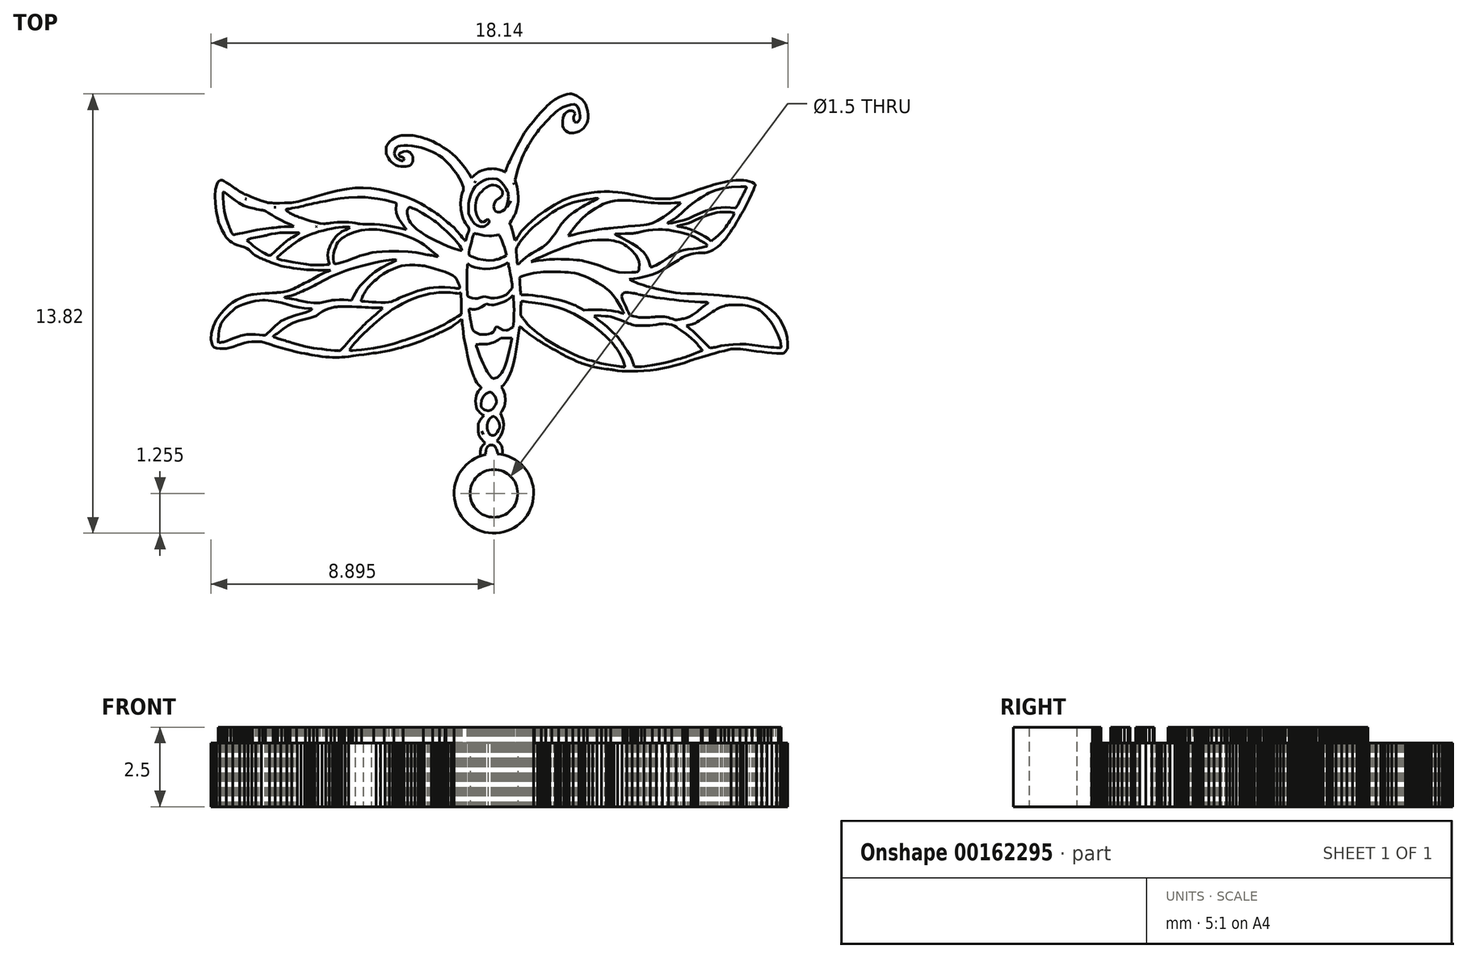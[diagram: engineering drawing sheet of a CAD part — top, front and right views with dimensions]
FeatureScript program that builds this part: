
annotation { "Feature Type Name" : "Feature", "Feature Type Description" : "" }
export const myFeature = defineFeature(function(context is Context, id is Id, definition is map)
    precondition{}
    {
        {
            var Q0;
            Q0=qCreatedBy(makeId("Top.planeOp"),FACE);
            var sketch = newSketch(context, id + "F0", { "sketchPlane" : qUnion([Q0])});
            skLineSegment(sketch, "E0", {"start": v(-0.39, -5.84) * mm, "end": v(-0.43, -5.8) * mm});
            skLineSegment(sketch, "E1", {"start": v(-0.43, -5.8) * mm, "end": v(-0.48, -5.76) * mm});
            skLineSegment(sketch, "E2", {"start": v(-0.48, -5.76) * mm, "end": v(-0.52, -5.71) * mm});
            skLineSegment(sketch, "E3", {"start": v(-0.52, -5.71) * mm, "end": v(-0.56, -5.66) * mm});
            skLineSegment(sketch, "E4", {"start": v(-0.56, -5.66) * mm, "end": v(-0.6, -5.53) * mm});
            skLineSegment(sketch, "E5", {"start": v(-0.6, -5.53) * mm, "end": v(-0.6, -5.4) * mm});
            skLineSegment(sketch, "E6", {"start": v(-0.6, -5.4) * mm, "end": v(-0.57, -5.28) * mm});
            skLineSegment(sketch, "E7", {"start": v(-0.57, -5.28) * mm, "end": v(-0.5, -5.18) * mm});
            skLineSegment(sketch, "E8", {"start": v(-0.5, -5.18) * mm, "end": v(-0.45, -5.13) * mm});
            skLineSegment(sketch, "E9", {"start": v(-0.45, -5.13) * mm, "end": v(-0.5, -5.07) * mm});
            skLineSegment(sketch, "E10", {"start": v(-0.5, -5.07) * mm, "end": v(-0.56, -5.02) * mm});
            skLineSegment(sketch, "E11", {"start": v(-0.56, -5.02) * mm, "end": v(-0.6, -4.96) * mm});
            skLineSegment(sketch, "E12", {"start": v(-0.6, -4.96) * mm, "end": v(-0.63, -4.9) * mm});
            skLineSegment(sketch, "E13", {"start": v(-0.63, -4.9) * mm, "end": v(-0.65, -4.86) * mm});
            skLineSegment(sketch, "E14", {"start": v(-0.65, -4.86) * mm, "end": v(-0.66, -4.83) * mm});
            skLineSegment(sketch, "E15", {"start": v(-0.66, -4.83) * mm, "end": v(-0.66, -4.79) * mm});
            skLineSegment(sketch, "E16", {"start": v(-0.66, -4.79) * mm, "end": v(-0.66, -4.73) * mm});
            skLineSegment(sketch, "E17", {"start": v(-0.66, -4.73) * mm, "end": v(-0.67, -4.66) * mm});
            skLineSegment(sketch, "E18", {"start": v(-0.67, -4.66) * mm, "end": v(-0.66, -4.61) * mm});
            skLineSegment(sketch, "E19", {"start": v(-0.66, -4.61) * mm, "end": v(-0.66, -4.57) * mm});
            skLineSegment(sketch, "E20", {"start": v(-0.66, -4.57) * mm, "end": v(-0.66, -4.54) * mm});
            skLineSegment(sketch, "E21", {"start": v(-0.66, -4.54) * mm, "end": v(-0.66, -4.52) * mm});
            skLineSegment(sketch, "E22", {"start": v(-0.66, -4.52) * mm, "end": v(-0.66, -4.5) * mm});
            skLineSegment(sketch, "E23", {"start": v(-0.66, -4.5) * mm, "end": v(-0.65, -4.48) * mm});
            skLineSegment(sketch, "E24", {"start": v(-0.65, -4.48) * mm, "end": v(-0.64, -4.47) * mm});
            skLineSegment(sketch, "E25", {"start": v(-0.64, -4.47) * mm, "end": v(-0.63, -4.45) * mm});
            skLineSegment(sketch, "E26", {"start": v(-0.63, -4.45) * mm, "end": v(-0.62, -4.42) * mm});
            skLineSegment(sketch, "E27", {"start": v(-0.62, -4.42) * mm, "end": v(-0.6, -4.39) * mm});
            skLineSegment(sketch, "E28", {"start": v(-0.6, -4.39) * mm, "end": v(-0.57, -4.36) * mm});
            skLineSegment(sketch, "E29", {"start": v(-0.57, -4.36) * mm, "end": v(-0.55, -4.33) * mm});
            skLineSegment(sketch, "E30", {"start": v(-0.55, -4.33) * mm, "end": v(-0.53, -4.3) * mm});
            skLineSegment(sketch, "E31", {"start": v(-0.53, -4.3) * mm, "end": v(-0.5, -4.3) * mm});
            skLineSegment(sketch, "E32", {"start": v(-0.5, -4.3) * mm, "end": v(-0.5, -4.28) * mm});
            skLineSegment(sketch, "E33", {"start": v(-0.5, -4.28) * mm, "end": v(-0.5, -4.27) * mm});
            skLineSegment(sketch, "E34", {"start": v(-0.5, -4.27) * mm, "end": v(-0.5, -4.26) * mm});
            skLineSegment(sketch, "E35", {"start": v(-0.5, -4.26) * mm, "end": v(-0.53, -4.24) * mm});
            skLineSegment(sketch, "E36", {"start": v(-0.53, -4.24) * mm, "end": v(-0.55, -4.22) * mm});
            skLineSegment(sketch, "E37", {"start": v(-0.55, -4.22) * mm, "end": v(-0.58, -4.2) * mm});
            skLineSegment(sketch, "E38", {"start": v(-0.58, -4.2) * mm, "end": v(-0.61, -4.17) * mm});
            skLineSegment(sketch, "E39", {"start": v(-0.61, -4.17) * mm, "end": v(-0.64, -4.15) * mm});
            skLineSegment(sketch, "E40", {"start": v(-0.64, -4.15) * mm, "end": v(-0.68, -4.1) * mm});
            skLineSegment(sketch, "E41", {"start": v(-0.68, -4.1) * mm, "end": v(-0.7, -4.08) * mm});
            skLineSegment(sketch, "E42", {"start": v(-0.7, -4.08) * mm, "end": v(-0.72, -4.04) * mm});
            skLineSegment(sketch, "E43", {"start": v(-0.72, -4.04) * mm, "end": v(-0.74, -4) * mm});
            skLineSegment(sketch, "E44", {"start": v(-0.74, -4) * mm, "end": v(-0.76, -3.81) * mm});
            skLineSegment(sketch, "E45", {"start": v(-0.76, -3.81) * mm, "end": v(-0.73, -3.65) * mm});
            skLineSegment(sketch, "E46", {"start": v(-0.73, -3.65) * mm, "end": v(-0.7, -3.58) * mm});
            skLineSegment(sketch, "E47", {"start": v(-0.7, -3.58) * mm, "end": v(-0.67, -3.51) * mm});
            skLineSegment(sketch, "E48", {"start": v(-0.67, -3.51) * mm, "end": v(-0.63, -3.46) * mm});
            skLineSegment(sketch, "E49", {"start": v(-0.63, -3.46) * mm, "end": v(-0.6, -3.43) * mm});
            skLineSegment(sketch, "E50", {"start": v(-0.6, -3.43) * mm, "end": v(-0.58, -3.4) * mm});
            skLineSegment(sketch, "E51", {"start": v(-0.58, -3.4) * mm, "end": v(-0.57, -3.4) * mm});
            skLineSegment(sketch, "E52", {"start": v(-0.57, -3.4) * mm, "end": v(-0.59, -3.37) * mm});
            skLineSegment(sketch, "E53", {"start": v(-0.59, -3.37) * mm, "end": v(-0.62, -3.34) * mm});
            skLineSegment(sketch, "E54", {"start": v(-0.62, -3.34) * mm, "end": v(-0.67, -3.3) * mm});
            skLineSegment(sketch, "E55", {"start": v(-0.67, -3.3) * mm, "end": v(-0.71, -3.23) * mm});
            skLineSegment(sketch, "E56", {"start": v(-0.71, -3.23) * mm, "end": v(-0.75, -3.16) * mm});
            skLineSegment(sketch, "E57", {"start": v(-0.75, -3.16) * mm, "end": v(-0.79, -3.1) * mm});
            skLineSegment(sketch, "E58", {"start": v(-0.79, -3.1) * mm, "end": v(-0.8, -3.05) * mm});
            skLineSegment(sketch, "E59", {"start": v(-0.8, -3.05) * mm, "end": v(-0.82, -3) * mm});
            skLineSegment(sketch, "E60", {"start": v(-0.82, -3) * mm, "end": v(-0.84, -2.95) * mm});
            skLineSegment(sketch, "E61", {"start": v(-0.84, -2.95) * mm, "end": v(-0.86, -2.9) * mm});
            skLineSegment(sketch, "E62", {"start": v(-0.86, -2.9) * mm, "end": v(-0.9, -2.8) * mm});
            skLineSegment(sketch, "E63", {"start": v(-0.9, -2.8) * mm, "end": v(-0.93, -2.68) * mm});
            skLineSegment(sketch, "E64", {"start": v(-0.93, -2.68) * mm, "end": v(-0.96, -2.54) * mm});
            skLineSegment(sketch, "E65", {"start": v(-0.96, -2.54) * mm, "end": v(-1, -2.36) * mm});
            skLineSegment(sketch, "E66", {"start": v(-1, -2.36) * mm, "end": v(-1.03, -2.21) * mm});
            skLineSegment(sketch, "E67", {"start": v(-1.03, -2.21) * mm, "end": v(-1.06, -2.08) * mm});
            skLineSegment(sketch, "E68", {"start": v(-1.06, -2.08) * mm, "end": v(-1.12, -1.8) * mm});
            skLineSegment(sketch, "E69", {"start": v(-1.12, -1.8) * mm, "end": v(-1.15, -1.51) * mm});
            skLineSegment(sketch, "E70", {"start": v(-1.15, -1.51) * mm, "end": v(-1.16, -1.44) * mm});
            skLineSegment(sketch, "E71", {"start": v(-1.16, -1.44) * mm, "end": v(-1.17, -1.37) * mm});
            skLineSegment(sketch, "E72", {"start": v(-1.17, -1.37) * mm, "end": v(-1.17, -1.31) * mm});
            skLineSegment(sketch, "E73", {"start": v(-1.17, -1.31) * mm, "end": v(-1.18, -1.28) * mm});
            skLineSegment(sketch, "E74", {"start": v(-1.18, -1.28) * mm, "end": v(-1.18, -1.23) * mm});
            skLineSegment(sketch, "E75", {"start": v(-1.18, -1.23) * mm, "end": v(-1.22, -1.26) * mm});
            skLineSegment(sketch, "E76", {"start": v(-1.22, -1.26) * mm, "end": v(-1.3, -1.32) * mm});
            skLineSegment(sketch, "E77", {"start": v(-1.3, -1.32) * mm, "end": v(-1.4, -1.4) * mm});
            skLineSegment(sketch, "E78", {"start": v(-1.4, -1.4) * mm, "end": v(-1.52, -1.48) * mm});
            skLineSegment(sketch, "E79", {"start": v(-1.52, -1.48) * mm, "end": v(-1.62, -1.54) * mm});
            skLineSegment(sketch, "E80", {"start": v(-1.62, -1.54) * mm, "end": v(-1.67, -1.57) * mm});
            skLineSegment(sketch, "E81", {"start": v(-1.67, -1.57) * mm, "end": v(-1.72, -1.6) * mm});
            skLineSegment(sketch, "E82", {"start": v(-1.72, -1.6) * mm, "end": v(-1.77, -1.62) * mm});
            skLineSegment(sketch, "E83", {"start": v(-1.77, -1.62) * mm, "end": v(-1.82, -1.64) * mm});
            skLineSegment(sketch, "E84", {"start": v(-1.82, -1.64) * mm, "end": v(-1.87, -1.66) * mm});
            skLineSegment(sketch, "E85", {"start": v(-1.87, -1.66) * mm, "end": v(-1.91, -1.68) * mm});
            skLineSegment(sketch, "E86", {"start": v(-1.91, -1.68) * mm, "end": v(-1.96, -1.7) * mm});
            skLineSegment(sketch, "E87", {"start": v(-1.96, -1.7) * mm, "end": v(-2, -1.72) * mm});
            skLineSegment(sketch, "E88", {"start": v(-2, -1.72) * mm, "end": v(-2.04, -1.74) * mm});
            skLineSegment(sketch, "E89", {"start": v(-2.04, -1.74) * mm, "end": v(-2.09, -1.76) * mm});
            skLineSegment(sketch, "E90", {"start": v(-2.09, -1.76) * mm, "end": v(-2.14, -1.79) * mm});
            skLineSegment(sketch, "E91", {"start": v(-2.14, -1.79) * mm, "end": v(-2.2, -1.8) * mm});
            skLineSegment(sketch, "E92", {"start": v(-2.2, -1.8) * mm, "end": v(-2.26, -1.83) * mm});
            skLineSegment(sketch, "E93", {"start": v(-2.26, -1.83) * mm, "end": v(-2.32, -1.86) * mm});
            skLineSegment(sketch, "E94", {"start": v(-2.32, -1.86) * mm, "end": v(-2.37, -1.88) * mm});
            skLineSegment(sketch, "E95", {"start": v(-2.37, -1.88) * mm, "end": v(-2.42, -1.9) * mm});
            skLineSegment(sketch, "E96", {"start": v(-2.42, -1.9) * mm, "end": v(-2.48, -1.93) * mm});
            skLineSegment(sketch, "E97", {"start": v(-2.48, -1.93) * mm, "end": v(-2.56, -1.96) * mm});
            skLineSegment(sketch, "E98", {"start": v(-2.56, -1.96) * mm, "end": v(-2.67, -2) * mm});
            skLineSegment(sketch, "E99", {"start": v(-2.67, -2) * mm, "end": v(-2.78, -2.03) * mm});
            skLineSegment(sketch, "E100", {"start": v(-2.78, -2.03) * mm, "end": v(-2.89, -2.07) * mm});
            skLineSegment(sketch, "E101", {"start": v(-2.89, -2.07) * mm, "end": v(-3, -2.1) * mm});
            skLineSegment(sketch, "E102", {"start": v(-3, -2.1) * mm, "end": v(-3.1, -2.13) * mm});
            skLineSegment(sketch, "E103", {"start": v(-3.1, -2.13) * mm, "end": v(-3.18, -2.15) * mm});
            skLineSegment(sketch, "E104", {"start": v(-3.18, -2.15) * mm, "end": v(-3.22, -2.16) * mm});
            skLineSegment(sketch, "E105", {"start": v(-3.22, -2.16) * mm, "end": v(-3.27, -2.17) * mm});
            skLineSegment(sketch, "E106", {"start": v(-3.27, -2.17) * mm, "end": v(-3.31, -2.18) * mm});
            skLineSegment(sketch, "E107", {"start": v(-3.31, -2.18) * mm, "end": v(-3.35, -2.2) * mm});
            skLineSegment(sketch, "E108", {"start": v(-3.35, -2.2) * mm, "end": v(-3.46, -2.22) * mm});
            skLineSegment(sketch, "E109", {"start": v(-3.46, -2.22) * mm, "end": v(-3.6, -2.25) * mm});
            skLineSegment(sketch, "E110", {"start": v(-3.6, -2.25) * mm, "end": v(-3.74, -2.27) * mm});
            skLineSegment(sketch, "E111", {"start": v(-3.74, -2.27) * mm, "end": v(-3.88, -2.3) * mm});
            skLineSegment(sketch, "E112", {"start": v(-3.88, -2.3) * mm, "end": v(-3.97, -2.3) * mm});
            skLineSegment(sketch, "E113", {"start": v(-3.97, -2.3) * mm, "end": v(-4.1, -2.32) * mm});
            skLineSegment(sketch, "E114", {"start": v(-4.1, -2.32) * mm, "end": v(-4.26, -2.34) * mm});
            skLineSegment(sketch, "E115", {"start": v(-4.26, -2.34) * mm, "end": v(-4.43, -2.37) * mm});
            skLineSegment(sketch, "E116", {"start": v(-4.43, -2.37) * mm, "end": v(-4.6, -2.4) * mm});
            skLineSegment(sketch, "E117", {"start": v(-4.6, -2.4) * mm, "end": v(-4.74, -2.4) * mm});
            skLineSegment(sketch, "E118", {"start": v(-4.74, -2.4) * mm, "end": v(-4.86, -2.42) * mm});
            skLineSegment(sketch, "E119", {"start": v(-4.86, -2.42) * mm, "end": v(-4.95, -2.43) * mm});
            skLineSegment(sketch, "E120", {"start": v(-4.95, -2.43) * mm, "end": v(-5.03, -2.44) * mm});
            skLineSegment(sketch, "E121", {"start": v(-5.03, -2.44) * mm, "end": v(-5.1, -2.44) * mm});
            skLineSegment(sketch, "E122", {"start": v(-5.1, -2.44) * mm, "end": v(-5.18, -2.44) * mm});
            skLineSegment(sketch, "E123", {"start": v(-5.18, -2.44) * mm, "end": v(-5.25, -2.44) * mm});
            skLineSegment(sketch, "E124", {"start": v(-5.25, -2.44) * mm, "end": v(-5.35, -2.43) * mm});
            skLineSegment(sketch, "E125", {"start": v(-5.35, -2.43) * mm, "end": v(-5.46, -2.42) * mm});
            skLineSegment(sketch, "E126", {"start": v(-5.46, -2.42) * mm, "end": v(-5.58, -2.4) * mm});
            skLineSegment(sketch, "E127", {"start": v(-5.58, -2.4) * mm, "end": v(-5.7, -2.4) * mm});
            skLineSegment(sketch, "E128", {"start": v(-5.7, -2.4) * mm, "end": v(-5.8, -2.38) * mm});
            skLineSegment(sketch, "E129", {"start": v(-5.8, -2.38) * mm, "end": v(-5.9, -2.36) * mm});
            skLineSegment(sketch, "E130", {"start": v(-5.9, -2.36) * mm, "end": v(-5.97, -2.35) * mm});
            skLineSegment(sketch, "E131", {"start": v(-5.97, -2.35) * mm, "end": v(-6, -2.34) * mm});
            skLineSegment(sketch, "E132", {"start": v(-6, -2.34) * mm, "end": v(-6.02, -2.34) * mm});
            skLineSegment(sketch, "E133", {"start": v(-6.02, -2.34) * mm, "end": v(-6.04, -2.33) * mm});
            skLineSegment(sketch, "E134", {"start": v(-6.04, -2.33) * mm, "end": v(-6.08, -2.32) * mm});
            skLineSegment(sketch, "E135", {"start": v(-6.08, -2.32) * mm, "end": v(-6.13, -2.32) * mm});
            skLineSegment(sketch, "E136", {"start": v(-6.13, -2.32) * mm, "end": v(-6.24, -2.3) * mm});
            skLineSegment(sketch, "E137", {"start": v(-6.24, -2.3) * mm, "end": v(-6.35, -2.27) * mm});
            skLineSegment(sketch, "E138", {"start": v(-6.35, -2.27) * mm, "end": v(-6.4, -2.26) * mm});
            skLineSegment(sketch, "E139", {"start": v(-6.4, -2.26) * mm, "end": v(-6.45, -2.25) * mm});
            skLineSegment(sketch, "E140", {"start": v(-6.45, -2.25) * mm, "end": v(-6.5, -2.23) * mm});
            skLineSegment(sketch, "E141", {"start": v(-6.5, -2.23) * mm, "end": v(-6.53, -2.23) * mm});
            skLineSegment(sketch, "E142", {"start": v(-6.53, -2.23) * mm, "end": v(-6.7, -2.19) * mm});
            skLineSegment(sketch, "E143", {"start": v(-6.7, -2.19) * mm, "end": v(-6.87, -2.14) * mm});
            skLineSegment(sketch, "E144", {"start": v(-6.87, -2.14) * mm, "end": v(-7.06, -2.08) * mm});
            skLineSegment(sketch, "E145", {"start": v(-7.06, -2.08) * mm, "end": v(-7.24, -2.02) * mm});
            skLineSegment(sketch, "E146", {"start": v(-7.24, -2.02) * mm, "end": v(-7.49, -1.94) * mm});
            skLineSegment(sketch, "E147", {"start": v(-7.49, -1.94) * mm, "end": v(-7.66, -1.94) * mm});
            skLineSegment(sketch, "E148", {"start": v(-7.66, -1.94) * mm, "end": v(-7.8, -1.94) * mm});
            skLineSegment(sketch, "E149", {"start": v(-7.8, -1.94) * mm, "end": v(-7.9, -1.96) * mm});
            skLineSegment(sketch, "E150", {"start": v(-7.9, -1.96) * mm, "end": v(-8.02, -1.98) * mm});
            skLineSegment(sketch, "E151", {"start": v(-8.02, -1.98) * mm, "end": v(-8.17, -2.03) * mm});
            skLineSegment(sketch, "E152", {"start": v(-8.17, -2.03) * mm, "end": v(-8.23, -2.05) * mm});
            skLineSegment(sketch, "E153", {"start": v(-8.23, -2.05) * mm, "end": v(-8.29, -2.07) * mm});
            skLineSegment(sketch, "E154", {"start": v(-8.29, -2.07) * mm, "end": v(-8.35, -2.1) * mm});
            skLineSegment(sketch, "E155", {"start": v(-8.35, -2.1) * mm, "end": v(-8.39, -2.1) * mm});
            skLineSegment(sketch, "E156", {"start": v(-8.39, -2.1) * mm, "end": v(-8.6, -2.16) * mm});
            skLineSegment(sketch, "E157", {"start": v(-8.6, -2.16) * mm, "end": v(-8.8, -2.16) * mm});
            skLineSegment(sketch, "E158", {"start": v(-8.8, -2.16) * mm, "end": v(-8.9, -2.15) * mm});
            skLineSegment(sketch, "E159", {"start": v(-8.9, -2.15) * mm, "end": v(-8.97, -2.12) * mm});
            skLineSegment(sketch, "E160", {"start": v(-8.97, -2.12) * mm, "end": v(-9, -2.09) * mm});
            skLineSegment(sketch, "E161", {"start": v(-9, -2.09) * mm, "end": v(-9.04, -2.04) * mm});
            skLineSegment(sketch, "E162", {"start": v(-9.04, -2.04) * mm, "end": v(-9.07, -1.87) * mm});
            skLineSegment(sketch, "E163", {"start": v(-9.07, -1.87) * mm, "end": v(-9.05, -1.67) * mm});
            skLineSegment(sketch, "E164", {"start": v(-9.05, -1.67) * mm, "end": v(-9, -1.46) * mm});
            skLineSegment(sketch, "E165", {"start": v(-9, -1.46) * mm, "end": v(-8.9, -1.26) * mm});
            skLineSegment(sketch, "E166", {"start": v(-8.9, -1.26) * mm, "end": v(-8.86, -1.2) * mm});
            skLineSegment(sketch, "E167", {"start": v(-8.86, -1.2) * mm, "end": v(-8.8, -1.12) * mm});
            skLineSegment(sketch, "E168", {"start": v(-8.8, -1.12) * mm, "end": v(-8.74, -1.04) * mm});
            skLineSegment(sketch, "E169", {"start": v(-8.74, -1.04) * mm, "end": v(-8.67, -0.96) * mm});
            skLineSegment(sketch, "E170", {"start": v(-8.67, -0.96) * mm, "end": v(-8.6, -0.88) * mm});
            skLineSegment(sketch, "E171", {"start": v(-8.6, -0.88) * mm, "end": v(-8.52, -0.8) * mm});
            skLineSegment(sketch, "E172", {"start": v(-8.52, -0.8) * mm, "end": v(-8.45, -0.75) * mm});
            skLineSegment(sketch, "E173", {"start": v(-8.45, -0.75) * mm, "end": v(-8.4, -0.7) * mm});
            skLineSegment(sketch, "E174", {"start": v(-8.4, -0.7) * mm, "end": v(-8.27, -0.64) * mm});
            skLineSegment(sketch, "E175", {"start": v(-8.27, -0.64) * mm, "end": v(-8.1, -0.56) * mm});
            skLineSegment(sketch, "E176", {"start": v(-8.1, -0.56) * mm, "end": v(-7.94, -0.5) * mm});
            skLineSegment(sketch, "E177", {"start": v(-7.94, -0.5) * mm, "end": v(-7.78, -0.46) * mm});
            skLineSegment(sketch, "E178", {"start": v(-7.78, -0.46) * mm, "end": v(-7.72, -0.45) * mm});
            skLineSegment(sketch, "E179", {"start": v(-7.72, -0.45) * mm, "end": v(-7.63, -0.44) * mm});
            skLineSegment(sketch, "E180", {"start": v(-7.63, -0.44) * mm, "end": v(-7.51, -0.43) * mm});
            skLineSegment(sketch, "E181", {"start": v(-7.51, -0.43) * mm, "end": v(-7.38, -0.43) * mm});
            skLineSegment(sketch, "E182", {"start": v(-7.38, -0.43) * mm, "end": v(-7.25, -0.42) * mm});
            skLineSegment(sketch, "E183", {"start": v(-7.25, -0.42) * mm, "end": v(-7.14, -0.41) * mm});
            skLineSegment(sketch, "E184", {"start": v(-7.14, -0.41) * mm, "end": v(-7.07, -0.4) * mm});
            skLineSegment(sketch, "E185", {"start": v(-7.07, -0.4) * mm, "end": v(-7.04, -0.4) * mm});
            skLineSegment(sketch, "E186", {"start": v(-7.04, -0.4) * mm, "end": v(-7.02, -0.4) * mm});
            skLineSegment(sketch, "E187", {"start": v(-7.02, -0.4) * mm, "end": v(-6.98, -0.4) * mm});
            skLineSegment(sketch, "E188", {"start": v(-6.98, -0.4) * mm, "end": v(-6.94, -0.4) * mm});
            skLineSegment(sketch, "E189", {"start": v(-6.94, -0.4) * mm, "end": v(-6.88, -0.39) * mm});
            skLineSegment(sketch, "E190", {"start": v(-6.88, -0.39) * mm, "end": v(-6.8, -0.38) * mm});
            skLineSegment(sketch, "E191", {"start": v(-6.8, -0.38) * mm, "end": v(-6.74, -0.37) * mm});
            skLineSegment(sketch, "E192", {"start": v(-6.74, -0.37) * mm, "end": v(-6.68, -0.36) * mm});
            skLineSegment(sketch, "E193", {"start": v(-6.68, -0.36) * mm, "end": v(-6.6, -0.33) * mm});
            skLineSegment(sketch, "E194", {"start": v(-6.6, -0.33) * mm, "end": v(-6.55, -0.3) * mm});
            skLineSegment(sketch, "E195", {"start": v(-6.55, -0.3) * mm, "end": v(-6.47, -0.28) * mm});
            skLineSegment(sketch, "E196", {"start": v(-6.47, -0.28) * mm, "end": v(-6.4, -0.25) * mm});
            skLineSegment(sketch, "E197", {"start": v(-6.4, -0.25) * mm, "end": v(-6.34, -0.21) * mm});
            skLineSegment(sketch, "E198", {"start": v(-6.34, -0.21) * mm, "end": v(-6.27, -0.18) * mm});
            skLineSegment(sketch, "E199", {"start": v(-6.27, -0.18) * mm, "end": v(-6.2, -0.14) * mm});
            skLineSegment(sketch, "E200", {"start": v(-6.2, -0.14) * mm, "end": v(-6.13, -0.1) * mm});
            skLineSegment(sketch, "E201", {"start": v(-6.13, -0.1) * mm, "end": v(-6.08, -0.08) * mm});
            skLineSegment(sketch, "E202", {"start": v(-6.08, -0.08) * mm, "end": v(-6.02, -0.05) * mm});
            skLineSegment(sketch, "E203", {"start": v(-6.02, -0.05) * mm, "end": v(-5.95, 0) * mm});
            skLineSegment(sketch, "E204", {"start": v(-5.95, 0) * mm, "end": v(-5.88, 0.03) * mm});
            skLineSegment(sketch, "E205", {"start": v(-5.88, 0.03) * mm, "end": v(-5.8, 0.07) * mm});
            skLineSegment(sketch, "E206", {"start": v(-5.8, 0.07) * mm, "end": v(-5.69, 0.13) * mm});
            skLineSegment(sketch, "E207", {"start": v(-5.69, 0.13) * mm, "end": v(-5.58, 0.19) * mm});
            skLineSegment(sketch, "E208", {"start": v(-5.58, 0.19) * mm, "end": v(-5.48, 0.23) * mm});
            skLineSegment(sketch, "E209", {"start": v(-5.48, 0.23) * mm, "end": v(-5.4, 0.27) * mm});
            skLineSegment(sketch, "E210", {"start": v(-5.4, 0.27) * mm, "end": v(-5.36, 0.28) * mm});
            skLineSegment(sketch, "E211", {"start": v(-5.36, 0.28) * mm, "end": v(-5.34, 0.29) * mm});
            skLineSegment(sketch, "E212", {"start": v(-5.34, 0.29) * mm, "end": v(-5.32, 0.3) * mm});
            skLineSegment(sketch, "E213", {"start": v(-5.32, 0.3) * mm, "end": v(-5.32, 0.3) * mm});
            skLineSegment(sketch, "E214", {"start": v(-5.32, 0.3) * mm, "end": v(-5.34, 0.3) * mm});
            skLineSegment(sketch, "E215", {"start": v(-5.34, 0.3) * mm, "end": v(-5.4, 0.3) * mm});
            skLineSegment(sketch, "E216", {"start": v(-5.4, 0.3) * mm, "end": v(-5.48, 0.3) * mm});
            skLineSegment(sketch, "E217", {"start": v(-5.48, 0.3) * mm, "end": v(-5.6, 0.3) * mm});
            skLineSegment(sketch, "E218", {"start": v(-5.6, 0.3) * mm, "end": v(-5.71, 0.3) * mm});
            skLineSegment(sketch, "E219", {"start": v(-5.71, 0.3) * mm, "end": v(-5.84, 0.31) * mm});
            skLineSegment(sketch, "E220", {"start": v(-5.84, 0.31) * mm, "end": v(-5.96, 0.32) * mm});
            skLineSegment(sketch, "E221", {"start": v(-5.96, 0.32) * mm, "end": v(-6.06, 0.32) * mm});
            skLineSegment(sketch, "E222", {"start": v(-6.06, 0.32) * mm, "end": v(-6.15, 0.33) * mm});
            skLineSegment(sketch, "E223", {"start": v(-6.15, 0.33) * mm, "end": v(-6.26, 0.34) * mm});
            skLineSegment(sketch, "E224", {"start": v(-6.26, 0.34) * mm, "end": v(-6.37, 0.35) * mm});
            skLineSegment(sketch, "E225", {"start": v(-6.37, 0.35) * mm, "end": v(-6.48, 0.37) * mm});
            skLineSegment(sketch, "E226", {"start": v(-6.48, 0.37) * mm, "end": v(-6.6, 0.39) * mm});
            skLineSegment(sketch, "E227", {"start": v(-6.6, 0.39) * mm, "end": v(-6.7, 0.4) * mm});
            skLineSegment(sketch, "E228", {"start": v(-6.7, 0.4) * mm, "end": v(-6.78, 0.42) * mm});
            skLineSegment(sketch, "E229", {"start": v(-6.78, 0.42) * mm, "end": v(-6.84, 0.43) * mm});
            skLineSegment(sketch, "E230", {"start": v(-6.84, 0.43) * mm, "end": v(-6.89, 0.45) * mm});
            skLineSegment(sketch, "E231", {"start": v(-6.89, 0.45) * mm, "end": v(-6.95, 0.47) * mm});
            skLineSegment(sketch, "E232", {"start": v(-6.95, 0.47) * mm, "end": v(-7.03, 0.5) * mm});
            skLineSegment(sketch, "E233", {"start": v(-7.03, 0.5) * mm, "end": v(-7.1, 0.52) * mm});
            skLineSegment(sketch, "E234", {"start": v(-7.1, 0.52) * mm, "end": v(-7.18, 0.55) * mm});
            skLineSegment(sketch, "E235", {"start": v(-7.18, 0.55) * mm, "end": v(-7.25, 0.58) * mm});
            skLineSegment(sketch, "E236", {"start": v(-7.25, 0.58) * mm, "end": v(-7.31, 0.6) * mm});
            skLineSegment(sketch, "E237", {"start": v(-7.31, 0.6) * mm, "end": v(-7.35, 0.62) * mm});
            skLineSegment(sketch, "E238", {"start": v(-7.35, 0.62) * mm, "end": v(-7.39, 0.63) * mm});
            skLineSegment(sketch, "E239", {"start": v(-7.39, 0.63) * mm, "end": v(-7.43, 0.65) * mm});
            skLineSegment(sketch, "E240", {"start": v(-7.43, 0.65) * mm, "end": v(-7.48, 0.67) * mm});
            skLineSegment(sketch, "E241", {"start": v(-7.48, 0.67) * mm, "end": v(-7.52, 0.69) * mm});
            skLineSegment(sketch, "E242", {"start": v(-7.52, 0.69) * mm, "end": v(-7.61, 0.73) * mm});
            skLineSegment(sketch, "E243", {"start": v(-7.61, 0.73) * mm, "end": v(-7.68, 0.77) * mm});
            skLineSegment(sketch, "E244", {"start": v(-7.68, 0.77) * mm, "end": v(-7.75, 0.82) * mm});
            skLineSegment(sketch, "E245", {"start": v(-7.75, 0.82) * mm, "end": v(-7.81, 0.88) * mm});
            skLineSegment(sketch, "E246", {"start": v(-7.81, 0.88) * mm, "end": v(-7.88, 0.95) * mm});
            skLineSegment(sketch, "E247", {"start": v(-7.88, 0.95) * mm, "end": v(-7.94, 0.99) * mm});
            skLineSegment(sketch, "E248", {"start": v(-7.94, 0.99) * mm, "end": v(-8.02, 1.02) * mm});
            skLineSegment(sketch, "E249", {"start": v(-8.02, 1.02) * mm, "end": v(-8.14, 1.06) * mm});
            skLineSegment(sketch, "E250", {"start": v(-8.14, 1.06) * mm, "end": v(-8.24, 1.1) * mm});
            skLineSegment(sketch, "E251", {"start": v(-8.24, 1.1) * mm, "end": v(-8.33, 1.13) * mm});
            skLineSegment(sketch, "E252", {"start": v(-8.33, 1.13) * mm, "end": v(-8.41, 1.18) * mm});
            skLineSegment(sketch, "E253", {"start": v(-8.41, 1.18) * mm, "end": v(-8.48, 1.22) * mm});
            skLineSegment(sketch, "E254", {"start": v(-8.48, 1.22) * mm, "end": v(-8.54, 1.28) * mm});
            skLineSegment(sketch, "E255", {"start": v(-8.54, 1.28) * mm, "end": v(-8.6, 1.35) * mm});
            skLineSegment(sketch, "E256", {"start": v(-8.6, 1.35) * mm, "end": v(-8.66, 1.45) * mm});
            skLineSegment(sketch, "E257", {"start": v(-8.66, 1.45) * mm, "end": v(-8.73, 1.57) * mm});
            skLineSegment(sketch, "E258", {"start": v(-8.73, 1.57) * mm, "end": v(-8.76, 1.64) * mm});
            skLineSegment(sketch, "E259", {"start": v(-8.76, 1.64) * mm, "end": v(-8.79, 1.7) * mm});
            skLineSegment(sketch, "E260", {"start": v(-8.79, 1.7) * mm, "end": v(-8.8, 1.75) * mm});
            skLineSegment(sketch, "E261", {"start": v(-8.8, 1.75) * mm, "end": v(-8.83, 1.8) * mm});
            skLineSegment(sketch, "E262", {"start": v(-8.83, 1.8) * mm, "end": v(-8.84, 1.87) * mm});
            skLineSegment(sketch, "E263", {"start": v(-8.84, 1.87) * mm, "end": v(-8.86, 1.95) * mm});
            skLineSegment(sketch, "E264", {"start": v(-8.86, 1.95) * mm, "end": v(-8.88, 2.05) * mm});
            skLineSegment(sketch, "E265", {"start": v(-8.88, 2.05) * mm, "end": v(-8.9, 2.17) * mm});
            skLineSegment(sketch, "E266", {"start": v(-8.9, 2.17) * mm, "end": v(-8.94, 2.41) * mm});
            skLineSegment(sketch, "E267", {"start": v(-8.94, 2.41) * mm, "end": v(-8.95, 2.64) * mm});
            skLineSegment(sketch, "E268", {"start": v(-8.95, 2.64) * mm, "end": v(-8.93, 2.84) * mm});
            skLineSegment(sketch, "E269", {"start": v(-8.93, 2.84) * mm, "end": v(-8.89, 3) * mm});
            skLineSegment(sketch, "E270", {"start": v(-8.89, 3) * mm, "end": v(-8.85, 3.07) * mm});
            skLineSegment(sketch, "E271", {"start": v(-8.85, 3.07) * mm, "end": v(-8.82, 3.11) * mm});
            skLineSegment(sketch, "E272", {"start": v(-8.82, 3.11) * mm, "end": v(-8.78, 3.13) * mm});
            skLineSegment(sketch, "E273", {"start": v(-8.78, 3.13) * mm, "end": v(-8.72, 3.13) * mm});
            skLineSegment(sketch, "E274", {"start": v(-8.72, 3.13) * mm, "end": v(-8.67, 3.1) * mm});
            skLineSegment(sketch, "E275", {"start": v(-8.67, 3.1) * mm, "end": v(-8.59, 3.06) * mm});
            skLineSegment(sketch, "E276", {"start": v(-8.59, 3.06) * mm, "end": v(-8.48, 3) * mm});
            skLineSegment(sketch, "E277", {"start": v(-8.48, 3) * mm, "end": v(-8.37, 2.92) * mm});
            skLineSegment(sketch, "E278", {"start": v(-8.37, 2.92) * mm, "end": v(-8.33, 2.89) * mm});
            skLineSegment(sketch, "E279", {"start": v(-8.33, 2.89) * mm, "end": v(-8.28, 2.85) * mm});
            skLineSegment(sketch, "E280", {"start": v(-8.28, 2.85) * mm, "end": v(-8.22, 2.82) * mm});
            skLineSegment(sketch, "E281", {"start": v(-8.22, 2.82) * mm, "end": v(-8.17, 2.78) * mm});
            skLineSegment(sketch, "E282", {"start": v(-8.17, 2.78) * mm, "end": v(-8.12, 2.75) * mm});
            skLineSegment(sketch, "E283", {"start": v(-8.12, 2.75) * mm, "end": v(-8.07, 2.72) * mm});
            skLineSegment(sketch, "E284", {"start": v(-8.07, 2.72) * mm, "end": v(-8.04, 2.7) * mm});
            skLineSegment(sketch, "E285", {"start": v(-8.04, 2.7) * mm, "end": v(-8.02, 2.7) * mm});
            skLineSegment(sketch, "E286", {"start": v(-8.02, 2.7) * mm, "end": v(-8, 2.7) * mm});
            skLineSegment(sketch, "E287", {"start": v(-8, 2.7) * mm, "end": v(-7.96, 2.67) * mm});
            skLineSegment(sketch, "E288", {"start": v(-7.96, 2.67) * mm, "end": v(-7.9, 2.65) * mm});
            skLineSegment(sketch, "E289", {"start": v(-7.9, 2.65) * mm, "end": v(-7.82, 2.61) * mm});
            skLineSegment(sketch, "E290", {"start": v(-7.82, 2.61) * mm, "end": v(-7.7, 2.56) * mm});
            skLineSegment(sketch, "E291", {"start": v(-7.7, 2.56) * mm, "end": v(-7.6, 2.52) * mm});
            skLineSegment(sketch, "E292", {"start": v(-7.6, 2.52) * mm, "end": v(-7.49, 2.49) * mm});
            skLineSegment(sketch, "E293", {"start": v(-7.49, 2.49) * mm, "end": v(-7.35, 2.45) * mm});
            skLineSegment(sketch, "E294", {"start": v(-7.35, 2.45) * mm, "end": v(-7.3, 2.44) * mm});
            skLineSegment(sketch, "E295", {"start": v(-7.3, 2.44) * mm, "end": v(-7.28, 2.43) * mm});
            skLineSegment(sketch, "E296", {"start": v(-7.28, 2.43) * mm, "end": v(-7.24, 2.42) * mm});
            skLineSegment(sketch, "E297", {"start": v(-7.24, 2.42) * mm, "end": v(-7.2, 2.42) * mm});
            skLineSegment(sketch, "E298", {"start": v(-7.2, 2.42) * mm, "end": v(-7.16, 2.42) * mm});
            skLineSegment(sketch, "E299", {"start": v(-7.16, 2.42) * mm, "end": v(-7.1, 2.42) * mm});
            skLineSegment(sketch, "E300", {"start": v(-7.1, 2.42) * mm, "end": v(-7.02, 2.42) * mm});
            skLineSegment(sketch, "E301", {"start": v(-7.02, 2.42) * mm, "end": v(-6.92, 2.42) * mm});
            skLineSegment(sketch, "E302", {"start": v(-6.92, 2.42) * mm, "end": v(-6.76, 2.42) * mm});
            skLineSegment(sketch, "E303", {"start": v(-6.76, 2.42) * mm, "end": v(-6.64, 2.42) * mm});
            skLineSegment(sketch, "E304", {"start": v(-6.64, 2.42) * mm, "end": v(-6.55, 2.43) * mm});
            skLineSegment(sketch, "E305", {"start": v(-6.55, 2.43) * mm, "end": v(-6.48, 2.44) * mm});
            skLineSegment(sketch, "E306", {"start": v(-6.48, 2.44) * mm, "end": v(-6.34, 2.46) * mm});
            skLineSegment(sketch, "E307", {"start": v(-6.34, 2.46) * mm, "end": v(-6.16, 2.5) * mm});
            skLineSegment(sketch, "E308", {"start": v(-6.16, 2.5) * mm, "end": v(-5.96, 2.56) * mm});
            skLineSegment(sketch, "E309", {"start": v(-5.96, 2.56) * mm, "end": v(-5.76, 2.62) * mm});
            skLineSegment(sketch, "E310", {"start": v(-5.76, 2.62) * mm, "end": v(-5.4, 2.73) * mm});
            skLineSegment(sketch, "E311", {"start": v(-5.4, 2.73) * mm, "end": v(-5.1, 2.8) * mm});
            skLineSegment(sketch, "E312", {"start": v(-5.1, 2.8) * mm, "end": v(-4.8, 2.86) * mm});
            skLineSegment(sketch, "E313", {"start": v(-4.8, 2.86) * mm, "end": v(-4.54, 2.9) * mm});
            skLineSegment(sketch, "E314", {"start": v(-4.54, 2.9) * mm, "end": v(-4.29, 2.9) * mm});
            skLineSegment(sketch, "E315", {"start": v(-4.29, 2.9) * mm, "end": v(-4.03, 2.88) * mm});
            skLineSegment(sketch, "E316", {"start": v(-4.03, 2.88) * mm, "end": v(-3.77, 2.84) * mm});
            skLineSegment(sketch, "E317", {"start": v(-3.77, 2.84) * mm, "end": v(-3.5, 2.78) * mm});
            skLineSegment(sketch, "E318", {"start": v(-3.5, 2.78) * mm, "end": v(-3.2, 2.7) * mm});
            skLineSegment(sketch, "E319", {"start": v(-3.2, 2.7) * mm, "end": v(-2.91, 2.6) * mm});
            skLineSegment(sketch, "E320", {"start": v(-2.91, 2.6) * mm, "end": v(-2.67, 2.5) * mm});
            skLineSegment(sketch, "E321", {"start": v(-2.67, 2.5) * mm, "end": v(-2.47, 2.4) * mm});
            skLineSegment(sketch, "E322", {"start": v(-2.47, 2.4) * mm, "end": v(-2.34, 2.32) * mm});
            skLineSegment(sketch, "E323", {"start": v(-2.34, 2.32) * mm, "end": v(-2.22, 2.25) * mm});
            skLineSegment(sketch, "E324", {"start": v(-2.22, 2.25) * mm, "end": v(-2.12, 2.19) * mm});
            skLineSegment(sketch, "E325", {"start": v(-2.12, 2.19) * mm, "end": v(-2.04, 2.14) * mm});
            skLineSegment(sketch, "E326", {"start": v(-2.04, 2.14) * mm, "end": v(-1.97, 2.09) * mm});
            skLineSegment(sketch, "E327", {"start": v(-1.97, 2.09) * mm, "end": v(-1.91, 2.04) * mm});
            skLineSegment(sketch, "E328", {"start": v(-1.91, 2.04) * mm, "end": v(-1.86, 2) * mm});
            skLineSegment(sketch, "E329", {"start": v(-1.86, 2) * mm, "end": v(-1.82, 1.97) * mm});
            skLineSegment(sketch, "E330", {"start": v(-1.82, 1.97) * mm, "end": v(-1.79, 1.94) * mm});
            skLineSegment(sketch, "E331", {"start": v(-1.79, 1.94) * mm, "end": v(-1.74, 1.9) * mm});
            skLineSegment(sketch, "E332", {"start": v(-1.74, 1.9) * mm, "end": v(-1.68, 1.85) * mm});
            skLineSegment(sketch, "E333", {"start": v(-1.68, 1.85) * mm, "end": v(-1.63, 1.8) * mm});
            skLineSegment(sketch, "E334", {"start": v(-1.63, 1.8) * mm, "end": v(-1.57, 1.76) * mm});
            skLineSegment(sketch, "E335", {"start": v(-1.57, 1.76) * mm, "end": v(-1.52, 1.72) * mm});
            skLineSegment(sketch, "E336", {"start": v(-1.52, 1.72) * mm, "end": v(-1.47, 1.68) * mm});
            skLineSegment(sketch, "E337", {"start": v(-1.47, 1.68) * mm, "end": v(-1.44, 1.66) * mm});
            skLineSegment(sketch, "E338", {"start": v(-1.44, 1.66) * mm, "end": v(-1.42, 1.63) * mm});
            skLineSegment(sketch, "E339", {"start": v(-1.42, 1.63) * mm, "end": v(-1.39, 1.6) * mm});
            skLineSegment(sketch, "E340", {"start": v(-1.39, 1.6) * mm, "end": v(-1.35, 1.55) * mm});
            skLineSegment(sketch, "E341", {"start": v(-1.35, 1.55) * mm, "end": v(-1.3, 1.5) * mm});
            skLineSegment(sketch, "E342", {"start": v(-1.3, 1.5) * mm, "end": v(-1.26, 1.44) * mm});
            skLineSegment(sketch, "E343", {"start": v(-1.26, 1.44) * mm, "end": v(-1.21, 1.39) * mm});
            skLineSegment(sketch, "E344", {"start": v(-1.21, 1.39) * mm, "end": v(-1.17, 1.34) * mm});
            skLineSegment(sketch, "E345", {"start": v(-1.17, 1.34) * mm, "end": v(-1.13, 1.3) * mm});
            skLineSegment(sketch, "E346", {"start": v(-1.13, 1.3) * mm, "end": v(-1.11, 1.26) * mm});
            skLineSegment(sketch, "E347", {"start": v(-1.11, 1.26) * mm, "end": v(-1.1, 1.24) * mm});
            skLineSegment(sketch, "E348", {"start": v(-1.1, 1.24) * mm, "end": v(-1.08, 1.23) * mm});
            skLineSegment(sketch, "E349", {"start": v(-1.08, 1.23) * mm, "end": v(-1.07, 1.23) * mm});
            skLineSegment(sketch, "E350", {"start": v(-1.07, 1.23) * mm, "end": v(-1.06, 1.25) * mm});
            skLineSegment(sketch, "E351", {"start": v(-1.06, 1.25) * mm, "end": v(-1.05, 1.28) * mm});
            skLineSegment(sketch, "E352", {"start": v(-1.05, 1.28) * mm, "end": v(-1.03, 1.33) * mm});
            skLineSegment(sketch, "E353", {"start": v(-1.03, 1.33) * mm, "end": v(-1.01, 1.4) * mm});
            skLineSegment(sketch, "E354", {"start": v(-1.01, 1.4) * mm, "end": v(-1, 1.45) * mm});
            skLineSegment(sketch, "E355", {"start": v(-1, 1.45) * mm, "end": v(-0.98, 1.51) * mm});
            skLineSegment(sketch, "E356", {"start": v(-0.98, 1.51) * mm, "end": v(-0.96, 1.56) * mm});
            skLineSegment(sketch, "E357", {"start": v(-0.96, 1.56) * mm, "end": v(-0.95, 1.6) * mm});
            skLineSegment(sketch, "E358", {"start": v(-0.95, 1.6) * mm, "end": v(-0.95, 1.61) * mm});
            skLineSegment(sketch, "E359", {"start": v(-0.95, 1.61) * mm, "end": v(-0.97, 1.64) * mm});
            skLineSegment(sketch, "E360", {"start": v(-0.97, 1.64) * mm, "end": v(-0.99, 1.67) * mm});
            skLineSegment(sketch, "E361", {"start": v(-0.99, 1.67) * mm, "end": v(-1.02, 1.72) * mm});
            skLineSegment(sketch, "E362", {"start": v(-1.02, 1.72) * mm, "end": v(-1.07, 1.79) * mm});
            skLineSegment(sketch, "E363", {"start": v(-1.07, 1.79) * mm, "end": v(-1.11, 1.85) * mm});
            skLineSegment(sketch, "E364", {"start": v(-1.11, 1.85) * mm, "end": v(-1.14, 1.9) * mm});
            skLineSegment(sketch, "E365", {"start": v(-1.14, 1.9) * mm, "end": v(-1.16, 1.98) * mm});
            skLineSegment(sketch, "E366", {"start": v(-1.16, 1.98) * mm, "end": v(-1.21, 2.2) * mm});
            skLineSegment(sketch, "E367", {"start": v(-1.21, 2.2) * mm, "end": v(-1.22, 2.42) * mm});
            skLineSegment(sketch, "E368", {"start": v(-1.22, 2.42) * mm, "end": v(-1.21, 2.51) * mm});
            skLineSegment(sketch, "E369", {"start": v(-1.21, 2.51) * mm, "end": v(-1.2, 2.62) * mm});
            skLineSegment(sketch, "E370", {"start": v(-1.2, 2.62) * mm, "end": v(-1.17, 2.73) * mm});
            skLineSegment(sketch, "E371", {"start": v(-1.17, 2.73) * mm, "end": v(-1.14, 2.82) * mm});
            skLineSegment(sketch, "E372", {"start": v(-1.14, 2.82) * mm, "end": v(-1.13, 2.85) * mm});
            skLineSegment(sketch, "E373", {"start": v(-1.13, 2.85) * mm, "end": v(-1.13, 2.88) * mm});
            skLineSegment(sketch, "E374", {"start": v(-1.13, 2.88) * mm, "end": v(-1.14, 2.92) * mm});
            skLineSegment(sketch, "E375", {"start": v(-1.14, 2.92) * mm, "end": v(-1.16, 2.98) * mm});
            skLineSegment(sketch, "E376", {"start": v(-1.16, 2.98) * mm, "end": v(-1.2, 3.09) * mm});
            skLineSegment(sketch, "E377", {"start": v(-1.2, 3.09) * mm, "end": v(-1.26, 3.2) * mm});
            skLineSegment(sketch, "E378", {"start": v(-1.26, 3.2) * mm, "end": v(-1.33, 3.31) * mm});
            skLineSegment(sketch, "E379", {"start": v(-1.33, 3.31) * mm, "end": v(-1.43, 3.44) * mm});
            skLineSegment(sketch, "E380", {"start": v(-1.43, 3.44) * mm, "end": v(-1.55, 3.6) * mm});
            skLineSegment(sketch, "E381", {"start": v(-1.55, 3.6) * mm, "end": v(-1.68, 3.74) * mm});
            skLineSegment(sketch, "E382", {"start": v(-1.68, 3.74) * mm, "end": v(-1.8, 3.84) * mm});
            skLineSegment(sketch, "E383", {"start": v(-1.8, 3.84) * mm, "end": v(-1.9, 3.91) * mm});
            skLineSegment(sketch, "E384", {"start": v(-1.9, 3.91) * mm, "end": v(-1.93, 3.93) * mm});
            skLineSegment(sketch, "E385", {"start": v(-1.93, 3.93) * mm, "end": v(-1.96, 3.95) * mm});
            skLineSegment(sketch, "E386", {"start": v(-1.96, 3.95) * mm, "end": v(-2, 3.97) * mm});
            skLineSegment(sketch, "E387", {"start": v(-2, 3.97) * mm, "end": v(-2.02, 3.99) * mm});
            skLineSegment(sketch, "E388", {"start": v(-2.02, 3.99) * mm, "end": v(-2.1, 4.03) * mm});
            skLineSegment(sketch, "E389", {"start": v(-2.1, 4.03) * mm, "end": v(-2.22, 4.08) * mm});
            skLineSegment(sketch, "E390", {"start": v(-2.22, 4.08) * mm, "end": v(-2.35, 4.13) * mm});
            skLineSegment(sketch, "E391", {"start": v(-2.35, 4.13) * mm, "end": v(-2.46, 4.16) * mm});
            skLineSegment(sketch, "E392", {"start": v(-2.46, 4.16) * mm, "end": v(-2.6, 4.2) * mm});
            skLineSegment(sketch, "E393", {"start": v(-2.6, 4.2) * mm, "end": v(-2.75, 4.22) * mm});
            skLineSegment(sketch, "E394", {"start": v(-2.75, 4.22) * mm, "end": v(-2.89, 4.23) * mm});
            skLineSegment(sketch, "E395", {"start": v(-2.89, 4.23) * mm, "end": v(-3, 4.23) * mm});
            skLineSegment(sketch, "E396", {"start": v(-3, 4.23) * mm, "end": v(-3.12, 4.22) * mm});
            skLineSegment(sketch, "E397", {"start": v(-3.12, 4.22) * mm, "end": v(-3.19, 4.2) * mm});
            skLineSegment(sketch, "E398", {"start": v(-3.19, 4.2) * mm, "end": v(-3.24, 4.16) * mm});
            skLineSegment(sketch, "E399", {"start": v(-3.24, 4.16) * mm, "end": v(-3.28, 4.1) * mm});
            skLineSegment(sketch, "E400", {"start": v(-3.28, 4.1) * mm, "end": v(-3.3, 3.97) * mm});
            skLineSegment(sketch, "E401", {"start": v(-3.3, 3.97) * mm, "end": v(-3.27, 3.87) * mm});
            skLineSegment(sketch, "E402", {"start": v(-3.27, 3.87) * mm, "end": v(-3.25, 3.85) * mm});
            skLineSegment(sketch, "E403", {"start": v(-3.25, 3.85) * mm, "end": v(-3.23, 3.83) * mm});
            skLineSegment(sketch, "E404", {"start": v(-3.23, 3.83) * mm, "end": v(-3.2, 3.8) * mm});
            skLineSegment(sketch, "E405", {"start": v(-3.2, 3.8) * mm, "end": v(-3.17, 3.79) * mm});
            skLineSegment(sketch, "E406", {"start": v(-3.17, 3.79) * mm, "end": v(-3.14, 3.77) * mm});
            skLineSegment(sketch, "E407", {"start": v(-3.14, 3.77) * mm, "end": v(-3.1, 3.76) * mm});
            skLineSegment(sketch, "E408", {"start": v(-3.1, 3.76) * mm, "end": v(-3.08, 3.75) * mm});
            skLineSegment(sketch, "E409", {"start": v(-3.08, 3.75) * mm, "end": v(-3.06, 3.74) * mm});
            skLineSegment(sketch, "E410", {"start": v(-3.06, 3.74) * mm, "end": v(-3.03, 3.75) * mm});
            skLineSegment(sketch, "E411", {"start": v(-3.03, 3.75) * mm, "end": v(-3.01, 3.77) * mm});
            skLineSegment(sketch, "E412", {"start": v(-3.01, 3.77) * mm, "end": v(-3, 3.79) * mm});
            skLineSegment(sketch, "E413", {"start": v(-3, 3.79) * mm, "end": v(-3, 3.8) * mm});
            skLineSegment(sketch, "E414", {"start": v(-3, 3.8) * mm, "end": v(-3, 3.82) * mm});
            skLineSegment(sketch, "E415", {"start": v(-3, 3.82) * mm, "end": v(-3.03, 3.84) * mm});
            skLineSegment(sketch, "E416", {"start": v(-3.03, 3.84) * mm, "end": v(-3.06, 3.86) * mm});
            skLineSegment(sketch, "E417", {"start": v(-3.06, 3.86) * mm, "end": v(-3.08, 3.87) * mm});
            skLineSegment(sketch, "E418", {"start": v(-3.08, 3.87) * mm, "end": v(-3.1, 3.87) * mm});
            skLineSegment(sketch, "E419", {"start": v(-3.1, 3.87) * mm, "end": v(-3.13, 3.9) * mm});
            skLineSegment(sketch, "E420", {"start": v(-3.13, 3.9) * mm, "end": v(-3.15, 3.91) * mm});
            skLineSegment(sketch, "E421", {"start": v(-3.15, 3.91) * mm, "end": v(-3.16, 3.94) * mm});
            skLineSegment(sketch, "E422", {"start": v(-3.16, 3.94) * mm, "end": v(-3.15, 3.96) * mm});
            skLineSegment(sketch, "E423", {"start": v(-3.15, 3.96) * mm, "end": v(-3.13, 3.99) * mm});
            skLineSegment(sketch, "E424", {"start": v(-3.13, 3.99) * mm, "end": v(-3.02, 4.04) * mm});
            skLineSegment(sketch, "E425", {"start": v(-3.02, 4.04) * mm, "end": v(-2.9, 4.05) * mm});
            skLineSegment(sketch, "E426", {"start": v(-2.9, 4.05) * mm, "end": v(-2.82, 4) * mm});
            skLineSegment(sketch, "E427", {"start": v(-2.82, 4) * mm, "end": v(-2.75, 3.92) * mm});
            skLineSegment(sketch, "E428", {"start": v(-2.75, 3.92) * mm, "end": v(-2.73, 3.89) * mm});
            skLineSegment(sketch, "E429", {"start": v(-2.73, 3.89) * mm, "end": v(-2.72, 3.86) * mm});
            skLineSegment(sketch, "E430", {"start": v(-2.72, 3.86) * mm, "end": v(-2.72, 3.83) * mm});
            skLineSegment(sketch, "E431", {"start": v(-2.72, 3.83) * mm, "end": v(-2.72, 3.8) * mm});
            skLineSegment(sketch, "E432", {"start": v(-2.72, 3.8) * mm, "end": v(-2.73, 3.74) * mm});
            skLineSegment(sketch, "E433", {"start": v(-2.73, 3.74) * mm, "end": v(-2.74, 3.7) * mm});
            skLineSegment(sketch, "E434", {"start": v(-2.74, 3.7) * mm, "end": v(-2.76, 3.65) * mm});
            skLineSegment(sketch, "E435", {"start": v(-2.76, 3.65) * mm, "end": v(-2.79, 3.62) * mm});
            skLineSegment(sketch, "E436", {"start": v(-2.79, 3.62) * mm, "end": v(-2.83, 3.6) * mm});
            skLineSegment(sketch, "E437", {"start": v(-2.83, 3.6) * mm, "end": v(-2.87, 3.58) * mm});
            skLineSegment(sketch, "E438", {"start": v(-2.87, 3.58) * mm, "end": v(-2.94, 3.57) * mm});
            skLineSegment(sketch, "E439", {"start": v(-2.94, 3.57) * mm, "end": v(-3.02, 3.56) * mm});
            skLineSegment(sketch, "E440", {"start": v(-3.02, 3.56) * mm, "end": v(-3.1, 3.57) * mm});
            skLineSegment(sketch, "E441", {"start": v(-3.1, 3.57) * mm, "end": v(-3.18, 3.58) * mm});
            skLineSegment(sketch, "E442", {"start": v(-3.18, 3.58) * mm, "end": v(-3.25, 3.6) * mm});
            skLineSegment(sketch, "E443", {"start": v(-3.25, 3.6) * mm, "end": v(-3.33, 3.66) * mm});
            skLineSegment(sketch, "E444", {"start": v(-3.33, 3.66) * mm, "end": v(-3.4, 3.7) * mm});
            skLineSegment(sketch, "E445", {"start": v(-3.4, 3.7) * mm, "end": v(-3.44, 3.75) * mm});
            skLineSegment(sketch, "E446", {"start": v(-3.44, 3.75) * mm, "end": v(-3.49, 3.82) * mm});
            skLineSegment(sketch, "E447", {"start": v(-3.49, 3.82) * mm, "end": v(-3.53, 3.9) * mm});
            skLineSegment(sketch, "E448", {"start": v(-3.53, 3.9) * mm, "end": v(-3.55, 3.94) * mm});
            skLineSegment(sketch, "E449", {"start": v(-3.55, 3.94) * mm, "end": v(-3.56, 3.98) * mm});
            skLineSegment(sketch, "E450", {"start": v(-3.56, 3.98) * mm, "end": v(-3.56, 4.02) * mm});
            skLineSegment(sketch, "E451", {"start": v(-3.56, 4.02) * mm, "end": v(-3.57, 4.08) * mm});
            skLineSegment(sketch, "E452", {"start": v(-3.57, 4.08) * mm, "end": v(-3.56, 4.14) * mm});
            skLineSegment(sketch, "E453", {"start": v(-3.56, 4.14) * mm, "end": v(-3.56, 4.18) * mm});
            skLineSegment(sketch, "E454", {"start": v(-3.56, 4.18) * mm, "end": v(-3.55, 4.21) * mm});
            skLineSegment(sketch, "E455", {"start": v(-3.55, 4.21) * mm, "end": v(-3.52, 4.25) * mm});
            skLineSegment(sketch, "E456", {"start": v(-3.52, 4.25) * mm, "end": v(-3.45, 4.34) * mm});
            skLineSegment(sketch, "E457", {"start": v(-3.45, 4.34) * mm, "end": v(-3.37, 4.41) * mm});
            skLineSegment(sketch, "E458", {"start": v(-3.37, 4.41) * mm, "end": v(-3.27, 4.48) * mm});
            skLineSegment(sketch, "E459", {"start": v(-3.27, 4.48) * mm, "end": v(-3.16, 4.53) * mm});
            skLineSegment(sketch, "E460", {"start": v(-3.16, 4.53) * mm, "end": v(-3.12, 4.54) * mm});
            skLineSegment(sketch, "E461", {"start": v(-3.12, 4.54) * mm, "end": v(-3.08, 4.55) * mm});
            skLineSegment(sketch, "E462", {"start": v(-3.08, 4.55) * mm, "end": v(-3.01, 4.55) * mm});
            skLineSegment(sketch, "E463", {"start": v(-3.01, 4.55) * mm, "end": v(-2.9, 4.55) * mm});
            skLineSegment(sketch, "E464", {"start": v(-2.9, 4.55) * mm, "end": v(-2.8, 4.55) * mm});
            skLineSegment(sketch, "E465", {"start": v(-2.8, 4.55) * mm, "end": v(-2.72, 4.54) * mm});
            skLineSegment(sketch, "E466", {"start": v(-2.72, 4.54) * mm, "end": v(-2.65, 4.53) * mm});
            skLineSegment(sketch, "E467", {"start": v(-2.65, 4.53) * mm, "end": v(-2.56, 4.5) * mm});
            skLineSegment(sketch, "E468", {"start": v(-2.56, 4.5) * mm, "end": v(-2.49, 4.49) * mm});
            skLineSegment(sketch, "E469", {"start": v(-2.49, 4.49) * mm, "end": v(-2.4, 4.47) * mm});
            skLineSegment(sketch, "E470", {"start": v(-2.4, 4.47) * mm, "end": v(-2.34, 4.44) * mm});
            skLineSegment(sketch, "E471", {"start": v(-2.34, 4.44) * mm, "end": v(-2.28, 4.43) * mm});
            skLineSegment(sketch, "E472", {"start": v(-2.28, 4.43) * mm, "end": v(-2.19, 4.4) * mm});
            skLineSegment(sketch, "E473", {"start": v(-2.19, 4.4) * mm, "end": v(-2.09, 4.35) * mm});
            skLineSegment(sketch, "E474", {"start": v(-2.09, 4.35) * mm, "end": v(-1.98, 4.3) * mm});
            skLineSegment(sketch, "E475", {"start": v(-1.98, 4.3) * mm, "end": v(-1.87, 4.24) * mm});
            skLineSegment(sketch, "E476", {"start": v(-1.87, 4.24) * mm, "end": v(-1.76, 4.17) * mm});
            skLineSegment(sketch, "E477", {"start": v(-1.76, 4.17) * mm, "end": v(-1.66, 4.1) * mm});
            skLineSegment(sketch, "E478", {"start": v(-1.66, 4.1) * mm, "end": v(-1.56, 4.03) * mm});
            skLineSegment(sketch, "E479", {"start": v(-1.56, 4.03) * mm, "end": v(-1.48, 3.97) * mm});
            skLineSegment(sketch, "E480", {"start": v(-1.48, 3.97) * mm, "end": v(-1.37, 3.87) * mm});
            skLineSegment(sketch, "E481", {"start": v(-1.37, 3.87) * mm, "end": v(-1.26, 3.74) * mm});
            skLineSegment(sketch, "E482", {"start": v(-1.26, 3.74) * mm, "end": v(-1.15, 3.61) * mm});
            skLineSegment(sketch, "E483", {"start": v(-1.15, 3.61) * mm, "end": v(-1.05, 3.48) * mm});
            skLineSegment(sketch, "E484", {"start": v(-1.05, 3.48) * mm, "end": v(-1.03, 3.45) * mm});
            skLineSegment(sketch, "E485", {"start": v(-1.03, 3.45) * mm, "end": v(-1, 3.41) * mm});
            skLineSegment(sketch, "E486", {"start": v(-1, 3.41) * mm, "end": v(-0.98, 3.38) * mm});
            skLineSegment(sketch, "E487", {"start": v(-0.98, 3.38) * mm, "end": v(-0.96, 3.34) * mm});
            skLineSegment(sketch, "E488", {"start": v(-0.96, 3.34) * mm, "end": v(-0.94, 3.3) * mm});
            skLineSegment(sketch, "E489", {"start": v(-0.94, 3.3) * mm, "end": v(-0.92, 3.28) * mm});
            skLineSegment(sketch, "E490", {"start": v(-0.92, 3.28) * mm, "end": v(-0.9, 3.25) * mm});
            skLineSegment(sketch, "E491", {"start": v(-0.9, 3.25) * mm, "end": v(-0.9, 3.24) * mm});
            skLineSegment(sketch, "E492", {"start": v(-0.9, 3.24) * mm, "end": v(-0.9, 3.22) * mm});
            skLineSegment(sketch, "E493", {"start": v(-0.9, 3.22) * mm, "end": v(-0.88, 3.21) * mm});
            skLineSegment(sketch, "E494", {"start": v(-0.88, 3.21) * mm, "end": v(-0.86, 3.22) * mm});
            skLineSegment(sketch, "E495", {"start": v(-0.86, 3.22) * mm, "end": v(-0.84, 3.25) * mm});
            skLineSegment(sketch, "E496", {"start": v(-0.84, 3.25) * mm, "end": v(-0.8, 3.3) * mm});
            skLineSegment(sketch, "E497", {"start": v(-0.8, 3.3) * mm, "end": v(-0.73, 3.34) * mm});
            skLineSegment(sketch, "E498", {"start": v(-0.73, 3.34) * mm, "end": v(-0.67, 3.39) * mm});
            skLineSegment(sketch, "E499", {"start": v(-0.67, 3.39) * mm, "end": v(-0.62, 3.42) * mm});
            skLineSegment(sketch, "E500", {"start": v(-0.62, 3.42) * mm, "end": v(-0.55, 3.44) * mm});
            skLineSegment(sketch, "E501", {"start": v(-0.55, 3.44) * mm, "end": v(-0.46, 3.47) * mm});
            skLineSegment(sketch, "E502", {"start": v(-0.46, 3.47) * mm, "end": v(-0.36, 3.49) * mm});
            skLineSegment(sketch, "E503", {"start": v(-0.36, 3.49) * mm, "end": v(-0.27, 3.5) * mm});
            skLineSegment(sketch, "E504", {"start": v(-0.27, 3.5) * mm, "end": v(-0.2, 3.5) * mm});
            skLineSegment(sketch, "E505", {"start": v(-0.2, 3.5) * mm, "end": v(-0.16, 3.5) * mm});
            skLineSegment(sketch, "E506", {"start": v(-0.16, 3.5) * mm, "end": v(-0.1, 3.5) * mm});
            skLineSegment(sketch, "E507", {"start": v(-0.1, 3.5) * mm, "end": v(-0.05, 3.48) * mm});
            skLineSegment(sketch, "E508", {"start": v(-0.05, 3.48) * mm, "end": v(0, 3.47) * mm});
            skLineSegment(sketch, "E509", {"start": v(0, 3.47) * mm, "end": v(0.04, 3.45) * mm});
            skLineSegment(sketch, "E510", {"start": v(0.04, 3.45) * mm, "end": v(0.08, 3.44) * mm});
            skLineSegment(sketch, "E511", {"start": v(0.08, 3.44) * mm, "end": v(0.11, 3.42) * mm});
            skLineSegment(sketch, "E512", {"start": v(0.11, 3.42) * mm, "end": v(0.14, 3.4) * mm});
            skLineSegment(sketch, "E513", {"start": v(0.14, 3.4) * mm, "end": v(0.16, 3.4) * mm});
            skLineSegment(sketch, "E514", {"start": v(0.16, 3.4) * mm, "end": v(0.17, 3.4) * mm});
            skLineSegment(sketch, "E515", {"start": v(0.17, 3.4) * mm, "end": v(0.18, 3.4) * mm});
            skLineSegment(sketch, "E516", {"start": v(0.18, 3.4) * mm, "end": v(0.18, 3.4) * mm});
            skLineSegment(sketch, "E517", {"start": v(0.18, 3.4) * mm, "end": v(0.2, 3.43) * mm});
            skLineSegment(sketch, "E518", {"start": v(0.2, 3.43) * mm, "end": v(0.21, 3.47) * mm});
            skLineSegment(sketch, "E519", {"start": v(0.21, 3.47) * mm, "end": v(0.23, 3.52) * mm});
            skLineSegment(sketch, "E520", {"start": v(0.23, 3.52) * mm, "end": v(0.25, 3.56) * mm});
            skLineSegment(sketch, "E521", {"start": v(0.25, 3.56) * mm, "end": v(0.27, 3.61) * mm});
            skLineSegment(sketch, "E522", {"start": v(0.27, 3.61) * mm, "end": v(0.3, 3.67) * mm});
            skLineSegment(sketch, "E523", {"start": v(0.3, 3.67) * mm, "end": v(0.32, 3.73) * mm});
            skLineSegment(sketch, "E524", {"start": v(0.32, 3.73) * mm, "end": v(0.36, 3.82) * mm});
            skLineSegment(sketch, "E525", {"start": v(0.36, 3.82) * mm, "end": v(0.41, 3.92) * mm});
            skLineSegment(sketch, "E526", {"start": v(0.41, 3.92) * mm, "end": v(0.48, 4.05) * mm});
            skLineSegment(sketch, "E527", {"start": v(0.48, 4.05) * mm, "end": v(0.55, 4.2) * mm});
            skLineSegment(sketch, "E528", {"start": v(0.55, 4.2) * mm, "end": v(0.62, 4.32) * mm});
            skLineSegment(sketch, "E529", {"start": v(0.62, 4.32) * mm, "end": v(0.68, 4.43) * mm});
            skLineSegment(sketch, "E530", {"start": v(0.68, 4.43) * mm, "end": v(0.73, 4.53) * mm});
            skLineSegment(sketch, "E531", {"start": v(0.73, 4.53) * mm, "end": v(0.79, 4.62) * mm});
            skLineSegment(sketch, "E532", {"start": v(0.79, 4.62) * mm, "end": v(0.85, 4.7) * mm});
            skLineSegment(sketch, "E533", {"start": v(0.85, 4.7) * mm, "end": v(0.91, 4.8) * mm});
            skLineSegment(sketch, "E534", {"start": v(0.91, 4.8) * mm, "end": v(0.99, 4.9) * mm});
            skLineSegment(sketch, "E535", {"start": v(0.99, 4.9) * mm, "end": v(1.07, 5) * mm});
            skLineSegment(sketch, "E536", {"start": v(1.07, 5) * mm, "end": v(1.14, 5.08) * mm});
            skLineSegment(sketch, "E537", {"start": v(1.14, 5.08) * mm, "end": v(1.21, 5.16) * mm});
            skLineSegment(sketch, "E538", {"start": v(1.21, 5.16) * mm, "end": v(1.3, 5.25) * mm});
            skLineSegment(sketch, "E539", {"start": v(1.3, 5.25) * mm, "end": v(1.37, 5.33) * mm});
            skLineSegment(sketch, "E540", {"start": v(1.37, 5.33) * mm, "end": v(1.44, 5.41) * mm});
            skLineSegment(sketch, "E541", {"start": v(1.44, 5.41) * mm, "end": v(1.51, 5.48) * mm});
            skLineSegment(sketch, "E542", {"start": v(1.51, 5.48) * mm, "end": v(1.57, 5.53) * mm});
            skLineSegment(sketch, "E543", {"start": v(1.57, 5.53) * mm, "end": v(1.61, 5.57) * mm});
            skLineSegment(sketch, "E544", {"start": v(1.61, 5.57) * mm, "end": v(1.75, 5.67) * mm});
            skLineSegment(sketch, "E545", {"start": v(1.75, 5.67) * mm, "end": v(1.89, 5.75) * mm});
            skLineSegment(sketch, "E546", {"start": v(1.89, 5.75) * mm, "end": v(2.01, 5.8) * mm});
            skLineSegment(sketch, "E547", {"start": v(2.01, 5.8) * mm, "end": v(2.13, 5.84) * mm});
            skLineSegment(sketch, "E548", {"start": v(2.13, 5.84) * mm, "end": v(2.2, 5.85) * mm});
            skLineSegment(sketch, "E549", {"start": v(2.2, 5.85) * mm, "end": v(2.27, 5.85) * mm});
            skLineSegment(sketch, "E550", {"start": v(2.27, 5.85) * mm, "end": v(2.34, 5.83) * mm});
            skLineSegment(sketch, "E551", {"start": v(2.34, 5.83) * mm, "end": v(2.43, 5.8) * mm});
            skLineSegment(sketch, "E552", {"start": v(2.43, 5.8) * mm, "end": v(2.51, 5.74) * mm});
            skLineSegment(sketch, "E553", {"start": v(2.51, 5.74) * mm, "end": v(2.6, 5.67) * mm});
            skLineSegment(sketch, "E554", {"start": v(2.6, 5.67) * mm, "end": v(2.66, 5.6) * mm});
            skLineSegment(sketch, "E555", {"start": v(2.66, 5.6) * mm, "end": v(2.7, 5.52) * mm});
            skLineSegment(sketch, "E556", {"start": v(2.7, 5.52) * mm, "end": v(2.74, 5.43) * mm});
            skLineSegment(sketch, "E557", {"start": v(2.74, 5.43) * mm, "end": v(2.77, 5.3) * mm});
            skLineSegment(sketch, "E558", {"start": v(2.77, 5.3) * mm, "end": v(2.79, 5.19) * mm});
            skLineSegment(sketch, "E559", {"start": v(2.79, 5.19) * mm, "end": v(2.8, 5.1) * mm});
            skLineSegment(sketch, "E560", {"start": v(2.8, 5.1) * mm, "end": v(2.78, 5) * mm});
            skLineSegment(sketch, "E561", {"start": v(2.78, 5) * mm, "end": v(2.75, 4.92) * mm});
            skLineSegment(sketch, "E562", {"start": v(2.75, 4.92) * mm, "end": v(2.7, 4.85) * mm});
            skLineSegment(sketch, "E563", {"start": v(2.7, 4.85) * mm, "end": v(2.65, 4.78) * mm});
            skLineSegment(sketch, "E564", {"start": v(2.65, 4.78) * mm, "end": v(2.59, 4.72) * mm});
            skLineSegment(sketch, "E565", {"start": v(2.59, 4.72) * mm, "end": v(2.51, 4.68) * mm});
            skLineSegment(sketch, "E566", {"start": v(2.51, 4.68) * mm, "end": v(2.43, 4.64) * mm});
            skLineSegment(sketch, "E567", {"start": v(2.43, 4.64) * mm, "end": v(2.34, 4.62) * mm});
            skLineSegment(sketch, "E568", {"start": v(2.34, 4.62) * mm, "end": v(2.26, 4.62) * mm});
            skLineSegment(sketch, "E569", {"start": v(2.26, 4.62) * mm, "end": v(2.2, 4.62) * mm});
            skLineSegment(sketch, "E570", {"start": v(2.2, 4.62) * mm, "end": v(2.15, 4.64) * mm});
            skLineSegment(sketch, "E571", {"start": v(2.15, 4.64) * mm, "end": v(2.1, 4.68) * mm});
            skLineSegment(sketch, "E572", {"start": v(2.1, 4.68) * mm, "end": v(2.04, 4.73) * mm});
            skLineSegment(sketch, "E573", {"start": v(2.04, 4.73) * mm, "end": v(2, 4.78) * mm});
            skLineSegment(sketch, "E574", {"start": v(2, 4.78) * mm, "end": v(2, 4.84) * mm});
            skLineSegment(sketch, "E575", {"start": v(2, 4.84) * mm, "end": v(1.99, 4.92) * mm});
            skLineSegment(sketch, "E576", {"start": v(1.99, 4.92) * mm, "end": v(1.99, 5.02) * mm});
            skLineSegment(sketch, "E577", {"start": v(1.99, 5.02) * mm, "end": v(2, 5.09) * mm});
            skLineSegment(sketch, "E578", {"start": v(2, 5.09) * mm, "end": v(2.02, 5.15) * mm});
            skLineSegment(sketch, "E579", {"start": v(2.02, 5.15) * mm, "end": v(2.05, 5.21) * mm});
            skLineSegment(sketch, "E580", {"start": v(2.05, 5.21) * mm, "end": v(2.09, 5.26) * mm});
            skLineSegment(sketch, "E581", {"start": v(2.09, 5.26) * mm, "end": v(2.14, 5.3) * mm});
            skLineSegment(sketch, "E582", {"start": v(2.14, 5.3) * mm, "end": v(2.2, 5.31) * mm});
            skLineSegment(sketch, "E583", {"start": v(2.2, 5.31) * mm, "end": v(2.25, 5.32) * mm});
            skLineSegment(sketch, "E584", {"start": v(2.25, 5.32) * mm, "end": v(2.29, 5.32) * mm});
            skLineSegment(sketch, "E585", {"start": v(2.29, 5.32) * mm, "end": v(2.32, 5.31) * mm});
            skLineSegment(sketch, "E586", {"start": v(2.32, 5.31) * mm, "end": v(2.34, 5.3) * mm});
            skLineSegment(sketch, "E587", {"start": v(2.34, 5.3) * mm, "end": v(2.36, 5.27) * mm});
            skLineSegment(sketch, "E588", {"start": v(2.36, 5.27) * mm, "end": v(2.38, 5.24) * mm});
            skLineSegment(sketch, "E589", {"start": v(2.38, 5.24) * mm, "end": v(2.36, 5.18) * mm});
            skLineSegment(sketch, "E590", {"start": v(2.36, 5.18) * mm, "end": v(2.34, 5.15) * mm});
            skLineSegment(sketch, "E591", {"start": v(2.34, 5.15) * mm, "end": v(2.33, 5.13) * mm});
            skLineSegment(sketch, "E592", {"start": v(2.33, 5.13) * mm, "end": v(2.33, 5.1) * mm});
            skLineSegment(sketch, "E593", {"start": v(2.33, 5.1) * mm, "end": v(2.33, 5.06) * mm});
            skLineSegment(sketch, "E594", {"start": v(2.33, 5.06) * mm, "end": v(2.34, 5.01) * mm});
            skLineSegment(sketch, "E595", {"start": v(2.34, 5.01) * mm, "end": v(2.36, 4.98) * mm});
            skLineSegment(sketch, "E596", {"start": v(2.36, 4.98) * mm, "end": v(2.38, 4.96) * mm});
            skLineSegment(sketch, "E597", {"start": v(2.38, 4.96) * mm, "end": v(2.42, 4.96) * mm});
            skLineSegment(sketch, "E598", {"start": v(2.42, 4.96) * mm, "end": v(2.46, 4.96) * mm});
            skLineSegment(sketch, "E599", {"start": v(2.46, 4.96) * mm, "end": v(2.49, 4.99) * mm});
            skLineSegment(sketch, "E600", {"start": v(2.49, 4.99) * mm, "end": v(2.51, 5.02) * mm});
            skLineSegment(sketch, "E601", {"start": v(2.51, 5.02) * mm, "end": v(2.53, 5.07) * mm});
            skLineSegment(sketch, "E602", {"start": v(2.53, 5.07) * mm, "end": v(2.54, 5.15) * mm});
            skLineSegment(sketch, "E603", {"start": v(2.54, 5.15) * mm, "end": v(2.53, 5.26) * mm});
            skLineSegment(sketch, "E604", {"start": v(2.53, 5.26) * mm, "end": v(2.5, 5.36) * mm});
            skLineSegment(sketch, "E605", {"start": v(2.5, 5.36) * mm, "end": v(2.46, 5.45) * mm});
            skLineSegment(sketch, "E606", {"start": v(2.46, 5.45) * mm, "end": v(2.41, 5.5) * mm});
            skLineSegment(sketch, "E607", {"start": v(2.41, 5.5) * mm, "end": v(2.35, 5.53) * mm});
            skLineSegment(sketch, "E608", {"start": v(2.35, 5.53) * mm, "end": v(2.25, 5.52) * mm});
            skLineSegment(sketch, "E609", {"start": v(2.25, 5.52) * mm, "end": v(2.12, 5.48) * mm});
            skLineSegment(sketch, "E610", {"start": v(2.12, 5.48) * mm, "end": v(2, 5.43) * mm});
            skLineSegment(sketch, "E611", {"start": v(2, 5.43) * mm, "end": v(1.91, 5.39) * mm});
            skLineSegment(sketch, "E612", {"start": v(1.91, 5.39) * mm, "end": v(1.84, 5.34) * mm});
            skLineSegment(sketch, "E613", {"start": v(1.84, 5.34) * mm, "end": v(1.75, 5.27) * mm});
            skLineSegment(sketch, "E614", {"start": v(1.75, 5.27) * mm, "end": v(1.7, 5.21) * mm});
            skLineSegment(sketch, "E615", {"start": v(1.7, 5.21) * mm, "end": v(1.62, 5.14) * mm});
            skLineSegment(sketch, "E616", {"start": v(1.62, 5.14) * mm, "end": v(1.54, 5.06) * mm});
            skLineSegment(sketch, "E617", {"start": v(1.54, 5.06) * mm, "end": v(1.46, 4.97) * mm});
            skLineSegment(sketch, "E618", {"start": v(1.46, 4.97) * mm, "end": v(1.38, 4.88) * mm});
            skLineSegment(sketch, "E619", {"start": v(1.38, 4.88) * mm, "end": v(1.3, 4.8) * mm});
            skLineSegment(sketch, "E620", {"start": v(1.3, 4.8) * mm, "end": v(1.24, 4.72) * mm});
            skLineSegment(sketch, "E621", {"start": v(1.24, 4.72) * mm, "end": v(1.2, 4.66) * mm});
            skLineSegment(sketch, "E622", {"start": v(1.2, 4.66) * mm, "end": v(1.17, 4.63) * mm});
            skLineSegment(sketch, "E623", {"start": v(1.17, 4.63) * mm, "end": v(1.15, 4.6) * mm});
            skLineSegment(sketch, "E624", {"start": v(1.15, 4.6) * mm, "end": v(1.12, 4.56) * mm});
            skLineSegment(sketch, "E625", {"start": v(1.12, 4.56) * mm, "end": v(1.1, 4.53) * mm});
            skLineSegment(sketch, "E626", {"start": v(1.1, 4.53) * mm, "end": v(1.08, 4.5) * mm});
            skLineSegment(sketch, "E627", {"start": v(1.08, 4.5) * mm, "end": v(1.05, 4.46) * mm});
            skLineSegment(sketch, "E628", {"start": v(1.05, 4.46) * mm, "end": v(1.02, 4.42) * mm});
            skLineSegment(sketch, "E629", {"start": v(1.02, 4.42) * mm, "end": v(1, 4.38) * mm});
            skLineSegment(sketch, "E630", {"start": v(1, 4.38) * mm, "end": v(0.97, 4.34) * mm});
            skLineSegment(sketch, "E631", {"start": v(0.97, 4.34) * mm, "end": v(0.95, 4.3) * mm});
            skLineSegment(sketch, "E632", {"start": v(0.95, 4.3) * mm, "end": v(0.93, 4.26) * mm});
            skLineSegment(sketch, "E633", {"start": v(0.93, 4.26) * mm, "end": v(0.91, 4.23) * mm});
            skLineSegment(sketch, "E634", {"start": v(0.91, 4.23) * mm, "end": v(0.82, 4.07) * mm});
            skLineSegment(sketch, "E635", {"start": v(0.82, 4.07) * mm, "end": v(0.75, 3.94) * mm});
            skLineSegment(sketch, "E636", {"start": v(0.75, 3.94) * mm, "end": v(0.7, 3.83) * mm});
            skLineSegment(sketch, "E637", {"start": v(0.7, 3.83) * mm, "end": v(0.66, 3.72) * mm});
            skLineSegment(sketch, "E638", {"start": v(0.66, 3.72) * mm, "end": v(0.66, 3.7) * mm});
            skLineSegment(sketch, "E639", {"start": v(0.66, 3.7) * mm, "end": v(0.64, 3.66) * mm});
            skLineSegment(sketch, "E640", {"start": v(0.64, 3.66) * mm, "end": v(0.63, 3.63) * mm});
            skLineSegment(sketch, "E641", {"start": v(0.63, 3.63) * mm, "end": v(0.62, 3.59) * mm});
            skLineSegment(sketch, "E642", {"start": v(0.62, 3.59) * mm, "end": v(0.57, 3.44) * mm});
            skLineSegment(sketch, "E643", {"start": v(0.57, 3.44) * mm, "end": v(0.51, 3.23) * mm});
            skLineSegment(sketch, "E644", {"start": v(0.51, 3.23) * mm, "end": v(0.5, 3.15) * mm});
            skLineSegment(sketch, "E645", {"start": v(0.5, 3.15) * mm, "end": v(0.52, 3.06) * mm});
            skLineSegment(sketch, "E646", {"start": v(0.52, 3.06) * mm, "end": v(0.55, 2.93) * mm});
            skLineSegment(sketch, "E647", {"start": v(0.55, 2.93) * mm, "end": v(0.58, 2.76) * mm});
            skLineSegment(sketch, "E648", {"start": v(0.58, 2.76) * mm, "end": v(0.6, 2.6) * mm});
            skLineSegment(sketch, "E649", {"start": v(0.6, 2.6) * mm, "end": v(0.6, 2.46) * mm});
            skLineSegment(sketch, "E650", {"start": v(0.6, 2.46) * mm, "end": v(0.58, 2.38) * mm});
            skLineSegment(sketch, "E651", {"start": v(0.58, 2.38) * mm, "end": v(0.55, 2.27) * mm});
            skLineSegment(sketch, "E652", {"start": v(0.55, 2.27) * mm, "end": v(0.53, 2.17) * mm});
            skLineSegment(sketch, "E653", {"start": v(0.53, 2.17) * mm, "end": v(0.5, 2.09) * mm});
            skLineSegment(sketch, "E654", {"start": v(0.5, 2.09) * mm, "end": v(0.47, 2.02) * mm});
            skLineSegment(sketch, "E655", {"start": v(0.47, 2.02) * mm, "end": v(0.43, 1.94) * mm});
            skLineSegment(sketch, "E656", {"start": v(0.43, 1.94) * mm, "end": v(0.38, 1.86) * mm});
            skLineSegment(sketch, "E657", {"start": v(0.38, 1.86) * mm, "end": v(0.34, 1.8) * mm});
            skLineSegment(sketch, "E658", {"start": v(0.34, 1.8) * mm, "end": v(0.33, 1.78) * mm});
            skLineSegment(sketch, "E659", {"start": v(0.33, 1.78) * mm, "end": v(0.32, 1.76) * mm});
            skLineSegment(sketch, "E660", {"start": v(0.32, 1.76) * mm, "end": v(0.32, 1.75) * mm});
            skLineSegment(sketch, "E661", {"start": v(0.32, 1.75) * mm, "end": v(0.33, 1.74) * mm});
            skLineSegment(sketch, "E662", {"start": v(0.33, 1.74) * mm, "end": v(0.36, 1.7) * mm});
            skLineSegment(sketch, "E663", {"start": v(0.36, 1.7) * mm, "end": v(0.4, 1.6) * mm});
            skLineSegment(sketch, "E664", {"start": v(0.4, 1.6) * mm, "end": v(0.43, 1.49) * mm});
            skLineSegment(sketch, "E665", {"start": v(0.43, 1.49) * mm, "end": v(0.46, 1.37) * mm});
            skLineSegment(sketch, "E666", {"start": v(0.46, 1.37) * mm, "end": v(0.47, 1.32) * mm});
            skLineSegment(sketch, "E667", {"start": v(0.47, 1.32) * mm, "end": v(0.48, 1.28) * mm});
            skLineSegment(sketch, "E668", {"start": v(0.48, 1.28) * mm, "end": v(0.48, 1.25) * mm});
            skLineSegment(sketch, "E669", {"start": v(0.48, 1.25) * mm, "end": v(0.49, 1.24) * mm});
            skLineSegment(sketch, "E670", {"start": v(0.49, 1.24) * mm, "end": v(0.5, 1.26) * mm});
            skLineSegment(sketch, "E671", {"start": v(0.5, 1.26) * mm, "end": v(0.56, 1.32) * mm});
            skLineSegment(sketch, "E672", {"start": v(0.56, 1.32) * mm, "end": v(0.61, 1.4) * mm});
            skLineSegment(sketch, "E673", {"start": v(0.61, 1.4) * mm, "end": v(0.66, 1.48) * mm});
            skLineSegment(sketch, "E674", {"start": v(0.66, 1.48) * mm, "end": v(0.7, 1.54) * mm});
            skLineSegment(sketch, "E675", {"start": v(0.7, 1.54) * mm, "end": v(0.78, 1.62) * mm});
            skLineSegment(sketch, "E676", {"start": v(0.78, 1.62) * mm, "end": v(0.88, 1.72) * mm});
            skLineSegment(sketch, "E677", {"start": v(0.88, 1.72) * mm, "end": v(1.02, 1.85) * mm});
            skLineSegment(sketch, "E678", {"start": v(1.02, 1.85) * mm, "end": v(1.13, 1.94) * mm});
            skLineSegment(sketch, "E679", {"start": v(1.13, 1.94) * mm, "end": v(1.21, 2.02) * mm});
            skLineSegment(sketch, "E680", {"start": v(1.21, 2.02) * mm, "end": v(1.3, 2.09) * mm});
            skLineSegment(sketch, "E681", {"start": v(1.3, 2.09) * mm, "end": v(1.42, 2.16) * mm});
            skLineSegment(sketch, "E682", {"start": v(1.42, 2.16) * mm, "end": v(1.73, 2.36) * mm});
            skLineSegment(sketch, "E683", {"start": v(1.73, 2.36) * mm, "end": v(2.02, 2.5) * mm});
            skLineSegment(sketch, "E684", {"start": v(2.02, 2.5) * mm, "end": v(2.29, 2.61) * mm});
            skLineSegment(sketch, "E685", {"start": v(2.29, 2.61) * mm, "end": v(2.54, 2.68) * mm});
            skLineSegment(sketch, "E686", {"start": v(2.54, 2.68) * mm, "end": v(2.67, 2.7) * mm});
            skLineSegment(sketch, "E687", {"start": v(2.67, 2.7) * mm, "end": v(2.81, 2.73) * mm});
            skLineSegment(sketch, "E688", {"start": v(2.81, 2.73) * mm, "end": v(2.89, 2.74) * mm});
            skLineSegment(sketch, "E689", {"start": v(2.89, 2.74) * mm, "end": v(2.98, 2.75) * mm});
            skLineSegment(sketch, "E690", {"start": v(2.98, 2.75) * mm, "end": v(3.09, 2.76) * mm});
            skLineSegment(sketch, "E691", {"start": v(3.09, 2.76) * mm, "end": v(3.18, 2.77) * mm});
            skLineSegment(sketch, "E692", {"start": v(3.18, 2.77) * mm, "end": v(3.3, 2.78) * mm});
            skLineSegment(sketch, "E693", {"start": v(3.3, 2.78) * mm, "end": v(3.38, 2.78) * mm});
            skLineSegment(sketch, "E694", {"start": v(3.38, 2.78) * mm, "end": v(3.46, 2.78) * mm});
            skLineSegment(sketch, "E695", {"start": v(3.46, 2.78) * mm, "end": v(3.56, 2.77) * mm});
            skLineSegment(sketch, "E696", {"start": v(3.56, 2.77) * mm, "end": v(3.73, 2.75) * mm});
            skLineSegment(sketch, "E697", {"start": v(3.73, 2.75) * mm, "end": v(3.86, 2.74) * mm});
            skLineSegment(sketch, "E698", {"start": v(3.86, 2.74) * mm, "end": v(3.95, 2.73) * mm});
            skLineSegment(sketch, "E699", {"start": v(3.95, 2.73) * mm, "end": v(4.03, 2.71) * mm});
            skLineSegment(sketch, "E700", {"start": v(4.03, 2.71) * mm, "end": v(4.07, 2.7) * mm});
            skLineSegment(sketch, "E701", {"start": v(4.07, 2.7) * mm, "end": v(4.12, 2.7) * mm});
            skLineSegment(sketch, "E702", {"start": v(4.12, 2.7) * mm, "end": v(4.17, 2.68) * mm});
            skLineSegment(sketch, "E703", {"start": v(4.17, 2.68) * mm, "end": v(4.21, 2.68) * mm});
            skLineSegment(sketch, "E704", {"start": v(4.21, 2.68) * mm, "end": v(4.33, 2.66) * mm});
            skLineSegment(sketch, "E705", {"start": v(4.33, 2.66) * mm, "end": v(4.46, 2.63) * mm});
            skLineSegment(sketch, "E706", {"start": v(4.46, 2.63) * mm, "end": v(4.6, 2.6) * mm});
            skLineSegment(sketch, "E707", {"start": v(4.6, 2.6) * mm, "end": v(4.73, 2.57) * mm});
            skLineSegment(sketch, "E708", {"start": v(4.73, 2.57) * mm, "end": v(4.9, 2.56) * mm});
            skLineSegment(sketch, "E709", {"start": v(4.9, 2.56) * mm, "end": v(5.08, 2.55) * mm});
            skLineSegment(sketch, "E710", {"start": v(5.08, 2.55) * mm, "end": v(5.25, 2.55) * mm});
            skLineSegment(sketch, "E711", {"start": v(5.25, 2.55) * mm, "end": v(5.37, 2.55) * mm});
            skLineSegment(sketch, "E712", {"start": v(5.37, 2.55) * mm, "end": v(5.48, 2.58) * mm});
            skLineSegment(sketch, "E713", {"start": v(5.48, 2.58) * mm, "end": v(5.62, 2.61) * mm});
            skLineSegment(sketch, "E714", {"start": v(5.62, 2.61) * mm, "end": v(5.78, 2.66) * mm});
            skLineSegment(sketch, "E715", {"start": v(5.78, 2.66) * mm, "end": v(5.95, 2.72) * mm});
            skLineSegment(sketch, "E716", {"start": v(5.95, 2.72) * mm, "end": v(6.05, 2.76) * mm});
            skLineSegment(sketch, "E717", {"start": v(6.05, 2.76) * mm, "end": v(6.15, 2.8) * mm});
            skLineSegment(sketch, "E718", {"start": v(6.15, 2.8) * mm, "end": v(6.24, 2.83) * mm});
            skLineSegment(sketch, "E719", {"start": v(6.24, 2.83) * mm, "end": v(6.3, 2.85) * mm});
            skLineSegment(sketch, "E720", {"start": v(6.3, 2.85) * mm, "end": v(6.43, 2.9) * mm});
            skLineSegment(sketch, "E721", {"start": v(6.43, 2.9) * mm, "end": v(6.55, 2.93) * mm});
            skLineSegment(sketch, "E722", {"start": v(6.55, 2.93) * mm, "end": v(6.63, 2.96) * mm});
            skLineSegment(sketch, "E723", {"start": v(6.63, 2.96) * mm, "end": v(6.74, 3) * mm});
            skLineSegment(sketch, "E724", {"start": v(6.74, 3) * mm, "end": v(6.85, 3.02) * mm});
            skLineSegment(sketch, "E725", {"start": v(6.85, 3.02) * mm, "end": v(6.96, 3.05) * mm});
            skLineSegment(sketch, "E726", {"start": v(6.96, 3.05) * mm, "end": v(7.07, 3.08) * mm});
            skLineSegment(sketch, "E727", {"start": v(7.07, 3.08) * mm, "end": v(7.17, 3.1) * mm});
            skLineSegment(sketch, "E728", {"start": v(7.17, 3.1) * mm, "end": v(7.26, 3.11) * mm});
            skLineSegment(sketch, "E729", {"start": v(7.26, 3.11) * mm, "end": v(7.33, 3.12) * mm});
            skLineSegment(sketch, "E730", {"start": v(7.33, 3.12) * mm, "end": v(7.44, 3.13) * mm});
            skLineSegment(sketch, "E731", {"start": v(7.44, 3.13) * mm, "end": v(7.57, 3.13) * mm});
            skLineSegment(sketch, "E732", {"start": v(7.57, 3.13) * mm, "end": v(7.68, 3.13) * mm});
            skLineSegment(sketch, "E733", {"start": v(7.68, 3.13) * mm, "end": v(7.77, 3.12) * mm});
            skLineSegment(sketch, "E734", {"start": v(7.77, 3.12) * mm, "end": v(7.86, 3.1) * mm});
            skLineSegment(sketch, "E735", {"start": v(7.86, 3.1) * mm, "end": v(7.94, 3.07) * mm});
            skLineSegment(sketch, "E736", {"start": v(7.94, 3.07) * mm, "end": v(8, 3.04) * mm});
            skLineSegment(sketch, "E737", {"start": v(8, 3.04) * mm, "end": v(8.04, 3) * mm});
            skLineSegment(sketch, "E738", {"start": v(8.04, 3) * mm, "end": v(8.05, 2.98) * mm});
            skLineSegment(sketch, "E739", {"start": v(8.05, 2.98) * mm, "end": v(8.04, 2.96) * mm});
            skLineSegment(sketch, "E740", {"start": v(8.04, 2.96) * mm, "end": v(8.03, 2.94) * mm});
            skLineSegment(sketch, "E741", {"start": v(8.03, 2.94) * mm, "end": v(8.02, 2.92) * mm});
            skLineSegment(sketch, "E742", {"start": v(8.02, 2.92) * mm, "end": v(8, 2.89) * mm});
            skLineSegment(sketch, "E743", {"start": v(8, 2.89) * mm, "end": v(8, 2.84) * mm});
            skLineSegment(sketch, "E744", {"start": v(8, 2.84) * mm, "end": v(7.94, 2.7) * mm});
            skLineSegment(sketch, "E745", {"start": v(7.94, 2.7) * mm, "end": v(7.86, 2.53) * mm});
            skLineSegment(sketch, "E746", {"start": v(7.86, 2.53) * mm, "end": v(7.77, 2.36) * mm});
            skLineSegment(sketch, "E747", {"start": v(7.77, 2.36) * mm, "end": v(7.67, 2.19) * mm});
            skLineSegment(sketch, "E748", {"start": v(7.67, 2.19) * mm, "end": v(7.6, 2.07) * mm});
            skLineSegment(sketch, "E749", {"start": v(7.6, 2.07) * mm, "end": v(7.55, 1.98) * mm});
            skLineSegment(sketch, "E750", {"start": v(7.55, 1.98) * mm, "end": v(7.5, 1.9) * mm});
            skLineSegment(sketch, "E751", {"start": v(7.5, 1.9) * mm, "end": v(7.47, 1.82) * mm});
            skLineSegment(sketch, "E752", {"start": v(7.47, 1.82) * mm, "end": v(7.44, 1.77) * mm});
            skLineSegment(sketch, "E753", {"start": v(7.44, 1.77) * mm, "end": v(7.4, 1.72) * mm});
            skLineSegment(sketch, "E754", {"start": v(7.4, 1.72) * mm, "end": v(7.38, 1.68) * mm});
            skLineSegment(sketch, "E755", {"start": v(7.38, 1.68) * mm, "end": v(7.36, 1.65) * mm});
            skLineSegment(sketch, "E756", {"start": v(7.36, 1.65) * mm, "end": v(7.31, 1.58) * mm});
            skLineSegment(sketch, "E757", {"start": v(7.31, 1.58) * mm, "end": v(7.26, 1.5) * mm});
            skLineSegment(sketch, "E758", {"start": v(7.26, 1.5) * mm, "end": v(7.2, 1.41) * mm});
            skLineSegment(sketch, "E759", {"start": v(7.2, 1.41) * mm, "end": v(7.16, 1.35) * mm});
            skLineSegment(sketch, "E760", {"start": v(7.16, 1.35) * mm, "end": v(7.13, 1.3) * mm});
            skLineSegment(sketch, "E761", {"start": v(7.13, 1.3) * mm, "end": v(7.07, 1.24) * mm});
            skLineSegment(sketch, "E762", {"start": v(7.07, 1.24) * mm, "end": v(7, 1.18) * mm});
            skLineSegment(sketch, "E763", {"start": v(7, 1.18) * mm, "end": v(6.94, 1.1) * mm});
            skLineSegment(sketch, "E764", {"start": v(6.94, 1.1) * mm, "end": v(6.86, 1.04) * mm});
            skLineSegment(sketch, "E765", {"start": v(6.86, 1.04) * mm, "end": v(6.79, 0.99) * mm});
            skLineSegment(sketch, "E766", {"start": v(6.79, 0.99) * mm, "end": v(6.72, 0.94) * mm});
            skLineSegment(sketch, "E767", {"start": v(6.72, 0.94) * mm, "end": v(6.66, 0.91) * mm});
            skLineSegment(sketch, "E768", {"start": v(6.66, 0.91) * mm, "end": v(6.6, 0.89) * mm});
            skLineSegment(sketch, "E769", {"start": v(6.6, 0.89) * mm, "end": v(6.52, 0.86) * mm});
            skLineSegment(sketch, "E770", {"start": v(6.52, 0.86) * mm, "end": v(6.46, 0.85) * mm});
            skLineSegment(sketch, "E771", {"start": v(6.46, 0.85) * mm, "end": v(6.43, 0.85) * mm});
            skLineSegment(sketch, "E772", {"start": v(6.43, 0.85) * mm, "end": v(6.41, 0.85) * mm});
            skLineSegment(sketch, "E773", {"start": v(6.41, 0.85) * mm, "end": v(6.37, 0.85) * mm});
            skLineSegment(sketch, "E774", {"start": v(6.37, 0.85) * mm, "end": v(6.32, 0.85) * mm});
            skLineSegment(sketch, "E775", {"start": v(6.32, 0.85) * mm, "end": v(6.26, 0.85) * mm});
            skLineSegment(sketch, "E776", {"start": v(6.26, 0.85) * mm, "end": v(6.16, 0.84) * mm});
            skLineSegment(sketch, "E777", {"start": v(6.16, 0.84) * mm, "end": v(6.1, 0.83) * mm});
            skLineSegment(sketch, "E778", {"start": v(6.1, 0.83) * mm, "end": v(6.03, 0.81) * mm});
            skLineSegment(sketch, "E779", {"start": v(6.03, 0.81) * mm, "end": v(5.95, 0.78) * mm});
            skLineSegment(sketch, "E780", {"start": v(5.95, 0.78) * mm, "end": v(5.84, 0.74) * mm});
            skLineSegment(sketch, "E781", {"start": v(5.84, 0.74) * mm, "end": v(5.76, 0.7) * mm});
            skLineSegment(sketch, "E782", {"start": v(5.76, 0.7) * mm, "end": v(5.7, 0.67) * mm});
            skLineSegment(sketch, "E783", {"start": v(5.7, 0.67) * mm, "end": v(5.63, 0.63) * mm});
            skLineSegment(sketch, "E784", {"start": v(5.63, 0.63) * mm, "end": v(5.49, 0.53) * mm});
            skLineSegment(sketch, "E785", {"start": v(5.49, 0.53) * mm, "end": v(5.32, 0.43) * mm});
            skLineSegment(sketch, "E786", {"start": v(5.32, 0.43) * mm, "end": v(5.14, 0.33) * mm});
            skLineSegment(sketch, "E787", {"start": v(5.14, 0.33) * mm, "end": v(4.96, 0.23) * mm});
            skLineSegment(sketch, "E788", {"start": v(4.96, 0.23) * mm, "end": v(4.8, 0.17) * mm});
            skLineSegment(sketch, "E789", {"start": v(4.8, 0.17) * mm, "end": v(4.6, 0.1) * mm});
            skLineSegment(sketch, "E790", {"start": v(4.6, 0.1) * mm, "end": v(4.4, 0.06) * mm});
            skLineSegment(sketch, "E791", {"start": v(4.4, 0.06) * mm, "end": v(4.23, 0.03) * mm});
            skLineSegment(sketch, "E792", {"start": v(4.23, 0.03) * mm, "end": v(4.18, 0.03) * mm});
            skLineSegment(sketch, "E793", {"start": v(4.18, 0.03) * mm, "end": v(4.14, 0.02) * mm});
            skLineSegment(sketch, "E794", {"start": v(4.14, 0.02) * mm, "end": v(4.1, 0.02) * mm});
            skLineSegment(sketch, "E795", {"start": v(4.1, 0.02) * mm, "end": v(4.1, 0.02) * mm});
            skLineSegment(sketch, "E796", {"start": v(4.1, 0.02) * mm, "end": v(4.1, 0.01) * mm});
            skLineSegment(sketch, "E797", {"start": v(4.1, 0.01) * mm, "end": v(4.12, 0) * mm});
            skLineSegment(sketch, "E798", {"start": v(4.12, 0) * mm, "end": v(4.16, -0.03) * mm});
            skLineSegment(sketch, "E799", {"start": v(4.16, -0.03) * mm, "end": v(4.22, -0.05) * mm});
            skLineSegment(sketch, "E800", {"start": v(4.22, -0.05) * mm, "end": v(4.29, -0.08) * mm});
            skLineSegment(sketch, "E801", {"start": v(4.29, -0.08) * mm, "end": v(4.37, -0.1) * mm});
            skLineSegment(sketch, "E802", {"start": v(4.37, -0.1) * mm, "end": v(4.45, -0.14) * mm});
            skLineSegment(sketch, "E803", {"start": v(4.45, -0.14) * mm, "end": v(4.54, -0.17) * mm});
            skLineSegment(sketch, "E804", {"start": v(4.54, -0.17) * mm, "end": v(4.63, -0.2) * mm});
            skLineSegment(sketch, "E805", {"start": v(4.63, -0.2) * mm, "end": v(4.7, -0.22) * mm});
            skLineSegment(sketch, "E806", {"start": v(4.7, -0.22) * mm, "end": v(4.77, -0.24) * mm});
            skLineSegment(sketch, "E807", {"start": v(4.77, -0.24) * mm, "end": v(4.85, -0.26) * mm});
            skLineSegment(sketch, "E808", {"start": v(4.85, -0.26) * mm, "end": v(4.94, -0.28) * mm});
            skLineSegment(sketch, "E809", {"start": v(4.94, -0.28) * mm, "end": v(5.06, -0.3) * mm});
            skLineSegment(sketch, "E810", {"start": v(5.06, -0.3) * mm, "end": v(5.21, -0.34) * mm});
            skLineSegment(sketch, "E811", {"start": v(5.21, -0.34) * mm, "end": v(5.41, -0.38) * mm});
            skLineSegment(sketch, "E812", {"start": v(5.41, -0.38) * mm, "end": v(5.54, -0.4) * mm});
            skLineSegment(sketch, "E813", {"start": v(5.54, -0.4) * mm, "end": v(5.7, -0.42) * mm});
            skLineSegment(sketch, "E814", {"start": v(5.7, -0.42) * mm, "end": v(5.9, -0.43) * mm});
            skLineSegment(sketch, "E815", {"start": v(5.9, -0.43) * mm, "end": v(6.14, -0.44) * mm});
            skLineSegment(sketch, "E816", {"start": v(6.14, -0.44) * mm, "end": v(6.36, -0.45) * mm});
            skLineSegment(sketch, "E817", {"start": v(6.36, -0.45) * mm, "end": v(6.55, -0.46) * mm});
            skLineSegment(sketch, "E818", {"start": v(6.55, -0.46) * mm, "end": v(6.73, -0.47) * mm});
            skLineSegment(sketch, "E819", {"start": v(6.73, -0.47) * mm, "end": v(6.92, -0.49) * mm});
            skLineSegment(sketch, "E820", {"start": v(6.92, -0.49) * mm, "end": v(7.01, -0.5) * mm});
            skLineSegment(sketch, "E821", {"start": v(7.01, -0.5) * mm, "end": v(7.12, -0.5) * mm});
            skLineSegment(sketch, "E822", {"start": v(7.12, -0.5) * mm, "end": v(7.23, -0.52) * mm});
            skLineSegment(sketch, "E823", {"start": v(7.23, -0.52) * mm, "end": v(7.32, -0.52) * mm});
            skLineSegment(sketch, "E824", {"start": v(7.32, -0.52) * mm, "end": v(7.57, -0.54) * mm});
            skLineSegment(sketch, "E825", {"start": v(7.57, -0.54) * mm, "end": v(7.79, -0.57) * mm});
            skLineSegment(sketch, "E826", {"start": v(7.79, -0.57) * mm, "end": v(7.97, -0.62) * mm});
            skLineSegment(sketch, "E827", {"start": v(7.97, -0.62) * mm, "end": v(8.12, -0.67) * mm});
            skLineSegment(sketch, "E828", {"start": v(8.12, -0.67) * mm, "end": v(8.2, -0.71) * mm});
            skLineSegment(sketch, "E829", {"start": v(8.2, -0.71) * mm, "end": v(8.29, -0.76) * mm});
            skLineSegment(sketch, "E830", {"start": v(8.29, -0.76) * mm, "end": v(8.37, -0.8) * mm});
            skLineSegment(sketch, "E831", {"start": v(8.37, -0.8) * mm, "end": v(8.42, -0.84) * mm});
            skLineSegment(sketch, "E832", {"start": v(8.42, -0.84) * mm, "end": v(8.55, -0.95) * mm});
            skLineSegment(sketch, "E833", {"start": v(8.55, -0.95) * mm, "end": v(8.67, -1.06) * mm});
            skLineSegment(sketch, "E834", {"start": v(8.67, -1.06) * mm, "end": v(8.76, -1.16) * mm});
            skLineSegment(sketch, "E835", {"start": v(8.76, -1.16) * mm, "end": v(8.83, -1.25) * mm});
            skLineSegment(sketch, "E836", {"start": v(8.83, -1.25) * mm, "end": v(8.94, -1.46) * mm});
            skLineSegment(sketch, "E837", {"start": v(8.94, -1.46) * mm, "end": v(9.01, -1.65) * mm});
            skLineSegment(sketch, "E838", {"start": v(9.01, -1.65) * mm, "end": v(9.06, -1.82) * mm});
            skLineSegment(sketch, "E839", {"start": v(9.06, -1.82) * mm, "end": v(9.07, -2) * mm});
            skLineSegment(sketch, "E840", {"start": v(9.07, -2) * mm, "end": v(9.07, -2.07) * mm});
            skLineSegment(sketch, "E841", {"start": v(9.07, -2.07) * mm, "end": v(9.06, -2.12) * mm});
            skLineSegment(sketch, "E842", {"start": v(9.06, -2.12) * mm, "end": v(9.06, -2.15) * mm});
            skLineSegment(sketch, "E843", {"start": v(9.06, -2.15) * mm, "end": v(9.05, -2.17) * mm});
            skLineSegment(sketch, "E844", {"start": v(9.05, -2.17) * mm, "end": v(9.02, -2.21) * mm});
            skLineSegment(sketch, "E845", {"start": v(9.02, -2.21) * mm, "end": v(9, -2.25) * mm});
            skLineSegment(sketch, "E846", {"start": v(9, -2.25) * mm, "end": v(8.97, -2.28) * mm});
            skLineSegment(sketch, "E847", {"start": v(8.97, -2.28) * mm, "end": v(8.95, -2.3) * mm});
            skLineSegment(sketch, "E848", {"start": v(8.95, -2.3) * mm, "end": v(8.91, -2.3) * mm});
            skLineSegment(sketch, "E849", {"start": v(8.91, -2.3) * mm, "end": v(8.83, -2.31) * mm});
            skLineSegment(sketch, "E850", {"start": v(8.83, -2.31) * mm, "end": v(8.71, -2.3) * mm});
            skLineSegment(sketch, "E851", {"start": v(8.71, -2.3) * mm, "end": v(8.57, -2.3) * mm});
            skLineSegment(sketch, "E852", {"start": v(8.57, -2.3) * mm, "end": v(8.42, -2.28) * mm});
            skLineSegment(sketch, "E853", {"start": v(8.42, -2.28) * mm, "end": v(8.25, -2.27) * mm});
            skLineSegment(sketch, "E854", {"start": v(8.25, -2.27) * mm, "end": v(8.08, -2.24) * mm});
            skLineSegment(sketch, "E855", {"start": v(8.08, -2.24) * mm, "end": v(7.92, -2.22) * mm});
            skLineSegment(sketch, "E856", {"start": v(7.92, -2.22) * mm, "end": v(7.77, -2.2) * mm});
            skLineSegment(sketch, "E857", {"start": v(7.77, -2.2) * mm, "end": v(7.66, -2.18) * mm});
            skLineSegment(sketch, "E858", {"start": v(7.66, -2.18) * mm, "end": v(7.57, -2.17) * mm});
            skLineSegment(sketch, "E859", {"start": v(7.57, -2.17) * mm, "end": v(7.47, -2.17) * mm});
            skLineSegment(sketch, "E860", {"start": v(7.47, -2.17) * mm, "end": v(7.3, -2.17) * mm});
            skLineSegment(sketch, "E861", {"start": v(7.3, -2.17) * mm, "end": v(7.06, -2.23) * mm});
            skLineSegment(sketch, "E862", {"start": v(7.06, -2.23) * mm, "end": v(7, -2.25) * mm});
            skLineSegment(sketch, "E863", {"start": v(7, -2.25) * mm, "end": v(6.92, -2.27) * mm});
            skLineSegment(sketch, "E864", {"start": v(6.92, -2.27) * mm, "end": v(6.84, -2.29) * mm});
            skLineSegment(sketch, "E865", {"start": v(6.84, -2.29) * mm, "end": v(6.76, -2.31) * mm});
            skLineSegment(sketch, "E866", {"start": v(6.76, -2.31) * mm, "end": v(6.66, -2.34) * mm});
            skLineSegment(sketch, "E867", {"start": v(6.66, -2.34) * mm, "end": v(6.55, -2.37) * mm});
            skLineSegment(sketch, "E868", {"start": v(6.55, -2.37) * mm, "end": v(6.4, -2.41) * mm});
            skLineSegment(sketch, "E869", {"start": v(6.4, -2.41) * mm, "end": v(6.24, -2.46) * mm});
            skLineSegment(sketch, "E870", {"start": v(6.24, -2.46) * mm, "end": v(6.2, -2.48) * mm});
            skLineSegment(sketch, "E871", {"start": v(6.2, -2.48) * mm, "end": v(6.14, -2.5) * mm});
            skLineSegment(sketch, "E872", {"start": v(6.14, -2.5) * mm, "end": v(6.08, -2.52) * mm});
            skLineSegment(sketch, "E873", {"start": v(6.08, -2.52) * mm, "end": v(6.02, -2.53) * mm});
            skLineSegment(sketch, "E874", {"start": v(6.02, -2.53) * mm, "end": v(5.8, -2.61) * mm});
            skLineSegment(sketch, "E875", {"start": v(5.8, -2.61) * mm, "end": v(5.55, -2.69) * mm});
            skLineSegment(sketch, "E876", {"start": v(5.55, -2.69) * mm, "end": v(5.32, -2.75) * mm});
            skLineSegment(sketch, "E877", {"start": v(5.32, -2.75) * mm, "end": v(5.13, -2.79) * mm});
            skLineSegment(sketch, "E878", {"start": v(5.13, -2.79) * mm, "end": v(4.94, -2.82) * mm});
            skLineSegment(sketch, "E879", {"start": v(4.94, -2.82) * mm, "end": v(4.74, -2.84) * mm});
            skLineSegment(sketch, "E880", {"start": v(4.74, -2.84) * mm, "end": v(4.55, -2.86) * mm});
            skLineSegment(sketch, "E881", {"start": v(4.55, -2.86) * mm, "end": v(4.36, -2.87) * mm});
            skLineSegment(sketch, "E882", {"start": v(4.36, -2.87) * mm, "end": v(4.18, -2.88) * mm});
            skLineSegment(sketch, "E883", {"start": v(4.18, -2.88) * mm, "end": v(4, -2.88) * mm});
            skLineSegment(sketch, "E884", {"start": v(4, -2.88) * mm, "end": v(3.85, -2.87) * mm});
            skLineSegment(sketch, "E885", {"start": v(3.85, -2.87) * mm, "end": v(3.72, -2.86) * mm});
            skLineSegment(sketch, "E886", {"start": v(3.72, -2.86) * mm, "end": v(3.65, -2.85) * mm});
            skLineSegment(sketch, "E887", {"start": v(3.65, -2.85) * mm, "end": v(3.6, -2.84) * mm});
            skLineSegment(sketch, "E888", {"start": v(3.6, -2.84) * mm, "end": v(3.56, -2.83) * mm});
            skLineSegment(sketch, "E889", {"start": v(3.56, -2.83) * mm, "end": v(3.54, -2.83) * mm});
            skLineSegment(sketch, "E890", {"start": v(3.54, -2.83) * mm, "end": v(3.52, -2.82) * mm});
            skLineSegment(sketch, "E891", {"start": v(3.52, -2.82) * mm, "end": v(3.48, -2.82) * mm});
            skLineSegment(sketch, "E892", {"start": v(3.48, -2.82) * mm, "end": v(3.43, -2.81) * mm});
            skLineSegment(sketch, "E893", {"start": v(3.43, -2.81) * mm, "end": v(3.36, -2.8) * mm});
            skLineSegment(sketch, "E894", {"start": v(3.36, -2.8) * mm, "end": v(3.2, -2.79) * mm});
            skLineSegment(sketch, "E895", {"start": v(3.2, -2.79) * mm, "end": v(3.06, -2.76) * mm});
            skLineSegment(sketch, "E896", {"start": v(3.06, -2.76) * mm, "end": v(2.93, -2.73) * mm});
            skLineSegment(sketch, "E897", {"start": v(2.93, -2.73) * mm, "end": v(2.82, -2.7) * mm});
            skLineSegment(sketch, "E898", {"start": v(2.82, -2.7) * mm, "end": v(2.78, -2.69) * mm});
            skLineSegment(sketch, "E899", {"start": v(2.78, -2.69) * mm, "end": v(2.73, -2.67) * mm});
            skLineSegment(sketch, "E900", {"start": v(2.73, -2.67) * mm, "end": v(2.68, -2.66) * mm});
            skLineSegment(sketch, "E901", {"start": v(2.68, -2.66) * mm, "end": v(2.64, -2.64) * mm});
            skLineSegment(sketch, "E902", {"start": v(2.64, -2.64) * mm, "end": v(2.6, -2.63) * mm});
            skLineSegment(sketch, "E903", {"start": v(2.6, -2.63) * mm, "end": v(2.55, -2.61) * mm});
            skLineSegment(sketch, "E904", {"start": v(2.55, -2.61) * mm, "end": v(2.5, -2.59) * mm});
            skLineSegment(sketch, "E905", {"start": v(2.5, -2.59) * mm, "end": v(2.44, -2.56) * mm});
            skLineSegment(sketch, "E906", {"start": v(2.44, -2.56) * mm, "end": v(2.31, -2.5) * mm});
            skLineSegment(sketch, "E907", {"start": v(2.31, -2.5) * mm, "end": v(2.2, -2.45) * mm});
            skLineSegment(sketch, "E908", {"start": v(2.2, -2.45) * mm, "end": v(2.14, -2.43) * mm});
            skLineSegment(sketch, "E909", {"start": v(2.14, -2.43) * mm, "end": v(2.08, -2.4) * mm});
            skLineSegment(sketch, "E910", {"start": v(2.08, -2.4) * mm, "end": v(2.02, -2.37) * mm});
            skLineSegment(sketch, "E911", {"start": v(2.02, -2.37) * mm, "end": v(1.98, -2.34) * mm});
            skLineSegment(sketch, "E912", {"start": v(1.98, -2.34) * mm, "end": v(1.93, -2.3) * mm});
            skLineSegment(sketch, "E913", {"start": v(1.93, -2.3) * mm, "end": v(1.85, -2.26) * mm});
            skLineSegment(sketch, "E914", {"start": v(1.85, -2.26) * mm, "end": v(1.76, -2.22) * mm});
            skLineSegment(sketch, "E915", {"start": v(1.76, -2.22) * mm, "end": v(1.67, -2.17) * mm});
            skLineSegment(sketch, "E916", {"start": v(1.67, -2.17) * mm, "end": v(1.58, -2.12) * mm});
            skLineSegment(sketch, "E917", {"start": v(1.58, -2.12) * mm, "end": v(1.5, -2.07) * mm});
            skLineSegment(sketch, "E918", {"start": v(1.5, -2.07) * mm, "end": v(1.43, -2.04) * mm});
            skLineSegment(sketch, "E919", {"start": v(1.43, -2.04) * mm, "end": v(1.4, -2) * mm});
            skLineSegment(sketch, "E920", {"start": v(1.4, -2) * mm, "end": v(1.37, -2) * mm});
            skLineSegment(sketch, "E921", {"start": v(1.37, -2) * mm, "end": v(1.34, -1.97) * mm});
            skLineSegment(sketch, "E922", {"start": v(1.34, -1.97) * mm, "end": v(1.31, -1.95) * mm});
            skLineSegment(sketch, "E923", {"start": v(1.31, -1.95) * mm, "end": v(1.3, -1.94) * mm});
            skLineSegment(sketch, "E924", {"start": v(1.3, -1.94) * mm, "end": v(1.26, -1.92) * mm});
            skLineSegment(sketch, "E925", {"start": v(1.26, -1.92) * mm, "end": v(1.2, -1.89) * mm});
            skLineSegment(sketch, "E926", {"start": v(1.2, -1.89) * mm, "end": v(1.13, -1.84) * mm});
            skLineSegment(sketch, "E927", {"start": v(1.13, -1.84) * mm, "end": v(1.06, -1.8) * mm});
            skLineSegment(sketch, "E928", {"start": v(1.06, -1.8) * mm, "end": v(0.94, -1.71) * mm});
            skLineSegment(sketch, "E929", {"start": v(0.94, -1.71) * mm, "end": v(0.85, -1.65) * mm});
            skLineSegment(sketch, "E930", {"start": v(0.85, -1.65) * mm, "end": v(0.77, -1.58) * mm});
            skLineSegment(sketch, "E931", {"start": v(0.77, -1.58) * mm, "end": v(0.69, -1.5) * mm});
            skLineSegment(sketch, "E932", {"start": v(0.69, -1.5) * mm, "end": v(0.67, -1.49) * mm});
            skLineSegment(sketch, "E933", {"start": v(0.67, -1.49) * mm, "end": v(0.65, -1.48) * mm});
            skLineSegment(sketch, "E934", {"start": v(0.65, -1.48) * mm, "end": v(0.64, -1.47) * mm});
            skLineSegment(sketch, "E935", {"start": v(0.64, -1.47) * mm, "end": v(0.63, -1.47) * mm});
            skLineSegment(sketch, "E936", {"start": v(0.63, -1.47) * mm, "end": v(0.63, -1.49) * mm});
            skLineSegment(sketch, "E937", {"start": v(0.63, -1.49) * mm, "end": v(0.62, -1.53) * mm});
            skLineSegment(sketch, "E938", {"start": v(0.62, -1.53) * mm, "end": v(0.62, -1.6) * mm});
            skLineSegment(sketch, "E939", {"start": v(0.62, -1.6) * mm, "end": v(0.6, -1.67) * mm});
            skLineSegment(sketch, "E940", {"start": v(0.6, -1.67) * mm, "end": v(0.57, -1.94) * mm});
            skLineSegment(sketch, "E941", {"start": v(0.57, -1.94) * mm, "end": v(0.53, -2.18) * mm});
            skLineSegment(sketch, "E942", {"start": v(0.53, -2.18) * mm, "end": v(0.49, -2.42) * mm});
            skLineSegment(sketch, "E943", {"start": v(0.49, -2.42) * mm, "end": v(0.43, -2.64) * mm});
            skLineSegment(sketch, "E944", {"start": v(0.43, -2.64) * mm, "end": v(0.37, -2.86) * mm});
            skLineSegment(sketch, "E945", {"start": v(0.37, -2.86) * mm, "end": v(0.3, -3.04) * mm});
            skLineSegment(sketch, "E946", {"start": v(0.3, -3.04) * mm, "end": v(0.22, -3.18) * mm});
            skLineSegment(sketch, "E947", {"start": v(0.22, -3.18) * mm, "end": v(0.13, -3.3) * mm});
            skLineSegment(sketch, "E948", {"start": v(0.13, -3.3) * mm, "end": v(0.06, -3.37) * mm});
            skLineSegment(sketch, "E949", {"start": v(0.06, -3.37) * mm, "end": v(0.1, -3.44) * mm});
            skLineSegment(sketch, "E950", {"start": v(0.1, -3.44) * mm, "end": v(0.18, -3.6) * mm});
            skLineSegment(sketch, "E951", {"start": v(0.18, -3.6) * mm, "end": v(0.2, -3.8) * mm});
            skLineSegment(sketch, "E952", {"start": v(0.2, -3.8) * mm, "end": v(0.15, -3.98) * mm});
            skLineSegment(sketch, "E953", {"start": v(0.15, -3.98) * mm, "end": v(0.07, -4.14) * mm});
            skLineSegment(sketch, "E954", {"start": v(0.07, -4.14) * mm, "end": v(0.03, -4.19) * mm});
            skLineSegment(sketch, "E955", {"start": v(0.03, -4.19) * mm, "end": v(0.06, -4.25) * mm});
            skLineSegment(sketch, "E956", {"start": v(0.06, -4.25) * mm, "end": v(0.11, -4.4) * mm});
            skLineSegment(sketch, "E957", {"start": v(0.11, -4.4) * mm, "end": v(0.13, -4.54) * mm});
            skLineSegment(sketch, "E958", {"start": v(0.13, -4.54) * mm, "end": v(0.12, -4.67) * mm});
            skLineSegment(sketch, "E959", {"start": v(0.12, -4.67) * mm, "end": v(0.09, -4.8) * mm});
            skLineSegment(sketch, "E960", {"start": v(0.09, -4.8) * mm, "end": v(0.03, -4.92) * mm});
            skLineSegment(sketch, "E961", {"start": v(0.03, -4.92) * mm, "end": v(-0.03, -5) * mm});
            skLineSegment(sketch, "E962", {"start": v(-0.03, -5) * mm, "end": v(-0.05, -5.03) * mm});
            skLineSegment(sketch, "E963", {"start": v(-0.05, -5.03) * mm, "end": v(-0.07, -5.05) * mm});
            skLineSegment(sketch, "E964", {"start": v(-0.07, -5.05) * mm, "end": v(-0.08, -5.07) * mm});
            skLineSegment(sketch, "E965", {"start": v(-0.08, -5.07) * mm, "end": v(-0.08, -5.07) * mm});
            skLineSegment(sketch, "E966", {"start": v(-0.08, -5.07) * mm, "end": v(-0.05, -5.09) * mm});
            skLineSegment(sketch, "E967", {"start": v(-0.05, -5.09) * mm, "end": v(-0.02, -5.1) * mm});
            skLineSegment(sketch, "E968", {"start": v(-0.02, -5.1) * mm, "end": v(0.01, -5.14) * mm});
            skLineSegment(sketch, "E969", {"start": v(0.01, -5.14) * mm, "end": v(0.03, -5.16) * mm});
            skLineSegment(sketch, "E970", {"start": v(0.03, -5.16) * mm, "end": v(0.07, -5.23) * mm});
            skLineSegment(sketch, "E971", {"start": v(0.07, -5.23) * mm, "end": v(0.09, -5.3) * mm});
            skLineSegment(sketch, "E972", {"start": v(0.09, -5.3) * mm, "end": v(0.1, -5.37) * mm});
            skLineSegment(sketch, "E973", {"start": v(0.1, -5.37) * mm, "end": v(0.1, -5.47) * mm});
            skLineSegment(sketch, "E974", {"start": v(0.1, -5.47) * mm, "end": v(0.1, -5.54) * mm});
            skLineSegment(sketch, "E975", {"start": v(0.1, -5.54) * mm, "end": v(0.1, -5.6) * mm});
            skLineSegment(sketch, "E976", {"start": v(0.1, -5.6) * mm, "end": v(0.09, -5.63) * mm});
            skLineSegment(sketch, "E977", {"start": v(0.09, -5.63) * mm, "end": v(0.07, -5.67) * mm});
            skLineSegment(sketch, "E978", {"start": v(0.07, -5.67) * mm, "end": v(0.06, -5.7) * mm});
            skLineSegment(sketch, "E979", {"start": v(0.06, -5.7) * mm, "end": v(0.04, -5.72) * mm});
            skLineSegment(sketch, "E980", {"start": v(0.04, -5.72) * mm, "end": v(0.02, -5.75) * mm});
            skLineSegment(sketch, "E981", {"start": v(0.02, -5.75) * mm, "end": v(0, -5.76) * mm});
            skLineSegment(sketch, "E982", {"start": v(0, -5.76) * mm, "end": v(-0.08, -5.8) * mm});
            skLineSegment(sketch, "E983", {"start": v(-0.08, -5.8) * mm, "end": v(-0.2, -5.84) * mm});
            skLineSegment(sketch, "E984", {"start": v(-0.2, -5.84) * mm, "end": v(-0.3, -5.85) * mm});
            skLineSegment(sketch, "E985", {"start": v(-0.3, -5.85) * mm, "end": v(-0.39, -5.84) * mm});
            skLineSegment(sketch, "E986", {"start": v(-0.19, -5.64) * mm, "end": v(-0.17, -5.63) * mm});
            skLineSegment(sketch, "E987", {"start": v(-0.17, -5.63) * mm, "end": v(-0.15, -5.62) * mm});
            skLineSegment(sketch, "E988", {"start": v(-0.15, -5.62) * mm, "end": v(-0.12, -5.6) * mm});
            skLineSegment(sketch, "E989", {"start": v(-0.12, -5.6) * mm, "end": v(-0.1, -5.56) * mm});
            skLineSegment(sketch, "E990", {"start": v(-0.1, -5.56) * mm, "end": v(-0.07, -5.5) * mm});
            skLineSegment(sketch, "E991", {"start": v(-0.07, -5.5) * mm, "end": v(-0.06, -5.45) * mm});
            skLineSegment(sketch, "E992", {"start": v(-0.06, -5.45) * mm, "end": v(-0.07, -5.4) * mm});
            skLineSegment(sketch, "E993", {"start": v(-0.07, -5.4) * mm, "end": v(-0.1, -5.32) * mm});
            skLineSegment(sketch, "E994", {"start": v(-0.1, -5.32) * mm, "end": v(-0.12, -5.28) * mm});
            skLineSegment(sketch, "E995", {"start": v(-0.12, -5.28) * mm, "end": v(-0.13, -5.25) * mm});
            skLineSegment(sketch, "E996", {"start": v(-0.13, -5.25) * mm, "end": v(-0.15, -5.23) * mm});
            skLineSegment(sketch, "E997", {"start": v(-0.15, -5.23) * mm, "end": v(-0.16, -5.22) * mm});
            skLineSegment(sketch, "E998", {"start": v(-0.16, -5.22) * mm, "end": v(-0.18, -5.2) * mm});
            skLineSegment(sketch, "E999", {"start": v(-0.18, -5.2) * mm, "end": v(-0.2, -5.2) * mm});
            skLineSegment(sketch, "E1000", {"start": v(-0.2, -5.2) * mm, "end": v(-0.22, -5.2) * mm});
            skLineSegment(sketch, "E1001", {"start": v(-0.22, -5.2) * mm, "end": v(-0.25, -5.2) * mm});
            skLineSegment(sketch, "E1002", {"start": v(-0.25, -5.2) * mm, "end": v(-0.3, -5.2) * mm});
            skLineSegment(sketch, "E1003", {"start": v(-0.3, -5.2) * mm, "end": v(-0.33, -5.2) * mm});
            skLineSegment(sketch, "E1004", {"start": v(-0.33, -5.2) * mm, "end": v(-0.34, -5.21) * mm});
            skLineSegment(sketch, "E1005", {"start": v(-0.34, -5.21) * mm, "end": v(-0.36, -5.23) * mm});
            skLineSegment(sketch, "E1006", {"start": v(-0.36, -5.23) * mm, "end": v(-0.4, -5.3) * mm});
            skLineSegment(sketch, "E1007", {"start": v(-0.4, -5.3) * mm, "end": v(-0.43, -5.38) * mm});
            skLineSegment(sketch, "E1008", {"start": v(-0.43, -5.38) * mm, "end": v(-0.44, -5.46) * mm});
            skLineSegment(sketch, "E1009", {"start": v(-0.44, -5.46) * mm, "end": v(-0.42, -5.53) * mm});
            skLineSegment(sketch, "E1010", {"start": v(-0.42, -5.53) * mm, "end": v(-0.4, -5.56) * mm});
            skLineSegment(sketch, "E1011", {"start": v(-0.4, -5.56) * mm, "end": v(-0.37, -5.6) * mm});
            skLineSegment(sketch, "E1012", {"start": v(-0.37, -5.6) * mm, "end": v(-0.31, -5.64) * mm});
            skLineSegment(sketch, "E1013", {"start": v(-0.31, -5.64) * mm, "end": v(-0.26, -5.66) * mm});
            skLineSegment(sketch, "E1014", {"start": v(-0.26, -5.66) * mm, "end": v(-0.22, -5.66) * mm});
            skLineSegment(sketch, "E1015", {"start": v(-0.22, -5.66) * mm, "end": v(-0.19, -5.64) * mm});
            skLineSegment(sketch, "E1016", {"start": v(-0.18, -4.89) * mm, "end": v(-0.15, -4.88) * mm});
            skLineSegment(sketch, "E1017", {"start": v(-0.15, -4.88) * mm, "end": v(-0.1, -4.84) * mm});
            skLineSegment(sketch, "E1018", {"start": v(-0.1, -4.84) * mm, "end": v(-0.07, -4.79) * mm});
            skLineSegment(sketch, "E1019", {"start": v(-0.07, -4.79) * mm, "end": v(-0.03, -4.72) * mm});
            skLineSegment(sketch, "E1020", {"start": v(-0.03, -4.72) * mm, "end": v(0, -4.68) * mm});
            skLineSegment(sketch, "E1021", {"start": v(0, -4.68) * mm, "end": v(0, -4.64) * mm});
            skLineSegment(sketch, "E1022", {"start": v(0, -4.64) * mm, "end": v(0, -4.61) * mm});
            skLineSegment(sketch, "E1023", {"start": v(0, -4.61) * mm, "end": v(0, -4.58) * mm});
            skLineSegment(sketch, "E1024", {"start": v(0, -4.58) * mm, "end": v(-0.02, -4.47) * mm});
            skLineSegment(sketch, "E1025", {"start": v(-0.02, -4.47) * mm, "end": v(-0.1, -4.36) * mm});
            skLineSegment(sketch, "E1026", {"start": v(-0.1, -4.36) * mm, "end": v(-0.14, -4.32) * mm});
            skLineSegment(sketch, "E1027", {"start": v(-0.14, -4.32) * mm, "end": v(-0.17, -4.3) * mm});
            skLineSegment(sketch, "E1028", {"start": v(-0.17, -4.3) * mm, "end": v(-0.2, -4.3) * mm});
            skLineSegment(sketch, "E1029", {"start": v(-0.2, -4.3) * mm, "end": v(-0.24, -4.31) * mm});
            skLineSegment(sketch, "E1030", {"start": v(-0.24, -4.31) * mm, "end": v(-0.3, -4.37) * mm});
            skLineSegment(sketch, "E1031", {"start": v(-0.3, -4.37) * mm, "end": v(-0.36, -4.46) * mm});
            skLineSegment(sketch, "E1032", {"start": v(-0.36, -4.46) * mm, "end": v(-0.39, -4.57) * mm});
            skLineSegment(sketch, "E1033", {"start": v(-0.39, -4.57) * mm, "end": v(-0.38, -4.68) * mm});
            skLineSegment(sketch, "E1034", {"start": v(-0.38, -4.68) * mm, "end": v(-0.37, -4.72) * mm});
            skLineSegment(sketch, "E1035", {"start": v(-0.37, -4.72) * mm, "end": v(-0.36, -4.77) * mm});
            skLineSegment(sketch, "E1036", {"start": v(-0.36, -4.77) * mm, "end": v(-0.34, -4.8) * mm});
            skLineSegment(sketch, "E1037", {"start": v(-0.34, -4.8) * mm, "end": v(-0.32, -4.84) * mm});
            skLineSegment(sketch, "E1038", {"start": v(-0.32, -4.84) * mm, "end": v(-0.3, -4.86) * mm});
            skLineSegment(sketch, "E1039", {"start": v(-0.3, -4.86) * mm, "end": v(-0.28, -4.88) * mm});
            skLineSegment(sketch, "E1040", {"start": v(-0.28, -4.88) * mm, "end": v(-0.25, -4.9) * mm});
            skLineSegment(sketch, "E1041", {"start": v(-0.25, -4.9) * mm, "end": v(-0.23, -4.9) * mm});
            skLineSegment(sketch, "E1042", {"start": v(-0.23, -4.9) * mm, "end": v(-0.2, -4.9) * mm});
            skLineSegment(sketch, "E1043", {"start": v(-0.2, -4.9) * mm, "end": v(-0.18, -4.89) * mm});
            skLineSegment(sketch, "E1044", {"start": v(-0.52, -4.81) * mm, "end": v(-0.53, -4.79) * mm});
            skLineSegment(sketch, "E1045", {"start": v(-0.53, -4.79) * mm, "end": v(-0.54, -4.77) * mm});
            skLineSegment(sketch, "E1046", {"start": v(-0.54, -4.77) * mm, "end": v(-0.55, -4.77) * mm});
            skLineSegment(sketch, "E1047", {"start": v(-0.55, -4.77) * mm, "end": v(-0.55, -4.77) * mm});
            skLineSegment(sketch, "E1048", {"start": v(-0.55, -4.77) * mm, "end": v(-0.54, -4.8) * mm});
            skLineSegment(sketch, "E1049", {"start": v(-0.54, -4.8) * mm, "end": v(-0.53, -4.82) * mm});
            skLineSegment(sketch, "E1050", {"start": v(-0.53, -4.82) * mm, "end": v(-0.52, -4.85) * mm});
            skLineSegment(sketch, "E1051", {"start": v(-0.52, -4.85) * mm, "end": v(-0.51, -4.86) * mm});
            skLineSegment(sketch, "E1052", {"start": v(-0.51, -4.86) * mm, "end": v(-0.51, -4.84) * mm});
            skLineSegment(sketch, "E1053", {"start": v(-0.51, -4.84) * mm, "end": v(-0.52, -4.81) * mm});
            skLineSegment(sketch, "E1054", {"start": v(-0.26, -4.09) * mm, "end": v(-0.22, -4.06) * mm});
            skLineSegment(sketch, "E1055", {"start": v(-0.22, -4.06) * mm, "end": v(-0.19, -4.03) * mm});
            skLineSegment(sketch, "E1056", {"start": v(-0.19, -4.03) * mm, "end": v(-0.15, -3.98) * mm});
            skLineSegment(sketch, "E1057", {"start": v(-0.15, -3.98) * mm, "end": v(-0.12, -3.92) * mm});
            skLineSegment(sketch, "E1058", {"start": v(-0.12, -3.92) * mm, "end": v(-0.1, -3.89) * mm});
            skLineSegment(sketch, "E1059", {"start": v(-0.1, -3.89) * mm, "end": v(-0.1, -3.86) * mm});
            skLineSegment(sketch, "E1060", {"start": v(-0.1, -3.86) * mm, "end": v(-0.1, -3.83) * mm});
            skLineSegment(sketch, "E1061", {"start": v(-0.1, -3.83) * mm, "end": v(-0.1, -3.8) * mm});
            skLineSegment(sketch, "E1062", {"start": v(-0.1, -3.8) * mm, "end": v(-0.13, -3.68) * mm});
            skLineSegment(sketch, "E1063", {"start": v(-0.13, -3.68) * mm, "end": v(-0.22, -3.57) * mm});
            skLineSegment(sketch, "E1064", {"start": v(-0.22, -3.57) * mm, "end": v(-0.24, -3.55) * mm});
            skLineSegment(sketch, "E1065", {"start": v(-0.24, -3.55) * mm, "end": v(-0.26, -3.54) * mm});
            skLineSegment(sketch, "E1066", {"start": v(-0.26, -3.54) * mm, "end": v(-0.29, -3.53) * mm});
            skLineSegment(sketch, "E1067", {"start": v(-0.29, -3.53) * mm, "end": v(-0.32, -3.54) * mm});
            skLineSegment(sketch, "E1068", {"start": v(-0.32, -3.54) * mm, "end": v(-0.42, -3.58) * mm});
            skLineSegment(sketch, "E1069", {"start": v(-0.42, -3.58) * mm, "end": v(-0.5, -3.66) * mm});
            skLineSegment(sketch, "E1070", {"start": v(-0.5, -3.66) * mm, "end": v(-0.56, -3.78) * mm});
            skLineSegment(sketch, "E1071", {"start": v(-0.56, -3.78) * mm, "end": v(-0.58, -3.92) * mm});
            skLineSegment(sketch, "E1072", {"start": v(-0.58, -3.92) * mm, "end": v(-0.58, -3.96) * mm});
            skLineSegment(sketch, "E1073", {"start": v(-0.58, -3.96) * mm, "end": v(-0.58, -3.98) * mm});
            skLineSegment(sketch, "E1074", {"start": v(-0.58, -3.98) * mm, "end": v(-0.57, -4) * mm});
            skLineSegment(sketch, "E1075", {"start": v(-0.57, -4) * mm, "end": v(-0.55, -4.03) * mm});
            skLineSegment(sketch, "E1076", {"start": v(-0.55, -4.03) * mm, "end": v(-0.52, -4.06) * mm});
            skLineSegment(sketch, "E1077", {"start": v(-0.52, -4.06) * mm, "end": v(-0.5, -4.08) * mm});
            skLineSegment(sketch, "E1078", {"start": v(-0.5, -4.08) * mm, "end": v(-0.46, -4.1) * mm});
            skLineSegment(sketch, "E1079", {"start": v(-0.46, -4.1) * mm, "end": v(-0.42, -4.1) * mm});
            skLineSegment(sketch, "E1080", {"start": v(-0.42, -4.1) * mm, "end": v(-0.37, -4.11) * mm});
            skLineSegment(sketch, "E1081", {"start": v(-0.37, -4.11) * mm, "end": v(-0.34, -4.11) * mm});
            skLineSegment(sketch, "E1082", {"start": v(-0.34, -4.11) * mm, "end": v(-0.3, -4.1) * mm});
            skLineSegment(sketch, "E1083", {"start": v(-0.3, -4.1) * mm, "end": v(-0.26, -4.09) * mm});
            skLineSegment(sketch, "E1084", {"start": v(-0.08, -3.08) * mm, "end": v(-0.06, -3.06) * mm});
            skLineSegment(sketch, "E1085", {"start": v(-0.06, -3.06) * mm, "end": v(-0.03, -3.04) * mm});
            skLineSegment(sketch, "E1086", {"start": v(-0.03, -3.04) * mm, "end": v(0, -3.02) * mm});
            skLineSegment(sketch, "E1087", {"start": v(0, -3.02) * mm, "end": v(0.02, -2.99) * mm});
            skLineSegment(sketch, "E1088", {"start": v(0.02, -2.99) * mm, "end": v(0.07, -2.93) * mm});
            skLineSegment(sketch, "E1089", {"start": v(0.07, -2.93) * mm, "end": v(0.11, -2.86) * mm});
            skLineSegment(sketch, "E1090", {"start": v(0.11, -2.86) * mm, "end": v(0.15, -2.78) * mm});
            skLineSegment(sketch, "E1091", {"start": v(0.15, -2.78) * mm, "end": v(0.19, -2.68) * mm});
            skLineSegment(sketch, "E1092", {"start": v(0.19, -2.68) * mm, "end": v(0.23, -2.57) * mm});
            skLineSegment(sketch, "E1093", {"start": v(0.23, -2.57) * mm, "end": v(0.26, -2.43) * mm});
            skLineSegment(sketch, "E1094", {"start": v(0.26, -2.43) * mm, "end": v(0.3, -2.26) * mm});
            skLineSegment(sketch, "E1095", {"start": v(0.3, -2.26) * mm, "end": v(0.35, -2.06) * mm});
            skLineSegment(sketch, "E1096", {"start": v(0.35, -2.06) * mm, "end": v(0.36, -1.99) * mm});
            skLineSegment(sketch, "E1097", {"start": v(0.36, -1.99) * mm, "end": v(0.38, -1.92) * mm});
            skLineSegment(sketch, "E1098", {"start": v(0.38, -1.92) * mm, "end": v(0.39, -1.87) * mm});
            skLineSegment(sketch, "E1099", {"start": v(0.39, -1.87) * mm, "end": v(0.4, -1.85) * mm});
            skLineSegment(sketch, "E1100", {"start": v(0.4, -1.85) * mm, "end": v(0.4, -1.84) * mm});
            skLineSegment(sketch, "E1101", {"start": v(0.4, -1.84) * mm, "end": v(0.4, -1.84) * mm});
            skLineSegment(sketch, "E1102", {"start": v(0.4, -1.84) * mm, "end": v(0.39, -1.83) * mm});
            skLineSegment(sketch, "E1103", {"start": v(0.39, -1.83) * mm, "end": v(0.37, -1.83) * mm});
            skLineSegment(sketch, "E1104", {"start": v(0.37, -1.83) * mm, "end": v(0.35, -1.83) * mm});
            skLineSegment(sketch, "E1105", {"start": v(0.35, -1.83) * mm, "end": v(0.32, -1.83) * mm});
            skLineSegment(sketch, "E1106", {"start": v(0.32, -1.83) * mm, "end": v(0.28, -1.83) * mm});
            skLineSegment(sketch, "E1107", {"start": v(0.28, -1.83) * mm, "end": v(0.22, -1.83) * mm});
            skLineSegment(sketch, "E1108", {"start": v(0.22, -1.83) * mm, "end": v(0.04, -1.83) * mm});
            skLineSegment(sketch, "E1109", {"start": v(0.04, -1.83) * mm, "end": v(-0.04, -1.89) * mm});
            skLineSegment(sketch, "E1110", {"start": v(-0.04, -1.89) * mm, "end": v(-0.09, -1.92) * mm});
            skLineSegment(sketch, "E1111", {"start": v(-0.09, -1.92) * mm, "end": v(-0.14, -1.94) * mm});
            skLineSegment(sketch, "E1112", {"start": v(-0.14, -1.94) * mm, "end": v(-0.19, -1.96) * mm});
            skLineSegment(sketch, "E1113", {"start": v(-0.19, -1.96) * mm, "end": v(-0.25, -1.99) * mm});
            skLineSegment(sketch, "E1114", {"start": v(-0.25, -1.99) * mm, "end": v(-0.33, -2) * mm});
            skLineSegment(sketch, "E1115", {"start": v(-0.33, -2) * mm, "end": v(-0.38, -2.02) * mm});
            skLineSegment(sketch, "E1116", {"start": v(-0.38, -2.02) * mm, "end": v(-0.45, -2.03) * mm});
            skLineSegment(sketch, "E1117", {"start": v(-0.45, -2.03) * mm, "end": v(-0.56, -2.03) * mm});
            skLineSegment(sketch, "E1118", {"start": v(-0.56, -2.03) * mm, "end": v(-0.63, -2.03) * mm});
            skLineSegment(sketch, "E1119", {"start": v(-0.63, -2.03) * mm, "end": v(-0.68, -2.03) * mm});
            skLineSegment(sketch, "E1120", {"start": v(-0.68, -2.03) * mm, "end": v(-0.72, -2.03) * mm});
            skLineSegment(sketch, "E1121", {"start": v(-0.72, -2.03) * mm, "end": v(-0.74, -2.03) * mm});
            skLineSegment(sketch, "E1122", {"start": v(-0.74, -2.03) * mm, "end": v(-0.73, -2.04) * mm});
            skLineSegment(sketch, "E1123", {"start": v(-0.73, -2.04) * mm, "end": v(-0.72, -2.08) * mm});
            skLineSegment(sketch, "E1124", {"start": v(-0.72, -2.08) * mm, "end": v(-0.7, -2.17) * mm});
            skLineSegment(sketch, "E1125", {"start": v(-0.7, -2.17) * mm, "end": v(-0.66, -2.28) * mm});
            skLineSegment(sketch, "E1126", {"start": v(-0.66, -2.28) * mm, "end": v(-0.61, -2.4) * mm});
            skLineSegment(sketch, "E1127", {"start": v(-0.61, -2.4) * mm, "end": v(-0.56, -2.52) * mm});
            skLineSegment(sketch, "E1128", {"start": v(-0.56, -2.52) * mm, "end": v(-0.51, -2.63) * mm});
            skLineSegment(sketch, "E1129", {"start": v(-0.51, -2.63) * mm, "end": v(-0.46, -2.74) * mm});
            skLineSegment(sketch, "E1130", {"start": v(-0.46, -2.74) * mm, "end": v(-0.42, -2.82) * mm});
            skLineSegment(sketch, "E1131", {"start": v(-0.42, -2.82) * mm, "end": v(-0.39, -2.88) * mm});
            skLineSegment(sketch, "E1132", {"start": v(-0.39, -2.88) * mm, "end": v(-0.36, -2.92) * mm});
            skLineSegment(sketch, "E1133", {"start": v(-0.36, -2.92) * mm, "end": v(-0.33, -2.96) * mm});
            skLineSegment(sketch, "E1134", {"start": v(-0.33, -2.96) * mm, "end": v(-0.32, -2.98) * mm});
            skLineSegment(sketch, "E1135", {"start": v(-0.32, -2.98) * mm, "end": v(-0.3, -3) * mm});
            skLineSegment(sketch, "E1136", {"start": v(-0.3, -3) * mm, "end": v(-0.3, -3.02) * mm});
            skLineSegment(sketch, "E1137", {"start": v(-0.3, -3.02) * mm, "end": v(-0.27, -3.05) * mm});
            skLineSegment(sketch, "E1138", {"start": v(-0.27, -3.05) * mm, "end": v(-0.24, -3.08) * mm});
            skLineSegment(sketch, "E1139", {"start": v(-0.24, -3.08) * mm, "end": v(-0.22, -3.1) * mm});
            skLineSegment(sketch, "E1140", {"start": v(-0.22, -3.1) * mm, "end": v(-0.2, -3.1) * mm});
            skLineSegment(sketch, "E1141", {"start": v(-0.2, -3.1) * mm, "end": v(-0.17, -3.1) * mm});
            skLineSegment(sketch, "E1142", {"start": v(-0.17, -3.1) * mm, "end": v(-0.13, -3.1) * mm});
            skLineSegment(sketch, "E1143", {"start": v(-0.13, -3.1) * mm, "end": v(-0.08, -3.08) * mm});
            skLineSegment(sketch, "E1144", {"start": v(3.94, -2.73) * mm, "end": v(3.95, -2.72) * mm});
            skLineSegment(sketch, "E1145", {"start": v(3.95, -2.72) * mm, "end": v(3.95, -2.7) * mm});
            skLineSegment(sketch, "E1146", {"start": v(3.95, -2.7) * mm, "end": v(3.94, -2.68) * mm});
            skLineSegment(sketch, "E1147", {"start": v(3.94, -2.68) * mm, "end": v(3.92, -2.62) * mm});
            skLineSegment(sketch, "E1148", {"start": v(3.92, -2.62) * mm, "end": v(3.88, -2.51) * mm});
            skLineSegment(sketch, "E1149", {"start": v(3.88, -2.51) * mm, "end": v(3.82, -2.4) * mm});
            skLineSegment(sketch, "E1150", {"start": v(3.82, -2.4) * mm, "end": v(3.77, -2.29) * mm});
            skLineSegment(sketch, "E1151", {"start": v(3.77, -2.29) * mm, "end": v(3.72, -2.21) * mm});
            skLineSegment(sketch, "E1152", {"start": v(3.72, -2.21) * mm, "end": v(3.7, -2.19) * mm});
            skLineSegment(sketch, "E1153", {"start": v(3.7, -2.19) * mm, "end": v(3.67, -2.15) * mm});
            skLineSegment(sketch, "E1154", {"start": v(3.67, -2.15) * mm, "end": v(3.65, -2.11) * mm});
            skLineSegment(sketch, "E1155", {"start": v(3.65, -2.11) * mm, "end": v(3.62, -2.08) * mm});
            skLineSegment(sketch, "E1156", {"start": v(3.62, -2.08) * mm, "end": v(3.55, -1.99) * mm});
            skLineSegment(sketch, "E1157", {"start": v(3.55, -1.99) * mm, "end": v(3.47, -1.9) * mm});
            skLineSegment(sketch, "E1158", {"start": v(3.47, -1.9) * mm, "end": v(3.36, -1.79) * mm});
            skLineSegment(sketch, "E1159", {"start": v(3.36, -1.79) * mm, "end": v(3.2, -1.66) * mm});
            skLineSegment(sketch, "E1160", {"start": v(3.2, -1.66) * mm, "end": v(2.94, -1.44) * mm});
            skLineSegment(sketch, "E1161", {"start": v(2.94, -1.44) * mm, "end": v(2.65, -1.25) * mm});
            skLineSegment(sketch, "E1162", {"start": v(2.65, -1.25) * mm, "end": v(2.34, -1.07) * mm});
            skLineSegment(sketch, "E1163", {"start": v(2.34, -1.07) * mm, "end": v(2.03, -0.93) * mm});
            skLineSegment(sketch, "E1164", {"start": v(2.03, -0.93) * mm, "end": v(1.84, -0.86) * mm});
            skLineSegment(sketch, "E1165", {"start": v(1.84, -0.86) * mm, "end": v(1.6, -0.8) * mm});
            skLineSegment(sketch, "E1166", {"start": v(1.6, -0.8) * mm, "end": v(1.32, -0.75) * mm});
            skLineSegment(sketch, "E1167", {"start": v(1.32, -0.75) * mm, "end": v(1.03, -0.7) * mm});
            skLineSegment(sketch, "E1168", {"start": v(1.03, -0.7) * mm, "end": v(0.91, -0.7) * mm});
            skLineSegment(sketch, "E1169", {"start": v(0.91, -0.7) * mm, "end": v(0.83, -0.69) * mm});
            skLineSegment(sketch, "E1170", {"start": v(0.83, -0.69) * mm, "end": v(0.77, -0.68) * mm});
            skLineSegment(sketch, "E1171", {"start": v(0.77, -0.68) * mm, "end": v(0.73, -0.68) * mm});
            skLineSegment(sketch, "E1172", {"start": v(0.73, -0.68) * mm, "end": v(0.7, -0.68) * mm});
            skLineSegment(sketch, "E1173", {"start": v(0.7, -0.68) * mm, "end": v(0.7, -0.68) * mm});
            skLineSegment(sketch, "E1174", {"start": v(0.7, -0.68) * mm, "end": v(0.69, -0.68) * mm});
            skLineSegment(sketch, "E1175", {"start": v(0.69, -0.68) * mm, "end": v(0.69, -0.69) * mm});
            skLineSegment(sketch, "E1176", {"start": v(0.69, -0.69) * mm, "end": v(0.68, -0.71) * mm});
            skLineSegment(sketch, "E1177", {"start": v(0.68, -0.71) * mm, "end": v(0.68, -0.76) * mm});
            skLineSegment(sketch, "E1178", {"start": v(0.68, -0.76) * mm, "end": v(0.67, -0.83) * mm});
            skLineSegment(sketch, "E1179", {"start": v(0.67, -0.83) * mm, "end": v(0.67, -0.91) * mm});
            skLineSegment(sketch, "E1180", {"start": v(0.67, -0.91) * mm, "end": v(0.67, -1.12) * mm});
            skLineSegment(sketch, "E1181", {"start": v(0.67, -1.12) * mm, "end": v(0.72, -1.18) * mm});
            skLineSegment(sketch, "E1182", {"start": v(0.72, -1.18) * mm, "end": v(0.73, -1.2) * mm});
            skLineSegment(sketch, "E1183", {"start": v(0.73, -1.2) * mm, "end": v(0.75, -1.23) * mm});
            skLineSegment(sketch, "E1184", {"start": v(0.75, -1.23) * mm, "end": v(0.77, -1.24) * mm});
            skLineSegment(sketch, "E1185", {"start": v(0.77, -1.24) * mm, "end": v(0.77, -1.25) * mm});
            skLineSegment(sketch, "E1186", {"start": v(0.77, -1.25) * mm, "end": v(0.78, -1.26) * mm});
            skLineSegment(sketch, "E1187", {"start": v(0.78, -1.26) * mm, "end": v(0.8, -1.28) * mm});
            skLineSegment(sketch, "E1188", {"start": v(0.8, -1.28) * mm, "end": v(0.82, -1.3) * mm});
            skLineSegment(sketch, "E1189", {"start": v(0.82, -1.3) * mm, "end": v(0.84, -1.34) * mm});
            skLineSegment(sketch, "E1190", {"start": v(0.84, -1.34) * mm, "end": v(0.86, -1.37) * mm});
            skLineSegment(sketch, "E1191", {"start": v(0.86, -1.37) * mm, "end": v(0.89, -1.4) * mm});
            skLineSegment(sketch, "E1192", {"start": v(0.89, -1.4) * mm, "end": v(0.92, -1.43) * mm});
            skLineSegment(sketch, "E1193", {"start": v(0.92, -1.43) * mm, "end": v(0.96, -1.47) * mm});
            skLineSegment(sketch, "E1194", {"start": v(0.96, -1.47) * mm, "end": v(1.02, -1.52) * mm});
            skLineSegment(sketch, "E1195", {"start": v(1.02, -1.52) * mm, "end": v(1.1, -1.58) * mm});
            skLineSegment(sketch, "E1196", {"start": v(1.1, -1.58) * mm, "end": v(1.2, -1.66) * mm});
            skLineSegment(sketch, "E1197", {"start": v(1.2, -1.66) * mm, "end": v(1.31, -1.76) * mm});
            skLineSegment(sketch, "E1198", {"start": v(1.31, -1.76) * mm, "end": v(1.46, -1.86) * mm});
            skLineSegment(sketch, "E1199", {"start": v(1.46, -1.86) * mm, "end": v(1.65, -1.98) * mm});
            skLineSegment(sketch, "E1200", {"start": v(1.65, -1.98) * mm, "end": v(1.86, -2.1) * mm});
            skLineSegment(sketch, "E1201", {"start": v(1.86, -2.1) * mm, "end": v(2.1, -2.23) * mm});
            skLineSegment(sketch, "E1202", {"start": v(2.1, -2.23) * mm, "end": v(2.31, -2.33) * mm});
            skLineSegment(sketch, "E1203", {"start": v(2.31, -2.33) * mm, "end": v(2.5, -2.4) * mm});
            skLineSegment(sketch, "E1204", {"start": v(2.5, -2.4) * mm, "end": v(2.65, -2.47) * mm});
            skLineSegment(sketch, "E1205", {"start": v(2.65, -2.47) * mm, "end": v(2.77, -2.5) * mm});
            skLineSegment(sketch, "E1206", {"start": v(2.77, -2.5) * mm, "end": v(2.83, -2.53) * mm});
            skLineSegment(sketch, "E1207", {"start": v(2.83, -2.53) * mm, "end": v(2.9, -2.55) * mm});
            skLineSegment(sketch, "E1208", {"start": v(2.9, -2.55) * mm, "end": v(2.99, -2.57) * mm});
            skLineSegment(sketch, "E1209", {"start": v(2.99, -2.57) * mm, "end": v(3.06, -2.59) * mm});
            skLineSegment(sketch, "E1210", {"start": v(3.06, -2.59) * mm, "end": v(3.21, -2.63) * mm});
            skLineSegment(sketch, "E1211", {"start": v(3.21, -2.63) * mm, "end": v(3.35, -2.66) * mm});
            skLineSegment(sketch, "E1212", {"start": v(3.35, -2.66) * mm, "end": v(3.5, -2.68) * mm});
            skLineSegment(sketch, "E1213", {"start": v(3.5, -2.68) * mm, "end": v(3.68, -2.71) * mm});
            skLineSegment(sketch, "E1214", {"start": v(3.68, -2.71) * mm, "end": v(3.77, -2.72) * mm});
            skLineSegment(sketch, "E1215", {"start": v(3.77, -2.72) * mm, "end": v(3.83, -2.73) * mm});
            skLineSegment(sketch, "E1216", {"start": v(3.83, -2.73) * mm, "end": v(3.87, -2.74) * mm});
            skLineSegment(sketch, "E1217", {"start": v(3.87, -2.74) * mm, "end": v(3.9, -2.74) * mm});
            skLineSegment(sketch, "E1218", {"start": v(3.9, -2.74) * mm, "end": v(3.92, -2.74) * mm});
            skLineSegment(sketch, "E1219", {"start": v(3.92, -2.74) * mm, "end": v(3.93, -2.74) * mm});
            skLineSegment(sketch, "E1220", {"start": v(3.93, -2.74) * mm, "end": v(3.93, -2.74) * mm});
            skLineSegment(sketch, "E1221", {"start": v(3.93, -2.74) * mm, "end": v(3.94, -2.73) * mm});
            skLineSegment(sketch, "E1222", {"start": v(4.57, -2.72) * mm, "end": v(4.81, -2.68) * mm});
            skLineSegment(sketch, "E1223", {"start": v(4.81, -2.68) * mm, "end": v(5.02, -2.65) * mm});
            skLineSegment(sketch, "E1224", {"start": v(5.02, -2.65) * mm, "end": v(5.22, -2.6) * mm});
            skLineSegment(sketch, "E1225", {"start": v(5.22, -2.6) * mm, "end": v(5.41, -2.55) * mm});
            skLineSegment(sketch, "E1226", {"start": v(5.41, -2.55) * mm, "end": v(5.53, -2.52) * mm});
            skLineSegment(sketch, "E1227", {"start": v(5.53, -2.52) * mm, "end": v(5.62, -2.5) * mm});
            skLineSegment(sketch, "E1228", {"start": v(5.62, -2.5) * mm, "end": v(5.7, -2.47) * mm});
            skLineSegment(sketch, "E1229", {"start": v(5.7, -2.47) * mm, "end": v(5.76, -2.46) * mm});
            skLineSegment(sketch, "E1230", {"start": v(5.76, -2.46) * mm, "end": v(5.81, -2.44) * mm});
            skLineSegment(sketch, "E1231", {"start": v(5.81, -2.44) * mm, "end": v(5.86, -2.42) * mm});
            skLineSegment(sketch, "E1232", {"start": v(5.86, -2.42) * mm, "end": v(5.9, -2.4) * mm});
            skLineSegment(sketch, "E1233", {"start": v(5.9, -2.4) * mm, "end": v(5.96, -2.39) * mm});
            skLineSegment(sketch, "E1234", {"start": v(5.96, -2.39) * mm, "end": v(6.11, -2.33) * mm});
            skLineSegment(sketch, "E1235", {"start": v(6.11, -2.33) * mm, "end": v(6.25, -2.28) * mm});
            skLineSegment(sketch, "E1236", {"start": v(6.25, -2.28) * mm, "end": v(6.35, -2.24) * mm});
            skLineSegment(sketch, "E1237", {"start": v(6.35, -2.24) * mm, "end": v(6.39, -2.23) * mm});
            skLineSegment(sketch, "E1238", {"start": v(6.39, -2.23) * mm, "end": v(6.39, -2.22) * mm});
            skLineSegment(sketch, "E1239", {"start": v(6.39, -2.22) * mm, "end": v(6.37, -2.2) * mm});
            skLineSegment(sketch, "E1240", {"start": v(6.37, -2.2) * mm, "end": v(6.35, -2.17) * mm});
            skLineSegment(sketch, "E1241", {"start": v(6.35, -2.17) * mm, "end": v(6.32, -2.14) * mm});
            skLineSegment(sketch, "E1242", {"start": v(6.32, -2.14) * mm, "end": v(6.29, -2.1) * mm});
            skLineSegment(sketch, "E1243", {"start": v(6.29, -2.1) * mm, "end": v(6.26, -2.07) * mm});
            skLineSegment(sketch, "E1244", {"start": v(6.26, -2.07) * mm, "end": v(6.23, -2.04) * mm});
            skLineSegment(sketch, "E1245", {"start": v(6.23, -2.04) * mm, "end": v(6.21, -2.01) * mm});
            skLineSegment(sketch, "E1246", {"start": v(6.21, -2.01) * mm, "end": v(6.14, -1.93) * mm});
            skLineSegment(sketch, "E1247", {"start": v(6.14, -1.93) * mm, "end": v(6.02, -1.83) * mm});
            skLineSegment(sketch, "E1248", {"start": v(6.02, -1.83) * mm, "end": v(5.87, -1.7) * mm});
            skLineSegment(sketch, "E1249", {"start": v(5.87, -1.7) * mm, "end": v(5.7, -1.59) * mm});
            skLineSegment(sketch, "E1250", {"start": v(5.7, -1.59) * mm, "end": v(5.67, -1.57) * mm});
            skLineSegment(sketch, "E1251", {"start": v(5.67, -1.57) * mm, "end": v(5.64, -1.54) * mm});
            skLineSegment(sketch, "E1252", {"start": v(5.64, -1.54) * mm, "end": v(5.6, -1.51) * mm});
            skLineSegment(sketch, "E1253", {"start": v(5.6, -1.51) * mm, "end": v(5.57, -1.5) * mm});
            skLineSegment(sketch, "E1254", {"start": v(5.57, -1.5) * mm, "end": v(5.5, -1.45) * mm});
            skLineSegment(sketch, "E1255", {"start": v(5.5, -1.45) * mm, "end": v(5.42, -1.42) * mm});
            skLineSegment(sketch, "E1256", {"start": v(5.42, -1.42) * mm, "end": v(5.33, -1.4) * mm});
            skLineSegment(sketch, "E1257", {"start": v(5.33, -1.4) * mm, "end": v(5.24, -1.38) * mm});
            skLineSegment(sketch, "E1258", {"start": v(5.24, -1.38) * mm, "end": v(5.18, -1.38) * mm});
            skLineSegment(sketch, "E1259", {"start": v(5.18, -1.38) * mm, "end": v(5.12, -1.38) * mm});
            skLineSegment(sketch, "E1260", {"start": v(5.12, -1.38) * mm, "end": v(5.04, -1.4) * mm});
            skLineSegment(sketch, "E1261", {"start": v(5.04, -1.4) * mm, "end": v(4.94, -1.4) * mm});
            skLineSegment(sketch, "E1262", {"start": v(4.94, -1.4) * mm, "end": v(4.83, -1.42) * mm});
            skLineSegment(sketch, "E1263", {"start": v(4.83, -1.42) * mm, "end": v(4.73, -1.43) * mm});
            skLineSegment(sketch, "E1264", {"start": v(4.73, -1.43) * mm, "end": v(4.63, -1.44) * mm});
            skLineSegment(sketch, "E1265", {"start": v(4.63, -1.44) * mm, "end": v(4.5, -1.44) * mm});
            skLineSegment(sketch, "E1266", {"start": v(4.5, -1.44) * mm, "end": v(4.42, -1.44) * mm});
            skLineSegment(sketch, "E1267", {"start": v(4.42, -1.44) * mm, "end": v(4.34, -1.44) * mm});
            skLineSegment(sketch, "E1268", {"start": v(4.34, -1.44) * mm, "end": v(4.28, -1.43) * mm});
            skLineSegment(sketch, "E1269", {"start": v(4.28, -1.43) * mm, "end": v(4.23, -1.42) * mm});
            skLineSegment(sketch, "E1270", {"start": v(4.23, -1.42) * mm, "end": v(4.17, -1.4) * mm});
            skLineSegment(sketch, "E1271", {"start": v(4.17, -1.4) * mm, "end": v(4.12, -1.4) * mm});
            skLineSegment(sketch, "E1272", {"start": v(4.12, -1.4) * mm, "end": v(4.06, -1.37) * mm});
            skLineSegment(sketch, "E1273", {"start": v(4.06, -1.37) * mm, "end": v(3.98, -1.34) * mm});
            skLineSegment(sketch, "E1274", {"start": v(3.98, -1.34) * mm, "end": v(3.92, -1.3) * mm});
            skLineSegment(sketch, "E1275", {"start": v(3.92, -1.3) * mm, "end": v(3.84, -1.28) * mm});
            skLineSegment(sketch, "E1276", {"start": v(3.84, -1.28) * mm, "end": v(3.75, -1.24) * mm});
            skLineSegment(sketch, "E1277", {"start": v(3.75, -1.24) * mm, "end": v(3.67, -1.22) * mm});
            skLineSegment(sketch, "E1278", {"start": v(3.67, -1.22) * mm, "end": v(3.58, -1.18) * mm});
            skLineSegment(sketch, "E1279", {"start": v(3.58, -1.18) * mm, "end": v(3.5, -1.16) * mm});
            skLineSegment(sketch, "E1280", {"start": v(3.5, -1.16) * mm, "end": v(3.43, -1.15) * mm});
            skLineSegment(sketch, "E1281", {"start": v(3.43, -1.15) * mm, "end": v(3.33, -1.14) * mm});
            skLineSegment(sketch, "E1282", {"start": v(3.33, -1.14) * mm, "end": v(3.2, -1.13) * mm});
            skLineSegment(sketch, "E1283", {"start": v(3.2, -1.13) * mm, "end": v(3.09, -1.12) * mm});
            skLineSegment(sketch, "E1284", {"start": v(3.09, -1.12) * mm, "end": v(3, -1.13) * mm});
            skLineSegment(sketch, "E1285", {"start": v(3, -1.13) * mm, "end": v(2.98, -1.14) * mm});
            skLineSegment(sketch, "E1286", {"start": v(2.98, -1.14) * mm, "end": v(2.99, -1.15) * mm});
            skLineSegment(sketch, "E1287", {"start": v(2.99, -1.15) * mm, "end": v(3.02, -1.18) * mm});
            skLineSegment(sketch, "E1288", {"start": v(3.02, -1.18) * mm, "end": v(3.06, -1.21) * mm});
            skLineSegment(sketch, "E1289", {"start": v(3.06, -1.21) * mm, "end": v(3.11, -1.25) * mm});
            skLineSegment(sketch, "E1290", {"start": v(3.11, -1.25) * mm, "end": v(3.24, -1.36) * mm});
            skLineSegment(sketch, "E1291", {"start": v(3.24, -1.36) * mm, "end": v(3.38, -1.48) * mm});
            skLineSegment(sketch, "E1292", {"start": v(3.38, -1.48) * mm, "end": v(3.52, -1.6) * mm});
            skLineSegment(sketch, "E1293", {"start": v(3.52, -1.6) * mm, "end": v(3.66, -1.74) * mm});
            skLineSegment(sketch, "E1294", {"start": v(3.66, -1.74) * mm, "end": v(3.73, -1.81) * mm});
            skLineSegment(sketch, "E1295", {"start": v(3.73, -1.81) * mm, "end": v(3.78, -1.88) * mm});
            skLineSegment(sketch, "E1296", {"start": v(3.78, -1.88) * mm, "end": v(3.84, -1.95) * mm});
            skLineSegment(sketch, "E1297", {"start": v(3.84, -1.95) * mm, "end": v(3.9, -2.04) * mm});
            skLineSegment(sketch, "E1298", {"start": v(3.9, -2.04) * mm, "end": v(4.03, -2.24) * mm});
            skLineSegment(sketch, "E1299", {"start": v(4.03, -2.24) * mm, "end": v(4.12, -2.4) * mm});
            skLineSegment(sketch, "E1300", {"start": v(4.12, -2.4) * mm, "end": v(4.18, -2.53) * mm});
            skLineSegment(sketch, "E1301", {"start": v(4.18, -2.53) * mm, "end": v(4.21, -2.64) * mm});
            skLineSegment(sketch, "E1302", {"start": v(4.21, -2.64) * mm, "end": v(4.22, -2.67) * mm});
            skLineSegment(sketch, "E1303", {"start": v(4.22, -2.67) * mm, "end": v(4.23, -2.7) * mm});
            skLineSegment(sketch, "E1304", {"start": v(4.23, -2.7) * mm, "end": v(4.23, -2.71) * mm});
            skLineSegment(sketch, "E1305", {"start": v(4.23, -2.71) * mm, "end": v(4.24, -2.72) * mm});
            skLineSegment(sketch, "E1306", {"start": v(4.24, -2.72) * mm, "end": v(4.27, -2.73) * mm});
            skLineSegment(sketch, "E1307", {"start": v(4.27, -2.73) * mm, "end": v(4.35, -2.73) * mm});
            skLineSegment(sketch, "E1308", {"start": v(4.35, -2.73) * mm, "end": v(4.46, -2.73) * mm});
            skLineSegment(sketch, "E1309", {"start": v(4.46, -2.73) * mm, "end": v(4.57, -2.72) * mm});
            skLineSegment(sketch, "E1310", {"start": v(-5, -2.2) * mm, "end": v(-4.97, -2.18) * mm});
            skLineSegment(sketch, "E1311", {"start": v(-4.97, -2.18) * mm, "end": v(-4.92, -2.14) * mm});
            skLineSegment(sketch, "E1312", {"start": v(-4.92, -2.14) * mm, "end": v(-4.87, -2.08) * mm});
            skLineSegment(sketch, "E1313", {"start": v(-4.87, -2.08) * mm, "end": v(-4.8, -2.01) * mm});
            skLineSegment(sketch, "E1314", {"start": v(-4.8, -2.01) * mm, "end": v(-4.74, -1.93) * mm});
            skLineSegment(sketch, "E1315", {"start": v(-4.74, -1.93) * mm, "end": v(-4.67, -1.85) * mm});
            skLineSegment(sketch, "E1316", {"start": v(-4.67, -1.85) * mm, "end": v(-4.6, -1.76) * mm});
            skLineSegment(sketch, "E1317", {"start": v(-4.6, -1.76) * mm, "end": v(-4.53, -1.7) * mm});
            skLineSegment(sketch, "E1318", {"start": v(-4.53, -1.7) * mm, "end": v(-4.46, -1.63) * mm});
            skLineSegment(sketch, "E1319", {"start": v(-4.46, -1.63) * mm, "end": v(-4.4, -1.56) * mm});
            skLineSegment(sketch, "E1320", {"start": v(-4.4, -1.56) * mm, "end": v(-4.34, -1.5) * mm});
            skLineSegment(sketch, "E1321", {"start": v(-4.34, -1.5) * mm, "end": v(-4.29, -1.44) * mm});
            skLineSegment(sketch, "E1322", {"start": v(-4.29, -1.44) * mm, "end": v(-4.24, -1.4) * mm});
            skLineSegment(sketch, "E1323", {"start": v(-4.24, -1.4) * mm, "end": v(-4.18, -1.34) * mm});
            skLineSegment(sketch, "E1324", {"start": v(-4.18, -1.34) * mm, "end": v(-4.12, -1.28) * mm});
            skLineSegment(sketch, "E1325", {"start": v(-4.12, -1.28) * mm, "end": v(-4.06, -1.23) * mm});
            skLineSegment(sketch, "E1326", {"start": v(-4.06, -1.23) * mm, "end": v(-4, -1.19) * mm});
            skLineSegment(sketch, "E1327", {"start": v(-4, -1.19) * mm, "end": v(-3.95, -1.14) * mm});
            skLineSegment(sketch, "E1328", {"start": v(-3.95, -1.14) * mm, "end": v(-3.9, -1.1) * mm});
            skLineSegment(sketch, "E1329", {"start": v(-3.9, -1.1) * mm, "end": v(-3.85, -1.06) * mm});
            skLineSegment(sketch, "E1330", {"start": v(-3.85, -1.06) * mm, "end": v(-3.82, -1.02) * mm});
            skLineSegment(sketch, "E1331", {"start": v(-3.82, -1.02) * mm, "end": v(-3.78, -1) * mm});
            skLineSegment(sketch, "E1332", {"start": v(-3.78, -1) * mm, "end": v(-3.75, -0.96) * mm});
            skLineSegment(sketch, "E1333", {"start": v(-3.75, -0.96) * mm, "end": v(-3.72, -0.94) * mm});
            skLineSegment(sketch, "E1334", {"start": v(-3.72, -0.94) * mm, "end": v(-3.7, -0.92) * mm});
            skLineSegment(sketch, "E1335", {"start": v(-3.7, -0.92) * mm, "end": v(-3.69, -0.9) * mm});
            skLineSegment(sketch, "E1336", {"start": v(-3.69, -0.9) * mm, "end": v(-3.67, -0.9) * mm});
            skLineSegment(sketch, "E1337", {"start": v(-3.67, -0.9) * mm, "end": v(-3.67, -0.89) * mm});
            skLineSegment(sketch, "E1338", {"start": v(-3.67, -0.89) * mm, "end": v(-3.68, -0.88) * mm});
            skLineSegment(sketch, "E1339", {"start": v(-3.68, -0.88) * mm, "end": v(-3.72, -0.88) * mm});
            skLineSegment(sketch, "E1340", {"start": v(-3.72, -0.88) * mm, "end": v(-3.77, -0.88) * mm});
            skLineSegment(sketch, "E1341", {"start": v(-3.77, -0.88) * mm, "end": v(-3.83, -0.88) * mm});
            skLineSegment(sketch, "E1342", {"start": v(-3.83, -0.88) * mm, "end": v(-3.92, -0.88) * mm});
            skLineSegment(sketch, "E1343", {"start": v(-3.92, -0.88) * mm, "end": v(-4.02, -0.87) * mm});
            skLineSegment(sketch, "E1344", {"start": v(-4.02, -0.87) * mm, "end": v(-4.12, -0.87) * mm});
            skLineSegment(sketch, "E1345", {"start": v(-4.12, -0.87) * mm, "end": v(-4.23, -0.86) * mm});
            skLineSegment(sketch, "E1346", {"start": v(-4.23, -0.86) * mm, "end": v(-4.34, -0.85) * mm});
            skLineSegment(sketch, "E1347", {"start": v(-4.34, -0.85) * mm, "end": v(-4.48, -0.85) * mm});
            skLineSegment(sketch, "E1348", {"start": v(-4.48, -0.85) * mm, "end": v(-4.64, -0.84) * mm});
            skLineSegment(sketch, "E1349", {"start": v(-4.64, -0.84) * mm, "end": v(-4.78, -0.84) * mm});
            skLineSegment(sketch, "E1350", {"start": v(-4.78, -0.84) * mm, "end": v(-4.88, -0.84) * mm});
            skLineSegment(sketch, "E1351", {"start": v(-4.88, -0.84) * mm, "end": v(-4.96, -0.84) * mm});
            skLineSegment(sketch, "E1352", {"start": v(-4.96, -0.84) * mm, "end": v(-5.03, -0.84) * mm});
            skLineSegment(sketch, "E1353", {"start": v(-5.03, -0.84) * mm, "end": v(-5.08, -0.84) * mm});
            skLineSegment(sketch, "E1354", {"start": v(-5.08, -0.84) * mm, "end": v(-5.12, -0.85) * mm});
            skLineSegment(sketch, "E1355", {"start": v(-5.12, -0.85) * mm, "end": v(-5.15, -0.85) * mm});
            skLineSegment(sketch, "E1356", {"start": v(-5.15, -0.85) * mm, "end": v(-5.18, -0.86) * mm});
            skLineSegment(sketch, "E1357", {"start": v(-5.18, -0.86) * mm, "end": v(-5.22, -0.87) * mm});
            skLineSegment(sketch, "E1358", {"start": v(-5.22, -0.87) * mm, "end": v(-5.36, -0.9) * mm});
            skLineSegment(sketch, "E1359", {"start": v(-5.36, -0.9) * mm, "end": v(-5.47, -0.94) * mm});
            skLineSegment(sketch, "E1360", {"start": v(-5.47, -0.94) * mm, "end": v(-5.57, -1) * mm});
            skLineSegment(sketch, "E1361", {"start": v(-5.57, -1) * mm, "end": v(-5.68, -1.07) * mm});
            skLineSegment(sketch, "E1362", {"start": v(-5.68, -1.07) * mm, "end": v(-5.76, -1.13) * mm});
            skLineSegment(sketch, "E1363", {"start": v(-5.76, -1.13) * mm, "end": v(-5.84, -1.16) * mm});
            skLineSegment(sketch, "E1364", {"start": v(-5.84, -1.16) * mm, "end": v(-5.94, -1.2) * mm});
            skLineSegment(sketch, "E1365", {"start": v(-5.94, -1.2) * mm, "end": v(-6.1, -1.23) * mm});
            skLineSegment(sketch, "E1366", {"start": v(-6.1, -1.23) * mm, "end": v(-6.3, -1.28) * mm});
            skLineSegment(sketch, "E1367", {"start": v(-6.3, -1.28) * mm, "end": v(-6.48, -1.35) * mm});
            skLineSegment(sketch, "E1368", {"start": v(-6.48, -1.35) * mm, "end": v(-6.65, -1.44) * mm});
            skLineSegment(sketch, "E1369", {"start": v(-6.65, -1.44) * mm, "end": v(-6.82, -1.55) * mm});
            skLineSegment(sketch, "E1370", {"start": v(-6.82, -1.55) * mm, "end": v(-6.88, -1.6) * mm});
            skLineSegment(sketch, "E1371", {"start": v(-6.88, -1.6) * mm, "end": v(-6.94, -1.65) * mm});
            skLineSegment(sketch, "E1372", {"start": v(-6.94, -1.65) * mm, "end": v(-7, -1.69) * mm});
            skLineSegment(sketch, "E1373", {"start": v(-7, -1.69) * mm, "end": v(-7.04, -1.72) * mm});
            skLineSegment(sketch, "E1374", {"start": v(-7.04, -1.72) * mm, "end": v(-7.07, -1.75) * mm});
            skLineSegment(sketch, "E1375", {"start": v(-7.07, -1.75) * mm, "end": v(-7.1, -1.77) * mm});
            skLineSegment(sketch, "E1376", {"start": v(-7.1, -1.77) * mm, "end": v(-7.12, -1.78) * mm});
            skLineSegment(sketch, "E1377", {"start": v(-7.12, -1.78) * mm, "end": v(-7.12, -1.8) * mm});
            skLineSegment(sketch, "E1378", {"start": v(-7.12, -1.8) * mm, "end": v(-7.11, -1.8) * mm});
            skLineSegment(sketch, "E1379", {"start": v(-7.11, -1.8) * mm, "end": v(-7.08, -1.8) * mm});
            skLineSegment(sketch, "E1380", {"start": v(-7.08, -1.8) * mm, "end": v(-7.03, -1.82) * mm});
            skLineSegment(sketch, "E1381", {"start": v(-7.03, -1.82) * mm, "end": v(-6.97, -1.84) * mm});
            skLineSegment(sketch, "E1382", {"start": v(-6.97, -1.84) * mm, "end": v(-6.85, -1.88) * mm});
            skLineSegment(sketch, "E1383", {"start": v(-6.85, -1.88) * mm, "end": v(-6.74, -1.91) * mm});
            skLineSegment(sketch, "E1384", {"start": v(-6.74, -1.91) * mm, "end": v(-6.7, -1.93) * mm});
            skLineSegment(sketch, "E1385", {"start": v(-6.7, -1.93) * mm, "end": v(-6.64, -1.94) * mm});
            skLineSegment(sketch, "E1386", {"start": v(-6.64, -1.94) * mm, "end": v(-6.58, -1.96) * mm});
            skLineSegment(sketch, "E1387", {"start": v(-6.58, -1.96) * mm, "end": v(-6.52, -1.98) * mm});
            skLineSegment(sketch, "E1388", {"start": v(-6.52, -1.98) * mm, "end": v(-6.38, -2.01) * mm});
            skLineSegment(sketch, "E1389", {"start": v(-6.38, -2.01) * mm, "end": v(-6.24, -2.05) * mm});
            skLineSegment(sketch, "E1390", {"start": v(-6.24, -2.05) * mm, "end": v(-6.1, -2.1) * mm});
            skLineSegment(sketch, "E1391", {"start": v(-6.1, -2.1) * mm, "end": v(-5.97, -2.12) * mm});
            skLineSegment(sketch, "E1392", {"start": v(-5.97, -2.12) * mm, "end": v(-5.85, -2.14) * mm});
            skLineSegment(sketch, "E1393", {"start": v(-5.85, -2.14) * mm, "end": v(-5.73, -2.16) * mm});
            skLineSegment(sketch, "E1394", {"start": v(-5.73, -2.16) * mm, "end": v(-5.58, -2.18) * mm});
            skLineSegment(sketch, "E1395", {"start": v(-5.58, -2.18) * mm, "end": v(-5.44, -2.2) * mm});
            skLineSegment(sketch, "E1396", {"start": v(-5.44, -2.2) * mm, "end": v(-5.3, -2.21) * mm});
            skLineSegment(sketch, "E1397", {"start": v(-5.3, -2.21) * mm, "end": v(-5.19, -2.22) * mm});
            skLineSegment(sketch, "E1398", {"start": v(-5.19, -2.22) * mm, "end": v(-5.14, -2.22) * mm});
            skLineSegment(sketch, "E1399", {"start": v(-5.14, -2.22) * mm, "end": v(-5.1, -2.23) * mm});
            skLineSegment(sketch, "E1400", {"start": v(-5.1, -2.23) * mm, "end": v(-5.07, -2.23) * mm});
            skLineSegment(sketch, "E1401", {"start": v(-5.07, -2.23) * mm, "end": v(-5.05, -2.23) * mm});
            skLineSegment(sketch, "E1402", {"start": v(-5.05, -2.23) * mm, "end": v(-5.03, -2.22) * mm});
            skLineSegment(sketch, "E1403", {"start": v(-5.03, -2.22) * mm, "end": v(-5, -2.2) * mm});
            skLineSegment(sketch, "E1404", {"start": v(-4.33, -2.2) * mm, "end": v(-3.96, -2.15) * mm});
            skLineSegment(sketch, "E1405", {"start": v(-3.96, -2.15) * mm, "end": v(-3.62, -2.09) * mm});
            skLineSegment(sketch, "E1406", {"start": v(-3.62, -2.09) * mm, "end": v(-3.32, -2) * mm});
            skLineSegment(sketch, "E1407", {"start": v(-3.32, -2) * mm, "end": v(-3.03, -1.91) * mm});
            skLineSegment(sketch, "E1408", {"start": v(-3.03, -1.91) * mm, "end": v(-2.97, -1.89) * mm});
            skLineSegment(sketch, "E1409", {"start": v(-2.97, -1.89) * mm, "end": v(-2.9, -1.86) * mm});
            skLineSegment(sketch, "E1410", {"start": v(-2.9, -1.86) * mm, "end": v(-2.82, -1.84) * mm});
            skLineSegment(sketch, "E1411", {"start": v(-2.82, -1.84) * mm, "end": v(-2.75, -1.81) * mm});
            skLineSegment(sketch, "E1412", {"start": v(-2.75, -1.81) * mm, "end": v(-2.4, -1.69) * mm});
            skLineSegment(sketch, "E1413", {"start": v(-2.4, -1.69) * mm, "end": v(-2.1, -1.58) * mm});
            skLineSegment(sketch, "E1414", {"start": v(-2.1, -1.58) * mm, "end": v(-1.88, -1.48) * mm});
            skLineSegment(sketch, "E1415", {"start": v(-1.88, -1.48) * mm, "end": v(-1.72, -1.4) * mm});
            skLineSegment(sketch, "E1416", {"start": v(-1.72, -1.4) * mm, "end": v(-1.68, -1.37) * mm});
            skLineSegment(sketch, "E1417", {"start": v(-1.68, -1.37) * mm, "end": v(-1.63, -1.34) * mm});
            skLineSegment(sketch, "E1418", {"start": v(-1.63, -1.34) * mm, "end": v(-1.57, -1.3) * mm});
            skLineSegment(sketch, "E1419", {"start": v(-1.57, -1.3) * mm, "end": v(-1.52, -1.27) * mm});
            skLineSegment(sketch, "E1420", {"start": v(-1.52, -1.27) * mm, "end": v(-1.47, -1.24) * mm});
            skLineSegment(sketch, "E1421", {"start": v(-1.47, -1.24) * mm, "end": v(-1.4, -1.2) * mm});
            skLineSegment(sketch, "E1422", {"start": v(-1.4, -1.2) * mm, "end": v(-1.35, -1.17) * mm});
            skLineSegment(sketch, "E1423", {"start": v(-1.35, -1.17) * mm, "end": v(-1.3, -1.14) * mm});
            skLineSegment(sketch, "E1424", {"start": v(-1.3, -1.14) * mm, "end": v(-1.2, -1.08) * mm});
            skLineSegment(sketch, "E1425", {"start": v(-1.2, -1.08) * mm, "end": v(-1.2, -0.75) * mm});
            skLineSegment(sketch, "E1426", {"start": v(-1.2, -0.75) * mm, "end": v(-1.2, -0.62) * mm});
            skLineSegment(sketch, "E1427", {"start": v(-1.2, -0.62) * mm, "end": v(-1.2, -0.51) * mm});
            skLineSegment(sketch, "E1428", {"start": v(-1.2, -0.51) * mm, "end": v(-1.2, -0.44) * mm});
            skLineSegment(sketch, "E1429", {"start": v(-1.2, -0.44) * mm, "end": v(-1.21, -0.41) * mm});
            skLineSegment(sketch, "E1430", {"start": v(-1.21, -0.41) * mm, "end": v(-1.22, -0.41) * mm});
            skLineSegment(sketch, "E1431", {"start": v(-1.22, -0.41) * mm, "end": v(-1.24, -0.42) * mm});
            skLineSegment(sketch, "E1432", {"start": v(-1.24, -0.42) * mm, "end": v(-1.26, -0.43) * mm});
            skLineSegment(sketch, "E1433", {"start": v(-1.26, -0.43) * mm, "end": v(-1.3, -0.43) * mm});
            skLineSegment(sketch, "E1434", {"start": v(-1.3, -0.43) * mm, "end": v(-1.33, -0.42) * mm});
            skLineSegment(sketch, "E1435", {"start": v(-1.33, -0.42) * mm, "end": v(-1.4, -0.41) * mm});
            skLineSegment(sketch, "E1436", {"start": v(-1.4, -0.41) * mm, "end": v(-1.54, -0.4) * mm});
            skLineSegment(sketch, "E1437", {"start": v(-1.54, -0.4) * mm, "end": v(-1.72, -0.4) * mm});
            skLineSegment(sketch, "E1438", {"start": v(-1.72, -0.4) * mm, "end": v(-1.9, -0.4) * mm});
            skLineSegment(sketch, "E1439", {"start": v(-1.9, -0.4) * mm, "end": v(-2.06, -0.41) * mm});
            skLineSegment(sketch, "E1440", {"start": v(-2.06, -0.41) * mm, "end": v(-2.2, -0.44) * mm});
            skLineSegment(sketch, "E1441", {"start": v(-2.2, -0.44) * mm, "end": v(-2.34, -0.47) * mm});
            skLineSegment(sketch, "E1442", {"start": v(-2.34, -0.47) * mm, "end": v(-2.51, -0.53) * mm});
            skLineSegment(sketch, "E1443", {"start": v(-2.51, -0.53) * mm, "end": v(-2.7, -0.6) * mm});
            skLineSegment(sketch, "E1444", {"start": v(-2.7, -0.6) * mm, "end": v(-2.87, -0.67) * mm});
            skLineSegment(sketch, "E1445", {"start": v(-2.87, -0.67) * mm, "end": v(-3.05, -0.75) * mm});
            skLineSegment(sketch, "E1446", {"start": v(-3.05, -0.75) * mm, "end": v(-3.21, -0.84) * mm});
            skLineSegment(sketch, "E1447", {"start": v(-3.21, -0.84) * mm, "end": v(-3.36, -0.93) * mm});
            skLineSegment(sketch, "E1448", {"start": v(-3.36, -0.93) * mm, "end": v(-3.5, -1.02) * mm});
            skLineSegment(sketch, "E1449", {"start": v(-3.5, -1.02) * mm, "end": v(-3.62, -1.12) * mm});
            skLineSegment(sketch, "E1450", {"start": v(-3.62, -1.12) * mm, "end": v(-3.68, -1.18) * mm});
            skLineSegment(sketch, "E1451", {"start": v(-3.68, -1.18) * mm, "end": v(-3.77, -1.25) * mm});
            skLineSegment(sketch, "E1452", {"start": v(-3.77, -1.25) * mm, "end": v(-3.87, -1.33) * mm});
            skLineSegment(sketch, "E1453", {"start": v(-3.87, -1.33) * mm, "end": v(-3.95, -1.4) * mm});
            skLineSegment(sketch, "E1454", {"start": v(-3.95, -1.4) * mm, "end": v(-4, -1.43) * mm});
            skLineSegment(sketch, "E1455", {"start": v(-4, -1.43) * mm, "end": v(-4.07, -1.5) * mm});
            skLineSegment(sketch, "E1456", {"start": v(-4.07, -1.5) * mm, "end": v(-4.16, -1.58) * mm});
            skLineSegment(sketch, "E1457", {"start": v(-4.16, -1.58) * mm, "end": v(-4.26, -1.68) * mm});
            skLineSegment(sketch, "E1458", {"start": v(-4.26, -1.68) * mm, "end": v(-4.39, -1.8) * mm});
            skLineSegment(sketch, "E1459", {"start": v(-4.39, -1.8) * mm, "end": v(-4.48, -1.9) * mm});
            skLineSegment(sketch, "E1460", {"start": v(-4.48, -1.9) * mm, "end": v(-4.56, -1.98) * mm});
            skLineSegment(sketch, "E1461", {"start": v(-4.56, -1.98) * mm, "end": v(-4.62, -2.06) * mm});
            skLineSegment(sketch, "E1462", {"start": v(-4.62, -2.06) * mm, "end": v(-4.65, -2.1) * mm});
            skLineSegment(sketch, "E1463", {"start": v(-4.65, -2.1) * mm, "end": v(-4.69, -2.15) * mm});
            skLineSegment(sketch, "E1464", {"start": v(-4.69, -2.15) * mm, "end": v(-4.7, -2.19) * mm});
            skLineSegment(sketch, "E1465", {"start": v(-4.7, -2.19) * mm, "end": v(-4.72, -2.2) * mm});
            skLineSegment(sketch, "E1466", {"start": v(-4.72, -2.2) * mm, "end": v(-4.7, -2.22) * mm});
            skLineSegment(sketch, "E1467", {"start": v(-4.7, -2.22) * mm, "end": v(-4.62, -2.22) * mm});
            skLineSegment(sketch, "E1468", {"start": v(-4.62, -2.22) * mm, "end": v(-4.5, -2.22) * mm});
            skLineSegment(sketch, "E1469", {"start": v(-4.5, -2.22) * mm, "end": v(-4.33, -2.2) * mm});
            skLineSegment(sketch, "E1470", {"start": v(6.83, -2.1) * mm, "end": v(6.97, -2.08) * mm});
            skLineSegment(sketch, "E1471", {"start": v(6.97, -2.08) * mm, "end": v(7.09, -2.06) * mm});
            skLineSegment(sketch, "E1472", {"start": v(7.09, -2.06) * mm, "end": v(7.2, -2.04) * mm});
            skLineSegment(sketch, "E1473", {"start": v(7.2, -2.04) * mm, "end": v(7.35, -2.03) * mm});
            skLineSegment(sketch, "E1474", {"start": v(7.35, -2.03) * mm, "end": v(7.56, -2.02) * mm});
            skLineSegment(sketch, "E1475", {"start": v(7.56, -2.02) * mm, "end": v(7.76, -2.03) * mm});
            skLineSegment(sketch, "E1476", {"start": v(7.76, -2.03) * mm, "end": v(7.95, -2.04) * mm});
            skLineSegment(sketch, "E1477", {"start": v(7.95, -2.04) * mm, "end": v(8.13, -2.07) * mm});
            skLineSegment(sketch, "E1478", {"start": v(8.13, -2.07) * mm, "end": v(8.22, -2.08) * mm});
            skLineSegment(sketch, "E1479", {"start": v(8.22, -2.08) * mm, "end": v(8.33, -2.1) * mm});
            skLineSegment(sketch, "E1480", {"start": v(8.33, -2.1) * mm, "end": v(8.44, -2.1) * mm});
            skLineSegment(sketch, "E1481", {"start": v(8.44, -2.1) * mm, "end": v(8.55, -2.12) * mm});
            skLineSegment(sketch, "E1482", {"start": v(8.55, -2.12) * mm, "end": v(8.64, -2.12) * mm});
            skLineSegment(sketch, "E1483", {"start": v(8.64, -2.12) * mm, "end": v(8.71, -2.13) * mm});
            skLineSegment(sketch, "E1484", {"start": v(8.71, -2.13) * mm, "end": v(8.78, -2.14) * mm});
            skLineSegment(sketch, "E1485", {"start": v(8.78, -2.14) * mm, "end": v(8.8, -2.14) * mm});
            skLineSegment(sketch, "E1486", {"start": v(8.8, -2.14) * mm, "end": v(8.83, -2.14) * mm});
            skLineSegment(sketch, "E1487", {"start": v(8.83, -2.14) * mm, "end": v(8.84, -2.14) * mm});
            skLineSegment(sketch, "E1488", {"start": v(8.84, -2.14) * mm, "end": v(8.85, -2.13) * mm});
            skLineSegment(sketch, "E1489", {"start": v(8.85, -2.13) * mm, "end": v(8.85, -2.12) * mm});
            skLineSegment(sketch, "E1490", {"start": v(8.85, -2.12) * mm, "end": v(8.86, -2.1) * mm});
            skLineSegment(sketch, "E1491", {"start": v(8.86, -2.1) * mm, "end": v(8.86, -2.08) * mm});
            skLineSegment(sketch, "E1492", {"start": v(8.86, -2.08) * mm, "end": v(8.85, -2.05) * mm});
            skLineSegment(sketch, "E1493", {"start": v(8.85, -2.05) * mm, "end": v(8.85, -2) * mm});
            skLineSegment(sketch, "E1494", {"start": v(8.85, -2) * mm, "end": v(8.83, -1.91) * mm});
            skLineSegment(sketch, "E1495", {"start": v(8.83, -1.91) * mm, "end": v(8.8, -1.83) * mm});
            skLineSegment(sketch, "E1496", {"start": v(8.8, -1.83) * mm, "end": v(8.76, -1.72) * mm});
            skLineSegment(sketch, "E1497", {"start": v(8.76, -1.72) * mm, "end": v(8.68, -1.58) * mm});
            skLineSegment(sketch, "E1498", {"start": v(8.68, -1.58) * mm, "end": v(8.6, -1.42) * mm});
            skLineSegment(sketch, "E1499", {"start": v(8.6, -1.42) * mm, "end": v(8.53, -1.32) * mm});
            skLineSegment(sketch, "E1500", {"start": v(8.53, -1.32) * mm, "end": v(8.47, -1.23) * mm});
            skLineSegment(sketch, "E1501", {"start": v(8.47, -1.23) * mm, "end": v(8.38, -1.13) * mm});
            skLineSegment(sketch, "E1502", {"start": v(8.38, -1.13) * mm, "end": v(8.3, -1.06) * mm});
            skLineSegment(sketch, "E1503", {"start": v(8.3, -1.06) * mm, "end": v(8.24, -1) * mm});
            skLineSegment(sketch, "E1504", {"start": v(8.24, -1) * mm, "end": v(8.18, -0.96) * mm});
            skLineSegment(sketch, "E1505", {"start": v(8.18, -0.96) * mm, "end": v(8.12, -0.92) * mm});
            skLineSegment(sketch, "E1506", {"start": v(8.12, -0.92) * mm, "end": v(8.06, -0.89) * mm});
            skLineSegment(sketch, "E1507", {"start": v(8.06, -0.89) * mm, "end": v(7.98, -0.86) * mm});
            skLineSegment(sketch, "E1508", {"start": v(7.98, -0.86) * mm, "end": v(7.9, -0.84) * mm});
            skLineSegment(sketch, "E1509", {"start": v(7.9, -0.84) * mm, "end": v(7.8, -0.81) * mm});
            skLineSegment(sketch, "E1510", {"start": v(7.8, -0.81) * mm, "end": v(7.72, -0.8) * mm});
            skLineSegment(sketch, "E1511", {"start": v(7.72, -0.8) * mm, "end": v(7.65, -0.79) * mm});
            skLineSegment(sketch, "E1512", {"start": v(7.65, -0.79) * mm, "end": v(7.56, -0.78) * mm});
            skLineSegment(sketch, "E1513", {"start": v(7.56, -0.78) * mm, "end": v(7.43, -0.78) * mm});
            skLineSegment(sketch, "E1514", {"start": v(7.43, -0.78) * mm, "end": v(7.35, -0.78) * mm});
            skLineSegment(sketch, "E1515", {"start": v(7.35, -0.78) * mm, "end": v(7.28, -0.79) * mm});
            skLineSegment(sketch, "E1516", {"start": v(7.28, -0.79) * mm, "end": v(7.22, -0.79) * mm});
            skLineSegment(sketch, "E1517", {"start": v(7.22, -0.79) * mm, "end": v(7.17, -0.8) * mm});
            skLineSegment(sketch, "E1518", {"start": v(7.17, -0.8) * mm, "end": v(7.12, -0.8) * mm});
            skLineSegment(sketch, "E1519", {"start": v(7.12, -0.8) * mm, "end": v(7.07, -0.82) * mm});
            skLineSegment(sketch, "E1520", {"start": v(7.07, -0.82) * mm, "end": v(7.01, -0.84) * mm});
            skLineSegment(sketch, "E1521", {"start": v(7.01, -0.84) * mm, "end": v(6.94, -0.87) * mm});
            skLineSegment(sketch, "E1522", {"start": v(6.94, -0.87) * mm, "end": v(6.84, -0.92) * mm});
            skLineSegment(sketch, "E1523", {"start": v(6.84, -0.92) * mm, "end": v(6.76, -0.97) * mm});
            skLineSegment(sketch, "E1524", {"start": v(6.76, -0.97) * mm, "end": v(6.7, -1) * mm});
            skLineSegment(sketch, "E1525", {"start": v(6.7, -1) * mm, "end": v(6.62, -1.06) * mm});
            skLineSegment(sketch, "E1526", {"start": v(6.62, -1.06) * mm, "end": v(6.54, -1.12) * mm});
            skLineSegment(sketch, "E1527", {"start": v(6.54, -1.12) * mm, "end": v(6.45, -1.18) * mm});
            skLineSegment(sketch, "E1528", {"start": v(6.45, -1.18) * mm, "end": v(6.36, -1.24) * mm});
            skLineSegment(sketch, "E1529", {"start": v(6.36, -1.24) * mm, "end": v(6.28, -1.29) * mm});
            skLineSegment(sketch, "E1530", {"start": v(6.28, -1.29) * mm, "end": v(6.21, -1.33) * mm});
            skLineSegment(sketch, "E1531", {"start": v(6.21, -1.33) * mm, "end": v(6.16, -1.35) * mm});
            skLineSegment(sketch, "E1532", {"start": v(6.16, -1.35) * mm, "end": v(6.05, -1.4) * mm});
            skLineSegment(sketch, "E1533", {"start": v(6.05, -1.4) * mm, "end": v(5.94, -1.43) * mm});
            skLineSegment(sketch, "E1534", {"start": v(5.94, -1.43) * mm, "end": v(5.9, -1.44) * mm});
            skLineSegment(sketch, "E1535", {"start": v(5.9, -1.44) * mm, "end": v(5.88, -1.44) * mm});
            skLineSegment(sketch, "E1536", {"start": v(5.88, -1.44) * mm, "end": v(5.9, -1.46) * mm});
            skLineSegment(sketch, "E1537", {"start": v(5.9, -1.46) * mm, "end": v(5.92, -1.48) * mm});
            skLineSegment(sketch, "E1538", {"start": v(5.92, -1.48) * mm, "end": v(5.96, -1.5) * mm});
            skLineSegment(sketch, "E1539", {"start": v(5.96, -1.5) * mm, "end": v(6, -1.55) * mm});
            skLineSegment(sketch, "E1540", {"start": v(6, -1.55) * mm, "end": v(6.07, -1.6) * mm});
            skLineSegment(sketch, "E1541", {"start": v(6.07, -1.6) * mm, "end": v(6.16, -1.68) * mm});
            skLineSegment(sketch, "E1542", {"start": v(6.16, -1.68) * mm, "end": v(6.26, -1.77) * mm});
            skLineSegment(sketch, "E1543", {"start": v(6.26, -1.77) * mm, "end": v(6.37, -1.9) * mm});
            skLineSegment(sketch, "E1544", {"start": v(6.37, -1.9) * mm, "end": v(6.62, -2.15) * mm});
            skLineSegment(sketch, "E1545", {"start": v(6.62, -2.15) * mm, "end": v(6.67, -2.14) * mm});
            skLineSegment(sketch, "E1546", {"start": v(6.67, -2.14) * mm, "end": v(6.7, -2.14) * mm});
            skLineSegment(sketch, "E1547", {"start": v(6.7, -2.14) * mm, "end": v(6.74, -2.13) * mm});
            skLineSegment(sketch, "E1548", {"start": v(6.74, -2.13) * mm, "end": v(6.78, -2.12) * mm});
            skLineSegment(sketch, "E1549", {"start": v(6.78, -2.12) * mm, "end": v(6.83, -2.1) * mm});
            skLineSegment(sketch, "E1550", {"start": v(-8.73, -1.96) * mm, "end": v(-8.68, -1.95) * mm});
            skLineSegment(sketch, "E1551", {"start": v(-8.68, -1.95) * mm, "end": v(-8.64, -1.94) * mm});
            skLineSegment(sketch, "E1552", {"start": v(-8.64, -1.94) * mm, "end": v(-8.6, -1.93) * mm});
            skLineSegment(sketch, "E1553", {"start": v(-8.6, -1.93) * mm, "end": v(-8.56, -1.92) * mm});
            skLineSegment(sketch, "E1554", {"start": v(-8.56, -1.92) * mm, "end": v(-8.45, -1.87) * mm});
            skLineSegment(sketch, "E1555", {"start": v(-8.45, -1.87) * mm, "end": v(-8.35, -1.83) * mm});
            skLineSegment(sketch, "E1556", {"start": v(-8.35, -1.83) * mm, "end": v(-8.27, -1.8) * mm});
            skLineSegment(sketch, "E1557", {"start": v(-8.27, -1.8) * mm, "end": v(-8.2, -1.77) * mm});
            skLineSegment(sketch, "E1558", {"start": v(-8.2, -1.77) * mm, "end": v(-8.13, -1.76) * mm});
            skLineSegment(sketch, "E1559", {"start": v(-8.13, -1.76) * mm, "end": v(-8.07, -1.74) * mm});
            skLineSegment(sketch, "E1560", {"start": v(-8.07, -1.74) * mm, "end": v(-8, -1.73) * mm});
            skLineSegment(sketch, "E1561", {"start": v(-8, -1.73) * mm, "end": v(-7.94, -1.72) * mm});
            skLineSegment(sketch, "E1562", {"start": v(-7.94, -1.72) * mm, "end": v(-7.88, -1.71) * mm});
            skLineSegment(sketch, "E1563", {"start": v(-7.88, -1.71) * mm, "end": v(-7.82, -1.71) * mm});
            skLineSegment(sketch, "E1564", {"start": v(-7.82, -1.71) * mm, "end": v(-7.76, -1.72) * mm});
            skLineSegment(sketch, "E1565", {"start": v(-7.76, -1.72) * mm, "end": v(-7.68, -1.72) * mm});
            skLineSegment(sketch, "E1566", {"start": v(-7.68, -1.72) * mm, "end": v(-7.55, -1.73) * mm});
            skLineSegment(sketch, "E1567", {"start": v(-7.55, -1.73) * mm, "end": v(-7.45, -1.74) * mm});
            skLineSegment(sketch, "E1568", {"start": v(-7.45, -1.74) * mm, "end": v(-7.36, -1.75) * mm});
            skLineSegment(sketch, "E1569", {"start": v(-7.36, -1.75) * mm, "end": v(-7.15, -1.55) * mm});
            skLineSegment(sketch, "E1570", {"start": v(-7.15, -1.55) * mm, "end": v(-7.06, -1.45) * mm});
            skLineSegment(sketch, "E1571", {"start": v(-7.06, -1.45) * mm, "end": v(-6.98, -1.38) * mm});
            skLineSegment(sketch, "E1572", {"start": v(-6.98, -1.38) * mm, "end": v(-6.92, -1.33) * mm});
            skLineSegment(sketch, "E1573", {"start": v(-6.92, -1.33) * mm, "end": v(-6.87, -1.3) * mm});
            skLineSegment(sketch, "E1574", {"start": v(-6.87, -1.3) * mm, "end": v(-6.65, -1.2) * mm});
            skLineSegment(sketch, "E1575", {"start": v(-6.65, -1.2) * mm, "end": v(-6.39, -1.1) * mm});
            skLineSegment(sketch, "E1576", {"start": v(-6.39, -1.1) * mm, "end": v(-6.2, -1.06) * mm});
            skLineSegment(sketch, "E1577", {"start": v(-6.2, -1.06) * mm, "end": v(-6.08, -1.02) * mm});
            skLineSegment(sketch, "E1578", {"start": v(-6.08, -1.02) * mm, "end": v(-5.99, -0.98) * mm});
            skLineSegment(sketch, "E1579", {"start": v(-5.99, -0.98) * mm, "end": v(-5.93, -0.95) * mm});
            skLineSegment(sketch, "E1580", {"start": v(-5.93, -0.95) * mm, "end": v(-5.9, -0.93) * mm});
            skLineSegment(sketch, "E1581", {"start": v(-5.9, -0.93) * mm, "end": v(-5.9, -0.91) * mm});
            skLineSegment(sketch, "E1582", {"start": v(-5.9, -0.91) * mm, "end": v(-5.93, -0.9) * mm});
            skLineSegment(sketch, "E1583", {"start": v(-5.93, -0.9) * mm, "end": v(-6, -0.9) * mm});
            skLineSegment(sketch, "E1584", {"start": v(-6, -0.9) * mm, "end": v(-6.14, -0.9) * mm});
            skLineSegment(sketch, "E1585", {"start": v(-6.14, -0.9) * mm, "end": v(-6.3, -0.87) * mm});
            skLineSegment(sketch, "E1586", {"start": v(-6.3, -0.87) * mm, "end": v(-6.5, -0.82) * mm});
            skLineSegment(sketch, "E1587", {"start": v(-6.5, -0.82) * mm, "end": v(-6.74, -0.75) * mm});
            skLineSegment(sketch, "E1588", {"start": v(-6.74, -0.75) * mm, "end": v(-6.88, -0.72) * mm});
            skLineSegment(sketch, "E1589", {"start": v(-6.88, -0.72) * mm, "end": v(-7.01, -0.69) * mm});
            skLineSegment(sketch, "E1590", {"start": v(-7.01, -0.69) * mm, "end": v(-7.17, -0.66) * mm});
            skLineSegment(sketch, "E1591", {"start": v(-7.17, -0.66) * mm, "end": v(-7.38, -0.64) * mm});
            skLineSegment(sketch, "E1592", {"start": v(-7.38, -0.64) * mm, "end": v(-7.45, -0.64) * mm});
            skLineSegment(sketch, "E1593", {"start": v(-7.45, -0.64) * mm, "end": v(-7.55, -0.65) * mm});
            skLineSegment(sketch, "E1594", {"start": v(-7.55, -0.65) * mm, "end": v(-7.67, -0.67) * mm});
            skLineSegment(sketch, "E1595", {"start": v(-7.67, -0.67) * mm, "end": v(-7.78, -0.68) * mm});
            skLineSegment(sketch, "E1596", {"start": v(-7.78, -0.68) * mm, "end": v(-7.92, -0.72) * mm});
            skLineSegment(sketch, "E1597", {"start": v(-7.92, -0.72) * mm, "end": v(-8.07, -0.77) * mm});
            skLineSegment(sketch, "E1598", {"start": v(-8.07, -0.77) * mm, "end": v(-8.2, -0.83) * mm});
            skLineSegment(sketch, "E1599", {"start": v(-8.2, -0.83) * mm, "end": v(-8.3, -0.88) * mm});
            skLineSegment(sketch, "E1600", {"start": v(-8.3, -0.88) * mm, "end": v(-8.34, -0.91) * mm});
            skLineSegment(sketch, "E1601", {"start": v(-8.34, -0.91) * mm, "end": v(-8.4, -0.96) * mm});
            skLineSegment(sketch, "E1602", {"start": v(-8.4, -0.96) * mm, "end": v(-8.46, -1.02) * mm});
            skLineSegment(sketch, "E1603", {"start": v(-8.46, -1.02) * mm, "end": v(-8.53, -1.1) * mm});
            skLineSegment(sketch, "E1604", {"start": v(-8.53, -1.1) * mm, "end": v(-8.63, -1.2) * mm});
            skLineSegment(sketch, "E1605", {"start": v(-8.63, -1.2) * mm, "end": v(-8.7, -1.3) * mm});
            skLineSegment(sketch, "E1606", {"start": v(-8.7, -1.3) * mm, "end": v(-8.75, -1.37) * mm});
            skLineSegment(sketch, "E1607", {"start": v(-8.75, -1.37) * mm, "end": v(-8.79, -1.47) * mm});
            skLineSegment(sketch, "E1608", {"start": v(-8.79, -1.47) * mm, "end": v(-8.8, -1.53) * mm});
            skLineSegment(sketch, "E1609", {"start": v(-8.8, -1.53) * mm, "end": v(-8.82, -1.6) * mm});
            skLineSegment(sketch, "E1610", {"start": v(-8.82, -1.6) * mm, "end": v(-8.83, -1.7) * mm});
            skLineSegment(sketch, "E1611", {"start": v(-8.83, -1.7) * mm, "end": v(-8.84, -1.78) * mm});
            skLineSegment(sketch, "E1612", {"start": v(-8.84, -1.78) * mm, "end": v(-8.84, -1.85) * mm});
            skLineSegment(sketch, "E1613", {"start": v(-8.84, -1.85) * mm, "end": v(-8.85, -1.92) * mm});
            skLineSegment(sketch, "E1614", {"start": v(-8.85, -1.92) * mm, "end": v(-8.84, -1.96) * mm});
            skLineSegment(sketch, "E1615", {"start": v(-8.84, -1.96) * mm, "end": v(-8.84, -1.98) * mm});
            skLineSegment(sketch, "E1616", {"start": v(-8.84, -1.98) * mm, "end": v(-8.82, -1.98) * mm});
            skLineSegment(sketch, "E1617", {"start": v(-8.82, -1.98) * mm, "end": v(-8.8, -1.97) * mm});
            skLineSegment(sketch, "E1618", {"start": v(-8.8, -1.97) * mm, "end": v(-8.76, -1.97) * mm});
            skLineSegment(sketch, "E1619", {"start": v(-8.76, -1.97) * mm, "end": v(-8.73, -1.96) * mm});
            skLineSegment(sketch, "E1620", {"start": v(-0.35, -1.7) * mm, "end": v(-0.26, -1.67) * mm});
            skLineSegment(sketch, "E1621", {"start": v(-0.26, -1.67) * mm, "end": v(-0.2, -1.64) * mm});
            skLineSegment(sketch, "E1622", {"start": v(-0.2, -1.64) * mm, "end": v(-0.16, -1.6) * mm});
            skLineSegment(sketch, "E1623", {"start": v(-0.16, -1.6) * mm, "end": v(-0.15, -1.55) * mm});
            skLineSegment(sketch, "E1624", {"start": v(-0.15, -1.55) * mm, "end": v(-0.14, -1.52) * mm});
            skLineSegment(sketch, "E1625", {"start": v(-0.14, -1.52) * mm, "end": v(-0.13, -1.5) * mm});
            skLineSegment(sketch, "E1626", {"start": v(-0.13, -1.5) * mm, "end": v(-0.1, -1.48) * mm});
            skLineSegment(sketch, "E1627", {"start": v(-0.1, -1.48) * mm, "end": v(-0.08, -1.48) * mm});
            skLineSegment(sketch, "E1628", {"start": v(-0.08, -1.48) * mm, "end": v(-0.05, -1.49) * mm});
            skLineSegment(sketch, "E1629", {"start": v(-0.05, -1.49) * mm, "end": v(0, -1.51) * mm});
            skLineSegment(sketch, "E1630", {"start": v(0, -1.51) * mm, "end": v(0.1, -1.57) * mm});
            skLineSegment(sketch, "E1631", {"start": v(0.1, -1.57) * mm, "end": v(0.22, -1.59) * mm});
            skLineSegment(sketch, "E1632", {"start": v(0.22, -1.59) * mm, "end": v(0.25, -1.58) * mm});
            skLineSegment(sketch, "E1633", {"start": v(0.25, -1.58) * mm, "end": v(0.28, -1.57) * mm});
            skLineSegment(sketch, "E1634", {"start": v(0.28, -1.57) * mm, "end": v(0.31, -1.56) * mm});
            skLineSegment(sketch, "E1635", {"start": v(0.31, -1.56) * mm, "end": v(0.35, -1.53) * mm});
            skLineSegment(sketch, "E1636", {"start": v(0.35, -1.53) * mm, "end": v(0.42, -1.48) * mm});
            skLineSegment(sketch, "E1637", {"start": v(0.42, -1.48) * mm, "end": v(0.44, -1.39) * mm});
            skLineSegment(sketch, "E1638", {"start": v(0.44, -1.39) * mm, "end": v(0.45, -1.3) * mm});
            skLineSegment(sketch, "E1639", {"start": v(0.45, -1.3) * mm, "end": v(0.45, -1.19) * mm});
            skLineSegment(sketch, "E1640", {"start": v(0.45, -1.19) * mm, "end": v(0.46, -1.07) * mm});
            skLineSegment(sketch, "E1641", {"start": v(0.46, -1.07) * mm, "end": v(0.46, -0.95) * mm});
            skLineSegment(sketch, "E1642", {"start": v(0.46, -0.95) * mm, "end": v(0.46, -0.82) * mm});
            skLineSegment(sketch, "E1643", {"start": v(0.46, -0.82) * mm, "end": v(0.45, -0.7) * mm});
            skLineSegment(sketch, "E1644", {"start": v(0.45, -0.7) * mm, "end": v(0.44, -0.6) * mm});
            skLineSegment(sketch, "E1645", {"start": v(0.44, -0.6) * mm, "end": v(0.43, -0.52) * mm});
            skLineSegment(sketch, "E1646", {"start": v(0.43, -0.52) * mm, "end": v(0.43, -0.49) * mm});
            skLineSegment(sketch, "E1647", {"start": v(0.43, -0.49) * mm, "end": v(0.36, -0.55) * mm});
            skLineSegment(sketch, "E1648", {"start": v(0.36, -0.55) * mm, "end": v(0.3, -0.6) * mm});
            skLineSegment(sketch, "E1649", {"start": v(0.3, -0.6) * mm, "end": v(0.23, -0.65) * mm});
            skLineSegment(sketch, "E1650", {"start": v(0.23, -0.65) * mm, "end": v(0.14, -0.69) * mm});
            skLineSegment(sketch, "E1651", {"start": v(0.14, -0.69) * mm, "end": v(0.03, -0.73) * mm});
            skLineSegment(sketch, "E1652", {"start": v(0.03, -0.73) * mm, "end": v(-0.09, -0.76) * mm});
            skLineSegment(sketch, "E1653", {"start": v(-0.09, -0.76) * mm, "end": v(-0.18, -0.78) * mm});
            skLineSegment(sketch, "E1654", {"start": v(-0.18, -0.78) * mm, "end": v(-0.25, -0.78) * mm});
            skLineSegment(sketch, "E1655", {"start": v(-0.25, -0.78) * mm, "end": v(-0.33, -0.77) * mm});
            skLineSegment(sketch, "E1656", {"start": v(-0.33, -0.77) * mm, "end": v(-0.41, -0.75) * mm});
            skLineSegment(sketch, "E1657", {"start": v(-0.41, -0.75) * mm, "end": v(-0.47, -0.8) * mm});
            skLineSegment(sketch, "E1658", {"start": v(-0.47, -0.8) * mm, "end": v(-0.57, -0.85) * mm});
            skLineSegment(sketch, "E1659", {"start": v(-0.57, -0.85) * mm, "end": v(-0.67, -0.9) * mm});
            skLineSegment(sketch, "E1660", {"start": v(-0.67, -0.9) * mm, "end": v(-0.77, -0.92) * mm});
            skLineSegment(sketch, "E1661", {"start": v(-0.77, -0.92) * mm, "end": v(-0.85, -0.93) * mm});
            skLineSegment(sketch, "E1662", {"start": v(-0.85, -0.93) * mm, "end": v(-0.9, -0.92) * mm});
            skLineSegment(sketch, "E1663", {"start": v(-0.9, -0.92) * mm, "end": v(-0.94, -0.91) * mm});
            skLineSegment(sketch, "E1664", {"start": v(-0.94, -0.91) * mm, "end": v(-0.95, -0.91) * mm});
            skLineSegment(sketch, "E1665", {"start": v(-0.95, -0.91) * mm, "end": v(-0.95, -0.91) * mm});
            skLineSegment(sketch, "E1666", {"start": v(-0.95, -0.91) * mm, "end": v(-0.96, -0.92) * mm});
            skLineSegment(sketch, "E1667", {"start": v(-0.96, -0.92) * mm, "end": v(-0.96, -0.94) * mm});
            skLineSegment(sketch, "E1668", {"start": v(-0.96, -0.94) * mm, "end": v(-0.95, -0.98) * mm});
            skLineSegment(sketch, "E1669", {"start": v(-0.95, -0.98) * mm, "end": v(-0.94, -1.03) * mm});
            skLineSegment(sketch, "E1670", {"start": v(-0.94, -1.03) * mm, "end": v(-0.93, -1.1) * mm});
            skLineSegment(sketch, "E1671", {"start": v(-0.93, -1.1) * mm, "end": v(-0.91, -1.22) * mm});
            skLineSegment(sketch, "E1672", {"start": v(-0.91, -1.22) * mm, "end": v(-0.9, -1.33) * mm});
            skLineSegment(sketch, "E1673", {"start": v(-0.9, -1.33) * mm, "end": v(-0.88, -1.41) * mm});
            skLineSegment(sketch, "E1674", {"start": v(-0.88, -1.41) * mm, "end": v(-0.87, -1.48) * mm});
            skLineSegment(sketch, "E1675", {"start": v(-0.87, -1.48) * mm, "end": v(-0.86, -1.52) * mm});
            skLineSegment(sketch, "E1676", {"start": v(-0.86, -1.52) * mm, "end": v(-0.85, -1.56) * mm});
            skLineSegment(sketch, "E1677", {"start": v(-0.85, -1.56) * mm, "end": v(-0.83, -1.58) * mm});
            skLineSegment(sketch, "E1678", {"start": v(-0.83, -1.58) * mm, "end": v(-0.82, -1.6) * mm});
            skLineSegment(sketch, "E1679", {"start": v(-0.82, -1.6) * mm, "end": v(-0.8, -1.61) * mm});
            skLineSegment(sketch, "E1680", {"start": v(-0.8, -1.61) * mm, "end": v(-0.76, -1.64) * mm});
            skLineSegment(sketch, "E1681", {"start": v(-0.76, -1.64) * mm, "end": v(-0.71, -1.67) * mm});
            skLineSegment(sketch, "E1682", {"start": v(-0.71, -1.67) * mm, "end": v(-0.66, -1.7) * mm});
            skLineSegment(sketch, "E1683", {"start": v(-0.66, -1.7) * mm, "end": v(-0.62, -1.71) * mm});
            skLineSegment(sketch, "E1684", {"start": v(-0.62, -1.71) * mm, "end": v(-0.56, -1.72) * mm});
            skLineSegment(sketch, "E1685", {"start": v(-0.56, -1.72) * mm, "end": v(-0.48, -1.72) * mm});
            skLineSegment(sketch, "E1686", {"start": v(-0.48, -1.72) * mm, "end": v(-0.4, -1.72) * mm});
            skLineSegment(sketch, "E1687", {"start": v(-0.4, -1.72) * mm, "end": v(-0.35, -1.7) * mm});
            skLineSegment(sketch, "E1688", {"start": v(5.63, -1.25) * mm, "end": v(5.66, -1.24) * mm});
            skLineSegment(sketch, "E1689", {"start": v(5.66, -1.24) * mm, "end": v(5.7, -1.23) * mm});
            skLineSegment(sketch, "E1690", {"start": v(5.7, -1.23) * mm, "end": v(5.75, -1.22) * mm});
            skLineSegment(sketch, "E1691", {"start": v(5.75, -1.22) * mm, "end": v(5.8, -1.22) * mm});
            skLineSegment(sketch, "E1692", {"start": v(5.8, -1.22) * mm, "end": v(5.88, -1.2) * mm});
            skLineSegment(sketch, "E1693", {"start": v(5.88, -1.2) * mm, "end": v(5.98, -1.15) * mm});
            skLineSegment(sketch, "E1694", {"start": v(5.98, -1.15) * mm, "end": v(6.07, -1.1) * mm});
            skLineSegment(sketch, "E1695", {"start": v(6.07, -1.1) * mm, "end": v(6.15, -1.06) * mm});
            skLineSegment(sketch, "E1696", {"start": v(6.15, -1.06) * mm, "end": v(6.18, -1.03) * mm});
            skLineSegment(sketch, "E1697", {"start": v(6.18, -1.03) * mm, "end": v(6.22, -1) * mm});
            skLineSegment(sketch, "E1698", {"start": v(6.22, -1) * mm, "end": v(6.27, -0.96) * mm});
            skLineSegment(sketch, "E1699", {"start": v(6.27, -0.96) * mm, "end": v(6.31, -0.92) * mm});
            skLineSegment(sketch, "E1700", {"start": v(6.31, -0.92) * mm, "end": v(6.36, -0.88) * mm});
            skLineSegment(sketch, "E1701", {"start": v(6.36, -0.88) * mm, "end": v(6.41, -0.83) * mm});
            skLineSegment(sketch, "E1702", {"start": v(6.41, -0.83) * mm, "end": v(6.46, -0.8) * mm});
            skLineSegment(sketch, "E1703", {"start": v(6.46, -0.8) * mm, "end": v(6.5, -0.77) * mm});
            skLineSegment(sketch, "E1704", {"start": v(6.5, -0.77) * mm, "end": v(6.52, -0.76) * mm});
            skLineSegment(sketch, "E1705", {"start": v(6.52, -0.76) * mm, "end": v(6.54, -0.74) * mm});
            skLineSegment(sketch, "E1706", {"start": v(6.54, -0.74) * mm, "end": v(6.56, -0.73) * mm});
            skLineSegment(sketch, "E1707", {"start": v(6.56, -0.73) * mm, "end": v(6.56, -0.72) * mm});
            skLineSegment(sketch, "E1708", {"start": v(6.56, -0.72) * mm, "end": v(6.55, -0.71) * mm});
            skLineSegment(sketch, "E1709", {"start": v(6.55, -0.71) * mm, "end": v(6.53, -0.7) * mm});
            skLineSegment(sketch, "E1710", {"start": v(6.53, -0.7) * mm, "end": v(6.5, -0.7) * mm});
            skLineSegment(sketch, "E1711", {"start": v(6.5, -0.7) * mm, "end": v(6.47, -0.7) * mm});
            skLineSegment(sketch, "E1712", {"start": v(6.47, -0.7) * mm, "end": v(6.32, -0.7) * mm});
            skLineSegment(sketch, "E1713", {"start": v(6.32, -0.7) * mm, "end": v(6.14, -0.69) * mm});
            skLineSegment(sketch, "E1714", {"start": v(6.14, -0.69) * mm, "end": v(5.95, -0.67) * mm});
            skLineSegment(sketch, "E1715", {"start": v(5.95, -0.67) * mm, "end": v(5.8, -0.66) * mm});
            skLineSegment(sketch, "E1716", {"start": v(5.8, -0.66) * mm, "end": v(5.65, -0.64) * mm});
            skLineSegment(sketch, "E1717", {"start": v(5.65, -0.64) * mm, "end": v(5.5, -0.63) * mm});
            skLineSegment(sketch, "E1718", {"start": v(5.5, -0.63) * mm, "end": v(5.34, -0.6) * mm});
            skLineSegment(sketch, "E1719", {"start": v(5.34, -0.6) * mm, "end": v(5.19, -0.59) * mm});
            skLineSegment(sketch, "E1720", {"start": v(5.19, -0.59) * mm, "end": v(5.04, -0.57) * mm});
            skLineSegment(sketch, "E1721", {"start": v(5.04, -0.57) * mm, "end": v(4.92, -0.55) * mm});
            skLineSegment(sketch, "E1722", {"start": v(4.92, -0.55) * mm, "end": v(4.82, -0.54) * mm});
            skLineSegment(sketch, "E1723", {"start": v(4.82, -0.54) * mm, "end": v(4.75, -0.53) * mm});
            skLineSegment(sketch, "E1724", {"start": v(4.75, -0.53) * mm, "end": v(4.57, -0.5) * mm});
            skLineSegment(sketch, "E1725", {"start": v(4.57, -0.5) * mm, "end": v(4.44, -0.47) * mm});
            skLineSegment(sketch, "E1726", {"start": v(4.44, -0.47) * mm, "end": v(4.37, -0.45) * mm});
            skLineSegment(sketch, "E1727", {"start": v(4.37, -0.45) * mm, "end": v(4.33, -0.44) * mm});
            skLineSegment(sketch, "E1728", {"start": v(4.33, -0.44) * mm, "end": v(4.29, -0.43) * mm});
            skLineSegment(sketch, "E1729", {"start": v(4.29, -0.43) * mm, "end": v(4.24, -0.42) * mm});
            skLineSegment(sketch, "E1730", {"start": v(4.24, -0.42) * mm, "end": v(4.2, -0.42) * mm});
            skLineSegment(sketch, "E1731", {"start": v(4.2, -0.42) * mm, "end": v(4.13, -0.4) * mm});
            skLineSegment(sketch, "E1732", {"start": v(4.13, -0.4) * mm, "end": v(4.06, -0.4) * mm});
            skLineSegment(sketch, "E1733", {"start": v(4.06, -0.4) * mm, "end": v(4, -0.39) * mm});
            skLineSegment(sketch, "E1734", {"start": v(4, -0.39) * mm, "end": v(3.95, -0.4) * mm});
            skLineSegment(sketch, "E1735", {"start": v(3.95, -0.4) * mm, "end": v(3.91, -0.4) * mm});
            skLineSegment(sketch, "E1736", {"start": v(3.91, -0.4) * mm, "end": v(3.9, -0.41) * mm});
            skLineSegment(sketch, "E1737", {"start": v(3.9, -0.41) * mm, "end": v(3.88, -0.43) * mm});
            skLineSegment(sketch, "E1738", {"start": v(3.88, -0.43) * mm, "end": v(3.87, -0.45) * mm});
            skLineSegment(sketch, "E1739", {"start": v(3.87, -0.45) * mm, "end": v(3.86, -0.47) * mm});
            skLineSegment(sketch, "E1740", {"start": v(3.86, -0.47) * mm, "end": v(3.85, -0.52) * mm});
            skLineSegment(sketch, "E1741", {"start": v(3.85, -0.52) * mm, "end": v(3.85, -0.58) * mm});
            skLineSegment(sketch, "E1742", {"start": v(3.85, -0.58) * mm, "end": v(3.88, -0.66) * mm});
            skLineSegment(sketch, "E1743", {"start": v(3.88, -0.66) * mm, "end": v(3.94, -0.78) * mm});
            skLineSegment(sketch, "E1744", {"start": v(3.94, -0.78) * mm, "end": v(3.98, -0.85) * mm});
            skLineSegment(sketch, "E1745", {"start": v(3.98, -0.85) * mm, "end": v(4.01, -0.92) * mm});
            skLineSegment(sketch, "E1746", {"start": v(4.01, -0.92) * mm, "end": v(4.04, -0.98) * mm});
            skLineSegment(sketch, "E1747", {"start": v(4.04, -0.98) * mm, "end": v(4.06, -1.02) * mm});
            skLineSegment(sketch, "E1748", {"start": v(4.06, -1.02) * mm, "end": v(4.07, -1.05) * mm});
            skLineSegment(sketch, "E1749", {"start": v(4.07, -1.05) * mm, "end": v(4.08, -1.08) * mm});
            skLineSegment(sketch, "E1750", {"start": v(4.08, -1.08) * mm, "end": v(4.1, -1.1) * mm});
            skLineSegment(sketch, "E1751", {"start": v(4.1, -1.1) * mm, "end": v(4.1, -1.11) * mm});
            skLineSegment(sketch, "E1752", {"start": v(4.1, -1.11) * mm, "end": v(4.13, -1.12) * mm});
            skLineSegment(sketch, "E1753", {"start": v(4.13, -1.12) * mm, "end": v(4.17, -1.14) * mm});
            skLineSegment(sketch, "E1754", {"start": v(4.17, -1.14) * mm, "end": v(4.23, -1.15) * mm});
            skLineSegment(sketch, "E1755", {"start": v(4.23, -1.15) * mm, "end": v(4.3, -1.16) * mm});
            skLineSegment(sketch, "E1756", {"start": v(4.3, -1.16) * mm, "end": v(4.39, -1.18) * mm});
            skLineSegment(sketch, "E1757", {"start": v(4.39, -1.18) * mm, "end": v(4.46, -1.19) * mm});
            skLineSegment(sketch, "E1758", {"start": v(4.46, -1.19) * mm, "end": v(4.54, -1.19) * mm});
            skLineSegment(sketch, "E1759", {"start": v(4.54, -1.19) * mm, "end": v(4.64, -1.18) * mm});
            skLineSegment(sketch, "E1760", {"start": v(4.64, -1.18) * mm, "end": v(4.72, -1.18) * mm});
            skLineSegment(sketch, "E1761", {"start": v(4.72, -1.18) * mm, "end": v(4.79, -1.18) * mm});
            skLineSegment(sketch, "E1762", {"start": v(4.79, -1.18) * mm, "end": v(4.84, -1.17) * mm});
            skLineSegment(sketch, "E1763", {"start": v(4.84, -1.17) * mm, "end": v(4.88, -1.17) * mm});
            skLineSegment(sketch, "E1764", {"start": v(4.88, -1.17) * mm, "end": v(4.91, -1.16) * mm});
            skLineSegment(sketch, "E1765", {"start": v(4.91, -1.16) * mm, "end": v(4.96, -1.16) * mm});
            skLineSegment(sketch, "E1766", {"start": v(4.96, -1.16) * mm, "end": v(5, -1.16) * mm});
            skLineSegment(sketch, "E1767", {"start": v(5, -1.16) * mm, "end": v(5.06, -1.16) * mm});
            skLineSegment(sketch, "E1768", {"start": v(5.06, -1.16) * mm, "end": v(5.13, -1.16) * mm});
            skLineSegment(sketch, "E1769", {"start": v(5.13, -1.16) * mm, "end": v(5.2, -1.16) * mm});
            skLineSegment(sketch, "E1770", {"start": v(5.2, -1.16) * mm, "end": v(5.25, -1.17) * mm});
            skLineSegment(sketch, "E1771", {"start": v(5.25, -1.17) * mm, "end": v(5.32, -1.19) * mm});
            skLineSegment(sketch, "E1772", {"start": v(5.32, -1.19) * mm, "end": v(5.37, -1.2) * mm});
            skLineSegment(sketch, "E1773", {"start": v(5.37, -1.2) * mm, "end": v(5.42, -1.22) * mm});
            skLineSegment(sketch, "E1774", {"start": v(5.42, -1.22) * mm, "end": v(5.47, -1.23) * mm});
            skLineSegment(sketch, "E1775", {"start": v(5.47, -1.23) * mm, "end": v(5.5, -1.24) * mm});
            skLineSegment(sketch, "E1776", {"start": v(5.5, -1.24) * mm, "end": v(5.53, -1.26) * mm});
            skLineSegment(sketch, "E1777", {"start": v(5.53, -1.26) * mm, "end": v(5.55, -1.26) * mm});
            skLineSegment(sketch, "E1778", {"start": v(5.55, -1.26) * mm, "end": v(5.58, -1.26) * mm});
            skLineSegment(sketch, "E1779", {"start": v(5.58, -1.26) * mm, "end": v(5.63, -1.25) * mm});
            skLineSegment(sketch, "E1780", {"start": v(3.9, -1.04) * mm, "end": v(3.9, -1.02) * mm});
            skLineSegment(sketch, "E1781", {"start": v(3.9, -1.02) * mm, "end": v(3.88, -0.98) * mm});
            skLineSegment(sketch, "E1782", {"start": v(3.88, -0.98) * mm, "end": v(3.86, -0.93) * mm});
            skLineSegment(sketch, "E1783", {"start": v(3.86, -0.93) * mm, "end": v(3.83, -0.87) * mm});
            skLineSegment(sketch, "E1784", {"start": v(3.83, -0.87) * mm, "end": v(3.8, -0.81) * mm});
            skLineSegment(sketch, "E1785", {"start": v(3.8, -0.81) * mm, "end": v(3.75, -0.74) * mm});
            skLineSegment(sketch, "E1786", {"start": v(3.75, -0.74) * mm, "end": v(3.71, -0.68) * mm});
            skLineSegment(sketch, "E1787", {"start": v(3.71, -0.68) * mm, "end": v(3.68, -0.62) * mm});
            skLineSegment(sketch, "E1788", {"start": v(3.68, -0.62) * mm, "end": v(3.62, -0.54) * mm});
            skLineSegment(sketch, "E1789", {"start": v(3.62, -0.54) * mm, "end": v(3.56, -0.47) * mm});
            skLineSegment(sketch, "E1790", {"start": v(3.56, -0.47) * mm, "end": v(3.51, -0.41) * mm});
            skLineSegment(sketch, "E1791", {"start": v(3.51, -0.41) * mm, "end": v(3.44, -0.35) * mm});
            skLineSegment(sketch, "E1792", {"start": v(3.44, -0.35) * mm, "end": v(3.4, -0.3) * mm});
            skLineSegment(sketch, "E1793", {"start": v(3.4, -0.3) * mm, "end": v(3.34, -0.25) * mm});
            skLineSegment(sketch, "E1794", {"start": v(3.34, -0.25) * mm, "end": v(3.3, -0.22) * mm});
            skLineSegment(sketch, "E1795", {"start": v(3.3, -0.22) * mm, "end": v(3.26, -0.2) * mm});
            skLineSegment(sketch, "E1796", {"start": v(3.26, -0.2) * mm, "end": v(3.08, -0.1) * mm});
            skLineSegment(sketch, "E1797", {"start": v(3.08, -0.1) * mm, "end": v(2.93, 0) * mm});
            skLineSegment(sketch, "E1798", {"start": v(2.93, 0) * mm, "end": v(2.8, 0.06) * mm});
            skLineSegment(sketch, "E1799", {"start": v(2.8, 0.06) * mm, "end": v(2.69, 0.11) * mm});
            skLineSegment(sketch, "E1800", {"start": v(2.69, 0.11) * mm, "end": v(2.58, 0.15) * mm});
            skLineSegment(sketch, "E1801", {"start": v(2.58, 0.15) * mm, "end": v(2.47, 0.18) * mm});
            skLineSegment(sketch, "E1802", {"start": v(2.47, 0.18) * mm, "end": v(2.36, 0.2) * mm});
            skLineSegment(sketch, "E1803", {"start": v(2.36, 0.2) * mm, "end": v(2.25, 0.23) * mm});
            skLineSegment(sketch, "E1804", {"start": v(2.25, 0.23) * mm, "end": v(2.17, 0.24) * mm});
            skLineSegment(sketch, "E1805", {"start": v(2.17, 0.24) * mm, "end": v(2.06, 0.24) * mm});
            skLineSegment(sketch, "E1806", {"start": v(2.06, 0.24) * mm, "end": v(1.92, 0.25) * mm});
            skLineSegment(sketch, "E1807", {"start": v(1.92, 0.25) * mm, "end": v(1.78, 0.25) * mm});
            skLineSegment(sketch, "E1808", {"start": v(1.78, 0.25) * mm, "end": v(1.63, 0.26) * mm});
            skLineSegment(sketch, "E1809", {"start": v(1.63, 0.26) * mm, "end": v(1.5, 0.25) * mm});
            skLineSegment(sketch, "E1810", {"start": v(1.5, 0.25) * mm, "end": v(1.38, 0.25) * mm});
            skLineSegment(sketch, "E1811", {"start": v(1.38, 0.25) * mm, "end": v(1.29, 0.25) * mm});
            skLineSegment(sketch, "E1812", {"start": v(1.29, 0.25) * mm, "end": v(1.18, 0.23) * mm});
            skLineSegment(sketch, "E1813", {"start": v(1.18, 0.23) * mm, "end": v(1.08, 0.21) * mm});
            skLineSegment(sketch, "E1814", {"start": v(1.08, 0.21) * mm, "end": v(0.97, 0.2) * mm});
            skLineSegment(sketch, "E1815", {"start": v(0.97, 0.2) * mm, "end": v(0.87, 0.17) * mm});
            skLineSegment(sketch, "E1816", {"start": v(0.87, 0.17) * mm, "end": v(0.78, 0.14) * mm});
            skLineSegment(sketch, "E1817", {"start": v(0.78, 0.14) * mm, "end": v(0.7, 0.12) * mm});
            skLineSegment(sketch, "E1818", {"start": v(0.7, 0.12) * mm, "end": v(0.66, 0.1) * mm});
            skLineSegment(sketch, "E1819", {"start": v(0.66, 0.1) * mm, "end": v(0.64, 0.07) * mm});
            skLineSegment(sketch, "E1820", {"start": v(0.64, 0.07) * mm, "end": v(0.64, 0.05) * mm});
            skLineSegment(sketch, "E1821", {"start": v(0.64, 0.05) * mm, "end": v(0.64, 0) * mm});
            skLineSegment(sketch, "E1822", {"start": v(0.64, 0) * mm, "end": v(0.64, -0.07) * mm});
            skLineSegment(sketch, "E1823", {"start": v(0.64, -0.07) * mm, "end": v(0.65, -0.15) * mm});
            skLineSegment(sketch, "E1824", {"start": v(0.65, -0.15) * mm, "end": v(0.65, -0.24) * mm});
            skLineSegment(sketch, "E1825", {"start": v(0.65, -0.24) * mm, "end": v(0.66, -0.31) * mm});
            skLineSegment(sketch, "E1826", {"start": v(0.66, -0.31) * mm, "end": v(0.67, -0.38) * mm});
            skLineSegment(sketch, "E1827", {"start": v(0.67, -0.38) * mm, "end": v(0.67, -0.42) * mm});
            skLineSegment(sketch, "E1828", {"start": v(0.67, -0.42) * mm, "end": v(0.68, -0.47) * mm});
            skLineSegment(sketch, "E1829", {"start": v(0.68, -0.47) * mm, "end": v(0.72, -0.47) * mm});
            skLineSegment(sketch, "E1830", {"start": v(0.72, -0.47) * mm, "end": v(0.8, -0.47) * mm});
            skLineSegment(sketch, "E1831", {"start": v(0.8, -0.47) * mm, "end": v(0.91, -0.48) * mm});
            skLineSegment(sketch, "E1832", {"start": v(0.91, -0.48) * mm, "end": v(1.05, -0.49) * mm});
            skLineSegment(sketch, "E1833", {"start": v(1.05, -0.49) * mm, "end": v(1.2, -0.5) * mm});
            skLineSegment(sketch, "E1834", {"start": v(1.2, -0.5) * mm, "end": v(1.34, -0.52) * mm});
            skLineSegment(sketch, "E1835", {"start": v(1.34, -0.52) * mm, "end": v(1.48, -0.55) * mm});
            skLineSegment(sketch, "E1836", {"start": v(1.48, -0.55) * mm, "end": v(1.61, -0.57) * mm});
            skLineSegment(sketch, "E1837", {"start": v(1.61, -0.57) * mm, "end": v(1.71, -0.6) * mm});
            skLineSegment(sketch, "E1838", {"start": v(1.71, -0.6) * mm, "end": v(1.78, -0.6) * mm});
            skLineSegment(sketch, "E1839", {"start": v(1.78, -0.6) * mm, "end": v(1.85, -0.62) * mm});
            skLineSegment(sketch, "E1840", {"start": v(1.85, -0.62) * mm, "end": v(1.95, -0.65) * mm});
            skLineSegment(sketch, "E1841", {"start": v(1.95, -0.65) * mm, "end": v(2.08, -0.69) * mm});
            skLineSegment(sketch, "E1842", {"start": v(2.08, -0.69) * mm, "end": v(2.22, -0.73) * mm});
            skLineSegment(sketch, "E1843", {"start": v(2.22, -0.73) * mm, "end": v(2.34, -0.78) * mm});
            skLineSegment(sketch, "E1844", {"start": v(2.34, -0.78) * mm, "end": v(2.39, -0.8) * mm});
            skLineSegment(sketch, "E1845", {"start": v(2.39, -0.8) * mm, "end": v(2.45, -0.83) * mm});
            skLineSegment(sketch, "E1846", {"start": v(2.45, -0.83) * mm, "end": v(2.5, -0.86) * mm});
            skLineSegment(sketch, "E1847", {"start": v(2.5, -0.86) * mm, "end": v(2.55, -0.9) * mm});
            skLineSegment(sketch, "E1848", {"start": v(2.55, -0.9) * mm, "end": v(2.66, -0.96) * mm});
            skLineSegment(sketch, "E1849", {"start": v(2.66, -0.96) * mm, "end": v(2.8, -0.95) * mm});
            skLineSegment(sketch, "E1850", {"start": v(2.8, -0.95) * mm, "end": v(2.94, -0.94) * mm});
            skLineSegment(sketch, "E1851", {"start": v(2.94, -0.94) * mm, "end": v(3.09, -0.94) * mm});
            skLineSegment(sketch, "E1852", {"start": v(3.09, -0.94) * mm, "end": v(3.23, -0.94) * mm});
            skLineSegment(sketch, "E1853", {"start": v(3.23, -0.94) * mm, "end": v(3.38, -0.95) * mm});
            skLineSegment(sketch, "E1854", {"start": v(3.38, -0.95) * mm, "end": v(3.51, -0.97) * mm});
            skLineSegment(sketch, "E1855", {"start": v(3.51, -0.97) * mm, "end": v(3.64, -0.99) * mm});
            skLineSegment(sketch, "E1856", {"start": v(3.64, -0.99) * mm, "end": v(3.75, -1.01) * mm});
            skLineSegment(sketch, "E1857", {"start": v(3.75, -1.01) * mm, "end": v(3.83, -1.04) * mm});
            skLineSegment(sketch, "E1858", {"start": v(3.83, -1.04) * mm, "end": v(3.87, -1.05) * mm});
            skLineSegment(sketch, "E1859", {"start": v(3.87, -1.05) * mm, "end": v(3.9, -1.05) * mm});
            skLineSegment(sketch, "E1860", {"start": v(3.9, -1.05) * mm, "end": v(3.9, -1.05) * mm});
            skLineSegment(sketch, "E1861", {"start": v(3.9, -1.05) * mm, "end": v(3.9, -1.04) * mm});
            skLineSegment(sketch, "E1862", {"start": v(-5.48, -0.7) * mm, "end": v(-5.42, -0.68) * mm});
            skLineSegment(sketch, "E1863", {"start": v(-5.42, -0.68) * mm, "end": v(-5.36, -0.66) * mm});
            skLineSegment(sketch, "E1864", {"start": v(-5.36, -0.66) * mm, "end": v(-5.3, -0.65) * mm});
            skLineSegment(sketch, "E1865", {"start": v(-5.3, -0.65) * mm, "end": v(-5.26, -0.64) * mm});
            skLineSegment(sketch, "E1866", {"start": v(-5.26, -0.64) * mm, "end": v(-5.16, -0.63) * mm});
            skLineSegment(sketch, "E1867", {"start": v(-5.16, -0.63) * mm, "end": v(-5.03, -0.63) * mm});
            skLineSegment(sketch, "E1868", {"start": v(-5.03, -0.63) * mm, "end": v(-4.89, -0.63) * mm});
            skLineSegment(sketch, "E1869", {"start": v(-4.89, -0.63) * mm, "end": v(-4.75, -0.64) * mm});
            skLineSegment(sketch, "E1870", {"start": v(-4.75, -0.64) * mm, "end": v(-4.65, -0.64) * mm});
            skLineSegment(sketch, "E1871", {"start": v(-4.65, -0.64) * mm, "end": v(-4.6, -0.52) * mm});
            skLineSegment(sketch, "E1872", {"start": v(-4.6, -0.52) * mm, "end": v(-4.53, -0.4) * mm});
            skLineSegment(sketch, "E1873", {"start": v(-4.53, -0.4) * mm, "end": v(-4.46, -0.3) * mm});
            skLineSegment(sketch, "E1874", {"start": v(-4.46, -0.3) * mm, "end": v(-4.37, -0.18) * mm});
            skLineSegment(sketch, "E1875", {"start": v(-4.37, -0.18) * mm, "end": v(-4.25, -0.05) * mm});
            skLineSegment(sketch, "E1876", {"start": v(-4.25, -0.05) * mm, "end": v(-4.09, 0.1) * mm});
            skLineSegment(sketch, "E1877", {"start": v(-4.09, 0.1) * mm, "end": v(-3.91, 0.25) * mm});
            skLineSegment(sketch, "E1878", {"start": v(-3.91, 0.25) * mm, "end": v(-3.71, 0.38) * mm});
            skLineSegment(sketch, "E1879", {"start": v(-3.71, 0.38) * mm, "end": v(-3.47, 0.5) * mm});
            skLineSegment(sketch, "E1880", {"start": v(-3.47, 0.5) * mm, "end": v(-3.38, 0.55) * mm});
            skLineSegment(sketch, "E1881", {"start": v(-3.38, 0.55) * mm, "end": v(-3.3, 0.59) * mm});
            skLineSegment(sketch, "E1882", {"start": v(-3.3, 0.59) * mm, "end": v(-3.26, 0.61) * mm});
            skLineSegment(sketch, "E1883", {"start": v(-3.26, 0.61) * mm, "end": v(-3.24, 0.63) * mm});
            skLineSegment(sketch, "E1884", {"start": v(-3.24, 0.63) * mm, "end": v(-3.26, 0.63) * mm});
            skLineSegment(sketch, "E1885", {"start": v(-3.26, 0.63) * mm, "end": v(-3.3, 0.63) * mm});
            skLineSegment(sketch, "E1886", {"start": v(-3.3, 0.63) * mm, "end": v(-3.38, 0.63) * mm});
            skLineSegment(sketch, "E1887", {"start": v(-3.38, 0.63) * mm, "end": v(-3.47, 0.62) * mm});
            skLineSegment(sketch, "E1888", {"start": v(-3.47, 0.62) * mm, "end": v(-3.58, 0.6) * mm});
            skLineSegment(sketch, "E1889", {"start": v(-3.58, 0.6) * mm, "end": v(-3.73, 0.58) * mm});
            skLineSegment(sketch, "E1890", {"start": v(-3.73, 0.58) * mm, "end": v(-3.9, 0.54) * mm});
            skLineSegment(sketch, "E1891", {"start": v(-3.9, 0.54) * mm, "end": v(-4.1, 0.5) * mm});
            skLineSegment(sketch, "E1892", {"start": v(-4.1, 0.5) * mm, "end": v(-4.3, 0.44) * mm});
            skLineSegment(sketch, "E1893", {"start": v(-4.3, 0.44) * mm, "end": v(-4.5, 0.4) * mm});
            skLineSegment(sketch, "E1894", {"start": v(-4.5, 0.4) * mm, "end": v(-4.68, 0.34) * mm});
            skLineSegment(sketch, "E1895", {"start": v(-4.68, 0.34) * mm, "end": v(-4.83, 0.3) * mm});
            skLineSegment(sketch, "E1896", {"start": v(-4.83, 0.3) * mm, "end": v(-5.27, 0.12) * mm});
            skLineSegment(sketch, "E1897", {"start": v(-5.27, 0.12) * mm, "end": v(-5.71, -0.11) * mm});
            skLineSegment(sketch, "E1898", {"start": v(-5.71, -0.11) * mm, "end": v(-5.76, -0.14) * mm});
            skLineSegment(sketch, "E1899", {"start": v(-5.76, -0.14) * mm, "end": v(-5.82, -0.17) * mm});
            skLineSegment(sketch, "E1900", {"start": v(-5.82, -0.17) * mm, "end": v(-5.9, -0.21) * mm});
            skLineSegment(sketch, "E1901", {"start": v(-5.9, -0.21) * mm, "end": v(-5.97, -0.25) * mm});
            skLineSegment(sketch, "E1902", {"start": v(-5.97, -0.25) * mm, "end": v(-6.05, -0.3) * mm});
            skLineSegment(sketch, "E1903", {"start": v(-6.05, -0.3) * mm, "end": v(-6.12, -0.32) * mm});
            skLineSegment(sketch, "E1904", {"start": v(-6.12, -0.32) * mm, "end": v(-6.18, -0.35) * mm});
            skLineSegment(sketch, "E1905", {"start": v(-6.18, -0.35) * mm, "end": v(-6.23, -0.37) * mm});
            skLineSegment(sketch, "E1906", {"start": v(-6.23, -0.37) * mm, "end": v(-6.26, -0.38) * mm});
            skLineSegment(sketch, "E1907", {"start": v(-6.26, -0.38) * mm, "end": v(-6.3, -0.4) * mm});
            skLineSegment(sketch, "E1908", {"start": v(-6.3, -0.4) * mm, "end": v(-6.35, -0.42) * mm});
            skLineSegment(sketch, "E1909", {"start": v(-6.35, -0.42) * mm, "end": v(-6.4, -0.44) * mm});
            skLineSegment(sketch, "E1910", {"start": v(-6.4, -0.44) * mm, "end": v(-6.54, -0.5) * mm});
            skLineSegment(sketch, "E1911", {"start": v(-6.54, -0.5) * mm, "end": v(-6.68, -0.53) * mm});
            skLineSegment(sketch, "E1912", {"start": v(-6.68, -0.53) * mm, "end": v(-6.73, -0.54) * mm});
            skLineSegment(sketch, "E1913", {"start": v(-6.73, -0.54) * mm, "end": v(-6.76, -0.54) * mm});
            skLineSegment(sketch, "E1914", {"start": v(-6.76, -0.54) * mm, "end": v(-6.76, -0.55) * mm});
            skLineSegment(sketch, "E1915", {"start": v(-6.76, -0.55) * mm, "end": v(-6.76, -0.55) * mm});
            skLineSegment(sketch, "E1916", {"start": v(-6.76, -0.55) * mm, "end": v(-6.74, -0.56) * mm});
            skLineSegment(sketch, "E1917", {"start": v(-6.74, -0.56) * mm, "end": v(-6.72, -0.56) * mm});
            skLineSegment(sketch, "E1918", {"start": v(-6.72, -0.56) * mm, "end": v(-6.7, -0.57) * mm});
            skLineSegment(sketch, "E1919", {"start": v(-6.7, -0.57) * mm, "end": v(-6.65, -0.58) * mm});
            skLineSegment(sketch, "E1920", {"start": v(-6.65, -0.58) * mm, "end": v(-6.6, -0.58) * mm});
            skLineSegment(sketch, "E1921", {"start": v(-6.6, -0.58) * mm, "end": v(-6.54, -0.6) * mm});
            skLineSegment(sketch, "E1922", {"start": v(-6.54, -0.6) * mm, "end": v(-6.46, -0.6) * mm});
            skLineSegment(sketch, "E1923", {"start": v(-6.46, -0.6) * mm, "end": v(-6.38, -0.63) * mm});
            skLineSegment(sketch, "E1924", {"start": v(-6.38, -0.63) * mm, "end": v(-6.3, -0.65) * mm});
            skLineSegment(sketch, "E1925", {"start": v(-6.3, -0.65) * mm, "end": v(-6.05, -0.7) * mm});
            skLineSegment(sketch, "E1926", {"start": v(-6.05, -0.7) * mm, "end": v(-5.84, -0.72) * mm});
            skLineSegment(sketch, "E1927", {"start": v(-5.84, -0.72) * mm, "end": v(-5.65, -0.72) * mm});
            skLineSegment(sketch, "E1928", {"start": v(-5.65, -0.72) * mm, "end": v(-5.48, -0.7) * mm});
            skLineSegment(sketch, "E1929", {"start": v(-3.49, -0.7) * mm, "end": v(-3.4, -0.68) * mm});
            skLineSegment(sketch, "E1930", {"start": v(-3.4, -0.68) * mm, "end": v(-3.32, -0.65) * mm});
            skLineSegment(sketch, "E1931", {"start": v(-3.32, -0.65) * mm, "end": v(-3.27, -0.63) * mm});
            skLineSegment(sketch, "E1932", {"start": v(-3.27, -0.63) * mm, "end": v(-3.22, -0.6) * mm});
            skLineSegment(sketch, "E1933", {"start": v(-3.22, -0.6) * mm, "end": v(-3.16, -0.58) * mm});
            skLineSegment(sketch, "E1934", {"start": v(-3.16, -0.58) * mm, "end": v(-3.1, -0.55) * mm});
            skLineSegment(sketch, "E1935", {"start": v(-3.1, -0.55) * mm, "end": v(-3, -0.51) * mm});
            skLineSegment(sketch, "E1936", {"start": v(-3, -0.51) * mm, "end": v(-2.9, -0.47) * mm});
            skLineSegment(sketch, "E1937", {"start": v(-2.9, -0.47) * mm, "end": v(-2.76, -0.42) * mm});
            skLineSegment(sketch, "E1938", {"start": v(-2.76, -0.42) * mm, "end": v(-2.57, -0.35) * mm});
            skLineSegment(sketch, "E1939", {"start": v(-2.57, -0.35) * mm, "end": v(-2.46, -0.32) * mm});
            skLineSegment(sketch, "E1940", {"start": v(-2.46, -0.32) * mm, "end": v(-2.33, -0.29) * mm});
            skLineSegment(sketch, "E1941", {"start": v(-2.33, -0.29) * mm, "end": v(-2.2, -0.26) * mm});
            skLineSegment(sketch, "E1942", {"start": v(-2.2, -0.26) * mm, "end": v(-2.07, -0.24) * mm});
            skLineSegment(sketch, "E1943", {"start": v(-2.07, -0.24) * mm, "end": v(-1.9, -0.23) * mm});
            skLineSegment(sketch, "E1944", {"start": v(-1.9, -0.23) * mm, "end": v(-1.72, -0.23) * mm});
            skLineSegment(sketch, "E1945", {"start": v(-1.72, -0.23) * mm, "end": v(-1.55, -0.24) * mm});
            skLineSegment(sketch, "E1946", {"start": v(-1.55, -0.24) * mm, "end": v(-1.4, -0.26) * mm});
            skLineSegment(sketch, "E1947", {"start": v(-1.4, -0.26) * mm, "end": v(-1.35, -0.26) * mm});
            skLineSegment(sketch, "E1948", {"start": v(-1.35, -0.26) * mm, "end": v(-1.3, -0.27) * mm});
            skLineSegment(sketch, "E1949", {"start": v(-1.3, -0.27) * mm, "end": v(-1.27, -0.27) * mm});
            skLineSegment(sketch, "E1950", {"start": v(-1.27, -0.27) * mm, "end": v(-1.26, -0.27) * mm});
            skLineSegment(sketch, "E1951", {"start": v(-1.26, -0.27) * mm, "end": v(-1.25, -0.25) * mm});
            skLineSegment(sketch, "E1952", {"start": v(-1.25, -0.25) * mm, "end": v(-1.25, -0.22) * mm});
            skLineSegment(sketch, "E1953", {"start": v(-1.25, -0.22) * mm, "end": v(-1.27, -0.17) * mm});
            skLineSegment(sketch, "E1954", {"start": v(-1.27, -0.17) * mm, "end": v(-1.29, -0.11) * mm});
            skLineSegment(sketch, "E1955", {"start": v(-1.29, -0.11) * mm, "end": v(-1.31, -0.05) * mm});
            skLineSegment(sketch, "E1956", {"start": v(-1.31, -0.05) * mm, "end": v(-1.34, 0) * mm});
            skLineSegment(sketch, "E1957", {"start": v(-1.34, 0) * mm, "end": v(-1.37, 0.05) * mm});
            skLineSegment(sketch, "E1958", {"start": v(-1.37, 0.05) * mm, "end": v(-1.4, 0.09) * mm});
            skLineSegment(sketch, "E1959", {"start": v(-1.4, 0.09) * mm, "end": v(-1.46, 0.14) * mm});
            skLineSegment(sketch, "E1960", {"start": v(-1.46, 0.14) * mm, "end": v(-1.56, 0.2) * mm});
            skLineSegment(sketch, "E1961", {"start": v(-1.56, 0.2) * mm, "end": v(-1.7, 0.25) * mm});
            skLineSegment(sketch, "E1962", {"start": v(-1.7, 0.25) * mm, "end": v(-1.89, 0.3) * mm});
            skLineSegment(sketch, "E1963", {"start": v(-1.89, 0.3) * mm, "end": v(-2.05, 0.35) * mm});
            skLineSegment(sketch, "E1964", {"start": v(-2.05, 0.35) * mm, "end": v(-2.17, 0.4) * mm});
            skLineSegment(sketch, "E1965", {"start": v(-2.17, 0.4) * mm, "end": v(-2.27, 0.42) * mm});
            skLineSegment(sketch, "E1966", {"start": v(-2.27, 0.42) * mm, "end": v(-2.36, 0.44) * mm});
            skLineSegment(sketch, "E1967", {"start": v(-2.36, 0.44) * mm, "end": v(-2.43, 0.45) * mm});
            skLineSegment(sketch, "E1968", {"start": v(-2.43, 0.45) * mm, "end": v(-2.5, 0.46) * mm});
            skLineSegment(sketch, "E1969", {"start": v(-2.5, 0.46) * mm, "end": v(-2.57, 0.46) * mm});
            skLineSegment(sketch, "E1970", {"start": v(-2.57, 0.46) * mm, "end": v(-2.65, 0.46) * mm});
            skLineSegment(sketch, "E1971", {"start": v(-2.65, 0.46) * mm, "end": v(-2.83, 0.47) * mm});
            skLineSegment(sketch, "E1972", {"start": v(-2.83, 0.47) * mm, "end": v(-2.96, 0.46) * mm});
            skLineSegment(sketch, "E1973", {"start": v(-2.96, 0.46) * mm, "end": v(-3.08, 0.44) * mm});
            skLineSegment(sketch, "E1974", {"start": v(-3.08, 0.44) * mm, "end": v(-3.2, 0.4) * mm});
            skLineSegment(sketch, "E1975", {"start": v(-3.2, 0.4) * mm, "end": v(-3.34, 0.35) * mm});
            skLineSegment(sketch, "E1976", {"start": v(-3.34, 0.35) * mm, "end": v(-3.5, 0.27) * mm});
            skLineSegment(sketch, "E1977", {"start": v(-3.5, 0.27) * mm, "end": v(-3.64, 0.19) * mm});
            skLineSegment(sketch, "E1978", {"start": v(-3.64, 0.19) * mm, "end": v(-3.77, 0.1) * mm});
            skLineSegment(sketch, "E1979", {"start": v(-3.77, 0.1) * mm, "end": v(-3.82, 0.06) * mm});
            skLineSegment(sketch, "E1980", {"start": v(-3.82, 0.06) * mm, "end": v(-3.87, 0.02) * mm});
            skLineSegment(sketch, "E1981", {"start": v(-3.87, 0.02) * mm, "end": v(-3.92, -0.03) * mm});
            skLineSegment(sketch, "E1982", {"start": v(-3.92, -0.03) * mm, "end": v(-3.98, -0.08) * mm});
            skLineSegment(sketch, "E1983", {"start": v(-3.98, -0.08) * mm, "end": v(-4.03, -0.13) * mm});
            skLineSegment(sketch, "E1984", {"start": v(-4.03, -0.13) * mm, "end": v(-4.07, -0.17) * mm});
            skLineSegment(sketch, "E1985", {"start": v(-4.07, -0.17) * mm, "end": v(-4.1, -0.2) * mm});
            skLineSegment(sketch, "E1986", {"start": v(-4.1, -0.2) * mm, "end": v(-4.12, -0.22) * mm});
            skLineSegment(sketch, "E1987", {"start": v(-4.12, -0.22) * mm, "end": v(-4.14, -0.26) * mm});
            skLineSegment(sketch, "E1988", {"start": v(-4.14, -0.26) * mm, "end": v(-4.18, -0.3) * mm});
            skLineSegment(sketch, "E1989", {"start": v(-4.18, -0.3) * mm, "end": v(-4.2, -0.33) * mm});
            skLineSegment(sketch, "E1990", {"start": v(-4.2, -0.33) * mm, "end": v(-4.22, -0.37) * mm});
            skLineSegment(sketch, "E1991", {"start": v(-4.22, -0.37) * mm, "end": v(-4.25, -0.42) * mm});
            skLineSegment(sketch, "E1992", {"start": v(-4.25, -0.42) * mm, "end": v(-4.28, -0.48) * mm});
            skLineSegment(sketch, "E1993", {"start": v(-4.28, -0.48) * mm, "end": v(-4.3, -0.53) * mm});
            skLineSegment(sketch, "E1994", {"start": v(-4.3, -0.53) * mm, "end": v(-4.33, -0.58) * mm});
            skLineSegment(sketch, "E1995", {"start": v(-4.33, -0.58) * mm, "end": v(-4.34, -0.62) * mm});
            skLineSegment(sketch, "E1996", {"start": v(-4.34, -0.62) * mm, "end": v(-4.35, -0.64) * mm});
            skLineSegment(sketch, "E1997", {"start": v(-4.35, -0.64) * mm, "end": v(-4.35, -0.66) * mm});
            skLineSegment(sketch, "E1998", {"start": v(-4.35, -0.66) * mm, "end": v(-4.34, -0.67) * mm});
            skLineSegment(sketch, "E1999", {"start": v(-4.34, -0.67) * mm, "end": v(-4.3, -0.67) * mm});
            skLineSegment(sketch, "E2000", {"start": v(-4.3, -0.67) * mm, "end": v(-4.24, -0.68) * mm});
            skLineSegment(sketch, "E2001", {"start": v(-4.24, -0.68) * mm, "end": v(-4.12, -0.69) * mm});
            skLineSegment(sketch, "E2002", {"start": v(-4.12, -0.69) * mm, "end": v(-4, -0.7) * mm});
            skLineSegment(sketch, "E2003", {"start": v(-4, -0.7) * mm, "end": v(-3.88, -0.7) * mm});
            skLineSegment(sketch, "E2004", {"start": v(-3.88, -0.7) * mm, "end": v(-3.73, -0.7) * mm});
            skLineSegment(sketch, "E2005", {"start": v(-3.73, -0.7) * mm, "end": v(-3.6, -0.7) * mm});
            skLineSegment(sketch, "E2006", {"start": v(-3.6, -0.7) * mm, "end": v(-3.49, -0.7) * mm});
            skLineSegment(sketch, "E2007", {"start": v(-0.58, -0.55) * mm, "end": v(-0.48, -0.52) * mm});
            skLineSegment(sketch, "E2008", {"start": v(-0.48, -0.52) * mm, "end": v(-0.37, -0.55) * mm});
            skLineSegment(sketch, "E2009", {"start": v(-0.37, -0.55) * mm, "end": v(-0.3, -0.57) * mm});
            skLineSegment(sketch, "E2010", {"start": v(-0.3, -0.57) * mm, "end": v(-0.26, -0.57) * mm});
            skLineSegment(sketch, "E2011", {"start": v(-0.26, -0.57) * mm, "end": v(-0.21, -0.58) * mm});
            skLineSegment(sketch, "E2012", {"start": v(-0.21, -0.58) * mm, "end": v(-0.15, -0.57) * mm});
            skLineSegment(sketch, "E2013", {"start": v(-0.15, -0.57) * mm, "end": v(-0.05, -0.56) * mm});
            skLineSegment(sketch, "E2014", {"start": v(-0.05, -0.56) * mm, "end": v(0.04, -0.53) * mm});
            skLineSegment(sketch, "E2015", {"start": v(0.04, -0.53) * mm, "end": v(0.08, -0.52) * mm});
            skLineSegment(sketch, "E2016", {"start": v(0.08, -0.52) * mm, "end": v(0.12, -0.5) * mm});
            skLineSegment(sketch, "E2017", {"start": v(0.12, -0.5) * mm, "end": v(0.15, -0.5) * mm});
            skLineSegment(sketch, "E2018", {"start": v(0.15, -0.5) * mm, "end": v(0.17, -0.49) * mm});
            skLineSegment(sketch, "E2019", {"start": v(0.17, -0.49) * mm, "end": v(0.2, -0.47) * mm});
            skLineSegment(sketch, "E2020", {"start": v(0.2, -0.47) * mm, "end": v(0.25, -0.44) * mm});
            skLineSegment(sketch, "E2021", {"start": v(0.25, -0.44) * mm, "end": v(0.29, -0.4) * mm});
            skLineSegment(sketch, "E2022", {"start": v(0.29, -0.4) * mm, "end": v(0.33, -0.34) * mm});
            skLineSegment(sketch, "E2023", {"start": v(0.33, -0.34) * mm, "end": v(0.36, -0.3) * mm});
            skLineSegment(sketch, "E2024", {"start": v(0.36, -0.3) * mm, "end": v(0.38, -0.27) * mm});
            skLineSegment(sketch, "E2025", {"start": v(0.38, -0.27) * mm, "end": v(0.4, -0.25) * mm});
            skLineSegment(sketch, "E2026", {"start": v(0.4, -0.25) * mm, "end": v(0.4, -0.23) * mm});
            skLineSegment(sketch, "E2027", {"start": v(0.4, -0.23) * mm, "end": v(0.4, -0.19) * mm});
            skLineSegment(sketch, "E2028", {"start": v(0.4, -0.19) * mm, "end": v(0.4, -0.13) * mm});
            skLineSegment(sketch, "E2029", {"start": v(0.4, -0.13) * mm, "end": v(0.39, -0.08) * mm});
            skLineSegment(sketch, "E2030", {"start": v(0.39, -0.08) * mm, "end": v(0.38, -0.02) * mm});
            skLineSegment(sketch, "E2031", {"start": v(0.38, -0.02) * mm, "end": v(0.37, 0.04) * mm});
            skLineSegment(sketch, "E2032", {"start": v(0.37, 0.04) * mm, "end": v(0.36, 0.08) * mm});
            skLineSegment(sketch, "E2033", {"start": v(0.36, 0.08) * mm, "end": v(0.35, 0.14) * mm});
            skLineSegment(sketch, "E2034", {"start": v(0.35, 0.14) * mm, "end": v(0.34, 0.2) * mm});
            skLineSegment(sketch, "E2035", {"start": v(0.34, 0.2) * mm, "end": v(0.32, 0.28) * mm});
            skLineSegment(sketch, "E2036", {"start": v(0.32, 0.28) * mm, "end": v(0.3, 0.36) * mm});
            skLineSegment(sketch, "E2037", {"start": v(0.3, 0.36) * mm, "end": v(0.3, 0.43) * mm});
            skLineSegment(sketch, "E2038", {"start": v(0.3, 0.43) * mm, "end": v(0.28, 0.49) * mm});
            skLineSegment(sketch, "E2039", {"start": v(0.28, 0.49) * mm, "end": v(0.27, 0.53) * mm});
            skLineSegment(sketch, "E2040", {"start": v(0.27, 0.53) * mm, "end": v(0.27, 0.54) * mm});
            skLineSegment(sketch, "E2041", {"start": v(0.27, 0.54) * mm, "end": v(0.26, 0.54) * mm});
            skLineSegment(sketch, "E2042", {"start": v(0.26, 0.54) * mm, "end": v(0.25, 0.53) * mm});
            skLineSegment(sketch, "E2043", {"start": v(0.25, 0.53) * mm, "end": v(0.22, 0.51) * mm});
            skLineSegment(sketch, "E2044", {"start": v(0.22, 0.51) * mm, "end": v(0.19, 0.5) * mm});
            skLineSegment(sketch, "E2045", {"start": v(0.19, 0.5) * mm, "end": v(0.05, 0.43) * mm});
            skLineSegment(sketch, "E2046", {"start": v(0.05, 0.43) * mm, "end": v(-0.11, 0.38) * mm});
            skLineSegment(sketch, "E2047", {"start": v(-0.11, 0.38) * mm, "end": v(-0.28, 0.35) * mm});
            skLineSegment(sketch, "E2048", {"start": v(-0.28, 0.35) * mm, "end": v(-0.47, 0.35) * mm});
            skLineSegment(sketch, "E2049", {"start": v(-0.47, 0.35) * mm, "end": v(-0.63, 0.36) * mm});
            skLineSegment(sketch, "E2050", {"start": v(-0.63, 0.36) * mm, "end": v(-0.77, 0.4) * mm});
            skLineSegment(sketch, "E2051", {"start": v(-0.77, 0.4) * mm, "end": v(-0.88, 0.43) * mm});
            skLineSegment(sketch, "E2052", {"start": v(-0.88, 0.43) * mm, "end": v(-0.96, 0.49) * mm});
            skLineSegment(sketch, "E2053", {"start": v(-0.96, 0.49) * mm, "end": v(-0.98, 0.5) * mm});
            skLineSegment(sketch, "E2054", {"start": v(-0.98, 0.5) * mm, "end": v(-1, 0.51) * mm});
            skLineSegment(sketch, "E2055", {"start": v(-1, 0.51) * mm, "end": v(-1, 0.5) * mm});
            skLineSegment(sketch, "E2056", {"start": v(-1, 0.5) * mm, "end": v(-1, 0.45) * mm});
            skLineSegment(sketch, "E2057", {"start": v(-1, 0.45) * mm, "end": v(-1, 0.39) * mm});
            skLineSegment(sketch, "E2058", {"start": v(-1, 0.39) * mm, "end": v(-1.02, 0.31) * mm});
            skLineSegment(sketch, "E2059", {"start": v(-1.02, 0.31) * mm, "end": v(-1.02, 0.2) * mm});
            skLineSegment(sketch, "E2060", {"start": v(-1.02, 0.2) * mm, "end": v(-1.02, 0.1) * mm});
            skLineSegment(sketch, "E2061", {"start": v(-1.02, 0.1) * mm, "end": v(-1.02, -0.04) * mm});
            skLineSegment(sketch, "E2062", {"start": v(-1.02, -0.04) * mm, "end": v(-1.02, -0.2) * mm});
            skLineSegment(sketch, "E2063", {"start": v(-1.02, -0.2) * mm, "end": v(-1, -0.5) * mm});
            skLineSegment(sketch, "E2064", {"start": v(-1, -0.5) * mm, "end": v(-0.98, -0.52) * mm});
            skLineSegment(sketch, "E2065", {"start": v(-0.98, -0.52) * mm, "end": v(-0.93, -0.55) * mm});
            skLineSegment(sketch, "E2066", {"start": v(-0.93, -0.55) * mm, "end": v(-0.85, -0.57) * mm});
            skLineSegment(sketch, "E2067", {"start": v(-0.85, -0.57) * mm, "end": v(-0.77, -0.59) * mm});
            skLineSegment(sketch, "E2068", {"start": v(-0.77, -0.59) * mm, "end": v(-0.72, -0.6) * mm});
            skLineSegment(sketch, "E2069", {"start": v(-0.72, -0.6) * mm, "end": v(-0.7, -0.59) * mm});
            skLineSegment(sketch, "E2070", {"start": v(-0.7, -0.59) * mm, "end": v(-0.66, -0.58) * mm});
            skLineSegment(sketch, "E2071", {"start": v(-0.66, -0.58) * mm, "end": v(-0.62, -0.57) * mm});
            skLineSegment(sketch, "E2072", {"start": v(-0.62, -0.57) * mm, "end": v(-0.58, -0.55) * mm});
            skLineSegment(sketch, "E2073", {"start": v(4.16, 0.23) * mm, "end": v(4.27, 0.25) * mm});
            skLineSegment(sketch, "E2074", {"start": v(4.27, 0.25) * mm, "end": v(4.34, 0.26) * mm});
            skLineSegment(sketch, "E2075", {"start": v(4.34, 0.26) * mm, "end": v(4.37, 0.28) * mm});
            skLineSegment(sketch, "E2076", {"start": v(4.37, 0.28) * mm, "end": v(4.38, 0.3) * mm});
            skLineSegment(sketch, "E2077", {"start": v(4.38, 0.3) * mm, "end": v(4.4, 0.38) * mm});
            skLineSegment(sketch, "E2078", {"start": v(4.4, 0.38) * mm, "end": v(4.4, 0.48) * mm});
            skLineSegment(sketch, "E2079", {"start": v(4.4, 0.48) * mm, "end": v(4.4, 0.57) * mm});
            skLineSegment(sketch, "E2080", {"start": v(4.4, 0.57) * mm, "end": v(4.38, 0.63) * mm});
            skLineSegment(sketch, "E2081", {"start": v(4.38, 0.63) * mm, "end": v(4.29, 0.78) * mm});
            skLineSegment(sketch, "E2082", {"start": v(4.29, 0.78) * mm, "end": v(4.14, 0.94) * mm});
            skLineSegment(sketch, "E2083", {"start": v(4.14, 0.94) * mm, "end": v(4.06, 1) * mm});
            skLineSegment(sketch, "E2084", {"start": v(4.06, 1) * mm, "end": v(4, 1.06) * mm});
            skLineSegment(sketch, "E2085", {"start": v(4, 1.06) * mm, "end": v(3.93, 1.1) * mm});
            skLineSegment(sketch, "E2086", {"start": v(3.93, 1.1) * mm, "end": v(3.88, 1.14) * mm});
            skLineSegment(sketch, "E2087", {"start": v(3.88, 1.14) * mm, "end": v(3.82, 1.17) * mm});
            skLineSegment(sketch, "E2088", {"start": v(3.82, 1.17) * mm, "end": v(3.76, 1.2) * mm});
            skLineSegment(sketch, "E2089", {"start": v(3.76, 1.2) * mm, "end": v(3.68, 1.21) * mm});
            skLineSegment(sketch, "E2090", {"start": v(3.68, 1.21) * mm, "end": v(3.6, 1.23) * mm});
            skLineSegment(sketch, "E2091", {"start": v(3.6, 1.23) * mm, "end": v(3.5, 1.25) * mm});
            skLineSegment(sketch, "E2092", {"start": v(3.5, 1.25) * mm, "end": v(3.44, 1.26) * mm});
            skLineSegment(sketch, "E2093", {"start": v(3.44, 1.26) * mm, "end": v(3.36, 1.26) * mm});
            skLineSegment(sketch, "E2094", {"start": v(3.36, 1.26) * mm, "end": v(3.25, 1.26) * mm});
            skLineSegment(sketch, "E2095", {"start": v(3.25, 1.26) * mm, "end": v(3.08, 1.25) * mm});
            skLineSegment(sketch, "E2096", {"start": v(3.08, 1.25) * mm, "end": v(2.9, 1.24) * mm});
            skLineSegment(sketch, "E2097", {"start": v(2.9, 1.24) * mm, "end": v(2.73, 1.22) * mm});
            skLineSegment(sketch, "E2098", {"start": v(2.73, 1.22) * mm, "end": v(2.6, 1.19) * mm});
            skLineSegment(sketch, "E2099", {"start": v(2.6, 1.19) * mm, "end": v(2.55, 1.18) * mm});
            skLineSegment(sketch, "E2100", {"start": v(2.55, 1.18) * mm, "end": v(2.52, 1.17) * mm});
            skLineSegment(sketch, "E2101", {"start": v(2.52, 1.17) * mm, "end": v(2.48, 1.17) * mm});
            skLineSegment(sketch, "E2102", {"start": v(2.48, 1.17) * mm, "end": v(2.46, 1.16) * mm});
            skLineSegment(sketch, "E2103", {"start": v(2.46, 1.16) * mm, "end": v(2.39, 1.14) * mm});
            skLineSegment(sketch, "E2104", {"start": v(2.39, 1.14) * mm, "end": v(2.29, 1.11) * mm});
            skLineSegment(sketch, "E2105", {"start": v(2.29, 1.11) * mm, "end": v(2.17, 1.07) * mm});
            skLineSegment(sketch, "E2106", {"start": v(2.17, 1.07) * mm, "end": v(2.03, 1.02) * mm});
            skLineSegment(sketch, "E2107", {"start": v(2.03, 1.02) * mm, "end": v(1.9, 0.97) * mm});
            skLineSegment(sketch, "E2108", {"start": v(1.9, 0.97) * mm, "end": v(1.75, 0.91) * mm});
            skLineSegment(sketch, "E2109", {"start": v(1.75, 0.91) * mm, "end": v(1.62, 0.86) * mm});
            skLineSegment(sketch, "E2110", {"start": v(1.62, 0.86) * mm, "end": v(1.5, 0.8) * mm});
            skLineSegment(sketch, "E2111", {"start": v(1.5, 0.8) * mm, "end": v(1.46, 0.79) * mm});
            skLineSegment(sketch, "E2112", {"start": v(1.46, 0.79) * mm, "end": v(1.4, 0.76) * mm});
            skLineSegment(sketch, "E2113", {"start": v(1.4, 0.76) * mm, "end": v(1.33, 0.73) * mm});
            skLineSegment(sketch, "E2114", {"start": v(1.33, 0.73) * mm, "end": v(1.27, 0.7) * mm});
            skLineSegment(sketch, "E2115", {"start": v(1.27, 0.7) * mm, "end": v(1.17, 0.67) * mm});
            skLineSegment(sketch, "E2116", {"start": v(1.17, 0.67) * mm, "end": v(1.08, 0.62) * mm});
            skLineSegment(sketch, "E2117", {"start": v(1.08, 0.62) * mm, "end": v(1.02, 0.59) * mm});
            skLineSegment(sketch, "E2118", {"start": v(1.02, 0.59) * mm, "end": v(1, 0.57) * mm});
            skLineSegment(sketch, "E2119", {"start": v(1, 0.57) * mm, "end": v(1, 0.57) * mm});
            skLineSegment(sketch, "E2120", {"start": v(1, 0.57) * mm, "end": v(1.03, 0.57) * mm});
            skLineSegment(sketch, "E2121", {"start": v(1.03, 0.57) * mm, "end": v(1.05, 0.58) * mm});
            skLineSegment(sketch, "E2122", {"start": v(1.05, 0.58) * mm, "end": v(1.08, 0.58) * mm});
            skLineSegment(sketch, "E2123", {"start": v(1.08, 0.58) * mm, "end": v(1.21, 0.6) * mm});
            skLineSegment(sketch, "E2124", {"start": v(1.21, 0.6) * mm, "end": v(1.39, 0.63) * mm});
            skLineSegment(sketch, "E2125", {"start": v(1.39, 0.63) * mm, "end": v(1.57, 0.64) * mm});
            skLineSegment(sketch, "E2126", {"start": v(1.57, 0.64) * mm, "end": v(1.73, 0.65) * mm});
            skLineSegment(sketch, "E2127", {"start": v(1.73, 0.65) * mm, "end": v(1.83, 0.65) * mm});
            skLineSegment(sketch, "E2128", {"start": v(1.83, 0.65) * mm, "end": v(1.94, 0.65) * mm});
            skLineSegment(sketch, "E2129", {"start": v(1.94, 0.65) * mm, "end": v(2.06, 0.65) * mm});
            skLineSegment(sketch, "E2130", {"start": v(2.06, 0.65) * mm, "end": v(2.2, 0.64) * mm});
            skLineSegment(sketch, "E2131", {"start": v(2.2, 0.64) * mm, "end": v(2.32, 0.63) * mm});
            skLineSegment(sketch, "E2132", {"start": v(2.32, 0.63) * mm, "end": v(2.43, 0.63) * mm});
            skLineSegment(sketch, "E2133", {"start": v(2.43, 0.63) * mm, "end": v(2.53, 0.62) * mm});
            skLineSegment(sketch, "E2134", {"start": v(2.53, 0.62) * mm, "end": v(2.6, 0.6) * mm});
            skLineSegment(sketch, "E2135", {"start": v(2.6, 0.6) * mm, "end": v(2.68, 0.59) * mm});
            skLineSegment(sketch, "E2136", {"start": v(2.68, 0.59) * mm, "end": v(2.79, 0.56) * mm});
            skLineSegment(sketch, "E2137", {"start": v(2.79, 0.56) * mm, "end": v(2.91, 0.53) * mm});
            skLineSegment(sketch, "E2138", {"start": v(2.91, 0.53) * mm, "end": v(3.05, 0.48) * mm});
            skLineSegment(sketch, "E2139", {"start": v(3.05, 0.48) * mm, "end": v(3.1, 0.47) * mm});
            skLineSegment(sketch, "E2140", {"start": v(3.1, 0.47) * mm, "end": v(3.17, 0.44) * mm});
            skLineSegment(sketch, "E2141", {"start": v(3.17, 0.44) * mm, "end": v(3.26, 0.4) * mm});
            skLineSegment(sketch, "E2142", {"start": v(3.26, 0.4) * mm, "end": v(3.35, 0.37) * mm});
            skLineSegment(sketch, "E2143", {"start": v(3.35, 0.37) * mm, "end": v(3.56, 0.29) * mm});
            skLineSegment(sketch, "E2144", {"start": v(3.56, 0.29) * mm, "end": v(3.75, 0.24) * mm});
            skLineSegment(sketch, "E2145", {"start": v(3.75, 0.24) * mm, "end": v(3.94, 0.22) * mm});
            skLineSegment(sketch, "E2146", {"start": v(3.94, 0.22) * mm, "end": v(4.16, 0.23) * mm});
            skLineSegment(sketch, "E2147", {"start": v(4.92, 0.46) * mm, "end": v(4.98, 0.5) * mm});
            skLineSegment(sketch, "E2148", {"start": v(4.98, 0.5) * mm, "end": v(5.05, 0.53) * mm});
            skLineSegment(sketch, "E2149", {"start": v(5.05, 0.53) * mm, "end": v(5.13, 0.58) * mm});
            skLineSegment(sketch, "E2150", {"start": v(5.13, 0.58) * mm, "end": v(5.21, 0.63) * mm});
            skLineSegment(sketch, "E2151", {"start": v(5.21, 0.63) * mm, "end": v(5.34, 0.72) * mm});
            skLineSegment(sketch, "E2152", {"start": v(5.34, 0.72) * mm, "end": v(5.44, 0.78) * mm});
            skLineSegment(sketch, "E2153", {"start": v(5.44, 0.78) * mm, "end": v(5.54, 0.83) * mm});
            skLineSegment(sketch, "E2154", {"start": v(5.54, 0.83) * mm, "end": v(5.63, 0.88) * mm});
            skLineSegment(sketch, "E2155", {"start": v(5.63, 0.88) * mm, "end": v(5.71, 0.92) * mm});
            skLineSegment(sketch, "E2156", {"start": v(5.71, 0.92) * mm, "end": v(5.8, 0.94) * mm});
            skLineSegment(sketch, "E2157", {"start": v(5.8, 0.94) * mm, "end": v(5.92, 0.96) * mm});
            skLineSegment(sketch, "E2158", {"start": v(5.92, 0.96) * mm, "end": v(6.1, 0.98) * mm});
            skLineSegment(sketch, "E2159", {"start": v(6.1, 0.98) * mm, "end": v(6.22, 1) * mm});
            skLineSegment(sketch, "E2160", {"start": v(6.22, 1) * mm, "end": v(6.34, 1.01) * mm});
            skLineSegment(sketch, "E2161", {"start": v(6.34, 1.01) * mm, "end": v(6.45, 1.04) * mm});
            skLineSegment(sketch, "E2162", {"start": v(6.45, 1.04) * mm, "end": v(6.5, 1.06) * mm});
            skLineSegment(sketch, "E2163", {"start": v(6.5, 1.06) * mm, "end": v(6.52, 1.07) * mm});
            skLineSegment(sketch, "E2164", {"start": v(6.52, 1.07) * mm, "end": v(6.53, 1.08) * mm});
            skLineSegment(sketch, "E2165", {"start": v(6.53, 1.08) * mm, "end": v(6.52, 1.1) * mm});
            skLineSegment(sketch, "E2166", {"start": v(6.52, 1.1) * mm, "end": v(6.5, 1.13) * mm});
            skLineSegment(sketch, "E2167", {"start": v(6.5, 1.13) * mm, "end": v(6.45, 1.16) * mm});
            skLineSegment(sketch, "E2168", {"start": v(6.45, 1.16) * mm, "end": v(6.4, 1.2) * mm});
            skLineSegment(sketch, "E2169", {"start": v(6.4, 1.2) * mm, "end": v(6.36, 1.21) * mm});
            skLineSegment(sketch, "E2170", {"start": v(6.36, 1.21) * mm, "end": v(6.32, 1.24) * mm});
            skLineSegment(sketch, "E2171", {"start": v(6.32, 1.24) * mm, "end": v(6.28, 1.26) * mm});
            skLineSegment(sketch, "E2172", {"start": v(6.28, 1.26) * mm, "end": v(6.25, 1.28) * mm});
            skLineSegment(sketch, "E2173", {"start": v(6.25, 1.28) * mm, "end": v(6.12, 1.36) * mm});
            skLineSegment(sketch, "E2174", {"start": v(6.12, 1.36) * mm, "end": v(5.93, 1.43) * mm});
            skLineSegment(sketch, "E2175", {"start": v(5.93, 1.43) * mm, "end": v(5.69, 1.5) * mm});
            skLineSegment(sketch, "E2176", {"start": v(5.69, 1.5) * mm, "end": v(5.41, 1.55) * mm});
            skLineSegment(sketch, "E2177", {"start": v(5.41, 1.55) * mm, "end": v(5.31, 1.57) * mm});
            skLineSegment(sketch, "E2178", {"start": v(5.31, 1.57) * mm, "end": v(5.23, 1.58) * mm});
            skLineSegment(sketch, "E2179", {"start": v(5.23, 1.58) * mm, "end": v(5.13, 1.58) * mm});
            skLineSegment(sketch, "E2180", {"start": v(5.13, 1.58) * mm, "end": v(5, 1.58) * mm});
            skLineSegment(sketch, "E2181", {"start": v(5, 1.58) * mm, "end": v(4.83, 1.58) * mm});
            skLineSegment(sketch, "E2182", {"start": v(4.83, 1.58) * mm, "end": v(4.68, 1.56) * mm});
            skLineSegment(sketch, "E2183", {"start": v(4.68, 1.56) * mm, "end": v(4.54, 1.54) * mm});
            skLineSegment(sketch, "E2184", {"start": v(4.54, 1.54) * mm, "end": v(4.38, 1.5) * mm});
            skLineSegment(sketch, "E2185", {"start": v(4.38, 1.5) * mm, "end": v(4.35, 1.49) * mm});
            skLineSegment(sketch, "E2186", {"start": v(4.35, 1.49) * mm, "end": v(4.31, 1.48) * mm});
            skLineSegment(sketch, "E2187", {"start": v(4.31, 1.48) * mm, "end": v(4.28, 1.47) * mm});
            skLineSegment(sketch, "E2188", {"start": v(4.28, 1.47) * mm, "end": v(4.24, 1.47) * mm});
            skLineSegment(sketch, "E2189", {"start": v(4.24, 1.47) * mm, "end": v(4.2, 1.46) * mm});
            skLineSegment(sketch, "E2190", {"start": v(4.2, 1.46) * mm, "end": v(4.13, 1.46) * mm});
            skLineSegment(sketch, "E2191", {"start": v(4.13, 1.46) * mm, "end": v(4.06, 1.46) * mm});
            skLineSegment(sketch, "E2192", {"start": v(4.06, 1.46) * mm, "end": v(3.96, 1.46) * mm});
            skLineSegment(sketch, "E2193", {"start": v(3.96, 1.46) * mm, "end": v(3.84, 1.45) * mm});
            skLineSegment(sketch, "E2194", {"start": v(3.84, 1.45) * mm, "end": v(3.74, 1.45) * mm});
            skLineSegment(sketch, "E2195", {"start": v(3.74, 1.45) * mm, "end": v(3.67, 1.45) * mm});
            skLineSegment(sketch, "E2196", {"start": v(3.67, 1.45) * mm, "end": v(3.64, 1.45) * mm});
            skLineSegment(sketch, "E2197", {"start": v(3.64, 1.45) * mm, "end": v(3.64, 1.43) * mm});
            skLineSegment(sketch, "E2198", {"start": v(3.64, 1.43) * mm, "end": v(3.66, 1.42) * mm});
            skLineSegment(sketch, "E2199", {"start": v(3.66, 1.42) * mm, "end": v(3.7, 1.4) * mm});
            skLineSegment(sketch, "E2200", {"start": v(3.7, 1.4) * mm, "end": v(3.75, 1.37) * mm});
            skLineSegment(sketch, "E2201", {"start": v(3.75, 1.37) * mm, "end": v(3.83, 1.33) * mm});
            skLineSegment(sketch, "E2202", {"start": v(3.83, 1.33) * mm, "end": v(4, 1.24) * mm});
            skLineSegment(sketch, "E2203", {"start": v(4, 1.24) * mm, "end": v(4.18, 1.14) * mm});
            skLineSegment(sketch, "E2204", {"start": v(4.18, 1.14) * mm, "end": v(4.33, 1.04) * mm});
            skLineSegment(sketch, "E2205", {"start": v(4.33, 1.04) * mm, "end": v(4.44, 0.96) * mm});
            skLineSegment(sketch, "E2206", {"start": v(4.44, 0.96) * mm, "end": v(4.54, 0.86) * mm});
            skLineSegment(sketch, "E2207", {"start": v(4.54, 0.86) * mm, "end": v(4.63, 0.73) * mm});
            skLineSegment(sketch, "E2208", {"start": v(4.63, 0.73) * mm, "end": v(4.7, 0.6) * mm});
            skLineSegment(sketch, "E2209", {"start": v(4.7, 0.6) * mm, "end": v(4.73, 0.47) * mm});
            skLineSegment(sketch, "E2210", {"start": v(4.73, 0.47) * mm, "end": v(4.74, 0.43) * mm});
            skLineSegment(sketch, "E2211", {"start": v(4.74, 0.43) * mm, "end": v(4.75, 0.4) * mm});
            skLineSegment(sketch, "E2212", {"start": v(4.75, 0.4) * mm, "end": v(4.76, 0.4) * mm});
            skLineSegment(sketch, "E2213", {"start": v(4.76, 0.4) * mm, "end": v(4.8, 0.4) * mm});
            skLineSegment(sketch, "E2214", {"start": v(4.8, 0.4) * mm, "end": v(4.85, 0.43) * mm});
            skLineSegment(sketch, "E2215", {"start": v(4.85, 0.43) * mm, "end": v(4.92, 0.46) * mm});
            skLineSegment(sketch, "E2216", {"start": v(-5.35, 0.48) * mm, "end": v(-5.35, 0.5) * mm});
            skLineSegment(sketch, "E2217", {"start": v(-5.35, 0.5) * mm, "end": v(-5.36, 0.52) * mm});
            skLineSegment(sketch, "E2218", {"start": v(-5.36, 0.52) * mm, "end": v(-5.36, 0.56) * mm});
            skLineSegment(sketch, "E2219", {"start": v(-5.36, 0.56) * mm, "end": v(-5.38, 0.6) * mm});
            skLineSegment(sketch, "E2220", {"start": v(-5.38, 0.6) * mm, "end": v(-5.39, 0.66) * mm});
            skLineSegment(sketch, "E2221", {"start": v(-5.39, 0.66) * mm, "end": v(-5.4, 0.71) * mm});
            skLineSegment(sketch, "E2222", {"start": v(-5.4, 0.71) * mm, "end": v(-5.4, 0.76) * mm});
            skLineSegment(sketch, "E2223", {"start": v(-5.4, 0.76) * mm, "end": v(-5.4, 0.79) * mm});
            skLineSegment(sketch, "E2224", {"start": v(-5.4, 0.79) * mm, "end": v(-5.4, 0.86) * mm});
            skLineSegment(sketch, "E2225", {"start": v(-5.4, 0.86) * mm, "end": v(-5.37, 0.94) * mm});
            skLineSegment(sketch, "E2226", {"start": v(-5.37, 0.94) * mm, "end": v(-5.34, 1.03) * mm});
            skLineSegment(sketch, "E2227", {"start": v(-5.34, 1.03) * mm, "end": v(-5.3, 1.1) * mm});
            skLineSegment(sketch, "E2228", {"start": v(-5.3, 1.1) * mm, "end": v(-5.28, 1.16) * mm});
            skLineSegment(sketch, "E2229", {"start": v(-5.28, 1.16) * mm, "end": v(-5.25, 1.21) * mm});
            skLineSegment(sketch, "E2230", {"start": v(-5.25, 1.21) * mm, "end": v(-5.2, 1.28) * mm});
            skLineSegment(sketch, "E2231", {"start": v(-5.2, 1.28) * mm, "end": v(-5.15, 1.35) * mm});
            skLineSegment(sketch, "E2232", {"start": v(-5.15, 1.35) * mm, "end": v(-5.09, 1.42) * mm});
            skLineSegment(sketch, "E2233", {"start": v(-5.09, 1.42) * mm, "end": v(-5.04, 1.46) * mm});
            skLineSegment(sketch, "E2234", {"start": v(-5.04, 1.46) * mm, "end": v(-5, 1.49) * mm});
            skLineSegment(sketch, "E2235", {"start": v(-5, 1.49) * mm, "end": v(-4.95, 1.52) * mm});
            skLineSegment(sketch, "E2236", {"start": v(-4.95, 1.52) * mm, "end": v(-4.9, 1.55) * mm});
            skLineSegment(sketch, "E2237", {"start": v(-4.9, 1.55) * mm, "end": v(-4.84, 1.58) * mm});
            skLineSegment(sketch, "E2238", {"start": v(-4.84, 1.58) * mm, "end": v(-4.7, 1.65) * mm});
            skLineSegment(sketch, "E2239", {"start": v(-4.7, 1.65) * mm, "end": v(-4.74, 1.66) * mm});
            skLineSegment(sketch, "E2240", {"start": v(-4.74, 1.66) * mm, "end": v(-4.82, 1.66) * mm});
            skLineSegment(sketch, "E2241", {"start": v(-4.82, 1.66) * mm, "end": v(-4.93, 1.66) * mm});
            skLineSegment(sketch, "E2242", {"start": v(-4.93, 1.66) * mm, "end": v(-5.05, 1.65) * mm});
            skLineSegment(sketch, "E2243", {"start": v(-5.05, 1.65) * mm, "end": v(-5.17, 1.64) * mm});
            skLineSegment(sketch, "E2244", {"start": v(-5.17, 1.64) * mm, "end": v(-5.28, 1.62) * mm});
            skLineSegment(sketch, "E2245", {"start": v(-5.28, 1.62) * mm, "end": v(-5.4, 1.58) * mm});
            skLineSegment(sketch, "E2246", {"start": v(-5.4, 1.58) * mm, "end": v(-5.55, 1.55) * mm});
            skLineSegment(sketch, "E2247", {"start": v(-5.55, 1.55) * mm, "end": v(-5.68, 1.52) * mm});
            skLineSegment(sketch, "E2248", {"start": v(-5.68, 1.52) * mm, "end": v(-5.78, 1.5) * mm});
            skLineSegment(sketch, "E2249", {"start": v(-5.78, 1.5) * mm, "end": v(-5.9, 1.45) * mm});
            skLineSegment(sketch, "E2250", {"start": v(-5.9, 1.45) * mm, "end": v(-6.02, 1.4) * mm});
            skLineSegment(sketch, "E2251", {"start": v(-6.02, 1.4) * mm, "end": v(-6.14, 1.35) * mm});
            skLineSegment(sketch, "E2252", {"start": v(-6.14, 1.35) * mm, "end": v(-6.22, 1.3) * mm});
            skLineSegment(sketch, "E2253", {"start": v(-6.22, 1.3) * mm, "end": v(-6.31, 1.25) * mm});
            skLineSegment(sketch, "E2254", {"start": v(-6.31, 1.25) * mm, "end": v(-6.41, 1.18) * mm});
            skLineSegment(sketch, "E2255", {"start": v(-6.41, 1.18) * mm, "end": v(-6.5, 1.12) * mm});
            skLineSegment(sketch, "E2256", {"start": v(-6.5, 1.12) * mm, "end": v(-6.54, 1.09) * mm});
            skLineSegment(sketch, "E2257", {"start": v(-6.54, 1.09) * mm, "end": v(-6.57, 1.06) * mm});
            skLineSegment(sketch, "E2258", {"start": v(-6.57, 1.06) * mm, "end": v(-6.6, 1.03) * mm});
            skLineSegment(sketch, "E2259", {"start": v(-6.6, 1.03) * mm, "end": v(-6.63, 1) * mm});
            skLineSegment(sketch, "E2260", {"start": v(-6.63, 1) * mm, "end": v(-6.73, 0.94) * mm});
            skLineSegment(sketch, "E2261", {"start": v(-6.73, 0.94) * mm, "end": v(-6.8, 0.87) * mm});
            skLineSegment(sketch, "E2262", {"start": v(-6.8, 0.87) * mm, "end": v(-6.87, 0.82) * mm});
            skLineSegment(sketch, "E2263", {"start": v(-6.87, 0.82) * mm, "end": v(-6.92, 0.78) * mm});
            skLineSegment(sketch, "E2264", {"start": v(-6.92, 0.78) * mm, "end": v(-6.95, 0.75) * mm});
            skLineSegment(sketch, "E2265", {"start": v(-6.95, 0.75) * mm, "end": v(-6.98, 0.72) * mm});
            skLineSegment(sketch, "E2266", {"start": v(-6.98, 0.72) * mm, "end": v(-7, 0.7) * mm});
            skLineSegment(sketch, "E2267", {"start": v(-7, 0.7) * mm, "end": v(-7, 0.69) * mm});
            skLineSegment(sketch, "E2268", {"start": v(-7, 0.69) * mm, "end": v(-6.98, 0.67) * mm});
            skLineSegment(sketch, "E2269", {"start": v(-6.98, 0.67) * mm, "end": v(-6.93, 0.65) * mm});
            skLineSegment(sketch, "E2270", {"start": v(-6.93, 0.65) * mm, "end": v(-6.85, 0.63) * mm});
            skLineSegment(sketch, "E2271", {"start": v(-6.85, 0.63) * mm, "end": v(-6.75, 0.6) * mm});
            skLineSegment(sketch, "E2272", {"start": v(-6.75, 0.6) * mm, "end": v(-6.49, 0.56) * mm});
            skLineSegment(sketch, "E2273", {"start": v(-6.49, 0.56) * mm, "end": v(-6.26, 0.52) * mm});
            skLineSegment(sketch, "E2274", {"start": v(-6.26, 0.52) * mm, "end": v(-6.07, 0.5) * mm});
            skLineSegment(sketch, "E2275", {"start": v(-6.07, 0.5) * mm, "end": v(-5.93, 0.47) * mm});
            skLineSegment(sketch, "E2276", {"start": v(-5.93, 0.47) * mm, "end": v(-5.89, 0.47) * mm});
            skLineSegment(sketch, "E2277", {"start": v(-5.89, 0.47) * mm, "end": v(-5.81, 0.47) * mm});
            skLineSegment(sketch, "E2278", {"start": v(-5.81, 0.47) * mm, "end": v(-5.72, 0.47) * mm});
            skLineSegment(sketch, "E2279", {"start": v(-5.72, 0.47) * mm, "end": v(-5.62, 0.47) * mm});
            skLineSegment(sketch, "E2280", {"start": v(-5.62, 0.47) * mm, "end": v(-5.52, 0.47) * mm});
            skLineSegment(sketch, "E2281", {"start": v(-5.52, 0.47) * mm, "end": v(-5.44, 0.47) * mm});
            skLineSegment(sketch, "E2282", {"start": v(-5.44, 0.47) * mm, "end": v(-5.38, 0.48) * mm});
            skLineSegment(sketch, "E2283", {"start": v(-5.38, 0.48) * mm, "end": v(-5.35, 0.48) * mm});
            skLineSegment(sketch, "E2284", {"start": v(0.84, 0.71) * mm, "end": v(0.92, 0.77) * mm});
            skLineSegment(sketch, "E2285", {"start": v(0.92, 0.77) * mm, "end": v(1.02, 0.84) * mm});
            skLineSegment(sketch, "E2286", {"start": v(1.02, 0.84) * mm, "end": v(1.13, 0.9) * mm});
            skLineSegment(sketch, "E2287", {"start": v(1.13, 0.9) * mm, "end": v(1.23, 0.95) * mm});
            skLineSegment(sketch, "E2288", {"start": v(1.23, 0.95) * mm, "end": v(1.36, 1.03) * mm});
            skLineSegment(sketch, "E2289", {"start": v(1.36, 1.03) * mm, "end": v(1.47, 1.12) * mm});
            skLineSegment(sketch, "E2290", {"start": v(1.47, 1.12) * mm, "end": v(1.57, 1.22) * mm});
            skLineSegment(sketch, "E2291", {"start": v(1.57, 1.22) * mm, "end": v(1.67, 1.36) * mm});
            skLineSegment(sketch, "E2292", {"start": v(1.67, 1.36) * mm, "end": v(1.69, 1.38) * mm});
            skLineSegment(sketch, "E2293", {"start": v(1.69, 1.38) * mm, "end": v(1.7, 1.4) * mm});
            skLineSegment(sketch, "E2294", {"start": v(1.7, 1.4) * mm, "end": v(1.73, 1.43) * mm});
            skLineSegment(sketch, "E2295", {"start": v(1.73, 1.43) * mm, "end": v(1.75, 1.45) * mm});
            skLineSegment(sketch, "E2296", {"start": v(1.75, 1.45) * mm, "end": v(1.77, 1.48) * mm});
            skLineSegment(sketch, "E2297", {"start": v(1.77, 1.48) * mm, "end": v(1.8, 1.52) * mm});
            skLineSegment(sketch, "E2298", {"start": v(1.8, 1.52) * mm, "end": v(1.82, 1.56) * mm});
            skLineSegment(sketch, "E2299", {"start": v(1.82, 1.56) * mm, "end": v(1.85, 1.6) * mm});
            skLineSegment(sketch, "E2300", {"start": v(1.85, 1.6) * mm, "end": v(1.88, 1.65) * mm});
            skLineSegment(sketch, "E2301", {"start": v(1.88, 1.65) * mm, "end": v(1.9, 1.7) * mm});
            skLineSegment(sketch, "E2302", {"start": v(1.9, 1.7) * mm, "end": v(1.94, 1.75) * mm});
            skLineSegment(sketch, "E2303", {"start": v(1.94, 1.75) * mm, "end": v(1.97, 1.78) * mm});
            skLineSegment(sketch, "E2304", {"start": v(1.97, 1.78) * mm, "end": v(2, 1.82) * mm});
            skLineSegment(sketch, "E2305", {"start": v(2, 1.82) * mm, "end": v(2.03, 1.85) * mm});
            skLineSegment(sketch, "E2306", {"start": v(2.03, 1.85) * mm, "end": v(2.06, 1.88) * mm});
            skLineSegment(sketch, "E2307", {"start": v(2.06, 1.88) * mm, "end": v(2.07, 1.9) * mm});
            skLineSegment(sketch, "E2308", {"start": v(2.07, 1.9) * mm, "end": v(2.11, 1.94) * mm});
            skLineSegment(sketch, "E2309", {"start": v(2.11, 1.94) * mm, "end": v(2.18, 2) * mm});
            skLineSegment(sketch, "E2310", {"start": v(2.18, 2) * mm, "end": v(2.26, 2.06) * mm});
            skLineSegment(sketch, "E2311", {"start": v(2.26, 2.06) * mm, "end": v(2.35, 2.13) * mm});
            skLineSegment(sketch, "E2312", {"start": v(2.35, 2.13) * mm, "end": v(2.44, 2.2) * mm});
            skLineSegment(sketch, "E2313", {"start": v(2.44, 2.2) * mm, "end": v(2.53, 2.26) * mm});
            skLineSegment(sketch, "E2314", {"start": v(2.53, 2.26) * mm, "end": v(2.62, 2.32) * mm});
            skLineSegment(sketch, "E2315", {"start": v(2.62, 2.32) * mm, "end": v(2.68, 2.35) * mm});
            skLineSegment(sketch, "E2316", {"start": v(2.68, 2.35) * mm, "end": v(2.73, 2.38) * mm});
            skLineSegment(sketch, "E2317", {"start": v(2.73, 2.38) * mm, "end": v(2.8, 2.4) * mm});
            skLineSegment(sketch, "E2318", {"start": v(2.8, 2.4) * mm, "end": v(2.85, 2.43) * mm});
            skLineSegment(sketch, "E2319", {"start": v(2.85, 2.43) * mm, "end": v(2.9, 2.46) * mm});
            skLineSegment(sketch, "E2320", {"start": v(2.9, 2.46) * mm, "end": v(2.95, 2.48) * mm});
            skLineSegment(sketch, "E2321", {"start": v(2.95, 2.48) * mm, "end": v(3, 2.5) * mm});
            skLineSegment(sketch, "E2322", {"start": v(3, 2.5) * mm, "end": v(3.04, 2.52) * mm});
            skLineSegment(sketch, "E2323", {"start": v(3.04, 2.52) * mm, "end": v(3.07, 2.53) * mm});
            skLineSegment(sketch, "E2324", {"start": v(3.07, 2.53) * mm, "end": v(3.1, 2.55) * mm});
            skLineSegment(sketch, "E2325", {"start": v(3.1, 2.55) * mm, "end": v(3.1, 2.55) * mm});
            skLineSegment(sketch, "E2326", {"start": v(3.1, 2.55) * mm, "end": v(3.1, 2.56) * mm});
            skLineSegment(sketch, "E2327", {"start": v(3.1, 2.56) * mm, "end": v(3.1, 2.56) * mm});
            skLineSegment(sketch, "E2328", {"start": v(3.1, 2.56) * mm, "end": v(3.08, 2.57) * mm});
            skLineSegment(sketch, "E2329", {"start": v(3.08, 2.57) * mm, "end": v(3.05, 2.56) * mm});
            skLineSegment(sketch, "E2330", {"start": v(3.05, 2.56) * mm, "end": v(3.01, 2.56) * mm});
            skLineSegment(sketch, "E2331", {"start": v(3.01, 2.56) * mm, "end": v(2.96, 2.56) * mm});
            skLineSegment(sketch, "E2332", {"start": v(2.96, 2.56) * mm, "end": v(2.85, 2.54) * mm});
            skLineSegment(sketch, "E2333", {"start": v(2.85, 2.54) * mm, "end": v(2.74, 2.53) * mm});
            skLineSegment(sketch, "E2334", {"start": v(2.74, 2.53) * mm, "end": v(2.62, 2.5) * mm});
            skLineSegment(sketch, "E2335", {"start": v(2.62, 2.5) * mm, "end": v(2.48, 2.47) * mm});
            skLineSegment(sketch, "E2336", {"start": v(2.48, 2.47) * mm, "end": v(2.32, 2.43) * mm});
            skLineSegment(sketch, "E2337", {"start": v(2.32, 2.43) * mm, "end": v(2.18, 2.39) * mm});
            skLineSegment(sketch, "E2338", {"start": v(2.18, 2.39) * mm, "end": v(2.05, 2.33) * mm});
            skLineSegment(sketch, "E2339", {"start": v(2.05, 2.33) * mm, "end": v(1.9, 2.26) * mm});
            skLineSegment(sketch, "E2340", {"start": v(1.9, 2.26) * mm, "end": v(1.84, 2.23) * mm});
            skLineSegment(sketch, "E2341", {"start": v(1.84, 2.23) * mm, "end": v(1.78, 2.2) * mm});
            skLineSegment(sketch, "E2342", {"start": v(1.78, 2.2) * mm, "end": v(1.72, 2.16) * mm});
            skLineSegment(sketch, "E2343", {"start": v(1.72, 2.16) * mm, "end": v(1.66, 2.12) * mm});
            skLineSegment(sketch, "E2344", {"start": v(1.66, 2.12) * mm, "end": v(1.59, 2.07) * mm});
            skLineSegment(sketch, "E2345", {"start": v(1.59, 2.07) * mm, "end": v(1.5, 2) * mm});
            skLineSegment(sketch, "E2346", {"start": v(1.5, 2) * mm, "end": v(1.37, 1.9) * mm});
            skLineSegment(sketch, "E2347", {"start": v(1.37, 1.9) * mm, "end": v(1.2, 1.78) * mm});
            skLineSegment(sketch, "E2348", {"start": v(1.2, 1.78) * mm, "end": v(1.13, 1.71) * mm});
            skLineSegment(sketch, "E2349", {"start": v(1.13, 1.71) * mm, "end": v(1.04, 1.63) * mm});
            skLineSegment(sketch, "E2350", {"start": v(1.04, 1.63) * mm, "end": v(0.95, 1.54) * mm});
            skLineSegment(sketch, "E2351", {"start": v(0.95, 1.54) * mm, "end": v(0.86, 1.45) * mm});
            skLineSegment(sketch, "E2352", {"start": v(0.86, 1.45) * mm, "end": v(0.78, 1.35) * mm});
            skLineSegment(sketch, "E2353", {"start": v(0.78, 1.35) * mm, "end": v(0.7, 1.25) * mm});
            skLineSegment(sketch, "E2354", {"start": v(0.7, 1.25) * mm, "end": v(0.63, 1.16) * mm});
            skLineSegment(sketch, "E2355", {"start": v(0.63, 1.16) * mm, "end": v(0.58, 1.08) * mm});
            skLineSegment(sketch, "E2356", {"start": v(0.58, 1.08) * mm, "end": v(0.56, 1.04) * mm});
            skLineSegment(sketch, "E2357", {"start": v(0.56, 1.04) * mm, "end": v(0.54, 1) * mm});
            skLineSegment(sketch, "E2358", {"start": v(0.54, 1) * mm, "end": v(0.53, 0.98) * mm});
            skLineSegment(sketch, "E2359", {"start": v(0.53, 0.98) * mm, "end": v(0.53, 0.96) * mm});
            skLineSegment(sketch, "E2360", {"start": v(0.53, 0.96) * mm, "end": v(0.53, 0.92) * mm});
            skLineSegment(sketch, "E2361", {"start": v(0.53, 0.92) * mm, "end": v(0.53, 0.86) * mm});
            skLineSegment(sketch, "E2362", {"start": v(0.53, 0.86) * mm, "end": v(0.54, 0.8) * mm});
            skLineSegment(sketch, "E2363", {"start": v(0.54, 0.8) * mm, "end": v(0.55, 0.7) * mm});
            skLineSegment(sketch, "E2364", {"start": v(0.55, 0.7) * mm, "end": v(0.55, 0.63) * mm});
            skLineSegment(sketch, "E2365", {"start": v(0.55, 0.63) * mm, "end": v(0.56, 0.56) * mm});
            skLineSegment(sketch, "E2366", {"start": v(0.56, 0.56) * mm, "end": v(0.57, 0.51) * mm});
            skLineSegment(sketch, "E2367", {"start": v(0.57, 0.51) * mm, "end": v(0.57, 0.49) * mm});
            skLineSegment(sketch, "E2368", {"start": v(0.57, 0.49) * mm, "end": v(0.58, 0.49) * mm});
            skLineSegment(sketch, "E2369", {"start": v(0.58, 0.49) * mm, "end": v(0.6, 0.5) * mm});
            skLineSegment(sketch, "E2370", {"start": v(0.6, 0.5) * mm, "end": v(0.63, 0.52) * mm});
            skLineSegment(sketch, "E2371", {"start": v(0.63, 0.52) * mm, "end": v(0.67, 0.57) * mm});
            skLineSegment(sketch, "E2372", {"start": v(0.67, 0.57) * mm, "end": v(0.72, 0.6) * mm});
            skLineSegment(sketch, "E2373", {"start": v(0.72, 0.6) * mm, "end": v(0.76, 0.65) * mm});
            skLineSegment(sketch, "E2374", {"start": v(0.76, 0.65) * mm, "end": v(0.8, 0.69) * mm});
            skLineSegment(sketch, "E2375", {"start": v(0.8, 0.69) * mm, "end": v(0.84, 0.71) * mm});
            skLineSegment(sketch, "E2376", {"start": v(-5.07, 0.52) * mm, "end": v(-4.93, 0.56) * mm});
            skLineSegment(sketch, "E2377", {"start": v(-4.93, 0.56) * mm, "end": v(-4.77, 0.61) * mm});
            skLineSegment(sketch, "E2378", {"start": v(-4.77, 0.61) * mm, "end": v(-4.61, 0.67) * mm});
            skLineSegment(sketch, "E2379", {"start": v(-4.61, 0.67) * mm, "end": v(-4.5, 0.71) * mm});
            skLineSegment(sketch, "E2380", {"start": v(-4.5, 0.71) * mm, "end": v(-4.4, 0.75) * mm});
            skLineSegment(sketch, "E2381", {"start": v(-4.4, 0.75) * mm, "end": v(-4.28, 0.79) * mm});
            skLineSegment(sketch, "E2382", {"start": v(-4.28, 0.79) * mm, "end": v(-4.22, 0.8) * mm});
            skLineSegment(sketch, "E2383", {"start": v(-4.22, 0.8) * mm, "end": v(-4.17, 0.82) * mm});
            skLineSegment(sketch, "E2384", {"start": v(-4.17, 0.82) * mm, "end": v(-4.13, 0.83) * mm});
            skLineSegment(sketch, "E2385", {"start": v(-4.13, 0.83) * mm, "end": v(-4.1, 0.84) * mm});
            skLineSegment(sketch, "E2386", {"start": v(-4.1, 0.84) * mm, "end": v(-4, 0.86) * mm});
            skLineSegment(sketch, "E2387", {"start": v(-4, 0.86) * mm, "end": v(-3.86, 0.88) * mm});
            skLineSegment(sketch, "E2388", {"start": v(-3.86, 0.88) * mm, "end": v(-3.69, 0.9) * mm});
            skLineSegment(sketch, "E2389", {"start": v(-3.69, 0.9) * mm, "end": v(-3.48, 0.9) * mm});
            skLineSegment(sketch, "E2390", {"start": v(-3.48, 0.9) * mm, "end": v(-3.16, 0.9) * mm});
            skLineSegment(sketch, "E2391", {"start": v(-3.16, 0.9) * mm, "end": v(-2.87, 0.9) * mm});
            skLineSegment(sketch, "E2392", {"start": v(-2.87, 0.9) * mm, "end": v(-2.62, 0.87) * mm});
            skLineSegment(sketch, "E2393", {"start": v(-2.62, 0.87) * mm, "end": v(-2.43, 0.83) * mm});
            skLineSegment(sketch, "E2394", {"start": v(-2.43, 0.83) * mm, "end": v(-2.38, 0.82) * mm});
            skLineSegment(sketch, "E2395", {"start": v(-2.38, 0.82) * mm, "end": v(-2.33, 0.8) * mm});
            skLineSegment(sketch, "E2396", {"start": v(-2.33, 0.8) * mm, "end": v(-2.27, 0.8) * mm});
            skLineSegment(sketch, "E2397", {"start": v(-2.27, 0.8) * mm, "end": v(-2.22, 0.78) * mm});
            skLineSegment(sketch, "E2398", {"start": v(-2.22, 0.78) * mm, "end": v(-2.17, 0.78) * mm});
            skLineSegment(sketch, "E2399", {"start": v(-2.17, 0.78) * mm, "end": v(-2.12, 0.77) * mm});
            skLineSegment(sketch, "E2400", {"start": v(-2.12, 0.77) * mm, "end": v(-2.07, 0.76) * mm});
            skLineSegment(sketch, "E2401", {"start": v(-2.07, 0.76) * mm, "end": v(-2.04, 0.75) * mm});
            skLineSegment(sketch, "E2402", {"start": v(-2.04, 0.75) * mm, "end": v(-1.98, 0.74) * mm});
            skLineSegment(sketch, "E2403", {"start": v(-1.98, 0.74) * mm, "end": v(-1.95, 0.73) * mm});
            skLineSegment(sketch, "E2404", {"start": v(-1.95, 0.73) * mm, "end": v(-1.94, 0.74) * mm});
            skLineSegment(sketch, "E2405", {"start": v(-1.94, 0.74) * mm, "end": v(-1.94, 0.74) * mm});
            skLineSegment(sketch, "E2406", {"start": v(-1.94, 0.74) * mm, "end": v(-1.95, 0.76) * mm});
            skLineSegment(sketch, "E2407", {"start": v(-1.95, 0.76) * mm, "end": v(-1.97, 0.78) * mm});
            skLineSegment(sketch, "E2408", {"start": v(-1.97, 0.78) * mm, "end": v(-2.02, 0.82) * mm});
            skLineSegment(sketch, "E2409", {"start": v(-2.02, 0.82) * mm, "end": v(-2.07, 0.86) * mm});
            skLineSegment(sketch, "E2410", {"start": v(-2.07, 0.86) * mm, "end": v(-2.14, 0.91) * mm});
            skLineSegment(sketch, "E2411", {"start": v(-2.14, 0.91) * mm, "end": v(-2.2, 0.97) * mm});
            skLineSegment(sketch, "E2412", {"start": v(-2.2, 0.97) * mm, "end": v(-2.29, 1.03) * mm});
            skLineSegment(sketch, "E2413", {"start": v(-2.29, 1.03) * mm, "end": v(-2.37, 1.1) * mm});
            skLineSegment(sketch, "E2414", {"start": v(-2.37, 1.1) * mm, "end": v(-2.47, 1.16) * mm});
            skLineSegment(sketch, "E2415", {"start": v(-2.47, 1.16) * mm, "end": v(-2.59, 1.23) * mm});
            skLineSegment(sketch, "E2416", {"start": v(-2.59, 1.23) * mm, "end": v(-2.71, 1.3) * mm});
            skLineSegment(sketch, "E2417", {"start": v(-2.71, 1.3) * mm, "end": v(-2.83, 1.35) * mm});
            skLineSegment(sketch, "E2418", {"start": v(-2.83, 1.35) * mm, "end": v(-3.08, 1.43) * mm});
            skLineSegment(sketch, "E2419", {"start": v(-3.08, 1.43) * mm, "end": v(-3.34, 1.5) * mm});
            skLineSegment(sketch, "E2420", {"start": v(-3.34, 1.5) * mm, "end": v(-3.6, 1.55) * mm});
            skLineSegment(sketch, "E2421", {"start": v(-3.6, 1.55) * mm, "end": v(-3.85, 1.58) * mm});
            skLineSegment(sketch, "E2422", {"start": v(-3.85, 1.58) * mm, "end": v(-4.1, 1.58) * mm});
            skLineSegment(sketch, "E2423", {"start": v(-4.1, 1.58) * mm, "end": v(-4.35, 1.56) * mm});
            skLineSegment(sketch, "E2424", {"start": v(-4.35, 1.56) * mm, "end": v(-4.58, 1.5) * mm});
            skLineSegment(sketch, "E2425", {"start": v(-4.58, 1.5) * mm, "end": v(-4.8, 1.41) * mm});
            skLineSegment(sketch, "E2426", {"start": v(-4.8, 1.41) * mm, "end": v(-4.87, 1.36) * mm});
            skLineSegment(sketch, "E2427", {"start": v(-4.87, 1.36) * mm, "end": v(-4.96, 1.3) * mm});
            skLineSegment(sketch, "E2428", {"start": v(-4.96, 1.3) * mm, "end": v(-5.04, 1.24) * mm});
            skLineSegment(sketch, "E2429", {"start": v(-5.04, 1.24) * mm, "end": v(-5.08, 1.18) * mm});
            skLineSegment(sketch, "E2430", {"start": v(-5.08, 1.18) * mm, "end": v(-5.12, 1.12) * mm});
            skLineSegment(sketch, "E2431", {"start": v(-5.12, 1.12) * mm, "end": v(-5.15, 1.03) * mm});
            skLineSegment(sketch, "E2432", {"start": v(-5.15, 1.03) * mm, "end": v(-5.19, 0.94) * mm});
            skLineSegment(sketch, "E2433", {"start": v(-5.19, 0.94) * mm, "end": v(-5.2, 0.85) * mm});
            skLineSegment(sketch, "E2434", {"start": v(-5.2, 0.85) * mm, "end": v(-5.22, 0.75) * mm});
            skLineSegment(sketch, "E2435", {"start": v(-5.22, 0.75) * mm, "end": v(-5.23, 0.65) * mm});
            skLineSegment(sketch, "E2436", {"start": v(-5.23, 0.65) * mm, "end": v(-5.22, 0.57) * mm});
            skLineSegment(sketch, "E2437", {"start": v(-5.22, 0.57) * mm, "end": v(-5.2, 0.52) * mm});
            skLineSegment(sketch, "E2438", {"start": v(-5.2, 0.52) * mm, "end": v(-5.18, 0.5) * mm});
            skLineSegment(sketch, "E2439", {"start": v(-5.18, 0.5) * mm, "end": v(-5.17, 0.5) * mm});
            skLineSegment(sketch, "E2440", {"start": v(-5.17, 0.5) * mm, "end": v(-5.13, 0.5) * mm});
            skLineSegment(sketch, "E2441", {"start": v(-5.13, 0.5) * mm, "end": v(-5.07, 0.52) * mm});
            skLineSegment(sketch, "E2442", {"start": v(-0.18, 0.62) * mm, "end": v(-0.14, 0.63) * mm});
            skLineSegment(sketch, "E2443", {"start": v(-0.14, 0.63) * mm, "end": v(-0.1, 0.64) * mm});
            skLineSegment(sketch, "E2444", {"start": v(-0.1, 0.64) * mm, "end": v(-0.05, 0.65) * mm});
            skLineSegment(sketch, "E2445", {"start": v(-0.05, 0.65) * mm, "end": v(-0.01, 0.66) * mm});
            skLineSegment(sketch, "E2446", {"start": v(-0.01, 0.66) * mm, "end": v(0.06, 0.7) * mm});
            skLineSegment(sketch, "E2447", {"start": v(0.06, 0.7) * mm, "end": v(0.14, 0.73) * mm});
            skLineSegment(sketch, "E2448", {"start": v(0.14, 0.73) * mm, "end": v(0.2, 0.76) * mm});
            skLineSegment(sketch, "E2449", {"start": v(0.2, 0.76) * mm, "end": v(0.22, 0.78) * mm});
            skLineSegment(sketch, "E2450", {"start": v(0.22, 0.78) * mm, "end": v(0.2, 0.83) * mm});
            skLineSegment(sketch, "E2451", {"start": v(0.2, 0.83) * mm, "end": v(0.18, 0.92) * mm});
            skLineSegment(sketch, "E2452", {"start": v(0.18, 0.92) * mm, "end": v(0.15, 1.02) * mm});
            skLineSegment(sketch, "E2453", {"start": v(0.15, 1.02) * mm, "end": v(0.13, 1.1) * mm});
            skLineSegment(sketch, "E2454", {"start": v(0.13, 1.1) * mm, "end": v(0.07, 1.26) * mm});
            skLineSegment(sketch, "E2455", {"start": v(0.07, 1.26) * mm, "end": v(0.02, 1.36) * mm});
            skLineSegment(sketch, "E2456", {"start": v(0.02, 1.36) * mm, "end": v(0, 1.4) * mm});
            skLineSegment(sketch, "E2457", {"start": v(0, 1.4) * mm, "end": v(-0.03, 1.42) * mm});
            skLineSegment(sketch, "E2458", {"start": v(-0.03, 1.42) * mm, "end": v(-0.09, 1.4) * mm});
            skLineSegment(sketch, "E2459", {"start": v(-0.09, 1.4) * mm, "end": v(-0.17, 1.4) * mm});
            skLineSegment(sketch, "E2460", {"start": v(-0.17, 1.4) * mm, "end": v(-0.25, 1.38) * mm});
            skLineSegment(sketch, "E2461", {"start": v(-0.25, 1.38) * mm, "end": v(-0.32, 1.38) * mm});
            skLineSegment(sketch, "E2462", {"start": v(-0.32, 1.38) * mm, "end": v(-0.49, 1.4) * mm});
            skLineSegment(sketch, "E2463", {"start": v(-0.49, 1.4) * mm, "end": v(-0.7, 1.44) * mm});
            skLineSegment(sketch, "E2464", {"start": v(-0.7, 1.44) * mm, "end": v(-0.73, 1.45) * mm});
            skLineSegment(sketch, "E2465", {"start": v(-0.73, 1.45) * mm, "end": v(-0.76, 1.46) * mm});
            skLineSegment(sketch, "E2466", {"start": v(-0.76, 1.46) * mm, "end": v(-0.79, 1.47) * mm});
            skLineSegment(sketch, "E2467", {"start": v(-0.79, 1.47) * mm, "end": v(-0.8, 1.47) * mm});
            skLineSegment(sketch, "E2468", {"start": v(-0.8, 1.47) * mm, "end": v(-0.81, 1.44) * mm});
            skLineSegment(sketch, "E2469", {"start": v(-0.81, 1.44) * mm, "end": v(-0.83, 1.38) * mm});
            skLineSegment(sketch, "E2470", {"start": v(-0.83, 1.38) * mm, "end": v(-0.85, 1.3) * mm});
            skLineSegment(sketch, "E2471", {"start": v(-0.85, 1.3) * mm, "end": v(-0.87, 1.22) * mm});
            skLineSegment(sketch, "E2472", {"start": v(-0.87, 1.22) * mm, "end": v(-0.9, 1.13) * mm});
            skLineSegment(sketch, "E2473", {"start": v(-0.9, 1.13) * mm, "end": v(-0.92, 1.04) * mm});
            skLineSegment(sketch, "E2474", {"start": v(-0.92, 1.04) * mm, "end": v(-0.94, 0.95) * mm});
            skLineSegment(sketch, "E2475", {"start": v(-0.94, 0.95) * mm, "end": v(-0.95, 0.88) * mm});
            skLineSegment(sketch, "E2476", {"start": v(-0.95, 0.88) * mm, "end": v(-0.96, 0.85) * mm});
            skLineSegment(sketch, "E2477", {"start": v(-0.96, 0.85) * mm, "end": v(-0.96, 0.82) * mm});
            skLineSegment(sketch, "E2478", {"start": v(-0.96, 0.82) * mm, "end": v(-0.96, 0.8) * mm});
            skLineSegment(sketch, "E2479", {"start": v(-0.96, 0.8) * mm, "end": v(-0.95, 0.78) * mm});
            skLineSegment(sketch, "E2480", {"start": v(-0.95, 0.78) * mm, "end": v(-0.94, 0.77) * mm});
            skLineSegment(sketch, "E2481", {"start": v(-0.94, 0.77) * mm, "end": v(-0.92, 0.76) * mm});
            skLineSegment(sketch, "E2482", {"start": v(-0.92, 0.76) * mm, "end": v(-0.88, 0.74) * mm});
            skLineSegment(sketch, "E2483", {"start": v(-0.88, 0.74) * mm, "end": v(-0.84, 0.72) * mm});
            skLineSegment(sketch, "E2484", {"start": v(-0.84, 0.72) * mm, "end": v(-0.68, 0.66) * mm});
            skLineSegment(sketch, "E2485", {"start": v(-0.68, 0.66) * mm, "end": v(-0.51, 0.63) * mm});
            skLineSegment(sketch, "E2486", {"start": v(-0.51, 0.63) * mm, "end": v(-0.34, 0.61) * mm});
            skLineSegment(sketch, "E2487", {"start": v(-0.34, 0.61) * mm, "end": v(-0.18, 0.62) * mm});
            skLineSegment(sketch, "E2488", {"start": v(-7.02, 0.93) * mm, "end": v(-6.9, 1.04) * mm});
            skLineSegment(sketch, "E2489", {"start": v(-6.9, 1.04) * mm, "end": v(-6.79, 1.14) * mm});
            skLineSegment(sketch, "E2490", {"start": v(-6.79, 1.14) * mm, "end": v(-6.7, 1.22) * mm});
            skLineSegment(sketch, "E2491", {"start": v(-6.7, 1.22) * mm, "end": v(-6.63, 1.27) * mm});
            skLineSegment(sketch, "E2492", {"start": v(-6.63, 1.27) * mm, "end": v(-6.6, 1.28) * mm});
            skLineSegment(sketch, "E2493", {"start": v(-6.6, 1.28) * mm, "end": v(-6.56, 1.31) * mm});
            skLineSegment(sketch, "E2494", {"start": v(-6.56, 1.31) * mm, "end": v(-6.5, 1.35) * mm});
            skLineSegment(sketch, "E2495", {"start": v(-6.5, 1.35) * mm, "end": v(-6.43, 1.38) * mm});
            skLineSegment(sketch, "E2496", {"start": v(-6.43, 1.38) * mm, "end": v(-6.39, 1.41) * mm});
            skLineSegment(sketch, "E2497", {"start": v(-6.39, 1.41) * mm, "end": v(-6.35, 1.43) * mm});
            skLineSegment(sketch, "E2498", {"start": v(-6.35, 1.43) * mm, "end": v(-6.32, 1.45) * mm});
            skLineSegment(sketch, "E2499", {"start": v(-6.32, 1.45) * mm, "end": v(-6.3, 1.46) * mm});
            skLineSegment(sketch, "E2500", {"start": v(-6.3, 1.46) * mm, "end": v(-6.3, 1.47) * mm});
            skLineSegment(sketch, "E2501", {"start": v(-6.3, 1.47) * mm, "end": v(-6.3, 1.47) * mm});
            skLineSegment(sketch, "E2502", {"start": v(-6.3, 1.47) * mm, "end": v(-6.3, 1.48) * mm});
            skLineSegment(sketch, "E2503", {"start": v(-6.3, 1.48) * mm, "end": v(-6.3, 1.48) * mm});
            skLineSegment(sketch, "E2504", {"start": v(-6.3, 1.48) * mm, "end": v(-6.33, 1.49) * mm});
            skLineSegment(sketch, "E2505", {"start": v(-6.33, 1.49) * mm, "end": v(-6.4, 1.49) * mm});
            skLineSegment(sketch, "E2506", {"start": v(-6.4, 1.49) * mm, "end": v(-6.47, 1.5) * mm});
            skLineSegment(sketch, "E2507", {"start": v(-6.47, 1.5) * mm, "end": v(-6.56, 1.5) * mm});
            skLineSegment(sketch, "E2508", {"start": v(-6.56, 1.5) * mm, "end": v(-6.65, 1.49) * mm});
            skLineSegment(sketch, "E2509", {"start": v(-6.65, 1.49) * mm, "end": v(-6.75, 1.49) * mm});
            skLineSegment(sketch, "E2510", {"start": v(-6.75, 1.49) * mm, "end": v(-6.83, 1.48) * mm});
            skLineSegment(sketch, "E2511", {"start": v(-6.83, 1.48) * mm, "end": v(-6.9, 1.48) * mm});
            skLineSegment(sketch, "E2512", {"start": v(-6.9, 1.48) * mm, "end": v(-7.04, 1.46) * mm});
            skLineSegment(sketch, "E2513", {"start": v(-7.04, 1.46) * mm, "end": v(-7.17, 1.44) * mm});
            skLineSegment(sketch, "E2514", {"start": v(-7.17, 1.44) * mm, "end": v(-7.27, 1.42) * mm});
            skLineSegment(sketch, "E2515", {"start": v(-7.27, 1.42) * mm, "end": v(-7.34, 1.4) * mm});
            skLineSegment(sketch, "E2516", {"start": v(-7.34, 1.4) * mm, "end": v(-7.36, 1.4) * mm});
            skLineSegment(sketch, "E2517", {"start": v(-7.36, 1.4) * mm, "end": v(-7.41, 1.38) * mm});
            skLineSegment(sketch, "E2518", {"start": v(-7.41, 1.38) * mm, "end": v(-7.47, 1.37) * mm});
            skLineSegment(sketch, "E2519", {"start": v(-7.47, 1.37) * mm, "end": v(-7.54, 1.36) * mm});
            skLineSegment(sketch, "E2520", {"start": v(-7.54, 1.36) * mm, "end": v(-7.68, 1.33) * mm});
            skLineSegment(sketch, "E2521", {"start": v(-7.68, 1.33) * mm, "end": v(-7.81, 1.3) * mm});
            skLineSegment(sketch, "E2522", {"start": v(-7.81, 1.3) * mm, "end": v(-7.91, 1.27) * mm});
            skLineSegment(sketch, "E2523", {"start": v(-7.91, 1.27) * mm, "end": v(-7.95, 1.25) * mm});
            skLineSegment(sketch, "E2524", {"start": v(-7.95, 1.25) * mm, "end": v(-7.94, 1.24) * mm});
            skLineSegment(sketch, "E2525", {"start": v(-7.94, 1.24) * mm, "end": v(-7.93, 1.23) * mm});
            skLineSegment(sketch, "E2526", {"start": v(-7.93, 1.23) * mm, "end": v(-7.91, 1.22) * mm});
            skLineSegment(sketch, "E2527", {"start": v(-7.91, 1.22) * mm, "end": v(-7.89, 1.2) * mm});
            skLineSegment(sketch, "E2528", {"start": v(-7.89, 1.2) * mm, "end": v(-7.86, 1.18) * mm});
            skLineSegment(sketch, "E2529", {"start": v(-7.86, 1.18) * mm, "end": v(-7.82, 1.15) * mm});
            skLineSegment(sketch, "E2530", {"start": v(-7.82, 1.15) * mm, "end": v(-7.78, 1.12) * mm});
            skLineSegment(sketch, "E2531", {"start": v(-7.78, 1.12) * mm, "end": v(-7.75, 1.08) * mm});
            skLineSegment(sketch, "E2532", {"start": v(-7.75, 1.08) * mm, "end": v(-7.68, 1.03) * mm});
            skLineSegment(sketch, "E2533", {"start": v(-7.68, 1.03) * mm, "end": v(-7.61, 0.97) * mm});
            skLineSegment(sketch, "E2534", {"start": v(-7.61, 0.97) * mm, "end": v(-7.54, 0.92) * mm});
            skLineSegment(sketch, "E2535", {"start": v(-7.54, 0.92) * mm, "end": v(-7.46, 0.87) * mm});
            skLineSegment(sketch, "E2536", {"start": v(-7.46, 0.87) * mm, "end": v(-7.39, 0.83) * mm});
            skLineSegment(sketch, "E2537", {"start": v(-7.39, 0.83) * mm, "end": v(-7.32, 0.8) * mm});
            skLineSegment(sketch, "E2538", {"start": v(-7.32, 0.8) * mm, "end": v(-7.26, 0.78) * mm});
            skLineSegment(sketch, "E2539", {"start": v(-7.26, 0.78) * mm, "end": v(-7.22, 0.77) * mm});
            skLineSegment(sketch, "E2540", {"start": v(-7.22, 0.77) * mm, "end": v(-7.21, 0.77) * mm});
            skLineSegment(sketch, "E2541", {"start": v(-7.21, 0.77) * mm, "end": v(-7.2, 0.77) * mm});
            skLineSegment(sketch, "E2542", {"start": v(-7.2, 0.77) * mm, "end": v(-7.18, 0.78) * mm});
            skLineSegment(sketch, "E2543", {"start": v(-7.18, 0.78) * mm, "end": v(-7.16, 0.8) * mm});
            skLineSegment(sketch, "E2544", {"start": v(-7.16, 0.8) * mm, "end": v(-7.14, 0.82) * mm});
            skLineSegment(sketch, "E2545", {"start": v(-7.14, 0.82) * mm, "end": v(-7.1, 0.85) * mm});
            skLineSegment(sketch, "E2546", {"start": v(-7.1, 0.85) * mm, "end": v(-7.07, 0.88) * mm});
            skLineSegment(sketch, "E2547", {"start": v(-7.07, 0.88) * mm, "end": v(-7.02, 0.93) * mm});
            skLineSegment(sketch, "E2548", {"start": v(-1.18, 0.93) * mm, "end": v(-1.2, 0.97) * mm});
            skLineSegment(sketch, "E2549", {"start": v(-1.2, 0.97) * mm, "end": v(-1.22, 1.01) * mm});
            skLineSegment(sketch, "E2550", {"start": v(-1.22, 1.01) * mm, "end": v(-1.25, 1.07) * mm});
            skLineSegment(sketch, "E2551", {"start": v(-1.25, 1.07) * mm, "end": v(-1.3, 1.14) * mm});
            skLineSegment(sketch, "E2552", {"start": v(-1.3, 1.14) * mm, "end": v(-1.36, 1.21) * mm});
            skLineSegment(sketch, "E2553", {"start": v(-1.36, 1.21) * mm, "end": v(-1.41, 1.28) * mm});
            skLineSegment(sketch, "E2554", {"start": v(-1.41, 1.28) * mm, "end": v(-1.47, 1.34) * mm});
            skLineSegment(sketch, "E2555", {"start": v(-1.47, 1.34) * mm, "end": v(-1.53, 1.4) * mm});
            skLineSegment(sketch, "E2556", {"start": v(-1.53, 1.4) * mm, "end": v(-1.57, 1.44) * mm});
            skLineSegment(sketch, "E2557", {"start": v(-1.57, 1.44) * mm, "end": v(-1.62, 1.48) * mm});
            skLineSegment(sketch, "E2558", {"start": v(-1.62, 1.48) * mm, "end": v(-1.67, 1.54) * mm});
            skLineSegment(sketch, "E2559", {"start": v(-1.67, 1.54) * mm, "end": v(-1.73, 1.59) * mm});
            skLineSegment(sketch, "E2560", {"start": v(-1.73, 1.59) * mm, "end": v(-1.83, 1.68) * mm});
            skLineSegment(sketch, "E2561", {"start": v(-1.83, 1.68) * mm, "end": v(-1.92, 1.76) * mm});
            skLineSegment(sketch, "E2562", {"start": v(-1.92, 1.76) * mm, "end": v(-2, 1.82) * mm});
            skLineSegment(sketch, "E2563", {"start": v(-2, 1.82) * mm, "end": v(-2.06, 1.86) * mm});
            skLineSegment(sketch, "E2564", {"start": v(-2.06, 1.86) * mm, "end": v(-2.1, 1.89) * mm});
            skLineSegment(sketch, "E2565", {"start": v(-2.1, 1.89) * mm, "end": v(-2.15, 1.92) * mm});
            skLineSegment(sketch, "E2566", {"start": v(-2.15, 1.92) * mm, "end": v(-2.23, 1.97) * mm});
            skLineSegment(sketch, "E2567", {"start": v(-2.23, 1.97) * mm, "end": v(-2.32, 2.03) * mm});
            skLineSegment(sketch, "E2568", {"start": v(-2.32, 2.03) * mm, "end": v(-2.42, 2.1) * mm});
            skLineSegment(sketch, "E2569", {"start": v(-2.42, 2.1) * mm, "end": v(-2.5, 2.15) * mm});
            skLineSegment(sketch, "E2570", {"start": v(-2.5, 2.15) * mm, "end": v(-2.59, 2.2) * mm});
            skLineSegment(sketch, "E2571", {"start": v(-2.59, 2.2) * mm, "end": v(-2.67, 2.23) * mm});
            skLineSegment(sketch, "E2572", {"start": v(-2.67, 2.23) * mm, "end": v(-2.73, 2.25) * mm});
            skLineSegment(sketch, "E2573", {"start": v(-2.73, 2.25) * mm, "end": v(-2.78, 2.27) * mm});
            skLineSegment(sketch, "E2574", {"start": v(-2.78, 2.27) * mm, "end": v(-2.81, 2.28) * mm});
            skLineSegment(sketch, "E2575", {"start": v(-2.81, 2.28) * mm, "end": v(-2.83, 2.29) * mm});
            skLineSegment(sketch, "E2576", {"start": v(-2.83, 2.29) * mm, "end": v(-2.84, 2.28) * mm});
            skLineSegment(sketch, "E2577", {"start": v(-2.84, 2.28) * mm, "end": v(-2.85, 2.27) * mm});
            skLineSegment(sketch, "E2578", {"start": v(-2.85, 2.27) * mm, "end": v(-2.86, 2.26) * mm});
            skLineSegment(sketch, "E2579", {"start": v(-2.86, 2.26) * mm, "end": v(-2.88, 2.23) * mm});
            skLineSegment(sketch, "E2580", {"start": v(-2.88, 2.23) * mm, "end": v(-2.89, 2.21) * mm});
            skLineSegment(sketch, "E2581", {"start": v(-2.89, 2.21) * mm, "end": v(-2.9, 2.19) * mm});
            skLineSegment(sketch, "E2582", {"start": v(-2.9, 2.19) * mm, "end": v(-2.9, 2.16) * mm});
            skLineSegment(sketch, "E2583", {"start": v(-2.9, 2.16) * mm, "end": v(-2.9, 2.15) * mm});
            skLineSegment(sketch, "E2584", {"start": v(-2.9, 2.15) * mm, "end": v(-2.9, 2.08) * mm});
            skLineSegment(sketch, "E2585", {"start": v(-2.9, 2.08) * mm, "end": v(-2.88, 2) * mm});
            skLineSegment(sketch, "E2586", {"start": v(-2.88, 2) * mm, "end": v(-2.86, 1.92) * mm});
            skLineSegment(sketch, "E2587", {"start": v(-2.86, 1.92) * mm, "end": v(-2.84, 1.86) * mm});
            skLineSegment(sketch, "E2588", {"start": v(-2.84, 1.86) * mm, "end": v(-2.8, 1.8) * mm});
            skLineSegment(sketch, "E2589", {"start": v(-2.8, 1.8) * mm, "end": v(-2.74, 1.72) * mm});
            skLineSegment(sketch, "E2590", {"start": v(-2.74, 1.72) * mm, "end": v(-2.66, 1.65) * mm});
            skLineSegment(sketch, "E2591", {"start": v(-2.66, 1.65) * mm, "end": v(-2.6, 1.6) * mm});
            skLineSegment(sketch, "E2592", {"start": v(-2.6, 1.6) * mm, "end": v(-2.55, 1.56) * mm});
            skLineSegment(sketch, "E2593", {"start": v(-2.55, 1.56) * mm, "end": v(-2.51, 1.53) * mm});
            skLineSegment(sketch, "E2594", {"start": v(-2.51, 1.53) * mm, "end": v(-2.48, 1.5) * mm});
            skLineSegment(sketch, "E2595", {"start": v(-2.48, 1.5) * mm, "end": v(-2.46, 1.5) * mm});
            skLineSegment(sketch, "E2596", {"start": v(-2.46, 1.5) * mm, "end": v(-2.4, 1.44) * mm});
            skLineSegment(sketch, "E2597", {"start": v(-2.4, 1.44) * mm, "end": v(-2.32, 1.4) * mm});
            skLineSegment(sketch, "E2598", {"start": v(-2.32, 1.4) * mm, "end": v(-2.2, 1.33) * mm});
            skLineSegment(sketch, "E2599", {"start": v(-2.2, 1.33) * mm, "end": v(-2.04, 1.25) * mm});
            skLineSegment(sketch, "E2600", {"start": v(-2.04, 1.25) * mm, "end": v(-1.8, 1.14) * mm});
            skLineSegment(sketch, "E2601", {"start": v(-1.8, 1.14) * mm, "end": v(-1.61, 1.06) * mm});
            skLineSegment(sketch, "E2602", {"start": v(-1.61, 1.06) * mm, "end": v(-1.44, 1) * mm});
            skLineSegment(sketch, "E2603", {"start": v(-1.44, 1) * mm, "end": v(-1.27, 0.94) * mm});
            skLineSegment(sketch, "E2604", {"start": v(-1.27, 0.94) * mm, "end": v(-1.22, 0.93) * mm});
            skLineSegment(sketch, "E2605", {"start": v(-1.22, 0.93) * mm, "end": v(-1.2, 0.92) * mm});
            skLineSegment(sketch, "E2606", {"start": v(-1.2, 0.92) * mm, "end": v(-1.18, 0.93) * mm});
            skLineSegment(sketch, "E2607", {"start": v(-1.18, 0.93) * mm, "end": v(-1.18, 0.93) * mm});
            skLineSegment(sketch, "E2608", {"start": v(6.79, 1.32) * mm, "end": v(6.89, 1.4) * mm});
            skLineSegment(sketch, "E2609", {"start": v(6.89, 1.4) * mm, "end": v(6.97, 1.48) * mm});
            skLineSegment(sketch, "E2610", {"start": v(6.97, 1.48) * mm, "end": v(7.04, 1.56) * mm});
            skLineSegment(sketch, "E2611", {"start": v(7.04, 1.56) * mm, "end": v(7.12, 1.66) * mm});
            skLineSegment(sketch, "E2612", {"start": v(7.12, 1.66) * mm, "end": v(7.16, 1.72) * mm});
            skLineSegment(sketch, "E2613", {"start": v(7.16, 1.72) * mm, "end": v(7.2, 1.79) * mm});
            skLineSegment(sketch, "E2614", {"start": v(7.2, 1.79) * mm, "end": v(7.25, 1.86) * mm});
            skLineSegment(sketch, "E2615", {"start": v(7.25, 1.86) * mm, "end": v(7.3, 1.92) * mm});
            skLineSegment(sketch, "E2616", {"start": v(7.3, 1.92) * mm, "end": v(7.33, 1.98) * mm});
            skLineSegment(sketch, "E2617", {"start": v(7.33, 1.98) * mm, "end": v(7.36, 2.03) * mm});
            skLineSegment(sketch, "E2618", {"start": v(7.36, 2.03) * mm, "end": v(7.38, 2.07) * mm});
            skLineSegment(sketch, "E2619", {"start": v(7.38, 2.07) * mm, "end": v(7.38, 2.1) * mm});
            skLineSegment(sketch, "E2620", {"start": v(7.38, 2.1) * mm, "end": v(7.37, 2.1) * mm});
            skLineSegment(sketch, "E2621", {"start": v(7.37, 2.1) * mm, "end": v(7.33, 2.12) * mm});
            skLineSegment(sketch, "E2622", {"start": v(7.33, 2.12) * mm, "end": v(7.27, 2.13) * mm});
            skLineSegment(sketch, "E2623", {"start": v(7.27, 2.13) * mm, "end": v(7.2, 2.14) * mm});
            skLineSegment(sketch, "E2624", {"start": v(7.2, 2.14) * mm, "end": v(7.1, 2.14) * mm});
            skLineSegment(sketch, "E2625", {"start": v(7.1, 2.14) * mm, "end": v(7.01, 2.14) * mm});
            skLineSegment(sketch, "E2626", {"start": v(7.01, 2.14) * mm, "end": v(6.92, 2.13) * mm});
            skLineSegment(sketch, "E2627", {"start": v(6.92, 2.13) * mm, "end": v(6.84, 2.12) * mm});
            skLineSegment(sketch, "E2628", {"start": v(6.84, 2.12) * mm, "end": v(6.7, 2.09) * mm});
            skLineSegment(sketch, "E2629", {"start": v(6.7, 2.09) * mm, "end": v(6.53, 2.03) * mm});
            skLineSegment(sketch, "E2630", {"start": v(6.53, 2.03) * mm, "end": v(6.36, 1.97) * mm});
            skLineSegment(sketch, "E2631", {"start": v(6.36, 1.97) * mm, "end": v(6.18, 1.88) * mm});
            skLineSegment(sketch, "E2632", {"start": v(6.18, 1.88) * mm, "end": v(6.03, 1.82) * mm});
            skLineSegment(sketch, "E2633", {"start": v(6.03, 1.82) * mm, "end": v(5.92, 1.77) * mm});
            skLineSegment(sketch, "E2634", {"start": v(5.92, 1.77) * mm, "end": v(5.83, 1.75) * mm});
            skLineSegment(sketch, "E2635", {"start": v(5.83, 1.75) * mm, "end": v(5.71, 1.72) * mm});
            skLineSegment(sketch, "E2636", {"start": v(5.71, 1.72) * mm, "end": v(5.67, 1.71) * mm});
            skLineSegment(sketch, "E2637", {"start": v(5.67, 1.71) * mm, "end": v(5.63, 1.7) * mm});
            skLineSegment(sketch, "E2638", {"start": v(5.63, 1.7) * mm, "end": v(5.6, 1.7) * mm});
            skLineSegment(sketch, "E2639", {"start": v(5.6, 1.7) * mm, "end": v(5.59, 1.7) * mm});
            skLineSegment(sketch, "E2640", {"start": v(5.59, 1.7) * mm, "end": v(5.59, 1.69) * mm});
            skLineSegment(sketch, "E2641", {"start": v(5.59, 1.69) * mm, "end": v(5.6, 1.68) * mm});
            skLineSegment(sketch, "E2642", {"start": v(5.6, 1.68) * mm, "end": v(5.65, 1.67) * mm});
            skLineSegment(sketch, "E2643", {"start": v(5.65, 1.67) * mm, "end": v(5.73, 1.66) * mm});
            skLineSegment(sketch, "E2644", {"start": v(5.73, 1.66) * mm, "end": v(5.79, 1.65) * mm});
            skLineSegment(sketch, "E2645", {"start": v(5.79, 1.65) * mm, "end": v(5.84, 1.64) * mm});
            skLineSegment(sketch, "E2646", {"start": v(5.84, 1.64) * mm, "end": v(5.88, 1.63) * mm});
            skLineSegment(sketch, "E2647", {"start": v(5.88, 1.63) * mm, "end": v(5.93, 1.62) * mm});
            skLineSegment(sketch, "E2648", {"start": v(5.93, 1.62) * mm, "end": v(5.98, 1.6) * mm});
            skLineSegment(sketch, "E2649", {"start": v(5.98, 1.6) * mm, "end": v(6.04, 1.58) * mm});
            skLineSegment(sketch, "E2650", {"start": v(6.04, 1.58) * mm, "end": v(6.1, 1.55) * mm});
            skLineSegment(sketch, "E2651", {"start": v(6.1, 1.55) * mm, "end": v(6.18, 1.5) * mm});
            skLineSegment(sketch, "E2652", {"start": v(6.18, 1.5) * mm, "end": v(6.33, 1.43) * mm});
            skLineSegment(sketch, "E2653", {"start": v(6.33, 1.43) * mm, "end": v(6.47, 1.36) * mm});
            skLineSegment(sketch, "E2654", {"start": v(6.47, 1.36) * mm, "end": v(6.57, 1.3) * mm});
            skLineSegment(sketch, "E2655", {"start": v(6.57, 1.3) * mm, "end": v(6.63, 1.24) * mm});
            skLineSegment(sketch, "E2656", {"start": v(6.63, 1.24) * mm, "end": v(6.64, 1.23) * mm});
            skLineSegment(sketch, "E2657", {"start": v(6.64, 1.23) * mm, "end": v(6.66, 1.22) * mm});
            skLineSegment(sketch, "E2658", {"start": v(6.66, 1.22) * mm, "end": v(6.67, 1.23) * mm});
            skLineSegment(sketch, "E2659", {"start": v(6.67, 1.23) * mm, "end": v(6.7, 1.25) * mm});
            skLineSegment(sketch, "E2660", {"start": v(6.7, 1.25) * mm, "end": v(6.74, 1.28) * mm});
            skLineSegment(sketch, "E2661", {"start": v(6.74, 1.28) * mm, "end": v(6.79, 1.32) * mm});
            skLineSegment(sketch, "E2662", {"start": v(2.38, 1.44) * mm, "end": v(2.47, 1.46) * mm});
            skLineSegment(sketch, "E2663", {"start": v(2.47, 1.46) * mm, "end": v(2.58, 1.48) * mm});
            skLineSegment(sketch, "E2664", {"start": v(2.58, 1.48) * mm, "end": v(2.71, 1.5) * mm});
            skLineSegment(sketch, "E2665", {"start": v(2.71, 1.5) * mm, "end": v(2.85, 1.53) * mm});
            skLineSegment(sketch, "E2666", {"start": v(2.85, 1.53) * mm, "end": v(3, 1.56) * mm});
            skLineSegment(sketch, "E2667", {"start": v(3, 1.56) * mm, "end": v(3.12, 1.58) * mm});
            skLineSegment(sketch, "E2668", {"start": v(3.12, 1.58) * mm, "end": v(3.23, 1.6) * mm});
            skLineSegment(sketch, "E2669", {"start": v(3.23, 1.6) * mm, "end": v(3.3, 1.6) * mm});
            skLineSegment(sketch, "E2670", {"start": v(3.3, 1.6) * mm, "end": v(3.34, 1.6) * mm});
            skLineSegment(sketch, "E2671", {"start": v(3.34, 1.6) * mm, "end": v(3.4, 1.62) * mm});
            skLineSegment(sketch, "E2672", {"start": v(3.4, 1.62) * mm, "end": v(3.45, 1.62) * mm});
            skLineSegment(sketch, "E2673", {"start": v(3.45, 1.62) * mm, "end": v(3.5, 1.63) * mm});
            skLineSegment(sketch, "E2674", {"start": v(3.5, 1.63) * mm, "end": v(3.58, 1.64) * mm});
            skLineSegment(sketch, "E2675", {"start": v(3.58, 1.64) * mm, "end": v(3.71, 1.65) * mm});
            skLineSegment(sketch, "E2676", {"start": v(3.71, 1.65) * mm, "end": v(3.88, 1.67) * mm});
            skLineSegment(sketch, "E2677", {"start": v(3.88, 1.67) * mm, "end": v(4.05, 1.68) * mm});
            skLineSegment(sketch, "E2678", {"start": v(4.05, 1.68) * mm, "end": v(4.26, 1.7) * mm});
            skLineSegment(sketch, "E2679", {"start": v(4.26, 1.7) * mm, "end": v(4.42, 1.72) * mm});
            skLineSegment(sketch, "E2680", {"start": v(4.42, 1.72) * mm, "end": v(4.54, 1.73) * mm});
            skLineSegment(sketch, "E2681", {"start": v(4.54, 1.73) * mm, "end": v(4.63, 1.74) * mm});
            skLineSegment(sketch, "E2682", {"start": v(4.63, 1.74) * mm, "end": v(4.7, 1.75) * mm});
            skLineSegment(sketch, "E2683", {"start": v(4.7, 1.75) * mm, "end": v(4.74, 1.76) * mm});
            skLineSegment(sketch, "E2684", {"start": v(4.74, 1.76) * mm, "end": v(4.78, 1.78) * mm});
            skLineSegment(sketch, "E2685", {"start": v(4.78, 1.78) * mm, "end": v(4.82, 1.8) * mm});
            skLineSegment(sketch, "E2686", {"start": v(4.82, 1.8) * mm, "end": v(4.98, 1.87) * mm});
            skLineSegment(sketch, "E2687", {"start": v(4.98, 1.87) * mm, "end": v(5.16, 1.98) * mm});
            skLineSegment(sketch, "E2688", {"start": v(5.16, 1.98) * mm, "end": v(5.34, 2.11) * mm});
            skLineSegment(sketch, "E2689", {"start": v(5.34, 2.11) * mm, "end": v(5.5, 2.24) * mm});
            skLineSegment(sketch, "E2690", {"start": v(5.5, 2.24) * mm, "end": v(5.55, 2.28) * mm});
            skLineSegment(sketch, "E2691", {"start": v(5.55, 2.28) * mm, "end": v(5.59, 2.31) * mm});
            skLineSegment(sketch, "E2692", {"start": v(5.59, 2.31) * mm, "end": v(5.62, 2.34) * mm});
            skLineSegment(sketch, "E2693", {"start": v(5.62, 2.34) * mm, "end": v(5.65, 2.37) * mm});
            skLineSegment(sketch, "E2694", {"start": v(5.65, 2.37) * mm, "end": v(5.68, 2.4) * mm});
            skLineSegment(sketch, "E2695", {"start": v(5.68, 2.4) * mm, "end": v(5.7, 2.42) * mm});
            skLineSegment(sketch, "E2696", {"start": v(5.7, 2.42) * mm, "end": v(5.69, 2.43) * mm});
            skLineSegment(sketch, "E2697", {"start": v(5.69, 2.43) * mm, "end": v(5.65, 2.43) * mm});
            skLineSegment(sketch, "E2698", {"start": v(5.65, 2.43) * mm, "end": v(5.6, 2.42) * mm});
            skLineSegment(sketch, "E2699", {"start": v(5.6, 2.42) * mm, "end": v(5.5, 2.42) * mm});
            skLineSegment(sketch, "E2700", {"start": v(5.5, 2.42) * mm, "end": v(5.39, 2.42) * mm});
            skLineSegment(sketch, "E2701", {"start": v(5.39, 2.42) * mm, "end": v(5.26, 2.41) * mm});
            skLineSegment(sketch, "E2702", {"start": v(5.26, 2.41) * mm, "end": v(5.12, 2.42) * mm});
            skLineSegment(sketch, "E2703", {"start": v(5.12, 2.42) * mm, "end": v(5, 2.42) * mm});
            skLineSegment(sketch, "E2704", {"start": v(5, 2.42) * mm, "end": v(4.87, 2.42) * mm});
            skLineSegment(sketch, "E2705", {"start": v(4.87, 2.42) * mm, "end": v(4.77, 2.43) * mm});
            skLineSegment(sketch, "E2706", {"start": v(4.77, 2.43) * mm, "end": v(4.56, 2.44) * mm});
            skLineSegment(sketch, "E2707", {"start": v(4.56, 2.44) * mm, "end": v(4.4, 2.46) * mm});
            skLineSegment(sketch, "E2708", {"start": v(4.4, 2.46) * mm, "end": v(4.3, 2.47) * mm});
            skLineSegment(sketch, "E2709", {"start": v(4.3, 2.47) * mm, "end": v(4.2, 2.49) * mm});
            skLineSegment(sketch, "E2710", {"start": v(4.2, 2.49) * mm, "end": v(4.11, 2.5) * mm});
            skLineSegment(sketch, "E2711", {"start": v(4.11, 2.5) * mm, "end": v(4.04, 2.5) * mm});
            skLineSegment(sketch, "E2712", {"start": v(4.04, 2.5) * mm, "end": v(3.95, 2.5) * mm});
            skLineSegment(sketch, "E2713", {"start": v(3.95, 2.5) * mm, "end": v(3.83, 2.5) * mm});
            skLineSegment(sketch, "E2714", {"start": v(3.83, 2.5) * mm, "end": v(3.7, 2.5) * mm});
            skLineSegment(sketch, "E2715", {"start": v(3.7, 2.5) * mm, "end": v(3.63, 2.49) * mm});
            skLineSegment(sketch, "E2716", {"start": v(3.63, 2.49) * mm, "end": v(3.56, 2.48) * mm});
            skLineSegment(sketch, "E2717", {"start": v(3.56, 2.48) * mm, "end": v(3.5, 2.46) * mm});
            skLineSegment(sketch, "E2718", {"start": v(3.5, 2.46) * mm, "end": v(3.37, 2.42) * mm});
            skLineSegment(sketch, "E2719", {"start": v(3.37, 2.42) * mm, "end": v(3.26, 2.38) * mm});
            skLineSegment(sketch, "E2720", {"start": v(3.26, 2.38) * mm, "end": v(3.15, 2.33) * mm});
            skLineSegment(sketch, "E2721", {"start": v(3.15, 2.33) * mm, "end": v(3.01, 2.25) * mm});
            skLineSegment(sketch, "E2722", {"start": v(3.01, 2.25) * mm, "end": v(2.8, 2.1) * mm});
            skLineSegment(sketch, "E2723", {"start": v(2.8, 2.1) * mm, "end": v(2.61, 1.95) * mm});
            skLineSegment(sketch, "E2724", {"start": v(2.61, 1.95) * mm, "end": v(2.44, 1.77) * mm});
            skLineSegment(sketch, "E2725", {"start": v(2.44, 1.77) * mm, "end": v(2.3, 1.57) * mm});
            skLineSegment(sketch, "E2726", {"start": v(2.3, 1.57) * mm, "end": v(2.28, 1.55) * mm});
            skLineSegment(sketch, "E2727", {"start": v(2.28, 1.55) * mm, "end": v(2.26, 1.52) * mm});
            skLineSegment(sketch, "E2728", {"start": v(2.26, 1.52) * mm, "end": v(2.23, 1.49) * mm});
            skLineSegment(sketch, "E2729", {"start": v(2.23, 1.49) * mm, "end": v(2.2, 1.46) * mm});
            skLineSegment(sketch, "E2730", {"start": v(2.2, 1.46) * mm, "end": v(2.2, 1.44) * mm});
            skLineSegment(sketch, "E2731", {"start": v(2.2, 1.44) * mm, "end": v(2.18, 1.42) * mm});
            skLineSegment(sketch, "E2732", {"start": v(2.18, 1.42) * mm, "end": v(2.17, 1.4) * mm});
            skLineSegment(sketch, "E2733", {"start": v(2.17, 1.4) * mm, "end": v(2.17, 1.4) * mm});
            skLineSegment(sketch, "E2734", {"start": v(2.17, 1.4) * mm, "end": v(2.19, 1.39) * mm});
            skLineSegment(sketch, "E2735", {"start": v(2.19, 1.39) * mm, "end": v(2.23, 1.4) * mm});
            skLineSegment(sketch, "E2736", {"start": v(2.23, 1.4) * mm, "end": v(2.26, 1.4) * mm});
            skLineSegment(sketch, "E2737", {"start": v(2.26, 1.4) * mm, "end": v(2.3, 1.41) * mm});
            skLineSegment(sketch, "E2738", {"start": v(2.3, 1.41) * mm, "end": v(2.34, 1.43) * mm});
            skLineSegment(sketch, "E2739", {"start": v(2.34, 1.43) * mm, "end": v(2.38, 1.44) * mm});
            skLineSegment(sketch, "E2740", {"start": v(-8.08, 1.48) * mm, "end": v(-7.62, 1.57) * mm});
            skLineSegment(sketch, "E2741", {"start": v(-7.62, 1.57) * mm, "end": v(-7.17, 1.63) * mm});
            skLineSegment(sketch, "E2742", {"start": v(-7.17, 1.63) * mm, "end": v(-7.09, 1.64) * mm});
            skLineSegment(sketch, "E2743", {"start": v(-7.09, 1.64) * mm, "end": v(-7, 1.65) * mm});
            skLineSegment(sketch, "E2744", {"start": v(-7, 1.65) * mm, "end": v(-6.93, 1.66) * mm});
            skLineSegment(sketch, "E2745", {"start": v(-6.93, 1.66) * mm, "end": v(-6.88, 1.67) * mm});
            skLineSegment(sketch, "E2746", {"start": v(-6.88, 1.67) * mm, "end": v(-6.77, 1.67) * mm});
            skLineSegment(sketch, "E2747", {"start": v(-6.77, 1.67) * mm, "end": v(-6.62, 1.68) * mm});
            skLineSegment(sketch, "E2748", {"start": v(-6.62, 1.68) * mm, "end": v(-6.55, 1.68) * mm});
            skLineSegment(sketch, "E2749", {"start": v(-6.55, 1.68) * mm, "end": v(-6.5, 1.68) * mm});
            skLineSegment(sketch, "E2750", {"start": v(-6.5, 1.68) * mm, "end": v(-6.47, 1.68) * mm});
            skLineSegment(sketch, "E2751", {"start": v(-6.47, 1.68) * mm, "end": v(-6.47, 1.69) * mm});
            skLineSegment(sketch, "E2752", {"start": v(-6.47, 1.69) * mm, "end": v(-6.48, 1.7) * mm});
            skLineSegment(sketch, "E2753", {"start": v(-6.48, 1.7) * mm, "end": v(-6.5, 1.7) * mm});
            skLineSegment(sketch, "E2754", {"start": v(-6.5, 1.7) * mm, "end": v(-6.53, 1.72) * mm});
            skLineSegment(sketch, "E2755", {"start": v(-6.53, 1.72) * mm, "end": v(-6.56, 1.73) * mm});
            skLineSegment(sketch, "E2756", {"start": v(-6.56, 1.73) * mm, "end": v(-6.72, 1.8) * mm});
            skLineSegment(sketch, "E2757", {"start": v(-6.72, 1.8) * mm, "end": v(-6.88, 1.89) * mm});
            skLineSegment(sketch, "E2758", {"start": v(-6.88, 1.89) * mm, "end": v(-7.04, 1.97) * mm});
            skLineSegment(sketch, "E2759", {"start": v(-7.04, 1.97) * mm, "end": v(-7.16, 2.04) * mm});
            skLineSegment(sketch, "E2760", {"start": v(-7.16, 2.04) * mm, "end": v(-7.27, 2.11) * mm});
            skLineSegment(sketch, "E2761", {"start": v(-7.27, 2.11) * mm, "end": v(-7.34, 2.16) * mm});
            skLineSegment(sketch, "E2762", {"start": v(-7.34, 2.16) * mm, "end": v(-7.4, 2.18) * mm});
            skLineSegment(sketch, "E2763", {"start": v(-7.4, 2.18) * mm, "end": v(-7.42, 2.19) * mm});
            skLineSegment(sketch, "E2764", {"start": v(-7.42, 2.19) * mm, "end": v(-7.45, 2.2) * mm});
            skLineSegment(sketch, "E2765", {"start": v(-7.45, 2.2) * mm, "end": v(-7.5, 2.2) * mm});
            skLineSegment(sketch, "E2766", {"start": v(-7.5, 2.2) * mm, "end": v(-7.56, 2.21) * mm});
            skLineSegment(sketch, "E2767", {"start": v(-7.56, 2.21) * mm, "end": v(-7.63, 2.23) * mm});
            skLineSegment(sketch, "E2768", {"start": v(-7.63, 2.23) * mm, "end": v(-7.71, 2.24) * mm});
            skLineSegment(sketch, "E2769", {"start": v(-7.71, 2.24) * mm, "end": v(-7.78, 2.26) * mm});
            skLineSegment(sketch, "E2770", {"start": v(-7.78, 2.26) * mm, "end": v(-7.84, 2.27) * mm});
            skLineSegment(sketch, "E2771", {"start": v(-7.84, 2.27) * mm, "end": v(-7.89, 2.28) * mm});
            skLineSegment(sketch, "E2772", {"start": v(-7.89, 2.28) * mm, "end": v(-8.04, 2.33) * mm});
            skLineSegment(sketch, "E2773", {"start": v(-8.04, 2.33) * mm, "end": v(-8.2, 2.43) * mm});
            skLineSegment(sketch, "E2774", {"start": v(-8.2, 2.43) * mm, "end": v(-8.3, 2.5) * mm});
            skLineSegment(sketch, "E2775", {"start": v(-8.3, 2.5) * mm, "end": v(-8.41, 2.58) * mm});
            skLineSegment(sketch, "E2776", {"start": v(-8.41, 2.58) * mm, "end": v(-8.5, 2.65) * mm});
            skLineSegment(sketch, "E2777", {"start": v(-8.5, 2.65) * mm, "end": v(-8.6, 2.72) * mm});
            skLineSegment(sketch, "E2778", {"start": v(-8.6, 2.72) * mm, "end": v(-8.62, 2.74) * mm});
            skLineSegment(sketch, "E2779", {"start": v(-8.62, 2.74) * mm, "end": v(-8.65, 2.76) * mm});
            skLineSegment(sketch, "E2780", {"start": v(-8.65, 2.76) * mm, "end": v(-8.67, 2.77) * mm});
            skLineSegment(sketch, "E2781", {"start": v(-8.67, 2.77) * mm, "end": v(-8.68, 2.77) * mm});
            skLineSegment(sketch, "E2782", {"start": v(-8.68, 2.77) * mm, "end": v(-8.69, 2.76) * mm});
            skLineSegment(sketch, "E2783", {"start": v(-8.69, 2.76) * mm, "end": v(-8.69, 2.72) * mm});
            skLineSegment(sketch, "E2784", {"start": v(-8.69, 2.72) * mm, "end": v(-8.7, 2.67) * mm});
            skLineSegment(sketch, "E2785", {"start": v(-8.7, 2.67) * mm, "end": v(-8.7, 2.6) * mm});
            skLineSegment(sketch, "E2786", {"start": v(-8.7, 2.6) * mm, "end": v(-8.68, 2.4) * mm});
            skLineSegment(sketch, "E2787", {"start": v(-8.68, 2.4) * mm, "end": v(-8.65, 2.18) * mm});
            skLineSegment(sketch, "E2788", {"start": v(-8.65, 2.18) * mm, "end": v(-8.6, 1.96) * mm});
            skLineSegment(sketch, "E2789", {"start": v(-8.6, 1.96) * mm, "end": v(-8.54, 1.78) * mm});
            skLineSegment(sketch, "E2790", {"start": v(-8.54, 1.78) * mm, "end": v(-8.53, 1.74) * mm});
            skLineSegment(sketch, "E2791", {"start": v(-8.53, 1.74) * mm, "end": v(-8.51, 1.71) * mm});
            skLineSegment(sketch, "E2792", {"start": v(-8.51, 1.71) * mm, "end": v(-8.5, 1.69) * mm});
            skLineSegment(sketch, "E2793", {"start": v(-8.5, 1.69) * mm, "end": v(-8.5, 1.68) * mm});
            skLineSegment(sketch, "E2794", {"start": v(-8.5, 1.68) * mm, "end": v(-8.5, 1.66) * mm});
            skLineSegment(sketch, "E2795", {"start": v(-8.5, 1.66) * mm, "end": v(-8.5, 1.64) * mm});
            skLineSegment(sketch, "E2796", {"start": v(-8.5, 1.64) * mm, "end": v(-8.48, 1.61) * mm});
            skLineSegment(sketch, "E2797", {"start": v(-8.48, 1.61) * mm, "end": v(-8.47, 1.58) * mm});
            skLineSegment(sketch, "E2798", {"start": v(-8.47, 1.58) * mm, "end": v(-8.45, 1.55) * mm});
            skLineSegment(sketch, "E2799", {"start": v(-8.45, 1.55) * mm, "end": v(-8.44, 1.52) * mm});
            skLineSegment(sketch, "E2800", {"start": v(-8.44, 1.52) * mm, "end": v(-8.42, 1.49) * mm});
            skLineSegment(sketch, "E2801", {"start": v(-8.42, 1.49) * mm, "end": v(-8.4, 1.46) * mm});
            skLineSegment(sketch, "E2802", {"start": v(-8.4, 1.46) * mm, "end": v(-8.4, 1.44) * mm});
            skLineSegment(sketch, "E2803", {"start": v(-8.4, 1.44) * mm, "end": v(-8.38, 1.43) * mm});
            skLineSegment(sketch, "E2804", {"start": v(-8.38, 1.43) * mm, "end": v(-8.36, 1.42) * mm});
            skLineSegment(sketch, "E2805", {"start": v(-8.36, 1.42) * mm, "end": v(-8.33, 1.43) * mm});
            skLineSegment(sketch, "E2806", {"start": v(-8.33, 1.43) * mm, "end": v(-8.3, 1.43) * mm});
            skLineSegment(sketch, "E2807", {"start": v(-8.3, 1.43) * mm, "end": v(-8.24, 1.44) * mm});
            skLineSegment(sketch, "E2808", {"start": v(-8.24, 1.44) * mm, "end": v(-8.17, 1.46) * mm});
            skLineSegment(sketch, "E2809", {"start": v(-8.17, 1.46) * mm, "end": v(-8.08, 1.48) * mm});
            skLineSegment(sketch, "E2810", {"start": v(-3, 1.69) * mm, "end": v(-3.1, 1.82) * mm});
            skLineSegment(sketch, "E2811", {"start": v(-3.1, 1.82) * mm, "end": v(-3.16, 1.92) * mm});
            skLineSegment(sketch, "E2812", {"start": v(-3.16, 1.92) * mm, "end": v(-3.2, 2.01) * mm});
            skLineSegment(sketch, "E2813", {"start": v(-3.2, 2.01) * mm, "end": v(-3.24, 2.1) * mm});
            skLineSegment(sketch, "E2814", {"start": v(-3.24, 2.1) * mm, "end": v(-3.26, 2.24) * mm});
            skLineSegment(sketch, "E2815", {"start": v(-3.26, 2.24) * mm, "end": v(-3.25, 2.36) * mm});
            skLineSegment(sketch, "E2816", {"start": v(-3.25, 2.36) * mm, "end": v(-3.24, 2.4) * mm});
            skLineSegment(sketch, "E2817", {"start": v(-3.24, 2.4) * mm, "end": v(-3.24, 2.42) * mm});
            skLineSegment(sketch, "E2818", {"start": v(-3.24, 2.42) * mm, "end": v(-3.25, 2.42) * mm});
            skLineSegment(sketch, "E2819", {"start": v(-3.25, 2.42) * mm, "end": v(-3.28, 2.43) * mm});
            skLineSegment(sketch, "E2820", {"start": v(-3.28, 2.43) * mm, "end": v(-3.31, 2.44) * mm});
            skLineSegment(sketch, "E2821", {"start": v(-3.31, 2.44) * mm, "end": v(-3.35, 2.45) * mm});
            skLineSegment(sketch, "E2822", {"start": v(-3.35, 2.45) * mm, "end": v(-3.6, 2.5) * mm});
            skLineSegment(sketch, "E2823", {"start": v(-3.6, 2.5) * mm, "end": v(-3.82, 2.55) * mm});
            skLineSegment(sketch, "E2824", {"start": v(-3.82, 2.55) * mm, "end": v(-4.03, 2.58) * mm});
            skLineSegment(sketch, "E2825", {"start": v(-4.03, 2.58) * mm, "end": v(-4.23, 2.6) * mm});
            skLineSegment(sketch, "E2826", {"start": v(-4.23, 2.6) * mm, "end": v(-4.47, 2.6) * mm});
            skLineSegment(sketch, "E2827", {"start": v(-4.47, 2.6) * mm, "end": v(-4.74, 2.59) * mm});
            skLineSegment(sketch, "E2828", {"start": v(-4.74, 2.59) * mm, "end": v(-5, 2.56) * mm});
            skLineSegment(sketch, "E2829", {"start": v(-5, 2.56) * mm, "end": v(-5.24, 2.52) * mm});
            skLineSegment(sketch, "E2830", {"start": v(-5.24, 2.52) * mm, "end": v(-5.35, 2.5) * mm});
            skLineSegment(sketch, "E2831", {"start": v(-5.35, 2.5) * mm, "end": v(-5.47, 2.48) * mm});
            skLineSegment(sketch, "E2832", {"start": v(-5.47, 2.48) * mm, "end": v(-5.55, 2.46) * mm});
            skLineSegment(sketch, "E2833", {"start": v(-5.55, 2.46) * mm, "end": v(-5.64, 2.45) * mm});
            skLineSegment(sketch, "E2834", {"start": v(-5.64, 2.45) * mm, "end": v(-5.74, 2.43) * mm});
            skLineSegment(sketch, "E2835", {"start": v(-5.74, 2.43) * mm, "end": v(-5.83, 2.4) * mm});
            skLineSegment(sketch, "E2836", {"start": v(-5.83, 2.4) * mm, "end": v(-5.91, 2.4) * mm});
            skLineSegment(sketch, "E2837", {"start": v(-5.91, 2.4) * mm, "end": v(-5.99, 2.38) * mm});
            skLineSegment(sketch, "E2838", {"start": v(-5.99, 2.38) * mm, "end": v(-6.04, 2.36) * mm});
            skLineSegment(sketch, "E2839", {"start": v(-6.04, 2.36) * mm, "end": v(-6.07, 2.36) * mm});
            skLineSegment(sketch, "E2840", {"start": v(-6.07, 2.36) * mm, "end": v(-6.1, 2.34) * mm});
            skLineSegment(sketch, "E2841", {"start": v(-6.1, 2.34) * mm, "end": v(-6.17, 2.33) * mm});
            skLineSegment(sketch, "E2842", {"start": v(-6.17, 2.33) * mm, "end": v(-6.25, 2.31) * mm});
            skLineSegment(sketch, "E2843", {"start": v(-6.25, 2.31) * mm, "end": v(-6.34, 2.3) * mm});
            skLineSegment(sketch, "E2844", {"start": v(-6.34, 2.3) * mm, "end": v(-6.43, 2.27) * mm});
            skLineSegment(sketch, "E2845", {"start": v(-6.43, 2.27) * mm, "end": v(-6.52, 2.25) * mm});
            skLineSegment(sketch, "E2846", {"start": v(-6.52, 2.25) * mm, "end": v(-6.6, 2.24) * mm});
            skLineSegment(sketch, "E2847", {"start": v(-6.6, 2.24) * mm, "end": v(-6.66, 2.23) * mm});
            skLineSegment(sketch, "E2848", {"start": v(-6.66, 2.23) * mm, "end": v(-6.7, 2.22) * mm});
            skLineSegment(sketch, "E2849", {"start": v(-6.7, 2.22) * mm, "end": v(-6.72, 2.2) * mm});
            skLineSegment(sketch, "E2850", {"start": v(-6.72, 2.2) * mm, "end": v(-6.7, 2.2) * mm});
            skLineSegment(sketch, "E2851", {"start": v(-6.7, 2.2) * mm, "end": v(-6.7, 2.18) * mm});
            skLineSegment(sketch, "E2852", {"start": v(-6.7, 2.18) * mm, "end": v(-6.67, 2.16) * mm});
            skLineSegment(sketch, "E2853", {"start": v(-6.67, 2.16) * mm, "end": v(-6.65, 2.14) * mm});
            skLineSegment(sketch, "E2854", {"start": v(-6.65, 2.14) * mm, "end": v(-6.61, 2.12) * mm});
            skLineSegment(sketch, "E2855", {"start": v(-6.61, 2.12) * mm, "end": v(-6.58, 2.1) * mm});
            skLineSegment(sketch, "E2856", {"start": v(-6.58, 2.1) * mm, "end": v(-6.54, 2.08) * mm});
            skLineSegment(sketch, "E2857", {"start": v(-6.54, 2.08) * mm, "end": v(-6.5, 2.06) * mm});
            skLineSegment(sketch, "E2858", {"start": v(-6.5, 2.06) * mm, "end": v(-6.47, 2.04) * mm});
            skLineSegment(sketch, "E2859", {"start": v(-6.47, 2.04) * mm, "end": v(-6.43, 2.02) * mm});
            skLineSegment(sketch, "E2860", {"start": v(-6.43, 2.02) * mm, "end": v(-6.39, 2) * mm});
            skLineSegment(sketch, "E2861", {"start": v(-6.39, 2) * mm, "end": v(-6.35, 1.99) * mm});
            skLineSegment(sketch, "E2862", {"start": v(-6.35, 1.99) * mm, "end": v(-6.3, 1.97) * mm});
            skLineSegment(sketch, "E2863", {"start": v(-6.3, 1.97) * mm, "end": v(-6.24, 1.95) * mm});
            skLineSegment(sketch, "E2864", {"start": v(-6.24, 1.95) * mm, "end": v(-6.17, 1.93) * mm});
            skLineSegment(sketch, "E2865", {"start": v(-6.17, 1.93) * mm, "end": v(-6.1, 1.9) * mm});
            skLineSegment(sketch, "E2866", {"start": v(-6.1, 1.9) * mm, "end": v(-5.95, 1.85) * mm});
            skLineSegment(sketch, "E2867", {"start": v(-5.95, 1.85) * mm, "end": v(-5.79, 1.8) * mm});
            skLineSegment(sketch, "E2868", {"start": v(-5.79, 1.8) * mm, "end": v(-5.64, 1.78) * mm});
            skLineSegment(sketch, "E2869", {"start": v(-5.64, 1.78) * mm, "end": v(-5.53, 1.77) * mm});
            skLineSegment(sketch, "E2870", {"start": v(-5.53, 1.77) * mm, "end": v(-5.5, 1.77) * mm});
            skLineSegment(sketch, "E2871", {"start": v(-5.5, 1.77) * mm, "end": v(-5.44, 1.77) * mm});
            skLineSegment(sketch, "E2872", {"start": v(-5.44, 1.77) * mm, "end": v(-5.37, 1.78) * mm});
            skLineSegment(sketch, "E2873", {"start": v(-5.37, 1.78) * mm, "end": v(-5.31, 1.8) * mm});
            skLineSegment(sketch, "E2874", {"start": v(-5.31, 1.8) * mm, "end": v(-5.2, 1.8) * mm});
            skLineSegment(sketch, "E2875", {"start": v(-5.2, 1.8) * mm, "end": v(-5.1, 1.81) * mm});
            skLineSegment(sketch, "E2876", {"start": v(-5.1, 1.81) * mm, "end": v(-4.97, 1.82) * mm});
            skLineSegment(sketch, "E2877", {"start": v(-4.97, 1.82) * mm, "end": v(-4.85, 1.82) * mm});
            skLineSegment(sketch, "E2878", {"start": v(-4.85, 1.82) * mm, "end": v(-4.74, 1.81) * mm});
            skLineSegment(sketch, "E2879", {"start": v(-4.74, 1.81) * mm, "end": v(-4.63, 1.8) * mm});
            skLineSegment(sketch, "E2880", {"start": v(-4.63, 1.8) * mm, "end": v(-4.54, 1.79) * mm});
            skLineSegment(sketch, "E2881", {"start": v(-4.54, 1.79) * mm, "end": v(-4.48, 1.77) * mm});
            skLineSegment(sketch, "E2882", {"start": v(-4.48, 1.77) * mm, "end": v(-4.44, 1.76) * mm});
            skLineSegment(sketch, "E2883", {"start": v(-4.44, 1.76) * mm, "end": v(-4.38, 1.76) * mm});
            skLineSegment(sketch, "E2884", {"start": v(-4.38, 1.76) * mm, "end": v(-4.3, 1.76) * mm});
            skLineSegment(sketch, "E2885", {"start": v(-4.3, 1.76) * mm, "end": v(-4.16, 1.76) * mm});
            skLineSegment(sketch, "E2886", {"start": v(-4.16, 1.76) * mm, "end": v(-3.93, 1.75) * mm});
            skLineSegment(sketch, "E2887", {"start": v(-3.93, 1.75) * mm, "end": v(-3.76, 1.74) * mm});
            skLineSegment(sketch, "E2888", {"start": v(-3.76, 1.74) * mm, "end": v(-3.56, 1.71) * mm});
            skLineSegment(sketch, "E2889", {"start": v(-3.56, 1.71) * mm, "end": v(-3.35, 1.68) * mm});
            skLineSegment(sketch, "E2890", {"start": v(-3.35, 1.68) * mm, "end": v(-3.17, 1.64) * mm});
            skLineSegment(sketch, "E2891", {"start": v(-3.17, 1.64) * mm, "end": v(-3.05, 1.61) * mm});
            skLineSegment(sketch, "E2892", {"start": v(-3.05, 1.61) * mm, "end": v(-3, 1.6) * mm});
            skLineSegment(sketch, "E2893", {"start": v(-3, 1.6) * mm, "end": v(-2.97, 1.6) * mm});
            skLineSegment(sketch, "E2894", {"start": v(-2.97, 1.6) * mm, "end": v(-2.95, 1.59) * mm});
            skLineSegment(sketch, "E2895", {"start": v(-2.95, 1.59) * mm, "end": v(-2.94, 1.6) * mm});
            skLineSegment(sketch, "E2896", {"start": v(-2.94, 1.6) * mm, "end": v(-2.94, 1.6) * mm});
            skLineSegment(sketch, "E2897", {"start": v(-2.94, 1.6) * mm, "end": v(-2.96, 1.62) * mm});
            skLineSegment(sketch, "E2898", {"start": v(-2.96, 1.62) * mm, "end": v(-2.98, 1.65) * mm});
            skLineSegment(sketch, "E2899", {"start": v(-2.98, 1.65) * mm, "end": v(-3, 1.69) * mm});
            skLineSegment(sketch, "E2900", {"start": v(-5.75, 1.68) * mm, "end": v(-5.75, 1.69) * mm});
            skLineSegment(sketch, "E2901", {"start": v(-5.75, 1.69) * mm, "end": v(-5.77, 1.68) * mm});
            skLineSegment(sketch, "E2902", {"start": v(-5.77, 1.68) * mm, "end": v(-5.77, 1.67) * mm});
            skLineSegment(sketch, "E2903", {"start": v(-5.77, 1.67) * mm, "end": v(-5.76, 1.67) * mm});
            skLineSegment(sketch, "E2904", {"start": v(-5.76, 1.67) * mm, "end": v(-5.75, 1.67) * mm});
            skLineSegment(sketch, "E2905", {"start": v(-5.75, 1.67) * mm, "end": v(-5.75, 1.68) * mm});
            skLineSegment(sketch, "E2906", {"start": v(-0.47, 1.69) * mm, "end": v(-0.42, 1.7) * mm});
            skLineSegment(sketch, "E2907", {"start": v(-0.42, 1.7) * mm, "end": v(-0.37, 1.74) * mm});
            skLineSegment(sketch, "E2908", {"start": v(-0.37, 1.74) * mm, "end": v(-0.34, 1.79) * mm});
            skLineSegment(sketch, "E2909", {"start": v(-0.34, 1.79) * mm, "end": v(-0.32, 1.83) * mm});
            skLineSegment(sketch, "E2910", {"start": v(-0.32, 1.83) * mm, "end": v(-0.32, 1.85) * mm});
            skLineSegment(sketch, "E2911", {"start": v(-0.32, 1.85) * mm, "end": v(-0.33, 1.88) * mm});
            skLineSegment(sketch, "E2912", {"start": v(-0.33, 1.88) * mm, "end": v(-0.35, 1.9) * mm});
            skLineSegment(sketch, "E2913", {"start": v(-0.35, 1.9) * mm, "end": v(-0.37, 1.9) * mm});
            skLineSegment(sketch, "E2914", {"start": v(-0.37, 1.9) * mm, "end": v(-0.4, 1.89) * mm});
            skLineSegment(sketch, "E2915", {"start": v(-0.4, 1.89) * mm, "end": v(-0.42, 1.86) * mm});
            skLineSegment(sketch, "E2916", {"start": v(-0.42, 1.86) * mm, "end": v(-0.48, 1.82) * mm});
            skLineSegment(sketch, "E2917", {"start": v(-0.48, 1.82) * mm, "end": v(-0.54, 1.82) * mm});
            skLineSegment(sketch, "E2918", {"start": v(-0.54, 1.82) * mm, "end": v(-0.6, 1.85) * mm});
            skLineSegment(sketch, "E2919", {"start": v(-0.6, 1.85) * mm, "end": v(-0.66, 1.92) * mm});
            skLineSegment(sketch, "E2920", {"start": v(-0.66, 1.92) * mm, "end": v(-0.72, 2.05) * mm});
            skLineSegment(sketch, "E2921", {"start": v(-0.72, 2.05) * mm, "end": v(-0.76, 2.2) * mm});
            skLineSegment(sketch, "E2922", {"start": v(-0.76, 2.2) * mm, "end": v(-0.76, 2.35) * mm});
            skLineSegment(sketch, "E2923", {"start": v(-0.76, 2.35) * mm, "end": v(-0.73, 2.5) * mm});
            skLineSegment(sketch, "E2924", {"start": v(-0.73, 2.5) * mm, "end": v(-0.72, 2.53) * mm});
            skLineSegment(sketch, "E2925", {"start": v(-0.72, 2.53) * mm, "end": v(-0.7, 2.57) * mm});
            skLineSegment(sketch, "E2926", {"start": v(-0.7, 2.57) * mm, "end": v(-0.69, 2.61) * mm});
            skLineSegment(sketch, "E2927", {"start": v(-0.69, 2.61) * mm, "end": v(-0.67, 2.64) * mm});
            skLineSegment(sketch, "E2928", {"start": v(-0.67, 2.64) * mm, "end": v(-0.62, 2.71) * mm});
            skLineSegment(sketch, "E2929", {"start": v(-0.62, 2.71) * mm, "end": v(-0.56, 2.78) * mm});
            skLineSegment(sketch, "E2930", {"start": v(-0.56, 2.78) * mm, "end": v(-0.48, 2.85) * mm});
            skLineSegment(sketch, "E2931", {"start": v(-0.48, 2.85) * mm, "end": v(-0.4, 2.91) * mm});
            skLineSegment(sketch, "E2932", {"start": v(-0.4, 2.91) * mm, "end": v(-0.33, 2.96) * mm});
            skLineSegment(sketch, "E2933", {"start": v(-0.33, 2.96) * mm, "end": v(-0.25, 2.98) * mm});
            skLineSegment(sketch, "E2934", {"start": v(-0.25, 2.98) * mm, "end": v(-0.18, 2.99) * mm});
            skLineSegment(sketch, "E2935", {"start": v(-0.18, 2.99) * mm, "end": v(-0.11, 2.97) * mm});
            skLineSegment(sketch, "E2936", {"start": v(-0.11, 2.97) * mm, "end": v(-0.06, 2.95) * mm});
            skLineSegment(sketch, "E2937", {"start": v(-0.06, 2.95) * mm, "end": v(0, 2.92) * mm});
            skLineSegment(sketch, "E2938", {"start": v(0, 2.92) * mm, "end": v(0.04, 2.87) * mm});
            skLineSegment(sketch, "E2939", {"start": v(0.04, 2.87) * mm, "end": v(0.07, 2.83) * mm});
            skLineSegment(sketch, "E2940", {"start": v(0.07, 2.83) * mm, "end": v(0.1, 2.78) * mm});
            skLineSegment(sketch, "E2941", {"start": v(0.1, 2.78) * mm, "end": v(0.1, 2.73) * mm});
            skLineSegment(sketch, "E2942", {"start": v(0.1, 2.73) * mm, "end": v(0.1, 2.68) * mm});
            skLineSegment(sketch, "E2943", {"start": v(0.1, 2.68) * mm, "end": v(0.08, 2.64) * mm});
            skLineSegment(sketch, "E2944", {"start": v(0.08, 2.64) * mm, "end": v(0.06, 2.62) * mm});
            skLineSegment(sketch, "E2945", {"start": v(0.06, 2.62) * mm, "end": v(0.04, 2.6) * mm});
            skLineSegment(sketch, "E2946", {"start": v(0.04, 2.6) * mm, "end": v(0.01, 2.58) * mm});
            skLineSegment(sketch, "E2947", {"start": v(0.01, 2.58) * mm, "end": v(-0.02, 2.57) * mm});
            skLineSegment(sketch, "E2948", {"start": v(-0.02, 2.57) * mm, "end": v(-0.1, 2.5) * mm});
            skLineSegment(sketch, "E2949", {"start": v(-0.1, 2.5) * mm, "end": v(-0.16, 2.4) * mm});
            skLineSegment(sketch, "E2950", {"start": v(-0.16, 2.4) * mm, "end": v(-0.18, 2.3) * mm});
            skLineSegment(sketch, "E2951", {"start": v(-0.18, 2.3) * mm, "end": v(-0.16, 2.21) * mm});
            skLineSegment(sketch, "E2952", {"start": v(-0.16, 2.21) * mm, "end": v(-0.12, 2.16) * mm});
            skLineSegment(sketch, "E2953", {"start": v(-0.12, 2.16) * mm, "end": v(-0.06, 2.14) * mm});
            skLineSegment(sketch, "E2954", {"start": v(-0.06, 2.14) * mm, "end": v(0.02, 2.14) * mm});
            skLineSegment(sketch, "E2955", {"start": v(0.02, 2.14) * mm, "end": v(0.1, 2.16) * mm});
            skLineSegment(sketch, "E2956", {"start": v(0.1, 2.16) * mm, "end": v(0.15, 2.2) * mm});
            skLineSegment(sketch, "E2957", {"start": v(0.15, 2.2) * mm, "end": v(0.2, 2.26) * mm});
            skLineSegment(sketch, "E2958", {"start": v(0.2, 2.26) * mm, "end": v(0.23, 2.35) * mm});
            skLineSegment(sketch, "E2959", {"start": v(0.23, 2.35) * mm, "end": v(0.26, 2.46) * mm});
            skLineSegment(sketch, "E2960", {"start": v(0.26, 2.46) * mm, "end": v(0.28, 2.55) * mm});
            skLineSegment(sketch, "E2961", {"start": v(0.28, 2.55) * mm, "end": v(0.28, 2.62) * mm});
            skLineSegment(sketch, "E2962", {"start": v(0.28, 2.62) * mm, "end": v(0.28, 2.68) * mm});
            skLineSegment(sketch, "E2963", {"start": v(0.28, 2.68) * mm, "end": v(0.27, 2.74) * mm});
            skLineSegment(sketch, "E2964", {"start": v(0.27, 2.74) * mm, "end": v(0.25, 2.8) * mm});
            skLineSegment(sketch, "E2965", {"start": v(0.25, 2.8) * mm, "end": v(0.21, 2.86) * mm});
            skLineSegment(sketch, "E2966", {"start": v(0.21, 2.86) * mm, "end": v(0.17, 2.93) * mm});
            skLineSegment(sketch, "E2967", {"start": v(0.17, 2.93) * mm, "end": v(0.12, 3) * mm});
            skLineSegment(sketch, "E2968", {"start": v(0.12, 3) * mm, "end": v(0.07, 3.06) * mm});
            skLineSegment(sketch, "E2969", {"start": v(0.07, 3.06) * mm, "end": v(0.02, 3.1) * mm});
            skLineSegment(sketch, "E2970", {"start": v(0.02, 3.1) * mm, "end": v(-0.04, 3.15) * mm});
            skLineSegment(sketch, "E2971", {"start": v(-0.04, 3.15) * mm, "end": v(-0.08, 3.17) * mm});
            skLineSegment(sketch, "E2972", {"start": v(-0.08, 3.17) * mm, "end": v(-0.2, 3.19) * mm});
            skLineSegment(sketch, "E2973", {"start": v(-0.2, 3.19) * mm, "end": v(-0.34, 3.18) * mm});
            skLineSegment(sketch, "E2974", {"start": v(-0.34, 3.18) * mm, "end": v(-0.42, 3.16) * mm});
            skLineSegment(sketch, "E2975", {"start": v(-0.42, 3.16) * mm, "end": v(-0.5, 3.12) * mm});
            skLineSegment(sketch, "E2976", {"start": v(-0.5, 3.12) * mm, "end": v(-0.6, 3.07) * mm});
            skLineSegment(sketch, "E2977", {"start": v(-0.6, 3.07) * mm, "end": v(-0.68, 3.01) * mm});
            skLineSegment(sketch, "E2978", {"start": v(-0.68, 3.01) * mm, "end": v(-0.76, 2.93) * mm});
            skLineSegment(sketch, "E2979", {"start": v(-0.76, 2.93) * mm, "end": v(-0.83, 2.83) * mm});
            skLineSegment(sketch, "E2980", {"start": v(-0.83, 2.83) * mm, "end": v(-0.9, 2.7) * mm});
            skLineSegment(sketch, "E2981", {"start": v(-0.9, 2.7) * mm, "end": v(-0.94, 2.53) * mm});
            skLineSegment(sketch, "E2982", {"start": v(-0.94, 2.53) * mm, "end": v(-0.96, 2.47) * mm});
            skLineSegment(sketch, "E2983", {"start": v(-0.96, 2.47) * mm, "end": v(-0.97, 2.4) * mm});
            skLineSegment(sketch, "E2984", {"start": v(-0.97, 2.4) * mm, "end": v(-0.97, 2.35) * mm});
            skLineSegment(sketch, "E2985", {"start": v(-0.97, 2.35) * mm, "end": v(-0.98, 2.26) * mm});
            skLineSegment(sketch, "E2986", {"start": v(-0.98, 2.26) * mm, "end": v(-0.98, 2.18) * mm});
            skLineSegment(sketch, "E2987", {"start": v(-0.98, 2.18) * mm, "end": v(-0.97, 2.12) * mm});
            skLineSegment(sketch, "E2988", {"start": v(-0.97, 2.12) * mm, "end": v(-0.96, 2.09) * mm});
            skLineSegment(sketch, "E2989", {"start": v(-0.96, 2.09) * mm, "end": v(-0.95, 2.06) * mm});
            skLineSegment(sketch, "E2990", {"start": v(-0.95, 2.06) * mm, "end": v(-0.93, 2) * mm});
            skLineSegment(sketch, "E2991", {"start": v(-0.93, 2) * mm, "end": v(-0.9, 1.96) * mm});
            skLineSegment(sketch, "E2992", {"start": v(-0.9, 1.96) * mm, "end": v(-0.86, 1.86) * mm});
            skLineSegment(sketch, "E2993", {"start": v(-0.86, 1.86) * mm, "end": v(-0.8, 1.78) * mm});
            skLineSegment(sketch, "E2994", {"start": v(-0.8, 1.78) * mm, "end": v(-0.7, 1.72) * mm});
            skLineSegment(sketch, "E2995", {"start": v(-0.7, 1.72) * mm, "end": v(-0.6, 1.68) * mm});
            skLineSegment(sketch, "E2996", {"start": v(-0.6, 1.68) * mm, "end": v(-0.57, 1.67) * mm});
            skLineSegment(sketch, "E2997", {"start": v(-0.57, 1.67) * mm, "end": v(-0.53, 1.67) * mm});
            skLineSegment(sketch, "E2998", {"start": v(-0.53, 1.67) * mm, "end": v(-0.5, 1.67) * mm});
            skLineSegment(sketch, "E2999", {"start": v(-0.5, 1.67) * mm, "end": v(-0.47, 1.69) * mm});
            skLineSegment(sketch, "E3000", {"start": v(5.43, 1.8) * mm, "end": v(5.63, 1.83) * mm});
            skLineSegment(sketch, "E3001", {"start": v(5.63, 1.83) * mm, "end": v(5.8, 1.88) * mm});
            skLineSegment(sketch, "E3002", {"start": v(5.8, 1.88) * mm, "end": v(5.95, 1.94) * mm});
            skLineSegment(sketch, "E3003", {"start": v(5.95, 1.94) * mm, "end": v(6.13, 2.02) * mm});
            skLineSegment(sketch, "E3004", {"start": v(6.13, 2.02) * mm, "end": v(6.49, 2.17) * mm});
            skLineSegment(sketch, "E3005", {"start": v(6.49, 2.17) * mm, "end": v(6.82, 2.26) * mm});
            skLineSegment(sketch, "E3006", {"start": v(6.82, 2.26) * mm, "end": v(7.12, 2.29) * mm});
            skLineSegment(sketch, "E3007", {"start": v(7.12, 2.29) * mm, "end": v(7.4, 2.26) * mm});
            skLineSegment(sketch, "E3008", {"start": v(7.4, 2.26) * mm, "end": v(7.42, 2.26) * mm});
            skLineSegment(sketch, "E3009", {"start": v(7.42, 2.26) * mm, "end": v(7.44, 2.27) * mm});
            skLineSegment(sketch, "E3010", {"start": v(7.44, 2.27) * mm, "end": v(7.46, 2.3) * mm});
            skLineSegment(sketch, "E3011", {"start": v(7.46, 2.3) * mm, "end": v(7.5, 2.36) * mm});
            skLineSegment(sketch, "E3012", {"start": v(7.5, 2.36) * mm, "end": v(7.53, 2.41) * mm});
            skLineSegment(sketch, "E3013", {"start": v(7.53, 2.41) * mm, "end": v(7.55, 2.47) * mm});
            skLineSegment(sketch, "E3014", {"start": v(7.55, 2.47) * mm, "end": v(7.58, 2.52) * mm});
            skLineSegment(sketch, "E3015", {"start": v(7.58, 2.52) * mm, "end": v(7.6, 2.57) * mm});
            skLineSegment(sketch, "E3016", {"start": v(7.6, 2.57) * mm, "end": v(7.63, 2.61) * mm});
            skLineSegment(sketch, "E3017", {"start": v(7.63, 2.61) * mm, "end": v(7.65, 2.66) * mm});
            skLineSegment(sketch, "E3018", {"start": v(7.65, 2.66) * mm, "end": v(7.67, 2.7) * mm});
            skLineSegment(sketch, "E3019", {"start": v(7.67, 2.7) * mm, "end": v(7.69, 2.73) * mm});
            skLineSegment(sketch, "E3020", {"start": v(7.69, 2.73) * mm, "end": v(7.72, 2.79) * mm});
            skLineSegment(sketch, "E3021", {"start": v(7.72, 2.79) * mm, "end": v(7.75, 2.85) * mm});
            skLineSegment(sketch, "E3022", {"start": v(7.75, 2.85) * mm, "end": v(7.76, 2.9) * mm});
            skLineSegment(sketch, "E3023", {"start": v(7.76, 2.9) * mm, "end": v(7.77, 2.92) * mm});
            skLineSegment(sketch, "E3024", {"start": v(7.77, 2.92) * mm, "end": v(7.75, 2.93) * mm});
            skLineSegment(sketch, "E3025", {"start": v(7.75, 2.93) * mm, "end": v(7.72, 2.93) * mm});
            skLineSegment(sketch, "E3026", {"start": v(7.72, 2.93) * mm, "end": v(7.67, 2.93) * mm});
            skLineSegment(sketch, "E3027", {"start": v(7.67, 2.93) * mm, "end": v(7.59, 2.93) * mm});
            skLineSegment(sketch, "E3028", {"start": v(7.59, 2.93) * mm, "end": v(7.3, 2.92) * mm});
            skLineSegment(sketch, "E3029", {"start": v(7.3, 2.92) * mm, "end": v(7.03, 2.88) * mm});
            skLineSegment(sketch, "E3030", {"start": v(7.03, 2.88) * mm, "end": v(6.79, 2.82) * mm});
            skLineSegment(sketch, "E3031", {"start": v(6.79, 2.82) * mm, "end": v(6.57, 2.73) * mm});
            skLineSegment(sketch, "E3032", {"start": v(6.57, 2.73) * mm, "end": v(6.5, 2.7) * mm});
            skLineSegment(sketch, "E3033", {"start": v(6.5, 2.7) * mm, "end": v(6.43, 2.65) * mm});
            skLineSegment(sketch, "E3034", {"start": v(6.43, 2.65) * mm, "end": v(6.34, 2.59) * mm});
            skLineSegment(sketch, "E3035", {"start": v(6.34, 2.59) * mm, "end": v(6.25, 2.53) * mm});
            skLineSegment(sketch, "E3036", {"start": v(6.25, 2.53) * mm, "end": v(6.15, 2.46) * mm});
            skLineSegment(sketch, "E3037", {"start": v(6.15, 2.46) * mm, "end": v(6.07, 2.4) * mm});
            skLineSegment(sketch, "E3038", {"start": v(6.07, 2.4) * mm, "end": v(6, 2.35) * mm});
            skLineSegment(sketch, "E3039", {"start": v(6, 2.35) * mm, "end": v(5.95, 2.3) * mm});
            skLineSegment(sketch, "E3040", {"start": v(5.95, 2.3) * mm, "end": v(5.9, 2.26) * mm});
            skLineSegment(sketch, "E3041", {"start": v(5.9, 2.26) * mm, "end": v(5.84, 2.21) * mm});
            skLineSegment(sketch, "E3042", {"start": v(5.84, 2.21) * mm, "end": v(5.78, 2.16) * mm});
            skLineSegment(sketch, "E3043", {"start": v(5.78, 2.16) * mm, "end": v(5.73, 2.1) * mm});
            skLineSegment(sketch, "E3044", {"start": v(5.73, 2.1) * mm, "end": v(5.64, 2.02) * mm});
            skLineSegment(sketch, "E3045", {"start": v(5.64, 2.02) * mm, "end": v(5.56, 1.96) * mm});
            skLineSegment(sketch, "E3046", {"start": v(5.56, 1.96) * mm, "end": v(5.48, 1.9) * mm});
            skLineSegment(sketch, "E3047", {"start": v(5.48, 1.9) * mm, "end": v(5.4, 1.85) * mm});
            skLineSegment(sketch, "E3048", {"start": v(5.4, 1.85) * mm, "end": v(5.35, 1.83) * mm});
            skLineSegment(sketch, "E3049", {"start": v(5.35, 1.83) * mm, "end": v(5.32, 1.81) * mm});
            skLineSegment(sketch, "E3050", {"start": v(5.32, 1.81) * mm, "end": v(5.3, 1.8) * mm});
            skLineSegment(sketch, "E3051", {"start": v(5.3, 1.8) * mm, "end": v(5.29, 1.79) * mm});
            skLineSegment(sketch, "E3052", {"start": v(5.29, 1.79) * mm, "end": v(5.3, 1.78) * mm});
            skLineSegment(sketch, "E3053", {"start": v(5.3, 1.78) * mm, "end": v(5.32, 1.78) * mm});
            skLineSegment(sketch, "E3054", {"start": v(5.32, 1.78) * mm, "end": v(5.36, 1.78) * mm});
            skLineSegment(sketch, "E3055", {"start": v(5.36, 1.78) * mm, "end": v(5.43, 1.8) * mm});
            skLineSegment(sketch, "E3056", {"start": v(-7.03, 2.29) * mm, "end": v(-7.06, 2.29) * mm});
            skLineSegment(sketch, "E3057", {"start": v(-7.06, 2.29) * mm, "end": v(-7.08, 2.29) * mm});
            skLineSegment(sketch, "E3058", {"start": v(-7.08, 2.29) * mm, "end": v(-7.09, 2.28) * mm});
            skLineSegment(sketch, "E3059", {"start": v(-7.09, 2.28) * mm, "end": v(-7.06, 2.28) * mm});
            skLineSegment(sketch, "E3060", {"start": v(-7.06, 2.28) * mm, "end": v(-7.03, 2.28) * mm});
            skLineSegment(sketch, "E3061", {"start": v(-7.03, 2.28) * mm, "end": v(-7.03, 2.29) * mm});
            skLineSegment(sketch, "E3062", {"start": v(0.3, 2.38) * mm, "end": v(0.32, 2.41) * mm});
            skLineSegment(sketch, "E3063", {"start": v(0.32, 2.41) * mm, "end": v(0.34, 2.44) * mm});
            skLineSegment(sketch, "E3064", {"start": v(0.34, 2.44) * mm, "end": v(0.35, 2.46) * mm});
            skLineSegment(sketch, "E3065", {"start": v(0.35, 2.46) * mm, "end": v(0.35, 2.48) * mm});
            skLineSegment(sketch, "E3066", {"start": v(0.35, 2.48) * mm, "end": v(0.35, 2.48) * mm});
            skLineSegment(sketch, "E3067", {"start": v(0.35, 2.48) * mm, "end": v(0.34, 2.46) * mm});
            skLineSegment(sketch, "E3068", {"start": v(0.34, 2.46) * mm, "end": v(0.32, 2.44) * mm});
            skLineSegment(sketch, "E3069", {"start": v(0.32, 2.44) * mm, "end": v(0.3, 2.4) * mm});
            skLineSegment(sketch, "E3070", {"start": v(0.3, 2.4) * mm, "end": v(0.28, 2.37) * mm});
            skLineSegment(sketch, "E3071", {"start": v(0.28, 2.37) * mm, "end": v(0.27, 2.33) * mm});
            skLineSegment(sketch, "E3072", {"start": v(0.27, 2.33) * mm, "end": v(0.26, 2.31) * mm});
            skLineSegment(sketch, "E3073", {"start": v(0.26, 2.31) * mm, "end": v(0.25, 2.3) * mm});
            skLineSegment(sketch, "E3074", {"start": v(0.25, 2.3) * mm, "end": v(0.25, 2.3) * mm});
            skLineSegment(sketch, "E3075", {"start": v(0.25, 2.3) * mm, "end": v(0.26, 2.3) * mm});
            skLineSegment(sketch, "E3076", {"start": v(0.26, 2.3) * mm, "end": v(0.28, 2.33) * mm});
            skLineSegment(sketch, "E3077", {"start": v(0.28, 2.33) * mm, "end": v(0.3, 2.38) * mm});
            skLineSegment(sketch, "E3078", {"start": v(-7.96, 2.54) * mm, "end": v(-7.97, 2.55) * mm});
            skLineSegment(sketch, "E3079", {"start": v(-7.97, 2.55) * mm, "end": v(-7.99, 2.56) * mm});
            skLineSegment(sketch, "E3080", {"start": v(-7.99, 2.56) * mm, "end": v(-8, 2.55) * mm});
            skLineSegment(sketch, "E3081", {"start": v(-8, 2.55) * mm, "end": v(-7.98, 2.54) * mm});
            skLineSegment(sketch, "E3082", {"start": v(-7.98, 2.54) * mm, "end": v(-7.97, 2.54) * mm});
            skLineSegment(sketch, "E3083", {"start": v(-7.97, 2.54) * mm, "end": v(-7.95, 2.53) * mm});
            skLineSegment(sketch, "E3084", {"start": v(-7.95, 2.53) * mm, "end": v(-7.95, 2.54) * mm});
            skLineSegment(sketch, "E3085", {"start": v(-7.95, 2.54) * mm, "end": v(-7.96, 2.54) * mm});
            skLineSegment(sketch, "E3086", {"start": v(0.46, 3.03) * mm, "end": v(0.46, 3.04) * mm});
            skLineSegment(sketch, "E3087", {"start": v(0.46, 3.04) * mm, "end": v(0.45, 3.04) * mm});
            skLineSegment(sketch, "E3088", {"start": v(0.45, 3.04) * mm, "end": v(0.45, 3.03) * mm});
            skLineSegment(sketch, "E3089", {"start": v(0.45, 3.03) * mm, "end": v(0.46, 3.02) * mm});
            skLineSegment(sketch, "E3090", {"start": v(0.46, 3.02) * mm, "end": v(0.46, 3) * mm});
            skLineSegment(sketch, "E3091", {"start": v(0.46, 3) * mm, "end": v(0.47, 3) * mm});
            skLineSegment(sketch, "E3092", {"start": v(0.47, 3) * mm, "end": v(0.47, 3.01) * mm});
            skLineSegment(sketch, "E3093", {"start": v(0.47, 3.01) * mm, "end": v(0.46, 3.03) * mm});
            skLineSegment(sketch, "E3094", {"start": v(-0.76, 3.09) * mm, "end": v(-0.75, 3.1) * mm});
            skLineSegment(sketch, "E3095", {"start": v(-0.75, 3.1) * mm, "end": v(-0.76, 3.1) * mm});
            skLineSegment(sketch, "E3096", {"start": v(-0.76, 3.1) * mm, "end": v(-0.78, 3.08) * mm});
            skLineSegment(sketch, "E3097", {"start": v(-0.78, 3.08) * mm, "end": v(-0.78, 3.07) * mm});
            skLineSegment(sketch, "E3098", {"start": v(-0.78, 3.07) * mm, "end": v(-0.78, 3.07) * mm});
            skLineSegment(sketch, "E3099", {"start": v(-0.78, 3.07) * mm, "end": v(-0.76, 3.09) * mm});
            skSolve(sketch);
        }
        {
            var Q0;
            Q0=makeQuery(id+"F0.imprint","IMPRINT",FACE,{"disambiguationData":[TD([[makeQuery(id+"F0.imprint","IMPRINT",EDGE,{"derivedFrom":sQuery(id+"F0.wireOp",EDGE,"E0")}),-1.0]])]});
            extrude(context, id + "F1", {"entities" : qUnion([Q0]), "depth" : 2 * mm});
        }
        {
            var Q0;
            Q0=makeQuery(id+"F0.imprint","IMPRINT",FACE,{"disambiguationData":[TD([[makeQuery(id+"F0.imprint","IMPRINT",EDGE,{"derivedFrom":sQuery(id+"F0.wireOp",EDGE,"E2740")}),1.0]])]});
            var Q1;
            Q1=makeQuery(id+"F0.imprint","IMPRINT",FACE,{"disambiguationData":[TD([[makeQuery(id+"F0.imprint","IMPRINT",EDGE,{"derivedFrom":sQuery(id+"F0.wireOp",EDGE,"E2810")}),1.0]])]});
            var Q2;
            Q2=makeQuery(id+"F0.imprint","IMPRINT",FACE,{"disambiguationData":[TD([[makeQuery(id+"F0.imprint","IMPRINT",EDGE,{"derivedFrom":sQuery(id+"F0.wireOp",EDGE,"E2548")}),1.0]])]});
            var Q3;
            Q3=makeQuery(id+"F0.imprint","IMPRINT",FACE,{"disambiguationData":[TD([[makeQuery(id+"F0.imprint","IMPRINT",EDGE,{"derivedFrom":sQuery(id+"F0.wireOp",EDGE,"E2488")}),1.0]])]});
            var Q4;
            Q4=makeQuery(id+"F0.imprint","IMPRINT",FACE,{"disambiguationData":[TD([[makeQuery(id+"F0.imprint","IMPRINT",EDGE,{"derivedFrom":sQuery(id+"F0.wireOp",EDGE,"E2216")}),1.0]])]});
            var Q5;
            Q5=makeQuery(id+"F0.imprint","IMPRINT",FACE,{"disambiguationData":[TD([[makeQuery(id+"F0.imprint","IMPRINT",EDGE,{"derivedFrom":sQuery(id+"F0.wireOp",EDGE,"E2376")}),1.0]])]});
            var Q6;
            Q6=makeQuery(id+"F0.imprint","IMPRINT",FACE,{"disambiguationData":[TD([[makeQuery(id+"F0.imprint","IMPRINT",EDGE,{"derivedFrom":sQuery(id+"F0.wireOp",EDGE,"E1862")}),1.0]])]});
            var Q7;
            Q7=makeQuery(id+"F0.imprint","IMPRINT",FACE,{"disambiguationData":[TD([[makeQuery(id+"F0.imprint","IMPRINT",EDGE,{"derivedFrom":sQuery(id+"F0.wireOp",EDGE,"E1929")}),1.0]])]});
            var Q8;
            Q8=makeQuery(id+"F0.imprint","IMPRINT",FACE,{"disambiguationData":[TD([[makeQuery(id+"F0.imprint","IMPRINT",EDGE,{"derivedFrom":sQuery(id+"F0.wireOp",EDGE,"E1550")}),1.0]])]});
            var Q9;
            Q9=makeQuery(id+"F0.imprint","IMPRINT",FACE,{"disambiguationData":[TD([[makeQuery(id+"F0.imprint","IMPRINT",EDGE,{"derivedFrom":sQuery(id+"F0.wireOp",EDGE,"E1310")}),1.0]])]});
            var Q10;
            Q10=makeQuery(id+"F0.imprint","IMPRINT",FACE,{"disambiguationData":[TD([[makeQuery(id+"F0.imprint","IMPRINT",EDGE,{"derivedFrom":sQuery(id+"F0.wireOp",EDGE,"E1404")}),1.0]])]});
            var Q11;
            Q11=makeQuery(id+"F0.imprint","IMPRINT",FACE,{"disambiguationData":[TD([[makeQuery(id+"F0.imprint","IMPRINT",EDGE,{"derivedFrom":sQuery(id+"F0.wireOp",EDGE,"E986")}),1.0]])]});
            var Q12;
            Q12=makeQuery(id+"F0.imprint","IMPRINT",FACE,{"disambiguationData":[TD([[makeQuery(id+"F0.imprint","IMPRINT",EDGE,{"derivedFrom":sQuery(id+"F0.wireOp",EDGE,"E1016")}),1.0]])]});
            var Q13;
            Q13=makeQuery(id+"F0.imprint","IMPRINT",FACE,{"disambiguationData":[TD([[makeQuery(id+"F0.imprint","IMPRINT",EDGE,{"derivedFrom":sQuery(id+"F0.wireOp",EDGE,"E1054")}),1.0]])]});
            var Q14;
            Q14=makeQuery(id+"F0.imprint","IMPRINT",FACE,{"disambiguationData":[TD([[makeQuery(id+"F0.imprint","IMPRINT",EDGE,{"derivedFrom":sQuery(id+"F0.wireOp",EDGE,"E1084")}),1.0]])]});
            var Q15;
            Q15=makeQuery(id+"F0.imprint","IMPRINT",FACE,{"disambiguationData":[TD([[makeQuery(id+"F0.imprint","IMPRINT",EDGE,{"derivedFrom":sQuery(id+"F0.wireOp",EDGE,"E1620")}),1.0]])]});
            var Q16;
            Q16=makeQuery(id+"F0.imprint","IMPRINT",FACE,{"disambiguationData":[TD([[makeQuery(id+"F0.imprint","IMPRINT",EDGE,{"derivedFrom":sQuery(id+"F0.wireOp",EDGE,"E2007")}),1.0]])]});
            var Q17;
            Q17=makeQuery(id+"F0.imprint","IMPRINT",FACE,{"disambiguationData":[TD([[makeQuery(id+"F0.imprint","IMPRINT",EDGE,{"derivedFrom":sQuery(id+"F0.wireOp",EDGE,"E2442")}),1.0]])]});
            var Q18;
            Q18=makeQuery(id+"F0.imprint","IMPRINT",FACE,{"disambiguationData":[TD([[makeQuery(id+"F0.imprint","IMPRINT",EDGE,{"derivedFrom":sQuery(id+"F0.wireOp",EDGE,"E2906")}),1.0]])]});
            var Q19;
            Q19=makeQuery(id+"F0.imprint","IMPRINT",FACE,{"disambiguationData":[TD([[makeQuery(id+"F0.imprint","IMPRINT",EDGE,{"derivedFrom":sQuery(id+"F0.wireOp",EDGE,"E2284")}),1.0]])]});
            var Q20;
            Q20=makeQuery(id+"F0.imprint","IMPRINT",FACE,{"disambiguationData":[TD([[makeQuery(id+"F0.imprint","IMPRINT",EDGE,{"derivedFrom":sQuery(id+"F0.wireOp",EDGE,"E2073")}),1.0]])]});
            var Q21;
            Q21=makeQuery(id+"F0.imprint","IMPRINT",FACE,{"disambiguationData":[TD([[makeQuery(id+"F0.imprint","IMPRINT",EDGE,{"derivedFrom":sQuery(id+"F0.wireOp",EDGE,"E2662")}),1.0]])]});
            var Q22;
            Q22=makeQuery(id+"F0.imprint","IMPRINT",FACE,{"disambiguationData":[TD([[makeQuery(id+"F0.imprint","IMPRINT",EDGE,{"derivedFrom":sQuery(id+"F0.wireOp",EDGE,"E2147")}),1.0]])]});
            var Q23;
            Q23=makeQuery(id+"F0.imprint","IMPRINT",FACE,{"disambiguationData":[TD([[makeQuery(id+"F0.imprint","IMPRINT",EDGE,{"derivedFrom":sQuery(id+"F0.wireOp",EDGE,"E2608")}),1.0]])]});
            var Q24;
            Q24=makeQuery(id+"F0.imprint","IMPRINT",FACE,{"disambiguationData":[TD([[makeQuery(id+"F0.imprint","IMPRINT",EDGE,{"derivedFrom":sQuery(id+"F0.wireOp",EDGE,"E3000")}),1.0]])]});
            var Q25;
            Q25=makeQuery(id+"F0.imprint","IMPRINT",FACE,{"disambiguationData":[TD([[makeQuery(id+"F0.imprint","IMPRINT",EDGE,{"derivedFrom":sQuery(id+"F0.wireOp",EDGE,"E1780")}),1.0]])]});
            var Q26;
            Q26=makeQuery(id+"F0.imprint","IMPRINT",FACE,{"disambiguationData":[TD([[makeQuery(id+"F0.imprint","IMPRINT",EDGE,{"derivedFrom":sQuery(id+"F0.wireOp",EDGE,"E1144")}),1.0]])]});
            var Q27;
            Q27=makeQuery(id+"F0.imprint","IMPRINT",FACE,{"disambiguationData":[TD([[makeQuery(id+"F0.imprint","IMPRINT",EDGE,{"derivedFrom":sQuery(id+"F0.wireOp",EDGE,"E1222")}),1.0]])]});
            var Q28;
            Q28=makeQuery(id+"F0.imprint","IMPRINT",FACE,{"disambiguationData":[TD([[makeQuery(id+"F0.imprint","IMPRINT",EDGE,{"derivedFrom":sQuery(id+"F0.wireOp",EDGE,"E1688")}),1.0]])]});
            var Q29;
            Q29=makeQuery(id+"F0.imprint","IMPRINT",FACE,{"disambiguationData":[TD([[makeQuery(id+"F0.imprint","IMPRINT",EDGE,{"derivedFrom":sQuery(id+"F0.wireOp",EDGE,"E1470")}),1.0]])]});
            extrude(context, id + "F2", {"entities" : qUnion([Q0, Q1, Q2, Q3, Q4, Q5, Q6, Q7, Q8, Q9, Q10, Q11, Q12, Q13, Q14, Q15, Q16, Q17, Q18, Q19, Q20, Q21, Q22, Q23, Q24, Q25, Q26, Q27, Q28, Q29]), "operationType" : NewBodyOperationType.ADD, "depth" : 2.5 * mm});
        }
        {
            var Q0;
            Q0=qCreatedBy(makeId("Top.planeOp"),FACE);
            var sketch = newSketch(context, id + "F3", { "sketchPlane" : qUnion([Q0])});
            skCircle(sketch, "E3100", {"center": v(-0.17, -6.72) * mm, "radius": 0.75 * mm});
            skCircle(sketch, "E3101", {"center": v(-0.17, -6.72) * mm, "radius": 1.25 * mm});
            skSolve(sketch);
        }
        {
            var Q0;
            Q0=makeQuery(id+"F3.imprint","IMPRINT",FACE,{"disambiguationData":[TD([[makeQuery(id+"F3.imprint","IMPRINT",EDGE,{"derivedFrom":sQuery(id+"F3.wireOp",EDGE,"E3100")}),-1.0]])]});
            extrude(context, id + "F4", {"entities" : qUnion([Q0]), "operationType" : NewBodyOperationType.ADD, "depth" : 2.5 * mm});
        }
    });
